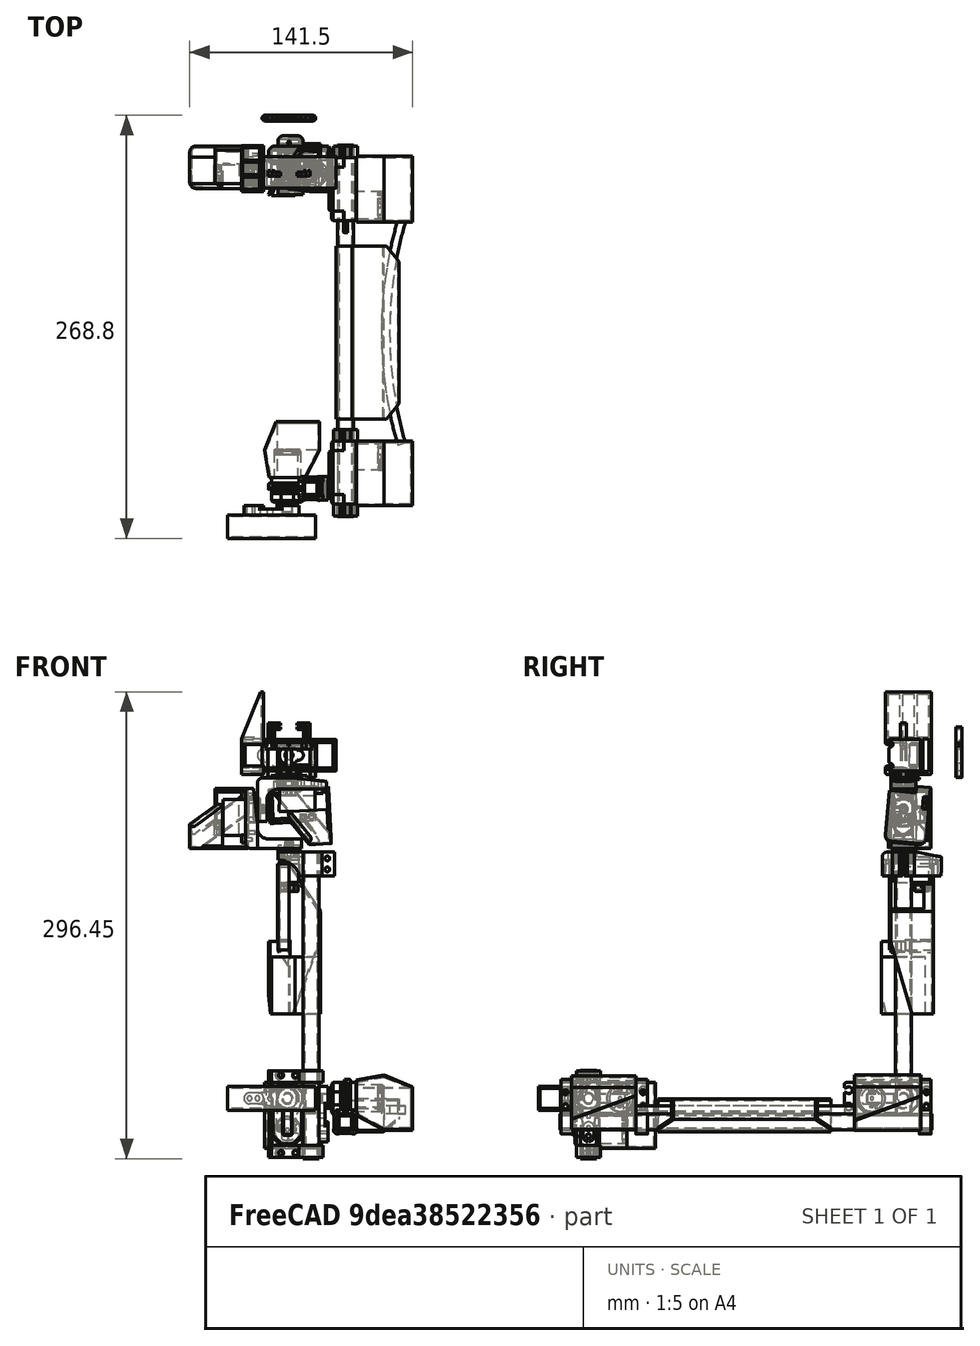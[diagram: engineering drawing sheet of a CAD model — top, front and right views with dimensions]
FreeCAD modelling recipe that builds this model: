
FCSTD DOCUMENT  (FreeCAD 0.19R22366 (Git))
Label: CompleteRobot
License: All rights reserved
LicenseURL: http://en.wikipedia.org/wiki/All_rights_reserved
objects: Sketcher::SketchObject×308, PartDesign::Pad×171, PartDesign::Pocket×133, PartDesign::Body×89, PartDesign::FeatureBase×47, PartDesign::Fillet×35, PartDesign::Mirrored×23, App::Part×12, PartDesign::Chamfer×10, PartDesign::PolarPattern×8, Part::Mirroring×8, PartDesign::Plane×7, PartDesign::MultiTransform×6, App::DocumentObjectGroup×4, PartDesign::Revolution×2, PartDesign::AdditiveLoft×1
note: 1200 computed .brp shape members not serialized (recipe doc carries the construction recipe); baked Part::Feature solids carry a one-line shape summary decoded from their .brp

FEATURE [Sketcher::SketchObject] Sketch
  MapMode = 5
  Support = -> [XY_Plane]
  constraints (7):
    c: Coincident(g0,g-1)
    c: PointOnObject(g1,g-1)
    c: Coincident(g1,g0)
    c: Coincident(g1,g0)
    c: Vertical(g1,g0)
    c: Diameter(g0) = 11.8
    c: Diameter(g1) = 5.5
FEATURE [PartDesign::Pad] Pad
  Length = 5.7
  Length2 = 100
  Profile = -> Sketch
  Refine = true
  Reversed = true
  Type = 0
FEATURE [Sketcher::SketchObject] Sketch001
  ExternalGeometry = -> [Pad]
  MapMode = 5
  Placement = pos=(0,0,-5.7) rot=(1,0,0;3.14159rad)
  Support = -> [Pad]
  constraints (11):
    c: Coincident(g0,g1)
    c: Coincident(g1,g2)
    c: Coincident(g2,g3)
    c: Coincident(g3,g0)
    c: Horizontal(g0)
    c: Horizontal(g2)
    c: Vertical(g3)
    c: Symmetric(g0,g1,g-1)
    c: Distance(g1) = 12
    c: DistanceX(g-1,g0) = 6
    c: Distance(g2) = 22.6
FEATURE [PartDesign::Plane] DatumPlane
  AttachmentOffset = pos=(0,0,16) rot=(0,0,1;0rad)
  Length = 60
  MapMode = 5
  Placement = pos=(0,0,-21.7) rot=(1,0,0;3.14159rad)
  ResizeMode = 0
  Support = -> [Pad]
  Width = 60
FEATURE [Sketcher::SketchObject] Sketch002
  ExternalGeometry = -> [Sketch001]
  MapMode = 5
  Placement = pos=(0,0,-21.7) rot=(1,0,0;3.14159rad)
  Support = -> [DatumPlane]
  constraints (18):
    c: Coincident(g0,g1)
    c: Coincident(g1,g2)
    c: Coincident(g2,g3)
    c: Coincident(g3,g0)
    c: Horizontal(g0)
    c: Horizontal(g2)
    c: Vertical(g3)
    c: Distance(g1) = 12.3
    c: Distance(g2) = 22.9
    c: PointOnObject(g4,g-1)
    c: PointOnObject(g5,g-3)
    c: Coincident(g5,g4)
    c: Horizontal(g5)
    c: PointOnObject(g4,g-4)
    c: Equal(g5,g4)
    c: Symmetric(g0,g1,g4)
    c: Horizontal(g4)
    c: Vertical(g1)
FEATURE [PartDesign::AdditiveLoft] AdditiveLoft
  BaseFeature = -> Pad
  Closed = false
  Profile = -> Sketch001
  Refine = true
  Ruled = false
  Sections = -> [Sketch002]
FEATURE [PartDesign::Plane] DatumPlane001
  AttachmentOffset = pos=(0,0,-1.7) rot=(0,0,1;0rad)
  Length = 60
  MapMode = 5
  Placement = pos=(0,0,-7.4) rot=(0,0,1;0rad)
  ResizeMode = 0
  Support = -> [AdditiveLoft]
  Width = 60
FEATURE [Sketcher::SketchObject] Sketch003
  ExternalGeometry = -> [AdditiveLoft]
  MapMode = 5
  Placement = pos=(0,0,-7.4) rot=(0,0,1;0rad)
  Support = -> [DatumPlane001]
  constraints (46):
    c: Coincident(g1,g2)
    c: Coincident(g2,g0)
    c: Horizontal(g0)
    c: Horizontal(g1)
    c: Coincident(g0,g-3)
    c: Coincident(g1,g-3)
    c: Distance(g0) = 5
    c: Coincident(g3,g4)
    c: Coincident(g4,g5)
    c: Horizontal(g3)
    c: Horizontal(g5)
    c: Coincident(g4,g-4)
    c: Coincident(g3,g-4)
    c: Equal(g3,g0)
    c: PointOnObject(g6,g-1)
    c: PointOnObject(g7,g-1)
    c: Vertical(g7,g7)
    c: Vertical(g6,g6)
    c: Coincident(g8,g7)
    c: Horizontal(g8)
    c: Coincident(g9,g8)
    c: Coincident(g9,g3)
    c: Coincident(g10,g7)
    c: Horizontal(g10)
    c: Coincident(g11,g10)
    c: Coincident(g11,g5)
    c: Vertical(g11)
    c: Vertical(g9)
    c: Vertical(g5,g3)
    c: Vertical(g0,g1)
    c: Coincident(g12,g6)
    c: Horizontal(g12)
    c: Coincident(g13,g0)
    c: Coincident(g13,g12)
    c: Coincident(g14,g1)
    c: Vertical(g14)
    c: Coincident(g15,g6)
    c: Horizontal(g15)
    c: Coincident(g14,g15)
    c: Vertical(g13)
    c: Equal(g6,g7)
    c: Equal(g12,g8)
    c: Diameter(g6) = 2
    c: Distance(g12) = 1.3
    c: DistanceY(g14,g12) = 1.2
    c: Horizontal(g7,g6)
FEATURE [PartDesign::Pad] Pad001
  BaseFeature = -> AdditiveLoft
  Length = 2.6
  Length2 = 100
  Profile = -> Sketch003
  Refine = true
  Reversed = true
  Type = 0
FEATURE [Sketcher::SketchObject] Sketch004
  MapMode = 5
  Support = -> [Pad001]
FEATURE [Sketcher::SketchObject] Sketch005
  MapMode = 5
  Support = -> [XY_Plane]
  constraints (2):
    c: Coincident(g0,g-1)
    c: Diameter(g0) = 4.95
FEATURE [PartDesign::Pad] Pad002
  BaseFeature = -> Pad001
  Length = 4.45
  Length2 = 100
  Profile = -> Sketch005
  Refine = true
  Type = 0
FEATURE [PartDesign::Chamfer] Chamfer
  Angle = 45
  Base = -> Pad002 [Edge69]
  BaseFeature = -> Pad002
  ChamferType = 1
  FlipDirection = false
  Refine = true
  Size = 0.45
  Size2 = 0.4
  SupportTransform = false
  expr: Size2 = (4.95 - 4.15) / 2
FEATURE [Sketcher::SketchObject] Sketch006
  ExternalGeometry = -> [Chamfer]
  MapMode = 5
  Support = -> [XY_Plane]
  expr: Constraints[4] = (4.95 - 4) / 2
  expr: Constraints[16] = 360 / 20
  constraints (25):
    c: PointOnObject(g0,g-3)
    c: Symmetric(g0,g1,g-1)
    c: PointOnObject(g2,g-1)
    c: PointOnObject(g2,g-3)
    c: DistanceX(g0,g2) = 0.475
    c: Coincident(g3,g0)
    c: Coincident(g3,g1)
    c: Symmetric(g0,g1,g-1)
    c: Distance(g3) = 0.12
    c: Coincident(g4,g0)
    c: PointOnObject(g4,g-3)
    c: Equal(g4,g3)
    c: Coincident(g5,g1)
    c: Coincident(g5,g-1)
    c: Coincident(g6,g-1)
    c: Coincident(g6,g4)
    c: Angle(g5,g6) = 0.314159
    c: Coincident(g7,g4)
    c: Coincident(g8,g1)
    c: Parallel(g7,g6)
    c: Parallel(g8,g5)
    c: Coincident(g9,g-1)
    c: Coincident(g9,g7)
    c: Coincident(g9,g8)
    c: Distance(g7) = 0.1
FEATURE [PartDesign::Pocket] Pocket
  BaseFeature = -> Chamfer
  Length = 5
  Length2 = 100
  Profile = -> Sketch006
  Refine = true
  Reversed = true
  Type = 1
FEATURE [PartDesign::PolarPattern] PolarPattern
  Angle = 360
  Axis = -> Sketch006 [N_Axis]
  BaseFeature = -> Pocket
  Occurrences = 20
  Originals = -> [Pocket]
  Refine = true
FEATURE [Sketcher::SketchObject] Sketch007
  MapMode = 5
  Placement = pos=(0,0,4.45) rot=(0,0,1;0rad)
  Support = -> [PolarPattern]
  constraints (2):
    c: Coincident(g0,g-1)
    c: Diameter(g0) = 2
FEATURE [PartDesign::Pocket] Pocket001
  BaseFeature = -> PolarPattern
  Length = 4
  Length2 = 100
  Profile = -> Sketch007
  Refine = true
  Type = 0
FEATURE [PartDesign::Fillet] Fillet
  Base = -> Pocket001 [Edge3,Edge5]
  BaseFeature = -> Pocket001
  Radius = 0.4
  Refine = true
  SupportTransform = false
FEATURE [Sketcher::SketchObject] Sketch008
  ExternalGeometry = -> [Fillet]
  MapMode = 5
  Placement = pos=(0,0,-21.7) rot=(1,0,0;3.14159rad)
  Support = -> [Fillet]
  constraints (18):
    c: Coincident(g0,g1)
    c: Coincident(g1,g2)
    c: Coincident(g2,g3)
    c: Coincident(g3,g0)
    c: Horizontal(g2)
    c: Vertical(g3)
    c: Coincident(g4,g-3)
    c: Coincident(g4,g-4)
    c: Vertical(g1)
    c: PointOnObject(g5,g4)
    c: PointOnObject(g5,g-1)
    c: PointOnObject(g6,g0)
    c: PointOnObject(g6,g2)
    c: PointOnObject(g5,g6)
    c: Symmetric(g6,g6,g-1)
    c: Symmetric(g0,g0,g6)
    c: Distance(g0) = 22
    c: Distance(g1) = 11.4
FEATURE [PartDesign::Pocket] Pocket002
  BaseFeature = -> Fillet
  Length = 10
  Length2 = 100
  Profile = -> Sketch008
  Refine = true
  Type = 0
FEATURE [PartDesign::Body] Body
  Group = -> [Sketch,Pad,Sketch001,DatumPlane,Sketch002,AdditiveLoft,DatumPlane001,Sketch003,Pad001,Sketch004,Sketch005,Pad002,Chamfer,Sketch006,Pocket,PolarPattern,Sketch007,Pocket001,Fillet,Sketch008,Pocket002]
  Origin = -> Origin
  Tip = -> Pocket002
FEATURE [PartDesign::FeatureBase] Clone
  BaseFeature = -> Body
FEATURE [PartDesign::Body] Body001
  BaseFeature = -> Body
  Group = -> [Clone]
  Origin = -> Origin001
  Placement = pos=(0,0,0) rot=(0,0,1;3.14159rad)
  Tip = -> Clone
FEATURE [PartDesign::FeatureBase] Clone001
  BaseFeature = -> Body
FEATURE [PartDesign::Body] Body002
  BaseFeature = -> Body
  Group = -> [Clone001]
  Origin = -> Origin002
  Placement = pos=(-20,0,-20) rot=(0.707107,0,0.707107;3.14159rad)
  Tip = -> Clone001
FEATURE [PartDesign::FeatureBase] Clone002
  BaseFeature = -> Body
FEATURE [PartDesign::Body] Body003
  BaseFeature = -> Body
  Group = -> [Clone002]
  Origin = -> Origin003
  Placement = pos=(0,0,-45) rot=(0,0,-1;1.5708rad)
  Tip = -> Clone002
FEATURE [Sketcher::SketchObject] Sketch009
  MapMode = 5
  Support = -> [XY_Plane004]
  expr: Constraints[2] = 11.8 + 4
  sketch-geometry (2):
    g0: Circle CenterX=0 CenterY=0 CenterZ=0 NormalX=0 NormalY=0 NormalZ=1 AngleXU=0 Radius=7.9
    g1: Circle CenterX=0 CenterY=0 CenterZ=0 NormalX=0 NormalY=0 NormalZ=1 AngleXU=0 Radius=2.55
  constraints (4):
    c: Coincident(g0,g-1)
    c: Coincident(g1,g0)
    c: Diameter(g0) = 15.8
    c: Diameter(g1) = 5.1
FEATURE [PartDesign::Pad] Pad003
  Length = 5
  Length2 = 100
  Profile = -> Sketch009
  Refine = true
  Type = 0
FEATURE [Sketcher::SketchObject] Sketch010
  ExternalGeometry = -> [Pad003]
  MapMode = 5
  Placement = pos=(0,0,5) rot=(0,0,1;0rad)
  Support = -> [Pad003]
  expr: Constraints[10] = 5.1 / 2 - 0.5 / 2
  expr: Constraints[16] = 360 / 20
  sketch-geometry (8):
    g0: ArcOfCircle CenterX=2.3 CenterY=0 CenterZ=0 NormalX=0 NormalY=0 NormalZ=1 AngleXU=0 Radius=0.2 StartAngle=1.57427 EndAngle=4.70891
    g1: LineSegment StartX=2.2993 StartY=0.199999 StartZ=0 EndX=2.3193 EndY=0.200068 EndZ=0
    g2: LineSegment StartX=2.2993 StartY=-0.199999 StartZ=0 EndX=2.3193 EndY=-0.200068 EndZ=0
    g3: ArcOfCircle CenterX=2.31861 CenterY=0.400067 CenterZ=0 NormalX=0 NormalY=0 NormalZ=1 AngleXU=0 Radius=0.2 StartAngle=4.71587 EndAngle=6.27739
    g4: ArcOfCircle CenterX=2.31861 CenterY=-0.400067 CenterZ=0 NormalX=0 NormalY=0 NormalZ=1 AngleXU=0 Radius=0.2 StartAngle=0.00579632 EndAngle=1.56732
    g5: LineSegment [constr] StartX=0 StartY=0 StartZ=0 EndX=2.51861 EndY=0.398908 EndZ=0
    g6: LineSegment [constr] StartX=0 StartY=0 StartZ=0 EndX=2.51861 EndY=-0.398908 EndZ=0
    g7: ArcOfCircle CenterX=0 CenterY=0 CenterZ=0 NormalX=0 NormalY=0 NormalZ=1 AngleXU=0 Radius=2.55 StartAngle=6.12611 EndAngle=6.44026
  constraints (21):
    c: PointOnObject(g0,g-1)
    c: Vertical(g0,g0)
    c: Diameter(g0) = 0.4
    c: Tangent(g2,g0) = -1.5708
    c: Tangent(g1,g0) = 1.5708
    c: PointOnObject(g4,g-3)
    c: Tangent(g4,g2) = 1.5708
    c: Tangent(g3,g1) = -1.5708
    c: Equal(g3,g0)
    c: Equal(g4,g0)
    c: DistanceX(g0) = 2.3
    c: Coincident(g5,g-1)
    c: Coincident(g5,g3)
    c: Coincident(g6,g-1)
    c: Coincident(g6,g4)
    c: Vertical(g4,g3)
    c: Angle(g6,g5) = 0.314159
    c: Coincident(g7,g-1)
    c: Coincident(g7,g3)
    c: Coincident(g7,g4)
    c: Distance(g1) = 0.02
FEATURE [PartDesign::Pad] Pad004
  BaseFeature = -> Pad003
  Length = 10
  Length2 = 100
  Profile = -> Sketch010
  Refine = true
  Reversed = true
  Type = 3
  UpToFace = -> Pad003 [Face3]
FEATURE [PartDesign::PolarPattern] PolarPattern001
  Angle = 360
  Axis = -> Sketch010 [N_Axis]
  BaseFeature = -> Pad004
  Occurrences = 20
  Originals = -> [Pad004]
  Refine = true
FEATURE [Sketcher::SketchObject] Sketch011
  ExternalGeometry = -> [PolarPattern001]
  MapMode = 5
  Placement = pos=(0,0,5) rot=(0,0,1;0rad)
  Support = -> [PolarPattern001]
  sketch-geometry (2):
    g0: Circle CenterX=0 CenterY=0 CenterZ=0 NormalX=0 NormalY=0 NormalZ=1 AngleXU=0 Radius=1.3
    g1: Circle CenterX=0 CenterY=0 CenterZ=0 NormalX=0 NormalY=0 NormalZ=1 AngleXU=0 Radius=7.9
  constraints (4):
    c: Coincident(g0,g-1)
    c: Diameter(g0) = 2.6
    c: Coincident(g1,g0)
    c: Equal(g-3,g1)
FEATURE [PartDesign::Pad] Pad005
  BaseFeature = -> PolarPattern001
  Length = 1
  Length2 = 100
  Profile = -> Sketch011
  Refine = true
  Type = 0
FEATURE [PartDesign::Plane] DatumPlane002
  AttachmentOffset = pos=(0,0,-20) rot=(0,0,1;0rad)
  Length = 61.225
  MapMode = 5
  Placement = pos=(-20,4.4e-15,-4.4e-15) rot=(0.57735,0.57735,0.57735;2.0944rad)
  ResizeMode = 0
  Support = -> [YZ_Plane004]
  Width = 74.225
FEATURE [Sketcher::SketchObject] Sketch012
  ExternalGeometry = -> [Pad005]
  MapMode = 5
  Placement = pos=(-20,4.4e-15,-4.4e-15) rot=(0.57735,0.57735,0.57735;2.0944rad)
  Support = -> [DatumPlane002]
  sketch-geometry (4):
    g0: LineSegment StartX=-7.9 StartY=6 StartZ=0 EndX=7.9 EndY=6 EndZ=0
    g1: LineSegment StartX=7.9 StartY=6 StartZ=0 EndX=7.9 EndY=0 EndZ=0
    g2: LineSegment StartX=7.9 StartY=0 StartZ=0 EndX=-7.9 EndY=0 EndZ=0
    g3: LineSegment StartX=-7.9 StartY=0 StartZ=0 EndX=-7.9 EndY=6 EndZ=0
  constraints (10):
    c: Coincident(g0,g1)
    c: Coincident(g1,g2)
    c: Coincident(g2,g3)
    c: Coincident(g3,g0)
    c: Horizontal(g0)
    c: Horizontal(g2)
    c: Vertical(g1)
    c: Vertical(g3)
    c: Symmetric(g2,g1,g-1)
    c: Coincident(g0,g-3)
FEATURE [PartDesign::Pad] Pad006
  BaseFeature = -> Pad005
  Length = 10
  Length2 = 100
  Profile = -> Sketch012
  Refine = true
  Type = 2
FEATURE [Sketcher::SketchObject] Sketch013
  MapMode = 5
  Placement = pos=(-20,0,0) rot=(0.57735,-0.57735,-0.57735;2.0944rad)
  Support = -> [Pad006]
  sketch-geometry (4):
    g0: LineSegment StartX=-8 StartY=0 StartZ=0 EndX=8 EndY=0 EndZ=0
    g1: LineSegment StartX=8 StartY=0 StartZ=0 EndX=8 EndY=38 EndZ=0
    g2: LineSegment StartX=8 StartY=38 StartZ=0 EndX=-8 EndY=38 EndZ=0
    g3: LineSegment StartX=-8 StartY=38 StartZ=0 EndX=-8 EndY=0 EndZ=0
  constraints (11):
    c: Coincident(g0,g1)
    c: Coincident(g1,g2)
    c: Coincident(g2,g3)
    c: Coincident(g3,g0)
    c: Horizontal(g0)
    c: Horizontal(g2)
    c: Vertical(g1)
    c: Vertical(g3)
    c: Symmetric(g0,g0,g-1)
    c: Distance(g2) = 16
    c: Distance(g1) = 38
FEATURE [PartDesign::Pad] Pad007
  BaseFeature = -> Pad006
  Length = 7.4
  Length2 = 100
  Profile = -> Sketch013
  Refine = true
  Type = 0
FEATURE [Sketcher::SketchObject] Sketch014
  MapMode = 5
  Placement = pos=(-20,0,0) rot=(0.57735,0.57735,0.57735;2.0944rad)
  Support = -> [Pad007]
  sketch-geometry (2):
    g0: ArcOfCircle CenterX=0 CenterY=25 CenterZ=0 NormalX=0 NormalY=0 NormalZ=1 AngleXU=0 Radius=6.3 StartAngle=5.23599 EndAngle=10.472
    g1: ArcOfCircle CenterX=0 CenterY=19.544 CenterZ=0 NormalX=0 NormalY=0 NormalZ=1 AngleXU=0 Radius=3.15 StartAngle=3.14159 EndAngle=6.28319
  constraints (8):
    c: PointOnObject(g0,g-2)
    c: PointOnObject(g1,g-2)
    c: Coincident(g1,g0)
    c: Coincident(g1,g0)
    c: Horizontal(g0,g1)
    c: Diameter(g0) = 12.6
    c: DistanceY(g0) = 25
    c: Diameter(g1) = 6.3
FEATURE [PartDesign::Pocket] Pocket003
  BaseFeature = -> Pad007
  Length = 5
  Length2 = 100
  Profile = -> Sketch014
  Refine = true
  Type = 1
FEATURE [Sketcher::SketchObject] Sketch015
  MapMode = 5
  Placement = pos=(-27.4,0,0) rot=(0.57735,-0.57735,-0.57735;2.0944rad)
  Support = -> [Pocket003]
  sketch-geometry (4):
    g0: LineSegment StartX=-6.405 StartY=31.9 StartZ=0 EndX=6.405 EndY=31.9 EndZ=0
    g1: LineSegment StartX=6.405 StartY=31.9 StartZ=0 EndX=6.405 EndY=7.9 EndZ=0
    g2: LineSegment StartX=6.405 StartY=7.9 StartZ=0 EndX=-6.405 EndY=7.9 EndZ=0
    g3: LineSegment StartX=-6.405 StartY=7.9 StartZ=0 EndX=-6.405 EndY=31.9 EndZ=0
  constraints (11):
    c: Coincident(g0,g1)
    c: Coincident(g1,g2)
    c: Coincident(g2,g3)
    c: Coincident(g3,g0)
    c: Horizontal(g2)
    c: Vertical(g1)
    c: Vertical(g3)
    c: Symmetric(g0,g0,g-2)
    c: Distance(g0) = 12.81
    c: Distance(g1) = 24
    c: DistanceY(g2) = 7.9
FEATURE [PartDesign::Pocket] Pocket004
  BaseFeature = -> Pocket003
  Length = 1.9
  Length2 = 100
  Profile = -> Sketch015
  Refine = true
  Type = 0
FEATURE [Sketcher::SketchObject] Sketch016
  MapMode = 5
  Placement = pos=(-27.4,0,0) rot=(0.57735,-0.57735,-0.57735;2.0944rad)
  Support = -> [Pocket004]
  sketch-geometry (2):
    g0: Circle CenterX=0 CenterY=33.9 CenterZ=0 NormalX=0 NormalY=0 NormalZ=1 AngleXU=0 Radius=1
    g1: Circle CenterX=0 CenterY=5.5 CenterZ=0 NormalX=0 NormalY=0 NormalZ=1 AngleXU=0 Radius=1
  constraints (6):
    c: PointOnObject(g0,g-2)
    c: PointOnObject(g1,g-2)
    c: Diameter(g0) = 2
    c: Equal(g1,g0)
    c: DistanceY(g1) = 5.5
    c: DistanceY(g1,g0) = 28.4
FEATURE [PartDesign::Pocket] Pocket005
  BaseFeature = -> Pocket004
  Length = 4
  Length2 = 100
  Profile = -> Sketch016
  Refine = true
  Type = 0
FEATURE [Sketcher::SketchObject] Sketch017
  ExternalGeometry = -> [Pocket005]
  MapMode = 5
  Placement = pos=(0,8,0) rot=(0,0.707107,0.707107;3.14159rad)
  Support = -> [Pocket005]
  sketch-geometry (3):
    g0: LineSegment StartX=20 StartY=15 StartZ=0 EndX=22.5 EndY=38 EndZ=0
    g1: LineSegment StartX=20 StartY=38 StartZ=0 EndX=22.5 EndY=38 EndZ=0
    g2: LineSegment StartX=20 StartY=38 StartZ=0 EndX=20 EndY=15 EndZ=0
  constraints (8):
    c: PointOnObject(g0,g-3)
    c: Coincident(g1,g-3)
    c: Coincident(g1,g0)
    c: Horizontal(g1)
    c: Coincident(g2,g1)
    c: Coincident(g2,g0)
    c: Distance(g1) = 2.5
    c: Distance(g2) = 23
FEATURE [PartDesign::Pocket] Pocket006
  BaseFeature = -> Pocket005
  Length = 5
  Length2 = 100
  Profile = -> Sketch017
  Refine = true
  Type = 1
FEATURE [PartDesign::Fillet] Fillet001
  Base = -> Pocket006 [Edge317]
  BaseFeature = -> Pocket006
  Radius = 10
  Refine = true
  SupportTransform = false
FEATURE [PartDesign::Chamfer] Chamfer001
  Angle = 45
  Base = -> Fillet001 [Edge21,Edge18]
  BaseFeature = -> Fillet001
  ChamferType = 0
  FlipDirection = false
  Refine = true
  Size = 0.05
  Size2 = 10
  SupportTransform = false
FEATURE [PartDesign::Fillet] Fillet002
  Base = -> Chamfer001 [Edge6]
  BaseFeature = -> Chamfer001
  Radius = 7
  Refine = true
  SupportTransform = false
FEATURE [PartDesign::Fillet] Fillet003
  Base = -> Fillet002 [Edge18]
  BaseFeature = -> Fillet002
  Radius = 3
  Refine = true
  SupportTransform = false
FEATURE [PartDesign::Fillet] Fillet004
  Base = -> Fillet003 [Edge114,Edge129]
  BaseFeature = -> Fillet003
  Radius = 6
  Refine = true
  SupportTransform = false
FEATURE [Sketcher::SketchObject] Sketch018
  ExternalGeometry = -> [Sketch015]
  MapMode = 5
  Placement = pos=(-25.5,0,0) rot=(0.57735,-0.57735,-0.57735;2.0944rad)
  Support = -> [Fillet004]
  sketch-geometry (10):
    g0: Circle CenterX=4.5 CenterY=29.9 CenterZ=0 NormalX=0 NormalY=0 NormalZ=1 AngleXU=0 Radius=1
    g1: Circle CenterX=-4.5 CenterY=29.9 CenterZ=0 NormalX=0 NormalY=0 NormalZ=1 AngleXU=0 Radius=1
    g2: Circle CenterX=4.5 CenterY=9.9 CenterZ=0 NormalX=0 NormalY=0 NormalZ=1 AngleXU=0 Radius=1
    g3: Circle CenterX=-4.5 CenterY=9.9 CenterZ=0 NormalX=0 NormalY=0 NormalZ=1 AngleXU=0 Radius=1
    g4: LineSegment [constr] StartX=-4.5 StartY=29.9 StartZ=0 EndX=4.5 EndY=29.9 EndZ=0
    g5: LineSegment [constr] StartX=-4.5 StartY=29.9 StartZ=0 EndX=-4.5 EndY=9.9 EndZ=0
    g6: LineSegment [constr] StartX=-4.5 StartY=9.9 StartZ=0 EndX=4.5 EndY=9.9 EndZ=0
    g7: LineSegment [constr] StartX=4.5 StartY=29.9 StartZ=0 EndX=4.5 EndY=9.9 EndZ=0
    g8: LineSegment [constr] StartX=-6.405 StartY=31.9 StartZ=0 EndX=0 EndY=19.9 EndZ=0
    g9: LineSegment [constr] StartX=0 StartY=19.9 StartZ=0 EndX=6.405 EndY=7.9 EndZ=0
  constraints (24):
    c: Diameter(g0) = 2
    c: Coincident(g4,g1)
    c: Coincident(g4,g0)
    c: Horizontal(g4)
    c: Coincident(g5,g1)
    c: Coincident(g5,g3)
    c: Vertical(g5)
    c: Coincident(g6,g3)
    c: Coincident(g6,g2)
    c: Horizontal(g6)
    c: Coincident(g7,g0)
    c: Coincident(g7,g2)
    c: Vertical(g7)
    c: Coincident(g8,g-3)
    c: Coincident(g9,g8)
    c: Coincident(g9,g-4)
    c: Equal(g8,g9)
    c: Parallel(g8,g9)
    c: Symmetric(g0,g3,g8)
    c: Distance(g5) = 20
    c: Distance(g4) = 9
    c: Equal(g1,g3)
    c: Equal(g3,g2)
    c: Equal(g2,g0)
FEATURE [PartDesign::Pocket] Pocket007
  BaseFeature = -> Fillet004
  Length = 4
  Length2 = 100
  Profile = -> Sketch018
  Refine = true
  Type = 0
FEATURE [Sketcher::SketchObject] Sketch020
  ExternalGeometry = -> [Pocket007]
  MapMode = 5
  Placement = pos=(0,0,-1.2e-15) rot=(1,0,0;3.14159rad)
  Support = -> [Pocket007]
  sketch-geometry (1):
    g0: Circle CenterX=0 CenterY=0 CenterZ=0 NormalX=0 NormalY=0 NormalZ=1 AngleXU=0 Radius=2.55
  constraints (2):
    c: Coincident(g0,g-1)
    c: PointOnObject(g-3,g0)
FEATURE [PartDesign::Pocket] Pocket008
  BaseFeature = -> Pocket007
  Length = 2
  Length2 = 100
  Profile = -> Sketch020
  Refine = true
  Type = 0
FEATURE [Sketcher::SketchObject] Sketch021
  ExternalGeometry = -> [Pocket008]
  MapMode = 5
  Placement = pos=(-25.5,0,0) rot=(0.57735,-0.57735,-0.57735;2.0944rad)
  Support = -> [Pocket008]
  sketch-geometry (6):
    g0: ArcOfCircle CenterX=0 CenterY=25 CenterZ=0 NormalX=0 NormalY=0 NormalZ=1 AngleXU=0 Radius=6.3 StartAngle=0.972582 EndAngle=2.16901
    g1: ArcOfCircle CenterX=0 CenterY=25 CenterZ=0 NormalX=0 NormalY=0 NormalZ=1 AngleXU=0 Radius=6.7 StartAngle=0.961287 EndAngle=2.18031
    g2: LineSegment StartX=-3.83552 StartY=30.4935 StartZ=0 EndX=-3.54796 EndY=30.206 EndZ=0
    g3: LineSegment StartX=3.83552 StartY=30.4935 StartZ=0 EndX=3.54796 EndY=30.206 EndZ=0
    g4: GeomPoint X=0 Y=31.3 Z=0
    g5: GeomPoint X=0 Y=31.7 Z=0
  constraints (15):
    c: Coincident(g0,g-3)
    c: Coincident(g0,g-3)
    c: Coincident(g0,g-3)
    c: Coincident(g1,g0)
    c: Coincident(g2,g1)
    c: Coincident(g2,g0)
    c: Coincident(g3,g1)
    c: Coincident(g3,g0)
    c: Horizontal(g1,g1)
    c: Perpendicular(g3,g2)
    c: PointOnObject(g4,g-2)
    c: PointOnObject(g5,g-2)
    c: PointOnObject(g5,g1)
    c: PointOnObject(g4,g0)
    c: DistanceY(g4,g5) = 0.4
FEATURE [PartDesign::Pocket] Pocket009
  BaseFeature = -> Pocket008
  Length = 5
  Length2 = 100
  Profile = -> Sketch021
  Refine = true
  Type = 1
FEATURE [Sketcher::SketchObject] Sketch022
  ExternalGeometry = -> [Pocket009]
  MapMode = 5
  Placement = pos=(0,0,0) rot=(1,0,0;1.5708rad)
  Support = -> [XZ_Plane004]
  sketch-geometry (4):
    g0: LineSegment StartX=1.90556 StartY=5 StartZ=0 EndX=2.55 EndY=4.275 EndZ=0
    g1: GeomPoint X=2.15 Y=4.725 Z=0
    g2: LineSegment StartX=2.55 StartY=4.275 StartZ=0 EndX=2.55 EndY=5 EndZ=0
    g3: LineSegment StartX=1.90556 StartY=5 StartZ=0 EndX=2.55 EndY=5 EndZ=0
  constraints (11):
    c: PointOnObject(g0,g-3)
    c: Vertical(g-4,g0)
    c: PointOnObject(g1,g0)
    c: DistanceY(g0,g1) = 0.45
    c: DistanceY(g1,g0) = 0.275
    c: DistanceX(g1,g0) = 0.4
    c: Coincident(g2,g0)
    c: Vertical(g2)
    c: Coincident(g3,g0)
    c: Coincident(g3,g2)
    c: Horizontal(g3)
FEATURE [PartDesign::Revolution] Revolution
  Angle = 360
  Axis = (0,-2e-16,1)
  Base = (0,0,0)
  BaseFeature = -> Pocket009
  Profile = -> Sketch022
  ReferenceAxis = -> Sketch022 [V_Axis]
  Refine = true
FEATURE [Sketcher::SketchObject] Sketch043
  MapMode = 5
  Placement = pos=(0,0,-1.2e-15) rot=(1,0,0;3.14159rad)
  Support = -> [Revolution]
  expr: Constraints[1] = 11.8 + 2
  sketch-geometry (1):
    g0: Circle CenterX=0 CenterY=0 CenterZ=0 NormalX=0 NormalY=0 NormalZ=1 AngleXU=0 Radius=6.9
  constraints (2):
    c: Coincident(g0,g-1)
    c: Diameter(g0) = 13.8
FEATURE [PartDesign::Pocket] Pocket019
  BaseFeature = -> Revolution
  Length = 1.8
  Length2 = 100
  Profile = -> Sketch043
  Refine = true
  Type = 0
FEATURE [Sketcher::SketchObject] Sketch044
  MapMode = 5
  Support = -> [XY_Plane006]
  expr: Constraints[1] = 11.8 + 2 - 0.1
  sketch-geometry (2):
    g0: Circle CenterX=0 CenterY=0 CenterZ=0 NormalX=0 NormalY=0 NormalZ=1 AngleXU=0 Radius=6.85
    g1: Circle CenterX=0 CenterY=0 CenterZ=0 NormalX=0 NormalY=0 NormalZ=1 AngleXU=0 Radius=3
  constraints (4):
    c: Coincident(g0,g-1)
    c: Diameter(g0) = 13.7
    c: Coincident(g1,g0)
    c: Diameter(g1) = 6
FEATURE [PartDesign::Pad] Pad014
  Length = 1.8
  Length2 = 100
  Profile = -> Sketch044
  Refine = true
  Type = 0
FEATURE [Sketcher::SketchObject] Sketch045
  ExternalGeometry = -> [Pad014]
  MapMode = 5
  Placement = pos=(0,0,0) rot=(1,0,0;3.14159rad)
  Support = -> [Pad014]
  sketch-geometry (4):
    g0: ArcOfCircle CenterX=0 CenterY=0 CenterZ=0 NormalX=0 NormalY=0 NormalZ=1 AngleXU=0 Radius=6.85 StartAngle=5.23599 EndAngle=10.472
    g1: ArcOfCircle CenterX=0 CenterY=0 CenterZ=0 NormalX=0 NormalY=0 NormalZ=1 AngleXU=0 Radius=5.85 StartAngle=5.23599 EndAngle=10.472
    g2: LineSegment StartX=-2.925 StartY=-5.06625 StartZ=0 EndX=-3.425 EndY=-5.93227 EndZ=0
    g3: LineSegment StartX=2.925 StartY=-5.06625 StartZ=0 EndX=3.425 EndY=-5.93227 EndZ=0
  constraints (12):
    c: Coincident(g0,g-1)
    c: Coincident(g1,g0)
    c: Coincident(g2,g1)
    c: Coincident(g2,g0)
    c: Coincident(g3,g1)
    c: Coincident(g3,g0)
    c: Perpendicular(g0,g3)
    c: Perpendicular(g0,g2)
    c: Horizontal(g0,g0)
    c: Diameter(g1) = 11.7
    c: Angle(g2,g3) = 1.0472
    c: Equal(g-3,g0)
FEATURE [PartDesign::Pad] Pad015
  BaseFeature = -> Pad014
  Length = 2
  Length2 = 100
  Profile = -> Sketch045
  Refine = true
  Type = 0
FEATURE [Sketcher::SketchObject] Sketch046
  MapMode = 5
  Support = -> [XY_Plane006]
  sketch-geometry (2):
    g0: Circle CenterX=4.5 CenterY=-5 CenterZ=0 NormalX=0 NormalY=0 NormalZ=1 AngleXU=0 Radius=1
    g1: Circle CenterX=-4.5 CenterY=-5 CenterZ=0 NormalX=0 NormalY=0 NormalZ=1 AngleXU=0 Radius=1
  constraints (5):
    c: Equal(g1,g0)
    c: Symmetric(g1,g0,g-2)
    c: Diameter(g0) = 2
    c: DistanceX(g0) = 4.5
    c: DistanceY(g0) = -5
FEATURE [PartDesign::Pocket] Pocket020
  BaseFeature = -> Pad015
  Length = 5
  Length2 = 100
  Profile = -> Sketch046
  Refine = true
  Type = 1
FEATURE [PartDesign::Body] Body006  label="s4Bushing"
  Group = -> [Sketch044,Pad014,Sketch045,Pad015,Sketch046,Pocket020]
  Origin = -> Origin006
  Placement = pos=(0,0,-45) rot=(0,0,1;0rad)
  Tip = -> Pocket020
FEATURE [Sketcher::SketchObject] Sketch047
  MapMode = 5
  Support = -> [XY_Plane007]
  sketch-geometry (2):
    g0: Circle CenterX=4.5 CenterY=-4.9 CenterZ=0 NormalX=0 NormalY=0 NormalZ=1 AngleXU=0 Radius=1
    g1: Circle CenterX=-4.5 CenterY=-4.9 CenterZ=0 NormalX=0 NormalY=0 NormalZ=1 AngleXU=0 Radius=1
  constraints (5):
    c: Equal(g1,g0)
    c: Symmetric(g1,g0,g-2)
    c: Diameter(g0) = 2
    c: DistanceX(g0) = 4.5
    c: DistanceY(g0) = -4.9
FEATURE [Sketcher::SketchObject] Sketch049
  MapMode = 5
  Support = -> [XY_Plane007]
  expr: Constraints[1] = 11.8 + 2 - 0.1
  sketch-geometry (2):
    g0: Circle CenterX=0 CenterY=0 CenterZ=0 NormalX=0 NormalY=0 NormalZ=1 AngleXU=0 Radius=6.85
    g1: Circle CenterX=0 CenterY=0 CenterZ=0 NormalX=0 NormalY=0 NormalZ=1 AngleXU=0 Radius=3
  constraints (4):
    c: Coincident(g0,g-1)
    c: Diameter(g0) = 13.7
    c: Coincident(g1,g0)
    c: Diameter(g1) = 6
FEATURE [PartDesign::Pad] Pad016
  Length = 1.8
  Length2 = 100
  Profile = -> Sketch049
  Refine = true
  Type = 0
FEATURE [Sketcher::SketchObject] Sketch048
  ExternalGeometry = -> [Pad016]
  MapMode = 5
  Placement = pos=(0,0,0) rot=(1,0,0;3.14159rad)
  Support = -> [Pad016]
  sketch-geometry (4):
    g0: ArcOfCircle CenterX=0 CenterY=0 CenterZ=0 NormalX=0 NormalY=0 NormalZ=1 AngleXU=0 Radius=6.85 StartAngle=5.23599 EndAngle=10.472
    g1: ArcOfCircle CenterX=0 CenterY=0 CenterZ=0 NormalX=0 NormalY=0 NormalZ=1 AngleXU=0 Radius=5.85 StartAngle=5.23599 EndAngle=10.472
    g2: LineSegment StartX=-2.925 StartY=-5.06625 StartZ=0 EndX=-3.425 EndY=-5.93227 EndZ=0
    g3: LineSegment StartX=2.925 StartY=-5.06625 StartZ=0 EndX=3.425 EndY=-5.93227 EndZ=0
  constraints (12):
    c: Coincident(g0,g-1)
    c: Coincident(g1,g0)
    c: Coincident(g2,g1)
    c: Coincident(g2,g0)
    c: Coincident(g3,g1)
    c: Coincident(g3,g0)
    c: Perpendicular(g0,g3)
    c: Perpendicular(g0,g2)
    c: Horizontal(g0,g0)
    c: Diameter(g1) = 11.7
    c: Angle(g2,g3) = 1.0472
    c: Equal(g-3,g0)
FEATURE [PartDesign::Pad] Pad017
  BaseFeature = -> Pad016
  Length = 2
  Length2 = 100
  Profile = -> Sketch048
  Refine = true
  Type = 0
FEATURE [PartDesign::Pocket] Pocket021
  BaseFeature = -> Pad017
  Length = 5
  Length2 = 100
  Profile = -> Sketch047
  Refine = true
  Type = 1
FEATURE [PartDesign::Body] Body007  label="s5Bushing"
  Group = -> [Sketch049,Pad016,Sketch048,Pad017,Sketch047,Pocket021]
  Origin = -> Origin007
  Placement = pos=(-20,0,-20) rot=(0.57735,-0.57735,0.57735;4.18879rad)
  Tip = -> Pocket021
FEATURE [Sketcher::SketchObject] Sketch050
  MapMode = 5
  Placement = pos=(0,0,0) rot=(0.57735,0.57735,0.57735;2.0944rad)
  Support = -> [YZ_Plane004]
  sketch-geometry (1):
    g0: Circle CenterX=0 CenterY=25 CenterZ=0 NormalX=0 NormalY=0 NormalZ=1 AngleXU=0 Radius=7.5
  constraints (3):
    c: PointOnObject(g0,g-2)
    c: DistanceY(g0) = 25
    c: Diameter(g0) = 15
FEATURE [PartDesign::Pocket] Pocket022
  BaseFeature = -> Pocket019
  Length = 22.5
  Length2 = 100
  Profile = -> Sketch050
  Refine = true
  Type = 0
FEATURE [PartDesign::Body] Body004  label="s5Mount"
  Group = -> [Sketch009,Pad003,Sketch010,Pad004,PolarPattern001,Sketch011,Pad005,DatumPlane002,Sketch012,Pad006,Sketch013,Pad007,Sketch014,Pocket003,Sketch015,Pocket004,Sketch016,Pocket005,Sketch017,Pocket006,Fillet001,Chamfer001,Fillet002,Fillet003,Fillet004,Sketch018,Pocket007,Sketch020,Pocket008,Sketch021,Pocket009,Sketch022,Revolution,Sketch043,Pocket019,Sketch050,Pocket022]
  Origin = -> Origin004
  Placement = pos=(0,0,-45) rot=(0,0,1;0rad)
  Tip = -> Pocket022
FEATURE [Sketcher::SketchObject] Sketch052
  MapMode = 5
  Support = -> [XY_Plane008]
  sketch-geometry (2):
    g0: Circle CenterX=0 CenterY=0 CenterZ=0 NormalX=0 NormalY=0 NormalZ=1 AngleXU=0 Radius=2.6
    g1: Circle CenterX=0 CenterY=0 CenterZ=0 NormalX=0 NormalY=0 NormalZ=1 AngleXU=0 Radius=6.15
  constraints (4):
    c: Coincident(g0,g-1)
    c: Coincident(g1,g0)
    c: Diameter(g0) = 5.2
    c: Diameter(g1) = 12.3
FEATURE [PartDesign::Pad] Pad018
  Length = 5.15
  Length2 = 100
  Profile = -> Sketch052
  Type = 0
  expr: Length = 4.45 + 0.2 + 0.5
FEATURE [Sketcher::SketchObject] Sketch053
  MapMode = 5
  Placement = pos=(0,0,0) rot=(1,0,0;3.14159rad)
  Support = -> [Pad018]
  sketch-geometry (4):
    g0: LineSegment StartX=-6.1 StartY=6.1 StartZ=0 EndX=6.1 EndY=6.1 EndZ=0
    g1: LineSegment StartX=6.1 StartY=6.1 StartZ=0 EndX=6.1 EndY=-6.1 EndZ=0
    g2: LineSegment StartX=6.1 StartY=-6.1 StartZ=0 EndX=-6.1 EndY=-6.1 EndZ=0
    g3: LineSegment StartX=-6.1 StartY=-6.1 StartZ=0 EndX=-6.1 EndY=6.1 EndZ=0
  constraints (11):
    c: Coincident(g0,g1)
    c: Coincident(g1,g2)
    c: Coincident(g2,g3)
    c: Coincident(g3,g0)
    c: Horizontal(g0)
    c: Horizontal(g2)
    c: Vertical(g1)
    c: Vertical(g3)
    c: Symmetric(g0,g1,g-1)
    c: Distance(g0) = 12.2
    c: Equal(g0,g3)
FEATURE [PartDesign::Pad] Pad019
  BaseFeature = -> Pad018
  Length = 1
  Length2 = 100
  Profile = -> Sketch053
  Refine = true
  Type = 0
FEATURE [Sketcher::SketchObject] Sketch054
  MapMode = 5
  Support = -> [Pad019]
  sketch-geometry (8):
    g0: LineSegment StartX=-6.2 StartY=6.8 StartZ=0 EndX=6.2 EndY=6.8 EndZ=0
    g1: LineSegment StartX=6.2 StartY=6.8 StartZ=0 EndX=6.2 EndY=-6.8 EndZ=0
    g2: LineSegment StartX=5 StartY=4.8 StartZ=0 EndX=-6.2 EndY=4.8 EndZ=0
    g3: LineSegment StartX=-6.2 StartY=4.8 StartZ=0 EndX=-6.2 EndY=6.8 EndZ=0
    g4: LineSegment StartX=-6.2 StartY=-4.8 StartZ=0 EndX=5 EndY=-4.8 EndZ=0
    g5: LineSegment StartX=6.2 StartY=-6.8 StartZ=0 EndX=-6.2 EndY=-6.8 EndZ=0
    g6: LineSegment StartX=-6.2 StartY=-6.8 StartZ=0 EndX=-6.2 EndY=-4.8 EndZ=0
    g7: LineSegment StartX=5 StartY=4.8 StartZ=0 EndX=5 EndY=-4.8 EndZ=0
  constraints (21):
    c: Coincident(g0,g1)
    c: Coincident(g2,g3)
    c: Coincident(g3,g0)
    c: Horizontal(g2)
    c: Vertical(g1)
    c: Vertical(g3)
    c: Symmetric(g0,g0,g-2)
    c: Coincident(g5,g6)
    c: Coincident(g6,g4)
    c: Horizontal(g4)
    c: Symmetric(g5,g5,g-2)
    c: Symmetric(g2,g4,g-1)
    c: Distance(g0) = 12.4
    c: Distance(g3) = 2
    c: DistanceY(g4,g2) = 9.6
    c: Coincident(g7,g2)
    c: Coincident(g7,g4)
    c: Vertical(g7)
    c: Coincident(g1,g5)
    c: Equal(g6,g3)
    c: DistanceX(g4,g1) = 1.2
FEATURE [PartDesign::Pocket] Pocket024
  BaseFeature = -> Pad019
  Length = 1
  Length2 = 100
  Profile = -> Sketch054
  Refine = true
  Reversed = true
  Type = 0
FEATURE [Sketcher::SketchObject] Sketch055
  ExternalGeometry = -> [Pocket024]
  MapMode = 5
  Placement = pos=(0,0,1) rot=(1,0,0;3.14159rad)
  Support = -> [Pocket024]
  sketch-geometry (4):
    g0: ArcOfCircle CenterX=0 CenterY=0 CenterZ=0 NormalX=0 NormalY=0 NormalZ=1 AngleXU=0 Radius=6.15 StartAngle=4.03704 EndAngle=8.52933
    g1: ArcOfCircle CenterX=0 CenterY=0 CenterZ=0 NormalX=0 NormalY=0 NormalZ=1 AngleXU=0 Radius=4.8 StartAngle=4.03704 EndAngle=8.52933
    g2: LineSegment StartX=-3.8448 StartY=4.8 StartZ=0 EndX=-3.00082 EndY=3.74634 EndZ=0
    g3: LineSegment StartX=-3.00082 StartY=-3.74634 StartZ=0 EndX=-3.8448 EndY=-4.8 EndZ=0
  constraints (11):
    c: Coincident(g0,g-1)
    c: Coincident(g1,g0)
    c: Coincident(g2,g0)
    c: Coincident(g2,g1)
    c: Coincident(g3,g1)
    c: Coincident(g3,g0)
    c: Perpendicular(g0,g3)
    c: Perpendicular(g0,g2)
    c: Vertical(g0,g0)
    c: Tangent(g1,g-4)
    c: Coincident(g0,g-4)
FEATURE [PartDesign::Pocket] Pocket025
  BaseFeature = -> Pocket024
  Length = 2.2
  Length2 = 100
  Profile = -> Sketch055
  Refine = true
  Type = 0
FEATURE [Sketcher::SketchObject] Sketch056
  MapMode = 5
  Support = -> [Pocket025]
  expr: Constraints[9] = 5.1 / 2 - 0.5 / 2
  expr: Constraints[15] = 360 / 20
  sketch-geometry (8):
    g0: ArcOfCircle CenterX=2.3 CenterY=0 CenterZ=0 NormalX=0 NormalY=0 NormalZ=1 AngleXU=0 Radius=0.2 StartAngle=1.44924 EndAngle=4.83395
    g1: LineSegment StartX=2.32425 StartY=0.198524 StartZ=0 EndX=2.3441 EndY=0.196099 EndZ=0
    g2: LineSegment StartX=2.32425 StartY=-0.198524 StartZ=0 EndX=2.3441 EndY=-0.196099 EndZ=0
    g3: ArcOfCircle CenterX=2.36836 CenterY=0.394623 CenterZ=0 NormalX=0 NormalY=0 NormalZ=1 AngleXU=0 Radius=0.2 StartAngle=4.59083 EndAngle=6.34375
    g4: ArcOfCircle CenterX=2.36836 CenterY=-0.394623 CenterZ=0 NormalX=0 NormalY=0 NormalZ=1 AngleXU=0 Radius=0.2 StartAngle=6.22262 EndAngle=7.97554
    g5: LineSegment [constr] StartX=0 StartY=0 StartZ=0 EndX=2.56799 EndY=0.40673 EndZ=0
    g6: LineSegment [constr] StartX=0 StartY=0 StartZ=0 EndX=2.56799 EndY=-0.40673 EndZ=0
    g7: ArcOfCircle CenterX=0 CenterY=0 CenterZ=0 NormalX=0 NormalY=0 NormalZ=1 AngleXU=0 Radius=2.6 StartAngle=6.12611 EndAngle=6.44026
  constraints (21):
    c: PointOnObject(g0,g-1)
    c: Vertical(g0,g0)
    c: Diameter(g0) = 0.4
    c: Tangent(g2,g0) = -1.5708
    c: Tangent(g1,g0) = 1.5708
    c: Tangent(g4,g2) = 1.5708
    c: Tangent(g3,g1) = -1.5708
    c: Equal(g3,g0)
    c: Equal(g4,g0)
    c: DistanceX(g0) = 2.3
    c: Coincident(g5,g-1)
    c: Coincident(g5,g3)
    c: Coincident(g6,g-1)
    c: Coincident(g6,g4)
    c: Vertical(g4,g3)
    c: Angle(g6,g5) = 0.314159
    c: Coincident(g7,g-1)
    c: Coincident(g7,g3)
    c: Coincident(g7,g4)
    c: Distance(g1) = 0.02
    c: Diameter(g7) = 5.2
FEATURE [PartDesign::Pad] Pad020
  BaseFeature = -> Pocket025
  Length = 5
  Length2 = 100
  Profile = -> Sketch056
  Refine = true
  Type = 0
FEATURE [PartDesign::PolarPattern] PolarPattern003
  Angle = 360
  Axis = -> Sketch056 [N_Axis]
  BaseFeature = -> Pad020
  Occurrences = 20
  Originals = -> [Pad020]
  Refine = true
FEATURE [Sketcher::SketchObject] Sketch057
  MapMode = 5
  Support = -> [PolarPattern003]
  sketch-geometry (1):
    g0: Circle CenterX=0 CenterY=0 CenterZ=0 NormalX=0 NormalY=0 NormalZ=1 AngleXU=0 Radius=1.35
  constraints (2):
    c: Coincident(g0,g-1)
    c: Diameter(g0) = 2.7
FEATURE [PartDesign::Pocket] Pocket026
  BaseFeature = -> PolarPattern003
  Length = 5
  Length2 = 100
  Profile = -> Sketch057
  Refine = true
  Type = 1
FEATURE [Sketcher::SketchObject] Sketch058
  ExternalGeometry = -> [Pocket026]
  MapMode = 5
  Placement = pos=(0,0,5.15) rot=(0,0,1;0rad)
  Support = -> [Pocket026]
  sketch-geometry (2):
    g0: Circle CenterX=0 CenterY=0 CenterZ=0 NormalX=0 NormalY=0 NormalZ=1 AngleXU=0 Radius=2.7
    g1: LineSegment [constr] StartX=2.6 StartY=0 StartZ=0 EndX=2.7 EndY=0 EndZ=0
  constraints (6):
    c: Coincident(g0,g-1)
    c: PointOnObject(g1,g-3)
    c: PointOnObject(g1,g0)
    c: PointOnObject(g1,g-1)
    c: Horizontal(g1)
    c: Distance(g1) = 0.1
FEATURE [PartDesign::Pocket] Pocket029
  BaseFeature = -> Pocket026
  Length = 1
  Length2 = 100
  Profile = -> Sketch058
  Refine = true
  Type = 0
FEATURE [Sketcher::SketchObject] Sketch059
  ExternalGeometry = -> [Pocket025]
  MapMode = 5
  Placement = pos=(0,0,5.15) rot=(0,0,1;0rad)
  Support = -> [Pocket025]
  expr: Constraints[1] = 11.8 + 4
  sketch-geometry (2):
    g0: Circle CenterX=0 CenterY=0 CenterZ=0 NormalX=0 NormalY=0 NormalZ=1 AngleXU=0 Radius=7.9
    g1: Circle CenterX=0 CenterY=0 CenterZ=0 NormalX=0 NormalY=0 NormalZ=1 AngleXU=0 Radius=2.6
  constraints (4):
    c: Coincident(g0,g-1)
    c: Diameter(g0) = 15.8
    c: Coincident(g1,g0)
    c: Equal(g-3,g1)
FEATURE [PartDesign::Pad] Pad021
  BaseFeature = -> Pocket029
  Length = 1.94
  Length2 = 100
  Profile = -> Sketch059
  Refine = true
  Reversed = true
  Type = 3
  UpToFace = -> Pocket029 [Face17]
FEATURE [Sketcher::SketchObject] Sketch060
  MapMode = 5
  Placement = pos=(0,0,5.15) rot=(0,0,1;0rad)
  Support = -> [Pad021]
  expr: Constraints[1] = 11.8 + 2
  sketch-geometry (1):
    g0: Circle CenterX=0 CenterY=0 CenterZ=0 NormalX=0 NormalY=0 NormalZ=1 AngleXU=0 Radius=6.9
  constraints (2):
    c: Coincident(g0,g-1)
    c: Diameter(g0) = 13.8
FEATURE [Sketcher::SketchObject] Sketch061
  MapMode = 5
  Support = -> [XY_Plane009]
  expr: Constraints[1] = 11.8 + 2 - 0.1
  sketch-geometry (2):
    g0: Circle CenterX=0 CenterY=0 CenterZ=0 NormalX=0 NormalY=0 NormalZ=1 AngleXU=0 Radius=6.85
    g1: Circle CenterX=0 CenterY=0 CenterZ=0 NormalX=0 NormalY=0 NormalZ=1 AngleXU=0 Radius=3.5
  constraints (4):
    c: Coincident(g0,g-1)
    c: Diameter(g0) = 13.7
    c: Coincident(g1,g0)
    c: Diameter(g1) = 7
FEATURE [PartDesign::Pad] Pad022
  Length = 1
  Length2 = 100
  Profile = -> Sketch061
  Refine = true
  Type = 0
FEATURE [Sketcher::SketchObject] Sketch062
  ExternalGeometry = -> [Pad022]
  MapMode = 5
  Placement = pos=(0,0,0) rot=(1,0,0;3.14159rad)
  Support = -> [Pad022]
  sketch-geometry (4):
    g0: ArcOfCircle CenterX=0 CenterY=0 CenterZ=0 NormalX=0 NormalY=0 NormalZ=1 AngleXU=0 Radius=6.85 StartAngle=0.523599 EndAngle=5.75959
    g1: ArcOfCircle CenterX=0 CenterY=0 CenterZ=0 NormalX=0 NormalY=0 NormalZ=1 AngleXU=0 Radius=5.9 StartAngle=0.523599 EndAngle=5.75959
    g2: LineSegment StartX=5.10955 StartY=2.95 StartZ=0 EndX=5.93227 EndY=3.425 EndZ=0
    g3: LineSegment StartX=5.10955 StartY=-2.95 StartZ=0 EndX=5.93227 EndY=-3.425 EndZ=0
  constraints (12):
    c: Coincident(g0,g-1)
    c: Coincident(g1,g0)
    c: Coincident(g2,g1)
    c: Coincident(g2,g0)
    c: Coincident(g3,g1)
    c: Coincident(g3,g0)
    c: Perpendicular(g0,g3)
    c: Perpendicular(g0,g2)
    c: Angle(g3,g2) = 1.0472
    c: Vertical(g0,g0)
    c: Equal(g0,g-3)
    c: Diameter(g1) = 11.8
FEATURE [PartDesign::Pad] Pad023
  BaseFeature = -> Pad022
  Length = 1.2
  Length2 = 100
  Profile = -> Sketch062
  Refine = true
  Type = 0
FEATURE [Sketcher::SketchObject] Sketch064
  MapMode = 5
  Placement = pos=(0,0,-1.2) rot=(1,0,0;3.14159rad)
  Support = -> [Pad023]
  sketch-geometry (2):
    g0: Circle CenterX=-5 CenterY=4.5 CenterZ=0 NormalX=0 NormalY=0 NormalZ=1 AngleXU=0 Radius=1
    g1: Circle CenterX=-5 CenterY=-4.5 CenterZ=0 NormalX=0 NormalY=0 NormalZ=1 AngleXU=0 Radius=1
  constraints (5):
    c: Diameter(g0) = 2
    c: Equal(g1,g0)
    c: DistanceY(g0) = 4.5
    c: DistanceX(g0) = -5
    c: Symmetric(g0,g1,g-1)
FEATURE [PartDesign::Pocket] Pocket032
  BaseFeature = -> Pad023
  Length = 1.2
  Length2 = 100
  Profile = -> Sketch064
  Refine = true
  Type = 0
FEATURE [PartDesign::Body] Body009  label="s6Bushing"
  Group = -> [Sketch061,Pad022,Sketch062,Pad023,Sketch064,Pocket032]
  Origin = -> Origin009
  Tip = -> Pocket032
FEATURE [Sketcher::SketchObject] Sketch065
  MapMode = 5
  Support = -> [XY_Plane010]
  sketch-geometry (4):
    g0: LineSegment StartX=-7 StartY=24 StartZ=0 EndX=9 EndY=24 EndZ=0
    g1: LineSegment StartX=-7 StartY=24 StartZ=0 EndX=-7 EndY=-13.5 EndZ=0
    g2: LineSegment StartX=-7 StartY=-13.5 StartZ=0 EndX=9 EndY=-13.5 EndZ=0
    g3: LineSegment StartX=9 StartY=-13.5 StartZ=0 EndX=9 EndY=24 EndZ=0
  constraints (12):
    c: Coincident(g1,g0)
    c: Vertical(g1)
    c: Coincident(g2,g1)
    c: Horizontal(g2)
    c: Coincident(g3,g0)
    c: Vertical(g3)
    c: Distance(g1) = 37.5
    c: Distance(g0) = 16
    c: DistanceY(g1,g-1) = 13.5
    c: Coincident(g3,g2)
    c: DistanceX(g0) = -7
    c: Horizontal(g0)
FEATURE [PartDesign::Pad] Pad024
  Length = 5
  Length2 = 100
  Profile = -> Sketch065
  Refine = true
  Type = 0
FEATURE [Sketcher::SketchObject] Sketch066
  AttachmentOffset = pos=(0,0,0) rot=(0,0,1;3.14159rad)
  ExternalGeometry = -> [Pad024]
  MapMode = 5
  Placement = pos=(0,0,0) rot=(0,-1,0;3.14159rad)
  Support = -> [Pad024]
  sketch-geometry (4):
    g0: LineSegment StartX=-9 StartY=24 StartZ=0 EndX=-7 EndY=24 EndZ=0
    g1: LineSegment StartX=-7 StartY=24 StartZ=0 EndX=-7 EndY=-13.5 EndZ=0
    g2: LineSegment StartX=-7 StartY=-13.5 StartZ=0 EndX=-9 EndY=-13.5 EndZ=0
    g3: LineSegment StartX=-9 StartY=-13.5 StartZ=0 EndX=-9 EndY=24 EndZ=0
  constraints (10):
    c: Coincident(g0,g1)
    c: Coincident(g1,g2)
    c: Coincident(g2,g3)
    c: Coincident(g3,g0)
    c: Horizontal(g0)
    c: Horizontal(g2)
    c: Vertical(g1)
    c: Coincident(g0,g-3)
    c: Coincident(g2,g-3)
    c: Distance(g0) = 2
FEATURE [PartDesign::Pad] Pad025
  BaseFeature = -> Pad024
  Length = 10
  Length2 = 100
  Profile = -> Sketch066
  Refine = true
  Type = 0
FEATURE [Sketcher::SketchObject] Sketch067
  ExternalGeometry = -> [Pad025]
  MapMode = 5
  Placement = pos=(0,24,0) rot=(0,0.707107,0.707107;3.14159rad)
  Support = -> [Pad025]
  sketch-geometry (3):
    g0: LineSegment StartX=-7 StartY=0 StartZ=0 EndX=7 EndY=0 EndZ=0
    g1: LineSegment StartX=-7 StartY=-10 StartZ=0 EndX=-7 EndY=0 EndZ=0
    g2: ArcOfCircle CenterX=7 CenterY=-14.8 CenterZ=0 NormalX=0 NormalY=0 NormalZ=1 AngleXU=0 Radius=14.8 StartAngle=1.5708 EndAngle=2.8113
  constraints (6):
    c: Coincident(g-4,g0)
    c: Coincident(g0,g-3)
    c: Coincident(g1,g0)
    c: Coincident(g2,g1)
    c: Coincident(g1,g-4)
    c: Tangent(g2,g0) = 1.5708
FEATURE [PartDesign::Pad] Pad026
  BaseFeature = -> Pad025
  Length = 2
  Length2 = 100
  Profile = -> Sketch067
  Refine = true
  Reversed = true
  Type = 0
FEATURE [Sketcher::SketchObject] Sketch068
  ExternalGeometry = -> [Pad026]
  MapMode = 5
  Placement = pos=(3e-16,-13.5,-7e-16) rot=(1,0,0;1.5708rad)
  Support = -> [Pad026]
  sketch-geometry (3):
    g0: LineSegment StartX=-7 StartY=7e-16 StartZ=0 EndX=7 EndY=7e-16 EndZ=0
    g1: LineSegment StartX=7 StartY=7e-16 StartZ=0 EndX=7 EndY=-10 EndZ=0
    g2: ArcOfCircle CenterX=-7 CenterY=-14.8 CenterZ=0 NormalX=0 NormalY=0 NormalZ=1 AngleXU=0 Radius=14.8 StartAngle=0.330297 EndAngle=1.5708
  constraints (6):
    c: Coincident(g-3,g0)
    c: Coincident(g0,g-4)
    c: Coincident(g0,g1)
    c: Coincident(g1,g-4)
    c: Coincident(g2,g1)
    c: Tangent(g2,g0) = 1.5708
FEATURE [PartDesign::Pad] Pad027
  BaseFeature = -> Pad026
  Length = 2
  Length2 = 100
  Profile = -> Sketch068
  Refine = true
  Reversed = true
  Type = 0
FEATURE [Sketcher::SketchObject] Sketch069
  ExternalGeometry = -> [Pad027]
  MapMode = 5
  Placement = pos=(9,0,0) rot=(0.57735,0.57735,0.57735;2.0944rad)
  Support = -> [Pad027]
  sketch-geometry (3):
    g0: LineSegment StartX=24 StartY=5 StartZ=0 EndX=9 EndY=5 EndZ=0
    g1: LineSegment StartX=9 StartY=5 StartZ=0 EndX=24 EndY=2 EndZ=0
    g2: LineSegment StartX=24 StartY=2 StartZ=0 EndX=24 EndY=5 EndZ=0
  constraints (8):
    c: Coincident(g-4,g0)
    c: PointOnObject(g0,g-3)
    c: Coincident(g0,g1)
    c: PointOnObject(g1,g-4)
    c: Coincident(g1,g2)
    c: Coincident(g2,g0)
    c: Distance(g2) = 3
    c: DistanceX(g-1,g0) = 9
FEATURE [PartDesign::Pocket] Pocket033
  BaseFeature = -> Pad027
  Length = 5
  Length2 = 100
  Profile = -> Sketch069
  Refine = true
  Type = 1
FEATURE [PartDesign::Fillet] Fillet009
  Base = -> Pocket033 [Edge19]
  BaseFeature = -> Pocket033
  Radius = 3
  Refine = true
  SupportTransform = false
FEATURE [PartDesign::Fillet] Fillet010
  Base = -> Fillet009 [Edge23]
  BaseFeature = -> Fillet009
  Radius = 0.1
  Refine = true
  SupportTransform = false
FEATURE [PartDesign::Fillet] Fillet011
  Base = -> Fillet010 [Edge12]
  BaseFeature = -> Fillet010
  Radius = 10
  Refine = true
  SupportTransform = false
FEATURE [Sketcher::SketchObject] Sketch070
  AttachmentOffset = pos=(0,0,0) rot=(0,0,1;3.14159rad)
  ExternalGeometry = -> [Fillet011]
  MapMode = 5
  Placement = pos=(0,0,0) rot=(0,-1,0;3.14159rad)
  Support = -> [Fillet011]
  sketch-geometry (3):
    g0: ArcOfCircle CenterX=3.5 CenterY=20.5 CenterZ=0 NormalX=0 NormalY=0 NormalZ=1 AngleXU=0 Radius=3.5 StartAngle=0 EndAngle=1.57079
    g1: LineSegment StartX=7 StartY=24 StartZ=0 EndX=7 EndY=20.5 EndZ=0
    g2: LineSegment StartX=7 StartY=24 StartZ=0 EndX=3.50003 EndY=24 EndZ=0
  constraints (8):
    c: PointOnObject(g0,g-3)
    c: Tangent(g0,g-3)
    c: Coincident(g1,g-3)
    c: Tangent(g1,g0) = 1.5708
    c: Coincident(g2,g1)
    c: Coincident(g2,g0)
    c: Radius(g0) = 3.5
    c: Vertical(g1)
FEATURE [PartDesign::Pocket] Pocket034
  BaseFeature = -> Fillet011
  Length = 5
  Length2 = 100
  Midplane = true
  Profile = -> Sketch070
  Refine = true
  Type = 1
FEATURE [Sketcher::SketchObject] Sketch071
  AttachmentOffset = pos=(0,0,0) rot=(0,0,1;3.14159rad)
  ExternalGeometry = -> [Pocket034]
  MapMode = 5
  Placement = pos=(0,0,-10) rot=(0,-1,0;3.14159rad)
  Support = -> [Pocket034]
  sketch-geometry (3):
    g0: ArcOfCircle CenterX=-5.5 CenterY=20.5 CenterZ=0 NormalX=0 NormalY=0 NormalZ=1 AngleXU=0 Radius=3.5 StartAngle=1.5708 EndAngle=3.14159
    g1: LineSegment StartX=-5.50001 StartY=24 StartZ=0 EndX=-9 EndY=24 EndZ=0
    g2: LineSegment StartX=-9 StartY=20.5 StartZ=0 EndX=-9 EndY=24 EndZ=0
  constraints (8):
    c: Coincident(g1,g0)
    c: Horizontal(g1)
    c: Tangent(g1,g0)
    c: Coincident(g2,g1)
    c: Tangent(g2,g0) = 1.5708
    c: Radius(g0) = 3.5
    c: Coincident(g1,g-3)
    c: Vertical(g2)
FEATURE [PartDesign::Pocket] Pocket035
  BaseFeature = -> Pocket034
  Length = 5
  Length2 = 100
  Profile = -> Sketch071
  Refine = true
  Type = 1
FEATURE [Sketcher::SketchObject] Sketch072
  MapMode = 5
  Placement = pos=(0,0,5) rot=(0,0,1;0rad)
  sketch-geometry (17):
    g0: LineSegment StartX=9 StartY=5 StartZ=0 EndX=19 EndY=5 EndZ=0
    g1: LineSegment StartX=9 StartY=7 StartZ=0 EndX=21 EndY=7 EndZ=0
    g2: LineSegment StartX=21 StartY=7 StartZ=0 EndX=21 EndY=2.5 EndZ=0
    g3: LineSegment StartX=21 StartY=2.5 StartZ=0 EndX=29 EndY=2.5 EndZ=0
    g4: LineSegment StartX=29 StartY=2.5 StartZ=0 EndX=29 EndY=0.5 EndZ=0
    g5: LineSegment StartX=29 StartY=0.5 StartZ=0 EndX=19 EndY=0.5 EndZ=0
    g6: LineSegment StartX=19 StartY=5 StartZ=0 EndX=19 EndY=0.5 EndZ=0
    g7: LineSegment StartX=7 StartY=-7 StartZ=0 EndX=21 EndY=-7 EndZ=0
    g8: LineSegment StartX=9 StartY=-5 StartZ=0 EndX=19 EndY=-5 EndZ=0
    g9: LineSegment StartX=19 StartY=-5 StartZ=0 EndX=19 EndY=-0.5 EndZ=0
    g10: LineSegment StartX=19 StartY=-0.5 StartZ=0 EndX=29 EndY=-0.5 EndZ=0
    g11: LineSegment StartX=29 StartY=-0.5 StartZ=0 EndX=29 EndY=-2.5 EndZ=0
    g12: LineSegment StartX=29 StartY=-2.5 StartZ=0 EndX=21 EndY=-2.5 EndZ=0
    g13: LineSegment StartX=21 StartY=-7 StartZ=0 EndX=21 EndY=-2.5 EndZ=0
    g14: LineSegment StartX=9 StartY=7 StartZ=0 EndX=7 EndY=7 EndZ=0
    g15: LineSegment StartX=7 StartY=7 StartZ=0 EndX=7 EndY=-7 EndZ=0
    g16: LineSegment StartX=9 StartY=5 StartZ=0 EndX=9 EndY=-5 EndZ=0
  constraints (50):
    c: Horizontal(g0)
    c: Horizontal(g1)
    c: Coincident(g1,g2)
    c: Coincident(g2,g3)
    c: Horizontal(g3)
    c: Coincident(g3,g4)
    c: Coincident(g4,g5)
    c: Horizontal(g5)
    c: Coincident(g6,g0)
    c: Coincident(g6,g5)
    c: Vertical(g6)
    c: Vertical(g4)
    c: Vertical(g2)
    c: DistanceY(g0,g1) = 2
    c: DistanceX(g0,g1) = 2
    c: Horizontal(g7)
    c: Horizontal(g8)
    c: Coincident(g8,g9)
    c: Coincident(g9,g10)
    c: Horizontal(g10)
    c: Coincident(g10,g11)
    c: Coincident(g11,g12)
    c: Horizontal(g12)
    c: Coincident(g13,g7)
    c: Coincident(g13,g12)
    c: Vertical(g13)
    c: Vertical(g11)
    c: Vertical(g9)
    c: DistanceY(g7,g8) = 2
    c: DistanceX(g8,g7) = 2
    c: Equal(g0,g8)
    c: Equal(g6,g9)
    c: DistanceY(g8,g0) = 10
    c: Distance(g0) = 10
    c: Equal(g5,g10)
    c: Symmetric(g0,g8,g-1)
    c: Distance(g3) = 8
    c: Distance(g4,g10) = 1
    c: Coincident(g14,g1)
    c: Horizontal(g14)
    c: Coincident(g15,g14)
    c: Vertical(g15)
    c: Coincident(g16,g0)
    c: Coincident(g16,g8)
    c: Equal(g4,g11)
    c: Distance(g4) = 2
    c: Equal(g14,g4)
    c: Coincident(g7,g15)
    c: DistanceX(g0) = 9
    c: Vertical(g1,g0)
FEATURE [PartDesign::Pad] Pad028
  BaseFeature = -> Pocket035
  Length = 15
  Length2 = 100
  Profile = -> Sketch072
  Refine = true
  Reversed = true
  Type = 0
FEATURE [PartDesign::Fillet] Fillet012
  Base = -> Pad028 [Edge17,Edge74,Edge8,Edge88]
  BaseFeature = -> Pad028
  Radius = 1
  Refine = true
  SupportTransform = false
FEATURE [PartDesign::Fillet] Fillet013
  Base = -> Fillet012 [Edge76,Edge56,Edge75,Edge58]
  BaseFeature = -> Fillet012
  Radius = 1
  Refine = true
  SupportTransform = false
FEATURE [Sketcher::SketchObject] Sketch073
  ExternalGeometry = -> [Fillet013]
  MapMode = 5
  Placement = pos=(0,2.5,0) rot=(0,0.707107,0.707107;3.14159rad)
  Support = -> [Fillet013]
  sketch-geometry (4):
    g0: Circle CenterX=-24.3786 CenterY=1 CenterZ=0 NormalX=0 NormalY=0 NormalZ=1 AngleXU=0 Radius=1.5
    g1: Circle CenterX=-24.3786 CenterY=-6 CenterZ=0 NormalX=0 NormalY=0 NormalZ=1 AngleXU=0 Radius=1.5
    g2: LineSegment [constr] StartX=-28.3786 StartY=-10 StartZ=0 EndX=-28.3786 EndY=-6 EndZ=0
    g3: LineSegment [constr] StartX=-28.3786 StartY=5 StartZ=0 EndX=-28.3786 EndY=1 EndZ=0
  constraints (8):
    c: Vertical(g1,g0)
    c: Diameter(g0) = 3
    c: Diameter(g1) = 3
    c: Horizontal(g3,g0)
    c: Horizontal(g2,g1)
    c: Equal(g2,g3)
    c: Distance(g3) = 4
    c: Distance(g0,g3) = 4
FEATURE [PartDesign::Pocket] Pocket036
  BaseFeature = -> Fillet013
  Length = 5
  Length2 = 100
  Profile = -> Sketch073
  Refine = true
  Type = 1
FEATURE [Sketcher::SketchObject] Sketch074
  MapMode = 5
  Placement = pos=(0,0,0) rot=(1,0,0;3.14159rad)
  Support = -> [Pocket036]
  sketch-geometry (4):
    g0: LineSegment StartX=-6.25 StartY=6.5 StartZ=0 EndX=6.25 EndY=6.5 EndZ=0
    g1: LineSegment StartX=6.25 StartY=6.5 StartZ=0 EndX=6.25 EndY=-17 EndZ=0
    g2: LineSegment StartX=6.25 StartY=-17 StartZ=0 EndX=-6.25 EndY=-17 EndZ=0
    g3: LineSegment StartX=-6.25 StartY=-17 StartZ=0 EndX=-6.25 EndY=6.5 EndZ=0
  constraints (11):
    c: Coincident(g0,g1)
    c: Coincident(g1,g2)
    c: Coincident(g2,g3)
    c: Coincident(g3,g0)
    c: Horizontal(g2)
    c: Vertical(g1)
    c: Vertical(g3)
    c: Symmetric(g0,g0,g-2)
    c: Distance(g0) = 12.5
    c: Distance(g3) = 23.5
    c: DistanceY(g-1,g0) = 6.5
FEATURE [PartDesign::Pocket] Pocket037
  BaseFeature = -> Pocket036
  Length = 2
  Length2 = 100
  Profile = -> Sketch074
  Refine = true
  Type = 0
FEATURE [Sketcher::SketchObject] Sketch075
  ExternalGeometry = -> [Pocket037]
  MapMode = 5
  Placement = pos=(0,0,2) rot=(1,0,0;3.14159rad)
  Support = -> [Pocket037]
  sketch-geometry (3):
    g0: ArcOfCircle CenterX=0 CenterY=0 CenterZ=0 NormalX=0 NormalY=0 NormalZ=1 AngleXU=0 Radius=6.25 StartAngle=5.24905 EndAngle=10.4589
    g1: ArcOfCircle CenterX=0 CenterY=-5.2 CenterZ=0 NormalX=0 NormalY=0 NormalZ=1 AngleXU=0 Radius=3.2 StartAngle=3.19518 EndAngle=6.2296
    g2: LineSegment [constr] StartX=0 StartY=0 StartZ=0 EndX=0 EndY=-8.4 EndZ=0
  constraints (10):
    c: Coincident(g0,g-1)
    c: PointOnObject(g1,g-2)
    c: Coincident(g1,g0)
    c: Coincident(g1,g0)
    c: Tangent(g-3,g0)
    c: Coincident(g2,g0)
    c: PointOnObject(g2,g1)
    c: Vertical(g2)
    c: Distance(g2) = 8.4
    c: Distance(g0,g1) = 3.2
FEATURE [PartDesign::Pocket] Pocket038
  BaseFeature = -> Pocket037
  Length = 5
  Length2 = 100
  Profile = -> Sketch075
  Refine = true
  Type = 1
FEATURE [Sketcher::SketchObject] Sketch076
  MapMode = 5
  Placement = pos=(0,0,2) rot=(1,0,0;3.14159rad)
  Support = -> [Pocket038]
  sketch-geometry (4):
    g0: Circle CenterX=-4.5 CenterY=5 CenterZ=0 NormalX=0 NormalY=0 NormalZ=1 AngleXU=0 Radius=1
    g1: Circle CenterX=4.5 CenterY=5 CenterZ=0 NormalX=0 NormalY=0 NormalZ=1 AngleXU=0 Radius=1
    g2: Circle CenterX=4.5 CenterY=-15 CenterZ=0 NormalX=0 NormalY=0 NormalZ=1 AngleXU=0 Radius=1
    g3: Circle CenterX=-4.5 CenterY=-15 CenterZ=0 NormalX=0 NormalY=0 NormalZ=1 AngleXU=0 Radius=1
  constraints (11):
    c: Equal(g2,g3)
    c: Equal(g3,g1)
    c: Equal(g1,g0)
    c: Diameter(g1) = 2
    c: Symmetric(g0,g1,g-2)
    c: Vertical(g3,g0)
    c: Vertical(g2,g1)
    c: Horizontal(g3,g2)
    c: DistanceX(g1) = 4.5
    c: DistanceY(g1) = 5
    c: DistanceY(g2,g1) = 20
FEATURE [PartDesign::Pocket] Pocket039
  BaseFeature = -> Pocket038
  Length = 5
  Length2 = 100
  Profile = -> Sketch076
  Refine = true
  Type = 1
FEATURE [Sketcher::SketchObject] Sketch077
  AttachmentOffset = pos=(0,0,0) rot=(0,0,1;3.14159rad)
  MapMode = 5
  Placement = pos=(0,0,0) rot=(0,-1,0;3.14159rad)
  Support = -> [Pocket039]
  sketch-geometry (2):
    g0: Circle CenterX=0 CenterY=19.5 CenterZ=0 NormalX=0 NormalY=0 NormalZ=1 AngleXU=0 Radius=1
    g1: Circle CenterX=0 CenterY=-8.9 CenterZ=0 NormalX=0 NormalY=0 NormalZ=1 AngleXU=0 Radius=1
  constraints (6):
    c: PointOnObject(g0,g-2)
    c: PointOnObject(g1,g-2)
    c: Equal(g1,g0)
    c: Distance(g-1,g1) = 8.9
    c: Distance(g-1,g0) = 19.5
    c: Diameter(g0) = 2
FEATURE [PartDesign::Pocket] Pocket040
  BaseFeature = -> Pocket039
  Length = 5
  Length2 = 100
  Profile = -> Sketch077
  Refine = true
  Type = 1
FEATURE [PartDesign::Body] Body010  label="s4Mount"
  Group = -> [Sketch065,Pad024,Sketch066,Pad025,Sketch067,Pad026,Sketch068,Pad027,Sketch069,Pocket033,Fillet009,Fillet010,Fillet011,Sketch070,Pocket034,Sketch071,Pocket035,Sketch072,Pad028,Fillet012,Fillet013,Sketch073,Pocket036,Sketch074,Pocket037,Sketch075,Pocket038,Sketch076,Pocket039,Sketch077,Pocket040]
  Origin = -> Origin010
  Placement = pos=(0,0,-52.4) rot=(0,0,1;0rad)
  Tip = -> Pocket040
FEATURE [Sketcher::SketchObject] Sketch078
  MapMode = 5
  Support = -> [XY_Plane011]
  sketch-geometry (8):
    g0: LineSegment StartX=-5 StartY=5 StartZ=0 EndX=5 EndY=5 EndZ=0
    g1: LineSegment StartX=5 StartY=5 StartZ=0 EndX=5 EndY=-5 EndZ=0
    g2: LineSegment StartX=5 StartY=-5 StartZ=0 EndX=-5 EndY=-5 EndZ=0
    g3: LineSegment StartX=-5 StartY=-5 StartZ=0 EndX=-5 EndY=5 EndZ=0
    g4: LineSegment StartX=-4 StartY=4 StartZ=0 EndX=4 EndY=4 EndZ=0
    g5: LineSegment StartX=4 StartY=4 StartZ=0 EndX=4 EndY=-4 EndZ=0
    g6: LineSegment StartX=4 StartY=-4 StartZ=0 EndX=-4 EndY=-4 EndZ=0
    g7: LineSegment StartX=-4 StartY=-4 StartZ=0 EndX=-4 EndY=4 EndZ=0
  constraints (22):
    c: Coincident(g0,g1)
    c: Coincident(g1,g2)
    c: Coincident(g2,g3)
    c: Coincident(g3,g0)
    c: Horizontal(g0)
    c: Horizontal(g2)
    c: Vertical(g1)
    c: Vertical(g3)
    c: Symmetric(g0,g1,g-1)
    c: Equal(g0,g1)
    c: Distance(g0) = 10
    c: Coincident(g4,g5)
    c: Coincident(g5,g6)
    c: Coincident(g6,g7)
    c: Coincident(g7,g4)
    c: Horizontal(g4)
    c: Horizontal(g6)
    c: Vertical(g5)
    c: Vertical(g7)
    c: Symmetric(g4,g5,g-1)
    c: Equal(g4,g5)
    c: Distance(g4) = 8
FEATURE [PartDesign::Pad] Pad029
  Length = 166
  Length2 = 100
  Profile = -> Sketch078
  Refine = true
  Reversed = true
  Type = 0
FEATURE [PartDesign::Body] Body011
  Group = -> [Sketch078,Pad029]
  Origin = -> Origin011
  Placement = pos=(14,0,-47.4) rot=(0,0,1;0rad)
  Tip = -> Pad029
FEATURE [Sketcher::SketchObject] Sketch090
  MapMode = 5
  Support = -> [XY_Plane013]
  sketch-geometry (8):
    g0: LineSegment StartX=-5 StartY=5 StartZ=0 EndX=5 EndY=5 EndZ=0
    g1: LineSegment StartX=5 StartY=5 StartZ=0 EndX=5 EndY=-5 EndZ=0
    g2: LineSegment StartX=5 StartY=-5 StartZ=0 EndX=-5 EndY=-5 EndZ=0
    g3: LineSegment StartX=-5 StartY=-5 StartZ=0 EndX=-5 EndY=5 EndZ=0
    g4: LineSegment StartX=-4 StartY=4 StartZ=0 EndX=4 EndY=4 EndZ=0
    g5: LineSegment StartX=4 StartY=4 StartZ=0 EndX=4 EndY=-4 EndZ=0
    g6: LineSegment StartX=4 StartY=-4 StartZ=0 EndX=-4 EndY=-4 EndZ=0
    g7: LineSegment StartX=-4 StartY=-4 StartZ=0 EndX=-4 EndY=4 EndZ=0
  constraints (22):
    c: Coincident(g0,g1)
    c: Coincident(g1,g2)
    c: Coincident(g2,g3)
    c: Coincident(g3,g0)
    c: Horizontal(g0)
    c: Horizontal(g2)
    c: Vertical(g1)
    c: Vertical(g3)
    c: Symmetric(g0,g1,g-1)
    c: Equal(g0,g1)
    c: Distance(g0) = 10
    c: Coincident(g4,g5)
    c: Coincident(g5,g6)
    c: Coincident(g6,g7)
    c: Coincident(g7,g4)
    c: Horizontal(g4)
    c: Horizontal(g6)
    c: Vertical(g5)
    c: Vertical(g7)
    c: Symmetric(g4,g5,g-1)
    c: Equal(g4,g5)
    c: Distance(g4) = 8
FEATURE [PartDesign::Pad] Pad037
  Length = 236
  Length2 = 100
  Profile = -> Sketch090
  Refine = true
  Reversed = true
  Type = 0
FEATURE [PartDesign::Body] Body013
  Group = -> [Sketch090,Pad037]
  Origin = -> Origin013
  Placement = pos=(35.9,18,-218.8) rot=(-1,0,0;1.5708rad)
  Tip = -> Pad037
FEATURE [Sketcher::SketchObject] Sketch094
  MapMode = 5
  Support = -> [XY_Plane014]
  expr: Constraints[31] = 15 / 2
  expr: Constraints[32] = 7 / 2
  sketch-geometry (15):
    g0: Circle [constr] CenterX=0 CenterY=0 CenterZ=0 NormalX=0 NormalY=0 NormalZ=1 AngleXU=0 Radius=7.5
    g1: Circle [constr] CenterX=18.5 CenterY=0 CenterZ=0 NormalX=0 NormalY=0 NormalZ=1 AngleXU=0 Radius=3.5
    g2: LineSegment StartX=-7.5 StartY=0 StartZ=0 EndX=27.5 EndY=0 EndZ=0
    g3: ArcOfCircle CenterX=0 CenterY=0 CenterZ=0 NormalX=0 NormalY=0 NormalZ=1 AngleXU=0 Radius=7.5 StartAngle=1.25298 EndAngle=3.14159
    g4: LineSegment [constr] StartX=13.3609 StartY=3.5 StartZ=0 EndX=2.34371 EndY=7.1244 EndZ=0
    g5: LineSegment [constr] StartX=18.5 StartY=3.5 StartZ=0 EndX=13.3609 EndY=3.5 EndZ=0
    g6: Circle [constr] CenterX=2.34371 CenterY=7.1244 CenterZ=0 NormalX=0 NormalY=0 NormalZ=1 AngleXU=0 Radius=1
    g7: Circle [constr] CenterX=13.3609 CenterY=3.5 CenterZ=0 NormalX=0 NormalY=0 NormalZ=1 AngleXU=0 Radius=1
    g8: Circle [constr] CenterX=18.5 CenterY=3.5 CenterZ=0 NormalX=0 NormalY=0 NormalZ=1 AngleXU=0 Radius=1
    g9: BSplineCurve PolesCount=3 KnotsCount=2 Degree=2 IsPeriodic=0
    g10: GeomPoint [constr] X=2.34371 Y=7.1244 Z=0
    g11: GeomPoint [constr] X=18.5 Y=3.5 Z=0
    g12: LineSegment StartX=18.5 StartY=3.5 StartZ=0 EndX=24 EndY=3.5 EndZ=0
    g13: ArcOfCircle CenterX=24 CenterY=0 CenterZ=0 NormalX=0 NormalY=0 NormalZ=1 AngleXU=0 Radius=3.5 StartAngle=0 EndAngle=1.5708
    g14: LineSegment [constr] StartX=24 StartY=0 StartZ=0 EndX=13.3609 EndY=3.5 EndZ=0
  constraints (37):
    c: Coincident(g0,g-1)
    c: PointOnObject(g1,g-1)
    c: PointOnObject(g2,g0)
    c: Horizontal(g2)
    c: PointOnObject(g-1,g2)
    c: Coincident(g3,g-1)
    c: Coincident(g3,g2)
    c: Tangent(g4,g0)
    c: Coincident(g3,g4)
    c: Coincident(g5,g4)
    c: Horizontal(g5)
    c: Tangent(g5,g1)
    c: Coincident(g6,g3)
    c: Radius(g6) = 1
    c: Equal(g6,g7)
    c: Coincident(g7,g4)
    c: Equal(g6,g8)
    c: InternalAlignment(g6,g9)
    c: InternalAlignment(g7,g9)
    c: InternalAlignment(g8,g9)
    c: InternalAlignment(g10,g9)
    c: InternalAlignment(g11,g9)
    c: Coincident(g12,g5)
    c: Horizontal(g12)
    c: PointOnObject(g13,g-1)
    c: Coincident(g13,g12)
    c: Coincident(g2,g13)
    c: Tangent(g13,g12)
    c: DistanceX(g1,g2) = 9
    c: PointOnObject(g5,g1)
    c: Coincident(g8,g5)
    c: Radius(g3) = 7.5
    c: Radius(g13) = 3.5
    c: Distance(g2) = 35
    c: Coincident(g14,g13)
    c: Coincident(g14,g4)
    c: Parallel(g14,g4)
FEATURE [PartDesign::Pad] Pad038
  AllowMultiFace = false
  Length = 5.8
  Length2 = 100
  Profile = -> Sketch094
  Refine = true
  Type = 0
FEATURE [PartDesign::Mirrored] Mirrored009
  MirrorPlane = -> Sketch094 [H_Axis]
  Originals = -> [Pad038]
  Refine = true
FEATURE [Sketcher::SketchObject] Sketch093
  ExternalGeometry = -> [Mirrored009]
  MapMode = 5
  Placement = pos=(0,0,5.8) rot=(0,0,1;0rad)
  Support = -> [Mirrored009]
  expr: Constraints[6] = 3 / 2
  expr: Constraints[8] = 3 + 2
  expr: Constraints[9] = 3 + 5
  sketch-geometry (4):
    g0: Circle CenterX=0 CenterY=0 CenterZ=0 NormalX=0 NormalY=0 NormalZ=1 AngleXU=0 Radius=3
    g1: Circle CenterX=24 CenterY=0 CenterZ=0 NormalX=0 NormalY=0 NormalZ=1 AngleXU=0 Radius=1.5
    g2: Circle CenterX=19 CenterY=0 CenterZ=0 NormalX=0 NormalY=0 NormalZ=1 AngleXU=0 Radius=1.5
    g3: Circle CenterX=11 CenterY=0 CenterZ=0 NormalX=0 NormalY=0 NormalZ=1 AngleXU=0 Radius=1.5
  constraints (11):
    c: Coincident(g0,g-1)
    c: PointOnObject(g1,g-1)
    c: PointOnObject(g2,g-1)
    c: PointOnObject(g3,g-1)
    c: Equal(g3,g2)
    c: Equal(g2,g1)
    c: Radius(g1) = 1.5
    c: DistanceX(g1,g-3) = 3.5
    c: DistanceX(g2,g1) = 5
    c: DistanceX(g3,g2) = 8
    c: Radius(g0) = 3
FEATURE [PartDesign::Pocket] Pocket047
  AllowMultiFace = false
  BaseFeature = -> Mirrored009
  Length = 5
  Length2 = 100
  Profile = -> Sketch093
  Refine = true
  Type = 1
FEATURE [Sketcher::SketchObject] Sketch091
  ExternalGeometry = -> [Pocket047]
  MapMode = 5
  Placement = pos=(0,0,0) rot=(1,0,0;3.14159rad)
  Support = -> [Pocket047]
  sketch-geometry (8):
    g0: LineSegment StartX=2.34371 StartY=7.1244 StartZ=0 EndX=2.34371 EndY=8.1244 EndZ=0
    g1: LineSegment StartX=2.34371 StartY=8.1244 StartZ=0 EndX=18.5 EndY=8.1244 EndZ=0
    g2: LineSegment StartX=18.5 StartY=8.1244 StartZ=0 EndX=18.5 EndY=3.5 EndZ=0
    g3: LineSegment StartX=2.34371 StartY=-7.1244 StartZ=0 EndX=2.34371 EndY=-8.1244 EndZ=0
    g4: LineSegment StartX=2.34371 StartY=-8.1244 StartZ=0 EndX=18.5 EndY=-8.1244 EndZ=0
    g5: LineSegment StartX=18.5 StartY=-8.1244 StartZ=0 EndX=18.5 EndY=-3.5 EndZ=0
    g6: ArcOfCircle CenterX=0 CenterY=0 CenterZ=0 NormalX=0 NormalY=0 NormalZ=1 AngleXU=0 Radius=7.5 StartAngle=5.03021 EndAngle=7.53616
    g7: ArcOfCircle CenterX=18.5 CenterY=0 CenterZ=0 NormalX=0 NormalY=0 NormalZ=1 AngleXU=0 Radius=3.5 StartAngle=1.57079 EndAngle=4.71239
  constraints (22):
    c: Vertical(g0)
    c: Coincident(g1,g0)
    c: Horizontal(g1)
    c: Coincident(g2,g1)
    c: Vertical(g2)
    c: Coincident(g2,g-5)
    c: Coincident(g0,g-3)
    c: Coincident(g3,g-4)
    c: Vertical(g3)
    c: Coincident(g4,g3)
    c: Horizontal(g4)
    c: Coincident(g5,g4)
    c: Coincident(g5,g-6)
    c: Vertical(g5)
    c: Equal(g5,g2)
    c: Distance(g0) = 1
    c: Coincident(g6,g0)
    c: Coincident(g6,g3)
    c: Coincident(g7,g2)
    c: Coincident(g7,g5)
    c: Tangent(g6,g-3)
    c: Tangent(g-5,g7)
FEATURE [PartDesign::Pocket] Pocket046
  AllowMultiFace = false
  BaseFeature = -> Pocket047
  Length = 2
  Length2 = 100
  Profile = -> Sketch091
  Refine = true
  Type = 0
FEATURE [Sketcher::SketchObject] Sketch092
  ExternalGeometry = -> [Pocket046]
  MapMode = 5
  Placement = pos=(0,0,0) rot=(1,0,0;3.14159rad)
  Support = -> [Pocket046]
  sketch-geometry (8):
    g0: LineSegment StartX=6.5 StartY=7.1244 StartZ=0 EndX=8.5 EndY=7.1244 EndZ=0
    g1: LineSegment StartX=8.5 StartY=7.1244 StartZ=0 EndX=8.5 EndY=-7.1244 EndZ=0
    g2: LineSegment StartX=8.5 StartY=-7.1244 StartZ=0 EndX=6.5 EndY=-7.1244 EndZ=0
    g3: LineSegment StartX=6.5 StartY=-7.1244 StartZ=0 EndX=6.5 EndY=7.1244 EndZ=0
    g4: LineSegment [constr] StartX=7.5 StartY=0 StartZ=0 EndX=6.5 EndY=0 EndZ=0
    g5: LineSegment [constr] StartX=2.34371 StartY=7.1244 StartZ=0 EndX=6.5 EndY=7.1244 EndZ=0
    g6: LineSegment [constr] StartX=6.5 StartY=7.1244 StartZ=0 EndX=6.5 EndY=0 EndZ=0
    g7: LineSegment [constr] StartX=6.5 StartY=0 StartZ=0 EndX=6.5 EndY=-7.1244 EndZ=0
  constraints (21):
    c: Coincident(g0,g1)
    c: Coincident(g1,g2)
    c: Coincident(g2,g3)
    c: Coincident(g3,g0)
    c: Horizontal(g0)
    c: Horizontal(g2)
    c: Vertical(g1)
    c: Vertical(g3)
    c: Coincident(g4,g-3)
    c: PointOnObject(g4,g3)
    c: Horizontal(g4)
    c: Distance(g4) = 1
    c: Coincident(g5,g-3)
    c: Coincident(g5,g0)
    c: Horizontal(g5)
    c: Coincident(g6,g0)
    c: Coincident(g6,g4)
    c: Coincident(g7,g4)
    c: Coincident(g7,g2)
    c: Equal(g6,g7)
    c: DistanceX(g4,g1) = 1
FEATURE [PartDesign::Pocket] Pocket045
  AllowMultiFace = false
  BaseFeature = -> Pocket046
  Length = 0
  Length2 = 100
  Profile = -> Sketch092
  Refine = true
  Type = 2
FEATURE [PartDesign::Body] Body014
  Group = -> [Sketch094,Pad038,Mirrored009,Sketch093,Pocket047,Sketch091,Pocket046,Sketch092,Pocket045]
  Origin = -> Origin014
  Placement = pos=(24.9,0,-203.8) rot=(0,-1,0;1.5708rad)
  Tip = -> Pocket045
FEATURE [Sketcher::SketchObject] Sketch099
  MapMode = 5
  Support = -> [XY_Plane015]
  expr: Constraints[67] = 2.5 / 2
  sketch-geometry (26):
    g0: LineSegment [constr] StartX=-5.1 StartY=0 StartZ=0 EndX=-5.1 EndY=-5.1 EndZ=0
    g1: LineSegment [constr] StartX=-5.1 StartY=-5.1 StartZ=0 EndX=0 EndY=-5.1 EndZ=0
    g2: LineSegment [constr] StartX=-5.1 StartY=0 StartZ=0 EndX=-5.1 EndY=5.1 EndZ=0
    g3: LineSegment [constr] StartX=0 StartY=-5.1 StartZ=0 EndX=5.1 EndY=-5.1 EndZ=0
    g4: ArcOfCircle CenterX=-5.1 CenterY=-5.1 CenterZ=0 NormalX=0 NormalY=0 NormalZ=1 AngleXU=0 Radius=0.5 StartAngle=1.5708 EndAngle=6.28319
    g5: ArcOfCircle CenterX=-5.1 CenterY=-5.1 CenterZ=0 NormalX=0 NormalY=0 NormalZ=1 AngleXU=0 Radius=2.5 StartAngle=2.49809 EndAngle=5.35589
    g6: LineSegment [constr] StartX=-5.1 StartY=5.1 StartZ=0 EndX=-1.25 EndY=5.1 EndZ=0
    g7: ArcOfCircle CenterX=-5.1 CenterY=5.1 CenterZ=0 NormalX=0 NormalY=0 NormalZ=1 AngleXU=0 Radius=0.5 StartAngle=-9e-16 EndAngle=4.71239
    g8: ArcOfCircle CenterX=-5.1 CenterY=5.1 CenterZ=0 NormalX=0 NormalY=0 NormalZ=1 AngleXU=0 Radius=2.5 StartAngle=0.927295 EndAngle=3.78509
    g9: LineSegment StartX=-7.1 StartY=3.6 StartZ=0 EndX=-7.1 EndY=-3.6 EndZ=0
    g10: LineSegment [constr] StartX=-5.1 StartY=5.1 StartZ=0 EndX=-5.6 EndY=5.1 EndZ=0
    g11: LineSegment [constr] StartX=-5.6 StartY=5.1 StartZ=0 EndX=-7.6 EndY=5.1 EndZ=0
    g12: LineSegment [constr] StartX=-5.1 StartY=-5.1 StartZ=0 EndX=-5.6 EndY=-5.1 EndZ=0
    g13: LineSegment [constr] StartX=-5.6 StartY=-5.1 StartZ=0 EndX=-7.6 EndY=-5.1 EndZ=0
    g14: LineSegment [constr] StartX=-5.1 StartY=0 StartZ=0 EndX=-7.1 EndY=0 EndZ=0
    g15: LineSegment [constr] StartX=-3.6 StartY=7.1 StartZ=0 EndX=-3.6 EndY=5.1 EndZ=0
    g16: LineSegment StartX=-3.6 StartY=-7.1 StartZ=0 EndX=0 EndY=-7.1 EndZ=0
    g17: LineSegment [constr] StartX=-3.6 StartY=-7.1 StartZ=0 EndX=-3.6 EndY=-5.1 EndZ=0
    g18: LineSegment StartX=-5.1 StartY=4.6 StartZ=0 EndX=-5.1 EndY=-4.6 EndZ=0
    g19: LineSegment StartX=-4.6 StartY=-5.1 StartZ=0 EndX=0 EndY=-5.1 EndZ=0
    g20: LineSegment StartX=-4.6 StartY=5.1 StartZ=0 EndX=-1.25 EndY=5.1 EndZ=0
    g21: LineSegment StartX=0 StartY=-5.1 StartZ=0 EndX=0 EndY=-7.1 EndZ=0
    g22: LineSegment StartX=-1.25 StartY=25.1 StartZ=0 EndX=-1.25 EndY=5.1 EndZ=0
    g23: LineSegment StartX=-3.6 StartY=7.1 StartZ=0 EndX=-3.25 EndY=7.1 EndZ=0
    g24: LineSegment StartX=-3.25 StartY=7.1 StartZ=0 EndX=-3.25 EndY=25.1 EndZ=0
    g25: LineSegment StartX=-3.25 StartY=25.1 StartZ=0 EndX=-1.25 EndY=25.1 EndZ=0
  constraints (77):
    c: PointOnObject(g0,g-1)
    c: Vertical(g0)
    c: Coincident(g1,g0)
    c: PointOnObject(g1,g-2)
    c: Horizontal(g1)
    c: Coincident(g2,g0)
    c: Vertical(g2)
    c: Equal(g2,g0)
    c: Coincident(g3,g1)
    c: Horizontal(g3)
    c: Equal(g3,g1)
    c: Equal(g0,g1)
    c: DistanceX(g0,g3) = 10.2
    c: Coincident(g4,g0)
    c: PointOnObject(g4,g1)
    c: PointOnObject(g4,g0)
    c: Coincident(g5,g4)
    c: Coincident(g6,g2)
    c: Horizontal(g6)
    c: Coincident(g7,g2)
    c: PointOnObject(g7,g2)
    c: PointOnObject(g7,g6)
    c: Coincident(g8,g7)
    c: Coincident(g9,g8)
    c: Coincident(g9,g5)
    c: Vertical(g9)
    c: Coincident(g10,g7)
    c: PointOnObject(g10,g7)
    c: Horizontal(g10)
    c: Coincident(g11,g10)
    c: PointOnObject(g11,g8)
    c: Horizontal(g11)
    c: Distance(g11) = 2
    c: Coincident(g12,g4)
    c: PointOnObject(g12,g4)
    c: Coincident(g13,g12)
    c: PointOnObject(g13,g5)
    c: Horizontal(g13)
    c: Horizontal(g12)
    c: Equal(g13,g11)
    c: Equal(g4,g7)
    c: Coincident(g14,g0)
    c: Horizontal(g14)
    c: PointOnObject(g14,g9)
    c: Equal(g14,g11)
    c: Radius(g4) = 0.5
    c: Coincident(g15,g8)
    c: PointOnObject(g15,g6)
    c: Vertical(g15)
    c: Equal(g15,g11)
    c: Coincident(g16,g5)
    c: PointOnObject(g16,g-2)
    c: Horizontal(g16)
    c: Coincident(g17,g5)
    c: PointOnObject(g17,g1)
    c: Vertical(g17)
    c: Equal(g17,g11)
    c: Coincident(g18,g7)
    c: Coincident(g18,g4)
    c: Coincident(g19,g4)
    c: Coincident(g19,g1)
    c: Coincident(g20,g7)
    c: Coincident(g20,g6)
    c: Coincident(g21,g19)
    c: Coincident(g21,g16)
    c: Coincident(g22,g20)
    c: Vertical(g22)
    c: DistanceX(g20,g-1) = 1.25
    c: Coincident(g23,g8)
    c: Horizontal(g23)
    c: Coincident(g24,g23)
    c: Vertical(g24)
    c: Coincident(g25,g24)
    c: Coincident(g25,g22)
    c: Horizontal(g25)
    c: Equal(g25,g15)
    c: Distance(g22) = 20
FEATURE [PartDesign::Pad] Pad041
  AllowMultiFace = false
  Length = 7.5
  Length2 = 100
  Profile = -> Sketch099
  Type = 0
FEATURE [Sketcher::SketchObject] Sketch096
  ExternalGeometry = -> [Pad041]
  MapMode = 5
  Placement = pos=(-1.25,0,0) rot=(0.57735,0.57735,0.57735;2.0944rad)
  Support = -> [Pad041]
  expr: Constraints[7] = 4.8 + 0.4 + 1
  sketch-geometry (8):
    g0: Circle CenterX=18.9 CenterY=2.85 CenterZ=0 NormalX=0 NormalY=0 NormalZ=1 AngleXU=0 Radius=1
    g1: Circle CenterX=9.9 CenterY=2.85 CenterZ=0 NormalX=0 NormalY=0 NormalZ=1 AngleXU=0 Radius=1
    g2: LineSegment [constr] StartX=18.9 StartY=2.85 StartZ=0 EndX=25.1 EndY=2.85 EndZ=0
    g3: LineSegment [constr] StartX=18.9 StartY=2.85 StartZ=0 EndX=18.9 EndY=0 EndZ=0
    g4: LineSegment [constr] StartX=9.9 StartY=2.85 StartZ=0 EndX=9.9 EndY=0 EndZ=0
    g5: LineSegment [constr] StartX=9.9 StartY=2.85 StartZ=0 EndX=5.1 EndY=2.85 EndZ=0
    g6: LineSegment [constr] StartX=19.9 StartY=2.85 StartZ=0 EndX=25.1 EndY=2.85 EndZ=0
    g7: LineSegment [constr] StartX=17.9 StartY=2.85 StartZ=0 EndX=10.9 EndY=2.85 EndZ=0
  constraints (25):
    c: Horizontal(g2)
    c: PointOnObject(g2,g-3)
    c: Coincident(g2,g0)
    c: Coincident(g3,g0)
    c: PointOnObject(g3,g-1)
    c: Vertical(g3)
    c: Distance(g3) = 2.85
    c: Distance(g2) = 6.2
    c: Radius(g0) = 1
    c: PointOnObject(g4,g-1)
    c: Coincident(g5,g1)
    c: Horizontal(g5)
    c: Coincident(g4,g1)
    c: Vertical(g4)
    c: Equal(g4,g3)
    c: Equal(g1,g0)
    c: PointOnObject(g6,g0)
    c: Coincident(g6,g2)
    c: Horizontal(g6)
    c: PointOnObject(g7,g2)
    c: PointOnObject(g7,g1)
    c: Horizontal(g7)
    c: PointOnObject(g7,g0)
    c: DistanceX(g5,g2) = 20
    c: Distance(g5) = 4.8
FEATURE [PartDesign::Pad] Pad039
  AllowMultiFace = false
  BaseFeature = -> Pad041
  Length = 1
  Length2 = 100
  Profile = -> Sketch096
  Type = 0
FEATURE [Sketcher::SketchObject] Sketch097
  ExternalGeometry = -> [Pad039]
  MapMode = 5
  Placement = pos=(-0.25,0,0) rot=(0.57735,0.57735,0.57735;2.0944rad)
  Support = -> [Pad039]
  sketch-geometry (2):
    g0: Circle CenterX=18.9 CenterY=2.85 CenterZ=0 NormalX=0 NormalY=0 NormalZ=1 AngleXU=0 Radius=1.6
    g1: Circle CenterX=9.9 CenterY=2.85 CenterZ=0 NormalX=0 NormalY=0 NormalZ=1 AngleXU=0 Radius=1.6
  constraints (4):
    c: Coincident(g0,g-4)
    c: Coincident(g1,g-3)
    c: Equal(g1,g0)
    c: Radius(g1) = 1.6
FEATURE [PartDesign::Pocket] Pocket049
  AllowMultiFace = false
  BaseFeature = -> Pad039
  Length = 5
  Length2 = 100
  Profile = -> Sketch097
  Type = 0
FEATURE [PartDesign::Mirrored] Mirrored010
  BaseFeature = -> Pocket049
  MirrorPlane = -> Sketch099 [V_Axis]
  Originals = -> [Pad041]
FEATURE [PartDesign::Mirrored] Mirrored011
  BaseFeature = -> Mirrored010
  MirrorPlane = -> YZ_Plane015
  Originals = -> [Pad039]
FEATURE [PartDesign::Mirrored] Mirrored012
  BaseFeature = -> Mirrored011
  MirrorPlane = -> YZ_Plane015
  Originals = -> [Pocket049]
FEATURE [PartDesign::Fillet] Fillet021
  Base = -> Mirrored012 [Edge1,Edge2,Edge76,Edge77,Edge8,Edge36,Edge78,Edge75]
  BaseFeature = -> Mirrored012
  Radius = 1
  SupportTransform = false
FEATURE [PartDesign::Fillet] Fillet022
  Base = -> Fillet021 [Edge73,Edge55,Edge74,Edge114,Edge113,Edge112]
  BaseFeature = -> Fillet021
  Radius = 2
  SupportTransform = false
FEATURE [Sketcher::SketchObject] Sketch098
  ExternalGeometry = -> [Fillet022]
  MapMode = 5
  Placement = pos=(0,25.1,0) rot=(0,0.707107,0.707107;3.14159rad)
  Support = -> [Fillet022]
  sketch-geometry (4):
    g0: LineSegment StartX=3.25 StartY=7.5 StartZ=0 EndX=-0.5 EndY=7.5 EndZ=0
    g1: LineSegment StartX=-0.5 StartY=7.5 StartZ=0 EndX=-0.5 EndY=0 EndZ=0
    g2: LineSegment StartX=-0.5 StartY=0 StartZ=0 EndX=3.25 EndY=0 EndZ=0
    g3: LineSegment StartX=3.25 StartY=0 StartZ=0 EndX=3.25 EndY=7.5 EndZ=0
  constraints (11):
    c: Coincident(g0,g1)
    c: Coincident(g1,g2)
    c: Coincident(g2,g3)
    c: Coincident(g3,g0)
    c: Horizontal(g0)
    c: Horizontal(g2)
    c: Vertical(g1)
    c: Vertical(g3)
    c: Coincident(g0,g-3)
    c: PointOnObject(g1,g-1)
    c: Distance(g0) = 3.75
FEATURE [PartDesign::Pad] Pad040
  AllowMultiFace = false
  BaseFeature = -> Fillet022
  Length = 2
  Length2 = 100
  Profile = -> Sketch098
  Type = 0
FEATURE [PartDesign::Fillet] Fillet020
  Base = -> Pad040 [Edge62,Edge119,Edge37,Edge96,Edge93]
  BaseFeature = -> Pad040
  Radius = 1
  SupportTransform = false
FEATURE [PartDesign::Body] Body015
  Group = -> [Sketch099,Pad041,Sketch096,Pad039,Sketch097,Pocket049,Mirrored010,Mirrored011,Mirrored012,Fillet021,Fillet022,Sketch098,Pad040,Fillet020]
  Origin = -> Origin015
  Placement = pos=(35.9,-37.5,-218.8) rot=(0,0.707107,0.707107;3.14159rad)
  Tip = -> Fillet020
FEATURE [PartDesign::FeatureBase] Clone006
  BaseFeature = -> Body015
  Placement = pos=(0,0,0) rot=(1,0,0;1.5708rad)
FEATURE [PartDesign::Body] Body019
  BaseFeature = -> Body015
  Group = -> [Clone006]
  Origin = -> Origin019
  Placement = pos=(35.9,-217.5,-218.8) rot=(0,0,1;3.14159rad)
  Tip = -> Clone006
FEATURE [PartDesign::FeatureBase] Clone007
  BaseFeature = -> Body014
  Placement = pos=(0,0,0) rot=(0,-1,0;1.5708rad)
FEATURE [PartDesign::Body] Body020
  BaseFeature = -> Body014
  Group = -> [Clone007]
  Origin = -> Origin020
  Placement = pos=(24.9,-200,-203.8) rot=(1,0,0;3.14159rad)
  Tip = -> Clone007
FEATURE [PartDesign::FeatureBase] Clone008
  BaseFeature = -> Body015
  Placement = pos=(0,0,0) rot=(0,0.707107,0.707107;3.14159rad)
FEATURE [PartDesign::Body] Body021
  BaseFeature = -> Body015
  Group = -> [Clone008]
  Origin = -> Origin021
  Tip = -> Clone008
FEATURE [Part::Mirroring] Part__Mirroring  label="Body021 (Mirror #1)"
  Base = (0,0,0)
  Normal = (0,1,0)
  Placement = pos=(35.9,17.5,-218.8) rot=(0,0,1;0rad)
  Source = -> Body021
FEATURE [PartDesign::FeatureBase] Clone009
  BaseFeature = -> Body015
  Placement = pos=(0,0,0) rot=(0,0.707107,0.707107;3.14159rad)
FEATURE [PartDesign::Body] Body022
  BaseFeature = -> Body015
  Group = -> [Clone009]
  Origin = -> Origin022
  Tip = -> Clone009
FEATURE [Part::Mirroring] Part__Mirroring001  label="Body022 (Mirror #2)"
  Base = (0,0,0)
  Normal = (0,1,0)
  Placement = pos=(35.9,-162.5,-218.8) rot=(0,0,1;0rad)
  Source = -> Body022
FEATURE [Sketcher::SketchObject] Sketch108
  MapMode = 5
  Support = -> [XY_Plane023]
  sketch-geometry (8):
    g0: LineSegment StartX=-20 StartY=10 StartZ=0 EndX=20 EndY=10 EndZ=0
    g1: LineSegment StartX=20 StartY=10 StartZ=0 EndX=20 EndY=-10 EndZ=0
    g2: LineSegment StartX=20 StartY=-10 StartZ=0 EndX=-20 EndY=-10 EndZ=0
    g3: LineSegment StartX=-20 StartY=-10 StartZ=0 EndX=-20 EndY=10 EndZ=0
    g4: LineSegment [constr] StartX=0 StartY=10 StartZ=0 EndX=0 EndY=0 EndZ=0
    g5: LineSegment [constr] StartX=0 StartY=0 StartZ=0 EndX=0 EndY=-10 EndZ=0
    g6: LineSegment [constr] StartX=0 StartY=0 StartZ=0 EndX=-20 EndY=0 EndZ=0
    g7: LineSegment [constr] StartX=0 StartY=0 StartZ=0 EndX=20 EndY=0 EndZ=0
  constraints (24):
    c: Coincident(g0,g1)
    c: Coincident(g1,g2)
    c: Coincident(g2,g3)
    c: Coincident(g3,g0)
    c: Horizontal(g0)
    c: Horizontal(g2)
    c: Vertical(g1)
    c: Vertical(g3)
    c: PointOnObject(g4,g0)
    c: Coincident(g4,g-1)
    c: Vertical(g4)
    c: Coincident(g5,g-1)
    c: PointOnObject(g5,g2)
    c: Vertical(g5)
    c: Equal(g4,g5)
    c: Distance(g2) = 40
    c: Distance(g3) = 20
    c: Coincident(g6,g-1)
    c: PointOnObject(g6,g3)
    c: Horizontal(g6)
    c: Coincident(g7,g-1)
    c: PointOnObject(g7,g1)
    c: Horizontal(g7)
    c: Equal(g7,g6)
FEATURE [PartDesign::Pad] Pad046
  AllowMultiFace = false
  Length = 27.4
  Length2 = 100
  Profile = -> Sketch108
  Refine = true
  Reversed = true
  Type = 0
FEATURE [Sketcher::SketchObject] Sketch109
  ExternalGeometry = -> [Pad046]
  MapMode = 5
  Support = -> [Pad046]
  sketch-geometry (7):
    g0: LineSegment StartX=-27.5 StartY=10 StartZ=0 EndX=27.5 EndY=10 EndZ=0
    g1: LineSegment StartX=27.5 StartY=10 StartZ=0 EndX=27.5 EndY=-10 EndZ=0
    g2: LineSegment StartX=27.5 StartY=-10 StartZ=0 EndX=-27.5 EndY=-10 EndZ=0
    g3: LineSegment StartX=-27.5 StartY=-10 StartZ=0 EndX=-27.5 EndY=10 EndZ=0
    g4: LineSegment [constr] StartX=-27.5 StartY=10 StartZ=0 EndX=-20 EndY=10 EndZ=0
    g5: LineSegment [constr] StartX=20 StartY=10 StartZ=0 EndX=27.5 EndY=10 EndZ=0
    g6: LineSegment [constr] StartX=27.5 StartY=-10 StartZ=0 EndX=20 EndY=-10 EndZ=0
  constraints (19):
    c: Coincident(g0,g1)
    c: Coincident(g1,g2)
    c: Coincident(g3,g0)
    c: Horizontal(g0)
    c: Horizontal(g2)
    c: Vertical(g1)
    c: Vertical(g3)
    c: Coincident(g4,g0)
    c: Coincident(g4,g-4)
    c: Coincident(g5,g-3)
    c: Coincident(g5,g0)
    c: Coincident(g6,g1)
    c: Coincident(g6,g-5)
    c: Horizontal(g6)
    c: Horizontal(g5)
    c: Coincident(g3,g2)
    c: Equal(g4,g5)
    c: Equal(g5,g6)
    c: Distance(g4) = 7.5
FEATURE [PartDesign::Pad] Pad048
  AllowMultiFace = false
  BaseFeature = -> Pad046
  Length = 2.5
  Length2 = 100
  Profile = -> Sketch109
  Refine = true
  Type = 0
FEATURE [Sketcher::SketchObject] Sketch110
  ExternalGeometry = -> [Pad048]
  MapMode = 5
  Placement = pos=(0,0,2.5) rot=(0,0,1;0rad)
  Support = -> [Pad048]
  sketch-geometry (4):
    g0: LineSegment StartX=-20 StartY=-10 StartZ=0 EndX=-20 EndY=10 EndZ=0
    g1: LineSegment StartX=-20 StartY=10 StartZ=0 EndX=20 EndY=10 EndZ=0
    g2: LineSegment StartX=20 StartY=10 StartZ=0 EndX=20 EndY=-10 EndZ=0
    g3: LineSegment StartX=20 StartY=-10 StartZ=0 EndX=-20 EndY=-10 EndZ=0
  constraints (8):
    c: Coincident(g1,g0)
    c: Coincident(g3,g0)
    c: Coincident(g1,g-3)
    c: Coincident(g2,g1)
    c: Coincident(g2,g-6)
    c: Coincident(g3,g2)
    c: Coincident(g0,g-5)
    c: Coincident(g0,g-4)
FEATURE [PartDesign::Pad] Pad047
  AllowMultiFace = false
  BaseFeature = -> Pad048
  Length = 7.5
  Length2 = 100
  Profile = -> Sketch110
  Refine = true
  Type = 0
FEATURE [PartDesign::Chamfer] Chamfer006
  Angle = 45
  Base = -> Pad047 [Edge38,Edge36,Edge33,Edge31]
  BaseFeature = -> Pad047
  ChamferType = 0
  FlipDirection = false
  Refine = true
  Size = 6
  Size2 = 1
  SupportTransform = false
FEATURE [Sketcher::SketchObject] Sketch107
  ExternalGeometry = -> [Chamfer006]
  MapMode = 5
  Placement = pos=(0,0,10) rot=(0,0,1;0rad)
  Support = -> [Chamfer006]
  expr: Constraints[1] = 13 / 2
  sketch-geometry (2):
    g0: Circle CenterX=-10 CenterY=0 CenterZ=0 NormalX=0 NormalY=0 NormalZ=1 AngleXU=0 Radius=6.5
    g1: GeomPoint X=-16.5 Y=0 Z=0
  constraints (5):
    c: PointOnObject(g0,g-1)
    c: Radius(g0) = 6.5
    c: PointOnObject(g1,g-1)
    c: PointOnObject(g1,g0)
    c: DistanceX(g-3,g1) = 3.5
FEATURE [PartDesign::Pad] Pad045
  AllowMultiFace = false
  BaseFeature = -> Chamfer006
  Length = 2.2
  Length2 = 100
  Profile = -> Sketch107
  Refine = true
  Type = 0
FEATURE [Sketcher::SketchObject] Sketch101
  ExternalGeometry = -> [Pad045]
  MapMode = 5
  Placement = pos=(0,0,10) rot=(0,0,1;0rad)
  Support = -> [Pad045]
  sketch-geometry (5):
    g0: LineSegment StartX=-10 StartY=3 StartZ=0 EndX=13.5 EndY=3 EndZ=0
    g1: LineSegment StartX=13.5 StartY=3 StartZ=0 EndX=13.5 EndY=-3 EndZ=0
    g2: LineSegment StartX=13.5 StartY=-3 StartZ=0 EndX=-10 EndY=-3 EndZ=0
    g3: LineSegment StartX=-10 StartY=3 StartZ=0 EndX=-10 EndY=0 EndZ=0
    g4: LineSegment StartX=-10 StartY=-3 StartZ=0 EndX=-10 EndY=0 EndZ=0
  constraints (14):
    c: Coincident(g0,g1)
    c: Coincident(g1,g2)
    c: Horizontal(g0)
    c: Horizontal(g2)
    c: Vertical(g1)
    c: Coincident(g3,g0)
    c: Coincident(g3,g-3)
    c: Coincident(g4,g2)
    c: Coincident(g4,g3)
    c: Vertical(g4)
    c: Vertical(g3)
    c: Equal(g3,g4)
    c: DistanceY(g1,g1) = 6
    c: DistanceX(g0,g-4) = 6.5
FEATURE [PartDesign::Pad] Pad044
  AllowMultiFace = false
  BaseFeature = -> Pad045
  Length = 1.5
  Length2 = 100
  Profile = -> Sketch101
  Refine = true
  Type = 0
FEATURE [Sketcher::SketchObject] Sketch103
  ExternalGeometry = -> [Pad044]
  MapMode = 5
  Placement = pos=(0,0,12.2) rot=(0,0,1;0rad)
  Support = -> [Pad044]
  expr: Constraints[1] = 6 / 2
  sketch-geometry (1):
    g0: Circle CenterX=-10 CenterY=0 CenterZ=0 NormalX=0 NormalY=0 NormalZ=1 AngleXU=0 Radius=3
  constraints (2):
    c: Coincident(g0,g-3)
    c: Radius(g0) = 3
FEATURE [PartDesign::Pad] Pad042
  AllowMultiFace = false
  BaseFeature = -> Pad044
  Length = 4
  Length2 = 100
  Profile = -> Sketch103
  Refine = true
  Type = 0
FEATURE [Sketcher::SketchObject] Sketch106
  ExternalGeometry = -> [Pad042]
  MapMode = 5
  Placement = pos=(0,0,2.5) rot=(0,0,1;0rad)
  Support = -> [Pad042]
  expr: Constraints[8] = 4.3 / 2
  sketch-geometry (7):
    g0: LineSegment StartX=28.5 StartY=-3.7 StartZ=0 EndX=28.5 EndY=-6.7 EndZ=0
    g1: ArcOfCircle CenterX=24.65 CenterY=-5.2 CenterZ=0 NormalX=0 NormalY=0 NormalZ=1 AngleXU=0 Radius=2.15 StartAngle=0.772146 EndAngle=5.51104
    g2: LineSegment [constr] StartX=24.65 StartY=-5.2 StartZ=0 EndX=22.5 EndY=-5.2 EndZ=0
    g3: LineSegment StartX=28.5 StartY=-3.7 StartZ=0 EndX=26.1903 EndY=-3.7 EndZ=0
    g4: LineSegment StartX=28.5 StartY=-6.7 StartZ=0 EndX=26.1903 EndY=-6.7 EndZ=0
    g5: LineSegment [constr] StartX=24.65 StartY=-5.2 StartZ=0 EndX=26.1903 EndY=-3.7 EndZ=0
    g6: LineSegment [constr] StartX=24.65 StartY=-5.2 StartZ=0 EndX=26.1903 EndY=-6.7 EndZ=0
  constraints (20):
    c: Vertical(g0)
    c: Distance(g0) = 3
    c: DistanceX(g-3,g0) = 1
    c: DistanceY(g-3,g0) = 3.3
    c: Coincident(g2,g1)
    c: Horizontal(g2)
    c: PointOnObject(g2,g1)
    c: DistanceX(g2,g-3) = 5
    c: Radius(g1) = 2.15
    c: Coincident(g3,g0)
    c: Horizontal(g3)
    c: Coincident(g4,g0)
    c: Horizontal(g4)
    c: Equal(g4,g3)
    c: Coincident(g5,g1)
    c: Coincident(g5,g3)
    c: Coincident(g6,g1)
    c: Coincident(g6,g4)
    c: Coincident(g3,g1)
    c: Coincident(g4,g1)
FEATURE [PartDesign::Mirrored] Mirrored001
  MirrorPlane = -> Sketch106 [V_Axis]
  Refine = true
FEATURE [PartDesign::Pocket] Pocket053
  AllowMultiFace = false
  BaseFeature = -> Pad042
  Length = 5
  Length2 = 100
  Profile = -> Sketch106
  Refine = true
  Type = 1
FEATURE [Sketcher::SketchObject] Sketch100
  ExternalGeometry = -> [Pocket053]
  MapMode = 5
  Placement = pos=(0,0,-27.4) rot=(1,0,0;3.14159rad)
  Support = -> [Pocket053]
  sketch-geometry (9):
    g0: LineSegment StartX=20 StartY=10 StartZ=0 EndX=16 EndY=10 EndZ=0
    g1: LineSegment [constr] StartX=16 StartY=10 StartZ=0 EndX=16 EndY=6 EndZ=0
    g2: LineSegment [constr] StartX=16 StartY=6 StartZ=0 EndX=20 EndY=6 EndZ=0
    g3: LineSegment StartX=20 StartY=6 StartZ=0 EndX=20 EndY=10 EndZ=0
    g4: ArcOfCircle CenterX=18 CenterY=8 CenterZ=0 NormalX=0 NormalY=0 NormalZ=1 AngleXU=0 Radius=2 StartAngle=3.14159 EndAngle=4.71239
    g5: LineSegment [constr] StartX=16 StartY=8 StartZ=0 EndX=18 EndY=8 EndZ=0
    g6: LineSegment [constr] StartX=18 StartY=6 StartZ=0 EndX=18 EndY=8 EndZ=0
    g7: LineSegment StartX=16 StartY=8 StartZ=0 EndX=16 EndY=10 EndZ=0
    g8: LineSegment StartX=18 StartY=6 StartZ=0 EndX=20 EndY=6 EndZ=0
  constraints (24):
    c: Coincident(g0,g1)
    c: Coincident(g1,g2)
    c: Coincident(g2,g3)
    c: Coincident(g3,g0)
    c: Horizontal(g0)
    c: Horizontal(g2)
    c: Vertical(g1)
    c: Vertical(g3)
    c: Coincident(g0,g-3)
    c: PointOnObject(g4,g1)
    c: PointOnObject(g4,g2)
    c: Coincident(g5,g4)
    c: Coincident(g5,g4)
    c: Coincident(g6,g4)
    c: Coincident(g6,g4)
    c: Vertical(g6)
    c: Horizontal(g5)
    c: Coincident(g7,g4)
    c: Coincident(g7,g0)
    c: Coincident(g8,g4)
    c: Coincident(g8,g2)
    c: Equal(g5,g8)
    c: DistanceX(g0,g0) = 4
    c: DistanceY(g3,g3) = 4
FEATURE [PartDesign::Mirrored] Mirrored003
  MirrorPlane = -> Sketch100 [V_Axis]
  Refine = true
FEATURE [PartDesign::Mirrored] Mirrored002
  MirrorPlane = -> Sketch100 [H_Axis]
  Refine = true
FEATURE [PartDesign::Mirrored] Mirrored013
  MirrorPlane = -> Sketch106 [H_Axis]
  Refine = true
FEATURE [PartDesign::MultiTransform] MultiTransform
  Originals = -> [Pocket053]
  Refine = true
  Transformations = -> [Mirrored013,Mirrored001]
FEATURE [PartDesign::Pocket] Pocket052
  AllowMultiFace = false
  BaseFeature = -> MultiTransform
  Length = 1
  Length2 = 100
  Profile = -> Sketch100
  Refine = true
  Type = 0
FEATURE [PartDesign::MultiTransform] MultiTransform001
  Originals = -> [Pocket052]
  Refine = true
  Transformations = -> [Mirrored002,Mirrored003]
FEATURE [PartDesign::Fillet] Fillet028
  Base = -> MultiTransform001 [Edge113,Edge109]
  BaseFeature = -> MultiTransform001
  Radius = 1
  Refine = true
  SupportTransform = false
FEATURE [PartDesign::Chamfer] Chamfer007
  Angle = 45
  Base = -> Fillet028 [Edge28,Edge29,Edge26,Edge19,Edge17]
  BaseFeature = -> Fillet028
  ChamferType = 0
  FlipDirection = false
  Refine = true
  Size = 0.5
  Size2 = 1
  SupportTransform = false
FEATURE [PartDesign::Fillet] Fillet024
  Base = -> Chamfer007 [Edge23,Edge4]
  BaseFeature = -> Chamfer007
  Radius = 1
  Refine = true
  SupportTransform = false
FEATURE [PartDesign::Chamfer] Chamfer002
  Angle = 45
  Base = -> Fillet024 [Edge36]
  BaseFeature = -> Fillet024
  ChamferType = 0
  FlipDirection = false
  Refine = true
  Size = 0.5
  Size2 = 1
  SupportTransform = false
FEATURE [PartDesign::Chamfer] Chamfer003
  Angle = 45
  Base = -> Chamfer002 [Edge36,Edge38,Edge40,Edge39,Edge37,Edge35,Edge33,Edge34]
  BaseFeature = -> Chamfer002
  ChamferType = 0
  FlipDirection = false
  Refine = true
  Size = 1
  Size2 = 1
  SupportTransform = false
FEATURE [PartDesign::Fillet] Fillet025
  Base = -> Chamfer003 [Edge83,Edge115,Edge114,Edge88]
  BaseFeature = -> Chamfer003
  Radius = 1
  Refine = true
  SupportTransform = false
FEATURE [PartDesign::Chamfer] Chamfer004
  Angle = 45
  Base = -> Fillet025 [Edge3,Edge14,Edge16,Edge18,Edge20,Edge22,Edge24,Edge26,Edge19,Edge53,Edge58,Edge56,Edge60,Edge61,Edge64,Edge62,Edge66,Edge7]
  BaseFeature = -> Fillet025
  ChamferType = 0
  FlipDirection = false
  Refine = true
  Size = 0.4
  Size2 = 1
  SupportTransform = false
FEATURE [PartDesign::Fillet] Fillet023
  Base = -> Chamfer004 [Edge39,Edge33,Edge92,Edge120]
  BaseFeature = -> Chamfer004
  Radius = 1
  Refine = true
  SupportTransform = false
FEATURE [PartDesign::Chamfer] Chamfer005
  Angle = 45
  Base = -> Fillet023 [Edge103,Edge42,Edge22,Edge35]
  BaseFeature = -> Fillet023
  ChamferType = 0
  FlipDirection = false
  Refine = true
  Size = 1
  Size2 = 1
  SupportTransform = false
FEATURE [Sketcher::SketchObject] Sketch102
  ExternalGeometry = -> [Chamfer005]
  MapMode = 5
  Placement = pos=(0,0,12.2) rot=(0,0,1;0rad)
  Support = -> [Chamfer005]
  sketch-geometry (3):
    g0: Circle CenterX=-10 CenterY=0 CenterZ=0 NormalX=0 NormalY=0 NormalZ=1 AngleXU=0 Radius=3.5
    g1: Circle CenterX=-10 CenterY=0 CenterZ=0 NormalX=0 NormalY=0 NormalZ=1 AngleXU=0 Radius=3
    g2: LineSegment [constr] StartX=-7 StartY=0 StartZ=0 EndX=-6.5 EndY=0 EndZ=0
  constraints (8):
    c: Coincident(g0,g-3)
    c: Coincident(g1,g0)
    c: Equal(g1,g-3)
    c: PointOnObject(g2,g1)
    c: PointOnObject(g2,g0)
    c: Horizontal(g2)
    c: PointOnObject(g2,g-1)
    c: DistanceX(g2,g2) = 0.5
FEATURE [PartDesign::Pocket] Pocket050
  AllowMultiFace = false
  BaseFeature = -> Chamfer005
  Length = 1
  Length2 = 100
  Profile = -> Sketch102
  Refine = true
  Type = 0
FEATURE [Sketcher::SketchObject] Sketch105
  ExternalGeometry = -> [Pocket050]
  MapMode = 5
  Placement = pos=(0,0,-26.4) rot=(1,0,0;3.14159rad)
  Support = -> [Pocket050]
  sketch-geometry (1):
    g0: Circle CenterX=18 CenterY=8 CenterZ=0 NormalX=0 NormalY=0 NormalZ=1 AngleXU=0 Radius=1.9
  constraints (2):
    c: Coincident(g0,g-3)
    c: Radius(g0) = 1.9
FEATURE [PartDesign::Pad] Pad043
  AllowMultiFace = false
  BaseFeature = -> Pocket050
  Length = 1
  Length2 = 100
  Profile = -> Sketch105
  Refine = true
  Type = 0
FEATURE [PartDesign::Mirrored] Mirrored005
  MirrorPlane = -> Sketch105 [V_Axis]
  Refine = true
FEATURE [Sketcher::SketchObject] Sketch104
  ExternalGeometry = -> [Pad043]
  MapMode = 5
  Placement = pos=(0,0,-27.4) rot=(1,0,0;3.14159rad)
  Support = -> [Pad043]
  sketch-geometry (14):
    g0: LineSegment StartX=17.75 StartY=9.25 StartZ=0 EndX=17.75 EndY=8.25 EndZ=0
    g1: LineSegment StartX=17.75 StartY=9.25 StartZ=0 EndX=18.25 EndY=9.25 EndZ=0
    g2: LineSegment StartX=18.25 StartY=9.25 StartZ=0 EndX=18.25 EndY=8.25 EndZ=0
    g3: LineSegment StartX=18.25 StartY=8.25 StartZ=0 EndX=19.25 EndY=8.25 EndZ=0
    g4: LineSegment StartX=19.25 StartY=8.25 StartZ=0 EndX=19.25 EndY=7.75 EndZ=0
    g5: LineSegment StartX=19.25 StartY=7.75 StartZ=0 EndX=18.25 EndY=7.75 EndZ=0
    g6: LineSegment StartX=18.25 StartY=7.75 StartZ=0 EndX=18.25 EndY=6.75 EndZ=0
    g7: LineSegment StartX=18.25 StartY=6.75 StartZ=0 EndX=17.75 EndY=6.75 EndZ=0
    g8: LineSegment StartX=17.75 StartY=6.75 StartZ=0 EndX=17.75 EndY=7.75 EndZ=0
    g9: LineSegment StartX=17.75 StartY=7.75 StartZ=0 EndX=16.75 EndY=7.75 EndZ=0
    g10: LineSegment StartX=16.75 StartY=7.75 StartZ=0 EndX=16.75 EndY=8.25 EndZ=0
    g11: LineSegment StartX=16.75 StartY=8.25 StartZ=0 EndX=17.75 EndY=8.25 EndZ=0
    g12: LineSegment [constr] StartX=17.75 StartY=8.25 StartZ=0 EndX=18 EndY=8 EndZ=0
    g13: LineSegment [constr] StartX=18 StartY=8 StartZ=0 EndX=18.25 EndY=7.75 EndZ=0
  constraints (40):
    c: Vertical(g0)
    c: Coincident(g1,g0)
    c: Horizontal(g1)
    c: Coincident(g2,g1)
    c: Vertical(g2)
    c: Coincident(g3,g2)
    c: Horizontal(g3)
    c: Coincident(g4,g3)
    c: Vertical(g4)
    c: Coincident(g5,g4)
    c: Horizontal(g5)
    c: Coincident(g6,g5)
    c: Vertical(g6)
    c: Coincident(g7,g6)
    c: Horizontal(g7)
    c: Coincident(g8,g7)
    c: Vertical(g8)
    c: Coincident(g9,g8)
    c: Horizontal(g9)
    c: Coincident(g10,g9)
    c: Vertical(g10)
    c: Coincident(g11,g10)
    c: Coincident(g11,g0)
    c: Horizontal(g11)
    c: Equal(g2,g0)
    c: Equal(g3,g5)
    c: Equal(g4,g7)
    c: Equal(g7,g10)
    c: Equal(g10,g1)
    c: Equal(g11,g3)
    c: Equal(g0,g8)
    c: Equal(g0,g11)
    c: Coincident(g12,g0)
    c: Coincident(g12,g-3)
    c: Coincident(g13,g12)
    c: Coincident(g13,g5)
    c: Parallel(g13,g12)
    c: Equal(g12,g13)
    c: Distance(g4) = 0.5
    c: Distance(g2) = 1
FEATURE [PartDesign::Mirrored] Mirrored007
  MirrorPlane = -> Sketch104 [V_Axis]
  Refine = true
FEATURE [PartDesign::Mirrored] Mirrored006
  MirrorPlane = -> Sketch104 [H_Axis]
  Refine = true
FEATURE [PartDesign::Mirrored] Mirrored004
  MirrorPlane = -> Sketch105 [H_Axis]
  Refine = true
FEATURE [PartDesign::MultiTransform] MultiTransform002
  Originals = -> [Pad043]
  Refine = true
  Transformations = -> [Mirrored004,Mirrored005]
FEATURE [PartDesign::Pocket] Pocket051
  AllowMultiFace = false
  BaseFeature = -> MultiTransform002
  Length = 0.5
  Length2 = 100
  Profile = -> Sketch104
  Refine = true
  Type = 0
FEATURE [PartDesign::MultiTransform] MultiTransform003
  Originals = -> [Pocket051]
  Refine = true
  Transformations = -> [Mirrored006,Mirrored007]
FEATURE [PartDesign::Fillet] Fillet027
  Base = -> MultiTransform003 [Edge73,Edge65,Edge242,Edge268]
  BaseFeature = -> MultiTransform003
  Radius = 0.5
  Refine = true
  SupportTransform = false
FEATURE [PartDesign::Fillet] Fillet026
  Base = -> Fillet027 [Edge480]
  BaseFeature = -> Fillet027
  Radius = 0.5
  Refine = true
  SupportTransform = false
FEATURE [Sketcher::SketchObject] Sketch111
  MapMode = 5
  Placement = pos=(0,0,-27.4) rot=(1,0,0;3.14159rad)
  Support = -> [Fillet026]
  sketch-geometry (4):
    g0: LineSegment StartX=-20.1 StartY=10.1 StartZ=0 EndX=20.1 EndY=10.1 EndZ=0
    g1: LineSegment StartX=20.1 StartY=10.1 StartZ=0 EndX=20.1 EndY=-10.1 EndZ=0
    g2: LineSegment StartX=20.1 StartY=-10.1 StartZ=0 EndX=-20.1 EndY=-10.1 EndZ=0
    g3: LineSegment StartX=-20.1 StartY=-10.1 StartZ=0 EndX=-20.1 EndY=10.1 EndZ=0
  constraints (11):
    c: Coincident(g0,g1)
    c: Coincident(g1,g2)
    c: Coincident(g2,g3)
    c: Coincident(g3,g0)
    c: Horizontal(g0)
    c: Horizontal(g2)
    c: Vertical(g1)
    c: Vertical(g3)
    c: Symmetric(g0,g1,g-1)
    c: Distance(g0) = 40.2
    c: Distance(g1) = 20.2
FEATURE [PartDesign::Pocket] Pocket054
  BaseFeature = -> Fillet026
  Length = 0
  Length2 = 100
  Offset = -5.5
  Profile = -> Sketch111
  Refine = true
  Type = 3
  UpToFace = -> Fillet026 [Face50]
FEATURE [Sketcher::SketchObject] Sketch114
  MapMode = 5
  Support = -> [XY_Plane027]
  expr: Constraints[2] = 5 / 2 - 0.1
  sketch-geometry (2):
    g0: Circle CenterX=0 CenterY=0 CenterZ=0 NormalX=0 NormalY=0 NormalZ=1 AngleXU=0 Radius=1.95
    g1: Circle CenterX=0 CenterY=0 CenterZ=0 NormalX=0 NormalY=0 NormalZ=1 AngleXU=0 Radius=2.4
  constraints (4):
    c: Radius(g0) = 1.95
    c: Coincident(g0,g-1)
    c: Radius(g1) = 2.4
    c: Coincident(g1,g0)
FEATURE [Sketcher::SketchObject] Sketch122
  MapMode = 5
  Support = -> [XY_Plane028]
  expr: Constraints[0] = 3.5 / 2
  sketch-geometry (1):
    g0: Circle CenterX=0 CenterY=0 CenterZ=0 NormalX=0 NormalY=0 NormalZ=1 AngleXU=0 Radius=1.75
  constraints (2):
    c: Radius(g0) = 1.75
    c: Coincident(g0,g-1)
FEATURE [PartDesign::Pad] Pad056
  AllowMultiFace = false
  Length = 11
  Length2 = 100
  Profile = -> Sketch122
  Reversed = true
  Type = 0
FEATURE [Sketcher::SketchObject] Sketch121
  MapMode = 5
  Placement = pos=(0,0,-11) rot=(1,0,0;3.14159rad)
  Support = -> [Pad056]
  sketch-geometry (6):
    g0: LineSegment StartX=1 StartY=2 StartZ=0 EndX=4 EndY=2 EndZ=0
    g1: LineSegment StartX=4 StartY=2 StartZ=0 EndX=4 EndY=-2 EndZ=0
    g2: LineSegment StartX=4 StartY=-2 StartZ=0 EndX=1 EndY=-2 EndZ=0
    g3: LineSegment StartX=1 StartY=2 StartZ=0 EndX=1 EndY=0 EndZ=0
    g4: LineSegment StartX=1 StartY=-2 StartZ=0 EndX=1 EndY=0 EndZ=0
    g5: LineSegment [constr] StartX=0 StartY=0 StartZ=0 EndX=1 EndY=0 EndZ=0
  constraints (17):
    c: Coincident(g0,g1)
    c: Coincident(g1,g2)
    c: Horizontal(g0)
    c: Horizontal(g2)
    c: Vertical(g1)
    c: Coincident(g3,g4)
    c: Vertical(g4)
    c: Vertical(g3)
    c: Equal(g3,g4)
    c: Coincident(g5,g3)
    c: Coincident(g-1,g5)
    c: Horizontal(g5)
    c: Coincident(g3,g0)
    c: Coincident(g4,g2)
    c: Distance(g5) = 1
    c: Distance(g0) = 3
    c: Distance(g1) = 4
FEATURE [PartDesign::Pocket] Pocket059
  AllowMultiFace = false
  BaseFeature = -> Pad056
  Length = 5
  Length2 = 100
  Profile = -> Sketch121
  Type = 0
FEATURE [PartDesign::Pad] Pad062
  AllowMultiFace = false
  Length = 4
  Length2 = 100
  Profile = -> Sketch114
  Reversed = true
  Type = 0
  expr: Length = 3 + 1
FEATURE [PartDesign::Mirrored] Mirrored014
  BaseFeature = -> Pocket059
  MirrorPlane = -> YZ_Plane027
  Originals = -> [Pocket059]
FEATURE [Sketcher::SketchObject] Sketch126
  MapMode = 5
  Support = -> [Mirrored014]
  expr: Constraints[1] = 6.2 / 2 + 0.8
  sketch-geometry (1):
    g0: Circle CenterX=0 CenterY=0 CenterZ=0 NormalX=0 NormalY=0 NormalZ=1 AngleXU=0 Radius=3.9
  constraints (2):
    c: Coincident(g0,g-1)
    c: Radius(g0) = 3.9
FEATURE [PartDesign::Pad] Pad055
  AllowMultiFace = false
  BaseFeature = -> Mirrored014
  Length = 3
  Length2 = 100
  Profile = -> Sketch126
  Type = 0
  expr: Length = 0.15 * 20
FEATURE [Sketcher::SketchObject] Sketch120
  MapMode = 5
  Placement = pos=(0,0,3) rot=(0,0,1;0rad)
  Support = -> [Pad055]
  expr: Constraints[1] = 6.2 / 2
  sketch-geometry (1):
    g0: Circle CenterX=0 CenterY=0 CenterZ=0 NormalX=0 NormalY=0 NormalZ=1 AngleXU=0 Radius=3.1
  constraints (2):
    c: Coincident(g0,g-1)
    c: Radius(g0) = 3.1
FEATURE [PartDesign::Pocket] Pocket060
  AllowMultiFace = false
  BaseFeature = -> Pad055
  Length = 2.25
  Length2 = 100
  Profile = -> Sketch120
  Type = 0
  expr: Length = 0.15 * 15
FEATURE [Sketcher::SketchObject] Sketch127
  MapMode = 5
  Placement = pos=(0,0,0) rot=(1,0,0;3.14159rad)
  Support = -> [Pocket060]
  sketch-geometry (2):
    g0: Circle CenterX=0 CenterY=0 CenterZ=0 NormalX=0 NormalY=0 NormalZ=1 AngleXU=0 Radius=1.6
    g1: Circle CenterX=0 CenterY=0 CenterZ=0 NormalX=0 NormalY=0 NormalZ=1 AngleXU=0 Radius=3
  constraints (4):
    c: Coincident(g0,g-1)
    c: Radius(g0) = 1.6
    c: Coincident(g1,g0)
    c: Radius(g1) = 3
FEATURE [PartDesign::Pocket] Pocket055
  AllowMultiFace = false
  BaseFeature = -> Pocket060
  Length = 0
  Length2 = 100
  Profile = -> Sketch127
  Reversed = true
  Type = 3
  UpToFace = -> Pocket060 [Face10]
FEATURE [PartDesign::Body] Body027
  Group = -> [Sketch122,Pad056,Sketch121,Pocket059,Mirrored014,Sketch126,Pad055,Sketch120,Pocket060,Sketch127,Pocket055]
  Origin = -> Origin027
  Tip = -> Pocket060
FEATURE [Sketcher::SketchObject] Sketch128
  ExternalGeometry = -> [Pad062]
  MapMode = 5
  Support = -> [Pad062]
  sketch-geometry (5):
    g0: LineSegment StartX=-5 StartY=5 StartZ=0 EndX=5 EndY=5 EndZ=0
    g1: LineSegment StartX=5 StartY=5 StartZ=0 EndX=5 EndY=-6.1 EndZ=0
    g2: LineSegment StartX=5 StartY=-6.1 StartZ=0 EndX=-5 EndY=-6.1 EndZ=0
    g3: LineSegment StartX=-5 StartY=-6.1 StartZ=0 EndX=-5 EndY=5 EndZ=0
    g4: Circle CenterX=0 CenterY=0 CenterZ=0 NormalX=0 NormalY=0 NormalZ=1 AngleXU=0 Radius=1.95
  constraints (14):
    c: Coincident(g0,g1)
    c: Coincident(g1,g2)
    c: Coincident(g2,g3)
    c: Coincident(g3,g0)
    c: Horizontal(g0)
    c: Horizontal(g2)
    c: Vertical(g1)
    c: Vertical(g3)
    c: DistanceX(g-1,g1) = 5
    c: Distance(g1) = 11.1
    c: Distance(g0) = 10
    c: Coincident(g4,g-1)
    c: Equal(g4,g-3)
    c: DistanceY(g4,g0) = 5
FEATURE [PartDesign::Pad] Pad057
  AllowMultiFace = false
  BaseFeature = -> Pad062
  Length = 1
  Length2 = 100
  Profile = -> Sketch128
  Reversed = true
  Type = 0
FEATURE [Sketcher::SketchObject] Sketch129
  MapMode = 5
  Placement = pos=(0,0,-1) rot=(1,0,0;3.14159rad)
  Support = -> [Pad057]
  sketch-geometry (5):
    g0: LineSegment StartX=-1.15 StartY=5.3 StartZ=0 EndX=-1.15 EndY=6.1 EndZ=0
    g1: LineSegment StartX=-1.15 StartY=6.1 StartZ=0 EndX=1.15 EndY=6.1 EndZ=0
    g2: LineSegment StartX=1.15 StartY=6.1 StartZ=0 EndX=1.15 EndY=5.3 EndZ=0
    g3: LineSegment StartX=1.15 StartY=5.3 StartZ=0 EndX=0 EndY=5.3 EndZ=0
    g4: LineSegment StartX=0 StartY=5.3 StartZ=0 EndX=-1.15 EndY=5.3 EndZ=0
  constraints (14):
    c: Coincident(g0,g1)
    c: Coincident(g1,g2)
    c: Horizontal(g1)
    c: Vertical(g0)
    c: Vertical(g2)
    c: Coincident(g4,g3)
    c: Coincident(g4,g0)
    c: Coincident(g3,g2)
    c: PointOnObject(g3,g-2)
    c: Horizontal(g3)
    c: Horizontal(g4)
    c: Equal(g4,g3)
    c: Distance(g1) = 2.3
    c: Distance(g2) = 0.8
FEATURE [PartDesign::Pad] Pad061
  AllowMultiFace = false
  BaseFeature = -> Pad057
  Length = 1.2
  Length2 = 100
  Profile = -> Sketch129
  Type = 0
  expr: Length = 2.7 - 1.5
FEATURE [PartDesign::Fillet] Fillet030
  Base = -> Pad061 [Edge2]
  BaseFeature = -> Pad061
  Radius = 0.2
  Refine = true
  SupportTransform = false
FEATURE [PartDesign::Chamfer] Chamfer008
  Angle = 45
  Base = -> Fillet030 [Edge31]
  BaseFeature = -> Fillet030
  ChamferType = 0
  FlipDirection = false
  Refine = true
  Size = 0.3
  Size2 = 1
  SupportTransform = false
FEATURE [Sketcher::SketchObject] Sketch124
  ExternalGeometry = -> [Chamfer008]
  MapMode = 5
  Support = -> [Chamfer008]
  expr: Constraints[9] = 6.2 / 2 + 0.8 + 0.2
  sketch-geometry (8):
    g0: LineSegment StartX=-5 StartY=5 StartZ=0 EndX=-5 EndY=-6.1 EndZ=0
    g1: LineSegment StartX=-5 StartY=-6.1 StartZ=0 EndX=5 EndY=-6.1 EndZ=0
    g2: LineSegment StartX=5 StartY=-6.1 StartZ=0 EndX=5 EndY=5 EndZ=0
    g3: ArcOfCircle CenterX=0 CenterY=0 CenterZ=0 NormalX=0 NormalY=0 NormalZ=1 AngleXU=0 Radius=4.1 StartAngle=3.14159 EndAngle=6.28319
    g4: LineSegment StartX=-5 StartY=5 StartZ=0 EndX=-4.1 EndY=5 EndZ=0
    g5: LineSegment StartX=-4.1 StartY=5 StartZ=0 EndX=-4.1 EndY=9e-16 EndZ=0
    g6: LineSegment StartX=5 StartY=5 StartZ=0 EndX=4.1 EndY=5 EndZ=0
    g7: LineSegment StartX=4.1 StartY=0 StartZ=0 EndX=4.1 EndY=5 EndZ=0
  constraints (20):
    c: Coincident(g1,g0)
    c: Coincident(g2,g1)
    c: Coincident(g2,g-3)
    c: Coincident(g1,g-3)
    c: Coincident(g0,g-4)
    c: Coincident(g-4,g0)
    c: Coincident(g3,g-1)
    c: PointOnObject(g3,g-1)
    c: PointOnObject(g3,g-1)
    c: Radius(g3) = 4.1
    c: Coincident(g4,g0)
    c: Coincident(g5,g4)
    c: Coincident(g5,g3)
    c: Coincident(g6,g2)
    c: Coincident(g7,g3)
    c: Coincident(g7,g6)
    c: Horizontal(g6)
    c: Horizontal(g4)
    c: Vertical(g5)
    c: Vertical(g7)
FEATURE [PartDesign::Pad] Pad059
  AllowMultiFace = false
  BaseFeature = -> Chamfer008
  Length = 4
  Length2 = 100
  Profile = -> Sketch124
  Type = 0
FEATURE [Sketcher::SketchObject] Sketch125
  ExternalGeometry = -> [Pad059]
  MapMode = 5
  Placement = pos=(0,0,4) rot=(0,0,1;0rad)
  Support = -> [Pad059]
  sketch-geometry (17):
    g0: LineSegment StartX=-5 StartY=5 StartZ=0 EndX=5 EndY=5 EndZ=0
    g1: LineSegment [constr] StartX=5 StartY=5 StartZ=0 EndX=5 EndY=-6.1 EndZ=0
    g2: LineSegment [constr] StartX=5 StartY=-6.1 StartZ=0 EndX=-5 EndY=-6.1 EndZ=0
    g3: LineSegment [constr] StartX=-5 StartY=-6.1 StartZ=0 EndX=-5 EndY=5 EndZ=0
    g4: LineSegment StartX=-5 StartY=5 StartZ=0 EndX=-5 EndY=0.75 EndZ=0
    g5: LineSegment StartX=5 StartY=5 StartZ=0 EndX=5 EndY=0.75 EndZ=0
    g6: ArcOfCircle CenterX=-5.75 CenterY=0.75 CenterZ=0 NormalX=0 NormalY=0 NormalZ=1 AngleXU=0 Radius=0.75 StartAngle=4.71239 EndAngle=6.28319
    g7: ArcOfCircle CenterX=5.75 CenterY=0.75 CenterZ=0 NormalX=0 NormalY=0 NormalZ=1 AngleXU=0 Radius=0.75 StartAngle=3.14159 EndAngle=4.71239
    g8: ArcOfCircle CenterX=-5.75 CenterY=-0.75 CenterZ=0 NormalX=0 NormalY=0 NormalZ=1 AngleXU=0 Radius=0.75 StartAngle=1.5708 EndAngle=3.14159
    g9: ArcOfCircle CenterX=5.75 CenterY=-0.75 CenterZ=0 NormalX=0 NormalY=0 NormalZ=1 AngleXU=0 Radius=0.75 StartAngle=1e-16 EndAngle=1.5708
    g10: LineSegment [constr] StartX=-5.75 StartY=0.75 StartZ=0 EndX=-5.75 EndY=0 EndZ=0
    g11: LineSegment [constr] StartX=-5.75 StartY=0 StartZ=0 EndX=-5.75 EndY=-0.75 EndZ=0
    g12: LineSegment [constr] StartX=5.75 StartY=0.75 StartZ=0 EndX=5.75 EndY=3e-16 EndZ=0
    g13: LineSegment [constr] StartX=5.75 StartY=-0.75 StartZ=0 EndX=5.75 EndY=3e-16 EndZ=0
    g14: LineSegment StartX=-6.5 StartY=-0.75 StartZ=0 EndX=-6.5 EndY=-6.1 EndZ=0
    g15: LineSegment StartX=6.5 StartY=-0.75 StartZ=0 EndX=6.5 EndY=-6.1 EndZ=0
    g16: LineSegment StartX=-6.5 StartY=-6.1 StartZ=0 EndX=6.5 EndY=-6.1 EndZ=0
  constraints (44):
    c: Coincident(g0,g1)
    c: Coincident(g1,g2)
    c: Coincident(g2,g3)
    c: Coincident(g3,g0)
    c: Horizontal(g0)
    c: Horizontal(g2)
    c: Vertical(g1)
    c: Vertical(g3)
    c: Coincident(g2,g-3)
    c: Coincident(g0,g-4)
    c: Coincident(g4,g0)
    c: Vertical(g4)
    c: Coincident(g5,g0)
    c: Vertical(g5)
    c: Tangent(g6,g4) = 1.5708
    c: Tangent(g7,g5) = -1.5708
    c: Coincident(g8,g6)
    c: Coincident(g10,g6)
    c: Coincident(g11,g8)
    c: Coincident(g11,g6)
    c: Vertical(g11)
    c: Vertical(g10)
    c: Equal(g10,g11)
    c: Coincident(g10,g6)
    c: Coincident(g12,g7)
    c: Coincident(g12,g7)
    c: Vertical(g12)
    c: Coincident(g13,g9)
    c: Coincident(g13,g7)
    c: Vertical(g13)
    c: Coincident(g9,g7)
    c: Equal(g12,g13)
    c: Equal(g5,g4)
    c: Equal(g12,g10)
    c: Vertical(g14)
    c: Vertical(g15)
    c: Horizontal(g16)
    c: Coincident(g16,g14)
    c: Coincident(g15,g16)
    c: PointOnObject(g1,g16)
    c: Tangent(g14,g8) = -1.5708
    c: Tangent(g9,g15) = 1.5708
    c: DistanceX(g1,g15) = 1.5
    c: PointOnObject(g6,g-1)
FEATURE [PartDesign::Pad] Pad058
  AllowMultiFace = false
  BaseFeature = -> Pad059
  Length = 2.55
  Length2 = 100
  Profile = -> Sketch125
  Type = 0
FEATURE [Sketcher::SketchObject] Sketch123
  ExternalGeometry = -> [Pad058]
  MapMode = 5
  Support = -> [Pad058]
  expr: Constraints[3] = 3.5 / 2 + 0.1
  sketch-geometry (4):
    g0: ArcOfCircle CenterX=0 CenterY=0 CenterZ=0 NormalX=0 NormalY=0 NormalZ=1 AngleXU=0 Radius=1.85 StartAngle=3.14159 EndAngle=6.28319
    g1: LineSegment StartX=1.85 StartY=-5e-16 StartZ=0 EndX=1.85 EndY=5 EndZ=0
    g2: LineSegment StartX=-1.85 StartY=2e-16 StartZ=0 EndX=-1.85 EndY=5 EndZ=0
    g3: LineSegment StartX=1.85 StartY=5 StartZ=0 EndX=-1.85 EndY=5 EndZ=0
  constraints (12):
    c: Coincident(g0,g-1)
    c: PointOnObject(g0,g-1)
    c: PointOnObject(g0,g-1)
    c: Radius(g0) = 1.85
    c: Coincident(g1,g0)
    c: PointOnObject(g1,g-3)
    c: Vertical(g1)
    c: Coincident(g2,g0)
    c: PointOnObject(g2,g-3)
    c: Vertical(g2)
    c: Coincident(g3,g1)
    c: Coincident(g2,g3)
FEATURE [PartDesign::Pocket] Pocket061
  AllowMultiFace = false
  BaseFeature = -> Pad058
  Length = 5
  Length2 = 100
  Profile = -> Sketch123
  Type = 1
FEATURE [Sketcher::SketchObject] Sketch118
  MapMode = 5
  Placement = pos=(0,0,6.55) rot=(0,0,1;0rad)
  Support = -> [Pocket061]
  expr: Constraints[17] = 11.1 + 0.2
  expr: Constraints[16] = 8.199999999999999 + 0.2
  sketch-geometry (6):
    g0: LineSegment StartX=5.65 StartY=-4.2 StartZ=0 EndX=-5.65 EndY=-4.2 EndZ=0
    g1: LineSegment StartX=-5.65 StartY=-4.2 StartZ=0 EndX=-5.65 EndY=4.2 EndZ=0
    g2: LineSegment StartX=5.65 StartY=4.2 StartZ=0 EndX=5.65 EndY=0 EndZ=0
    g3: LineSegment StartX=5.65 StartY=0 StartZ=0 EndX=5.65 EndY=-4.2 EndZ=0
    g4: LineSegment StartX=-5.65 StartY=4.2 StartZ=0 EndX=0 EndY=4.2 EndZ=0
    g5: LineSegment StartX=0 StartY=4.2 StartZ=0 EndX=5.65 EndY=4.2 EndZ=0
  constraints (18):
    c: Coincident(g0,g1)
    c: Horizontal(g0)
    c: Vertical(g1)
    c: PointOnObject(g2,g-1)
    c: Vertical(g2)
    c: Coincident(g3,g2)
    c: Coincident(g3,g0)
    c: Vertical(g3)
    c: Equal(g3,g2)
    c: PointOnObject(g4,g-2)
    c: Horizontal(g4)
    c: Coincident(g5,g4)
    c: Coincident(g5,g2)
    c: Horizontal(g5)
    c: Equal(g4,g5)
    c: Coincident(g1,g4)
    c: Distance(g1) = 8.4
    c: Distance(g0) = 11.3
FEATURE [PartDesign::Pocket] Pocket058
  AllowMultiFace = false
  BaseFeature = -> Pocket061
  Length = 2
  Length2 = 100
  Profile = -> Sketch118
  Type = 0
  expr: Length = 1.2 + 0.8
FEATURE [Sketcher::SketchObject] Sketch113
  ExternalGeometry = -> [Pocket058]
  MapMode = 5
  Support = -> [Pocket058]
  sketch-geometry (1):
    g0: Circle CenterX=0 CenterY=0 CenterZ=0 NormalX=0 NormalY=0 NormalZ=1 AngleXU=0 Radius=4.1
  constraints (2):
    c: Coincident(g0,g-1)
    c: Equal(g0,g-3)
FEATURE [PartDesign::Pocket] Pocket056
  AllowMultiFace = false
  BaseFeature = -> Pocket058
  Length = 5
  Length2 = 100
  Profile = -> Sketch113
  Type = 1
FEATURE [Sketcher::SketchObject] Sketch112
  ExternalGeometry = -> [Pocket056]
  MapMode = 5
  Placement = pos=(0,0,-1) rot=(1,0,0;3.14159rad)
  Support = -> [Pocket056]
  sketch-geometry (4):
    g0: ArcOfCircle CenterX=0 CenterY=0 CenterZ=0 NormalX=0 NormalY=0 NormalZ=1 AngleXU=0 Radius=4.1 StartAngle=3.14159 EndAngle=6.28319
    g1: LineSegment StartX=4.1 StartY=2.6e-15 StartZ=0 EndX=4.1 EndY=-5 EndZ=0
    g2: LineSegment StartX=4.1 StartY=-5 StartZ=0 EndX=-4.1 EndY=-5 EndZ=0
    g3: LineSegment StartX=-4.1 StartY=-5 StartZ=0 EndX=-4.1 EndY=9e-16 EndZ=0
  constraints (11):
    c: Coincident(g0,g-1)
    c: Coincident(g0,g-3)
    c: PointOnObject(g0,g-1)
    c: Coincident(g1,g2)
    c: Coincident(g2,g3)
    c: Horizontal(g2)
    c: Vertical(g1)
    c: Vertical(g3)
    c: PointOnObject(g-4,g2)
    c: Coincident(g1,g0)
    c: Coincident(g3,g0)
FEATURE [PartDesign::Pad] Pad054
  AllowMultiFace = false
  BaseFeature = -> Pocket056
  Length = 10
  Length2 = 100
  Profile = -> Sketch112
  Reversed = true
  Type = 3
  UpToFace = -> Pocket056 [Face19]
FEATURE [Sketcher::SketchObject] Sketch116
  MapMode = 5
  Placement = pos=(0,0,-1) rot=(1,0,0;3.14159rad)
  Support = -> [Pad054]
  expr: Constraints[1] = 2.2 / 2
  expr: Constraints[2] = 5 + 2.2 / 2 - 0.1
  sketch-geometry (1):
    g0: Circle CenterX=0 CenterY=6 CenterZ=0 NormalX=0 NormalY=0 NormalZ=1 AngleXU=0 Radius=1.1
  constraints (3):
    c: PointOnObject(g0,g-2)
    c: Radius(g0) = 1.1
    c: Distance(g-1,g0) = 6
FEATURE [PartDesign::Pad] Pad060
  AllowMultiFace = false
  BaseFeature = -> Pad054
  Length = 1.2
  Length2 = 100
  Profile = -> Sketch116
  Type = 0
FEATURE [Sketcher::SketchObject] Sketch119
  ExternalGeometry = -> [Pad060]
  MapMode = 5
  Placement = pos=(0,0,-1) rot=(1,0,0;3.14159rad)
  Support = -> [Pad060]
  sketch-geometry (2):
    g0: Circle CenterX=0 CenterY=6 CenterZ=0 NormalX=0 NormalY=0 NormalZ=1 AngleXU=0 Radius=1.1
    g1: Circle CenterX=0 CenterY=6 CenterZ=0 NormalX=0 NormalY=0 NormalZ=1 AngleXU=0 Radius=2
  constraints (4):
    c: Coincident(g0,g-3)
    c: Equal(g-3,g0)
    c: Coincident(g1,g0)
    c: Radius(g1) = 2
FEATURE [PartDesign::Pocket] Pocket057
  AllowMultiFace = false
  BaseFeature = -> Pad060
  Length = 5
  Length2 = 100
  Profile = -> Sketch119
  Reversed = true
  Type = 1
FEATURE [Sketcher::SketchObject] Sketch117
  ExternalGeometry = -> [Pocket057]
  MapMode = 5
  Placement = pos=(0,0,-1) rot=(1,0,0;3.14159rad)
  Support = -> [Pocket057]
  expr: Constraints[14] = 11 / 2 + 2
  sketch-geometry (5):
    g0: LineSegment StartX=5 StartY=2 StartZ=0 EndX=7.5 EndY=2 EndZ=0
    g1: LineSegment StartX=7.5 StartY=2 StartZ=0 EndX=7.5 EndY=-2 EndZ=0
    g2: LineSegment StartX=7.5 StartY=-2 StartZ=0 EndX=5 EndY=-2 EndZ=0
    g3: LineSegment StartX=5 StartY=2 StartZ=0 EndX=5 EndY=0 EndZ=0
    g4: LineSegment StartX=5 StartY=0 StartZ=0 EndX=5 EndY=-2 EndZ=0
  constraints (15):
    c: Coincident(g2,g4)
    c: Coincident(g3,g4)
    c: Coincident(g0,g3)
    c: Coincident(g1,g2)
    c: Coincident(g0,g1)
    c: Horizontal(g0)
    c: Horizontal(g2)
    c: Vertical(g1)
    c: Vertical(g3)
    c: Vertical(g4)
    c: Equal(g3,g4)
    c: PointOnObject(g3,g-1)
    c: PointOnObject(g3,g-3)
    c: Distance(g1) = 4
    c: DistanceX(g-1,g0) = 7.5
FEATURE [PartDesign::Pad] Pad050
  AllowMultiFace = false
  BaseFeature = -> Pocket057
  Length = 2
  Length2 = 100
  Profile = -> Sketch117
  Reversed = true
  Type = 0
FEATURE [Sketcher::SketchObject] Sketch115
  MapMode = 5
  Placement = pos=(0,0,-1) rot=(1,0,0;3.14159rad)
  Support = -> [Pad050]
  expr: Constraints[1] = 10.95 / 2 + 2 / 2
  expr: Constraints[2] = 2 / 2
  sketch-geometry (1):
    g0: Circle CenterX=6.475 CenterY=0 CenterZ=0 NormalX=0 NormalY=0 NormalZ=1 AngleXU=0 Radius=1
  constraints (3):
    c: PointOnObject(g0,g-1)
    c: Distance(g-1,g0) = 6.475
    c: Radius(g0) = 1
FEATURE [PartDesign::Pad] Pad051
  AllowMultiFace = false
  BaseFeature = -> Pad050
  Length = 1.2
  Length2 = 100
  Profile = -> Sketch115
  Type = 0
FEATURE [PartDesign::Mirrored] Mirrored015
  BaseFeature = -> Pad051
  MirrorPlane = -> YZ_Plane026
  Originals = -> [Pad050]
FEATURE [Sketcher::SketchObject] Sketch130
  MapMode = 5
  Support = -> [XY_Plane026]
  sketch-geometry (1):
    g0: Circle CenterX=0 CenterY=0 CenterZ=0 NormalX=0 NormalY=0 NormalZ=1 AngleXU=0 Radius=3
  constraints (2):
    c: Radius(g0) = 3
    c: Coincident(g0,g-1)
FEATURE [PartDesign::Pad] Pad053
  AllowMultiFace = false
  Length = 2.5
  Length2 = 100
  Profile = -> Sketch130
  Type = 0
FEATURE [PartDesign::Mirrored] Mirrored016
  BaseFeature = -> Mirrored015
  MirrorPlane = -> YZ_Plane026
  Originals = -> [Pad051]
FEATURE [Sketcher::SketchObject] Sketch019
  ExternalGeometry = -> [Mirrored016]
  MapMode = 5
  Placement = pos=(0,5,0) rot=(0,0.707107,0.707107;3.14159rad)
  Support = -> [Mirrored016]
  sketch-geometry (5):
    g0: LineSegment StartX=3 StartY=0 StartZ=0 EndX=3 EndY=-1 EndZ=0
    g1: LineSegment StartX=3 StartY=-1 StartZ=0 EndX=-3 EndY=-1 EndZ=0
    g2: LineSegment StartX=-3 StartY=-1 StartZ=0 EndX=-3 EndY=0 EndZ=0
    g3: LineSegment StartX=0 StartY=0 StartZ=0 EndX=-3 EndY=0 EndZ=0
    g4: LineSegment StartX=0 StartY=0 StartZ=0 EndX=3 EndY=0 EndZ=0
  constraints (14):
    c: Coincident(g0,g1)
    c: Coincident(g1,g2)
    c: Horizontal(g1)
    c: Vertical(g0)
    c: Vertical(g2)
    c: PointOnObject(g2,g-1)
    c: Coincident(g3,g-1)
    c: Coincident(g3,g2)
    c: Coincident(g4,g3)
    c: Coincident(g4,g0)
    c: Equal(g4,g3)
    c: Horizontal(g4)
    c: PointOnObject(g0,g-3)
    c: Distance(g1) = 6
FEATURE [PartDesign::Pad] Pad052
  AllowMultiFace = false
  BaseFeature = -> Mirrored016
  Length = 5
  Length2 = 100
  Profile = -> Sketch019
  Type = 0
FEATURE [PartDesign::Pad] Pad049
  AllowMultiFace = false
  BaseFeature = -> Pad052
  Length = 2
  Length2 = 100
  Profile = -> Sketch116
  Reversed = true
  Type = 3
  UpToFace = -> Pad052 [Face64]
FEATURE [PartDesign::Body] Body028
  Group = -> [Sketch130,Pad053]
  Origin = -> Origin028
  Placement = pos=(0,0,0.8) rot=(0,0,1;0rad)
  Tip = -> Pad053
FEATURE [PartDesign::FeatureBase] Clone012
  BaseFeature = -> Body027
FEATURE [PartDesign::Body] Body029
  BaseFeature = -> Body027
  Group = -> [Clone012]
  Origin = -> Origin030
  Tip = -> Clone012
FEATURE [PartDesign::FeatureBase] Clone014
  BaseFeature = -> Body028
  Placement = pos=(0,0,0.8) rot=(0,0,1;0rad)
FEATURE [PartDesign::Body] Body031
  BaseFeature = -> Body028
  Group = -> [Clone014]
  Origin = -> Origin032
  Tip = -> Clone014
FEATURE [PartDesign::FeatureBase] Clone016
  BaseFeature = -> Body028
  Placement = pos=(0,0,0.8) rot=(0,0,1;0rad)
FEATURE [PartDesign::Body] Body032
  Group = -> [Clone016]
  Origin = -> Origin034
  Tip = -> Clone016
FEATURE [PartDesign::FeatureBase] Clone017
  BaseFeature = -> Body027
FEATURE [PartDesign::Body] Body034
  BaseFeature = -> Body027
  Group = -> [Clone017]
  Origin = -> Origin037
  Tip = -> Clone017
FEATURE [PartDesign::FeatureBase] Clone019
  BaseFeature = -> Body028
  Placement = pos=(0,0,0.8) rot=(0,0,1;0rad)
FEATURE [PartDesign::Body] Body035
  Group = -> [Clone019]
  Origin = -> Origin038
  Tip = -> Clone019
FEATURE [PartDesign::FeatureBase] Clone020
  BaseFeature = -> Body027
FEATURE [PartDesign::Body] Body037
  BaseFeature = -> Body027
  Group = -> [Clone020]
  Origin = -> Origin041
  Tip = -> Clone020
FEATURE [Sketcher::SketchObject] Sketch131
  MapMode = 5
  Support = -> [XY_Plane042]
  expr: Constraints[3] = 1 + 0.4 * 2
  expr: Constraints[2] = 2 / 2
  sketch-geometry (2):
    g0: Circle CenterX=0 CenterY=0 CenterZ=0 NormalX=0 NormalY=0 NormalZ=1 AngleXU=0 Radius=1
    g1: Circle CenterX=0 CenterY=0 CenterZ=0 NormalX=0 NormalY=0 NormalZ=1 AngleXU=0 Radius=1.8
  constraints (4):
    c: Coincident(g0,g-1)
    c: Coincident(g1,g0)
    c: Radius(g0) = 1
    c: Radius(g1) = 1.8
FEATURE [PartDesign::Pad] Pad063
  AllowMultiFace = false
  Length = 18
  Length2 = 100
  Profile = -> Sketch131
  Type = 0
FEATURE [Sketcher::SketchObject] Sketch132
  ExternalGeometry = -> [Pad063]
  MapMode = 5
  Placement = pos=(0,0,18) rot=(0,0,1;0rad)
  Support = -> [Pad063]
  expr: Constraints[15] = 20 - 2.4 * 2 - 2 - 0.2
  expr: Constraints[12] = 21 + 1.6 - (2 - 1.6) - 0.2
  sketch-geometry (6):
    g0: LineSegment StartX=-10.8 StartY=1.8 StartZ=0 EndX=11.2 EndY=1.8 EndZ=0
    g1: LineSegment StartX=11.2 StartY=1.8 StartZ=0 EndX=11.2 EndY=-1.8 EndZ=0
    g2: LineSegment StartX=11.2 StartY=-1.8 StartZ=0 EndX=-10.8 EndY=-1.8 EndZ=0
    g3: LineSegment StartX=-10.8 StartY=-1.8 StartZ=0 EndX=-10.8 EndY=1.8 EndZ=0
    g4: Circle CenterX=0 CenterY=0 CenterZ=0 NormalX=0 NormalY=0 NormalZ=1 AngleXU=0 Radius=1
    g5: GeomPoint X=-1.8 Y=0 Z=0
  constraints (16):
    c: Coincident(g0,g1)
    c: Coincident(g1,g2)
    c: Coincident(g2,g3)
    c: Coincident(g3,g0)
    c: Horizontal(g0)
    c: Horizontal(g2)
    c: Vertical(g1)
    c: Vertical(g3)
    c: Tangent(g0,g-3)
    c: Tangent(g-3,g2)
    c: Coincident(g4,g-1)
    c: Equal(g-4,g4)
    c: Distance(g0) = 22
    c: PointOnObject(g5,g-3)
    c: PointOnObject(g5,g-1)
    c: DistanceX(g5,g0) = 13
FEATURE [PartDesign::Pad] Pad064
  AllowMultiFace = false
  BaseFeature = -> Pad063
  Length = 2
  Length2 = 100
  Profile = -> Sketch132
  Type = 0
FEATURE [Sketcher::SketchObject] Sketch133
  MapMode = 5
  Support = -> [XY_Plane043]
  expr: Constraints[3] = 1 + 0.4 * 2
  expr: Constraints[2] = 2 / 2
  sketch-geometry (2):
    g0: Circle CenterX=0 CenterY=0 CenterZ=0 NormalX=0 NormalY=0 NormalZ=1 AngleXU=0 Radius=1
    g1: Circle CenterX=0 CenterY=0 CenterZ=0 NormalX=0 NormalY=0 NormalZ=1 AngleXU=0 Radius=1.8
  constraints (4):
    c: Coincident(g0,g-1)
    c: Coincident(g1,g0)
    c: Radius(g0) = 1
    c: Radius(g1) = 1.8
FEATURE [PartDesign::Pad] Pad065
  AllowMultiFace = false
  Length = 18
  Length2 = 100
  Profile = -> Sketch133
  Type = 0
FEATURE [Sketcher::SketchObject] Sketch134
  ExternalGeometry = -> [Pad065]
  MapMode = 5
  Placement = pos=(0,0,18) rot=(0,0,1;0rad)
  Support = -> [Pad065]
  sketch-geometry (6):
    g0: LineSegment StartX=-3.8 StartY=1.8 StartZ=0 EndX=4e-16 EndY=1.8 EndZ=0
    g1: LineSegment StartX=-3e-16 StartY=-1.8 StartZ=0 EndX=-3.8 EndY=-1.8 EndZ=0
    g2: LineSegment StartX=-3.8 StartY=-1.8 StartZ=0 EndX=-3.8 EndY=1.8 EndZ=0
    g3: ArcOfCircle CenterX=0 CenterY=0 CenterZ=0 NormalX=0 NormalY=0 NormalZ=1 AngleXU=0 Radius=1.8 StartAngle=4.71239 EndAngle=7.85398
    g4: Circle CenterX=0 CenterY=0 CenterZ=0 NormalX=0 NormalY=0 NormalZ=1 AngleXU=0 Radius=1
    g5: GeomPoint X=-1.8 Y=0 Z=0
  constraints (16):
    c: Coincident(g1,g2)
    c: Coincident(g2,g0)
    c: Horizontal(g0)
    c: Horizontal(g1)
    c: Vertical(g2)
    c: Coincident(g3,g-1)
    c: PointOnObject(g3,g-4)
    c: PointOnObject(g3,g-2)
    c: PointOnObject(g3,g-2)
    c: Coincident(g0,g3)
    c: Coincident(g1,g3)
    c: Coincident(g4,g3)
    c: Equal(g-3,g4)
    c: PointOnObject(g5,g-4)
    c: PointOnObject(g5,g-1)
    c: DistanceX(g0,g5) = 2
FEATURE [PartDesign::Pad] Pad066
  AllowMultiFace = false
  BaseFeature = -> Pad065
  Length = 4
  Length2 = 100
  Profile = -> Sketch134
  Type = 0
FEATURE [Sketcher::SketchObject] Sketch135
  ExternalGeometry = -> [Pad064]
  MapMode = 5
  Placement = pos=(0,-3,0) rot=(1,0,0;1.5708rad)
  sketch-geometry (3):
    g0: LineSegment StartX=11.2 StartY=20 StartZ=0 EndX=11.2 EndY=18 EndZ=0
    g1: LineSegment StartX=11.2 StartY=20 StartZ=0 EndX=8.2 EndY=18 EndZ=0
    g2: LineSegment StartX=11.2 StartY=18 StartZ=0 EndX=8.2 EndY=18 EndZ=0
  constraints (7):
    c: Coincident(g1,g0)
    c: Coincident(g2,g0)
    c: Coincident(g2,g1)
    c: Horizontal(g2)
    c: Distance(g2) = 3
    c: Coincident(g0,g-3)
    c: Coincident(g0,g-3)
FEATURE [Sketcher::SketchObject] Sketch137
  ExternalGeometry = -> [Pad066]
  MapMode = 5
  Placement = pos=(0,-1.8,0) rot=(1,0,0;1.5708rad)
  Support = -> [Pad066]
  sketch-geometry (3):
    g0: LineSegment StartX=-3.8 StartY=20 StartZ=0 EndX=-3.8 EndY=18 EndZ=0
    g1: LineSegment StartX=-3.8 StartY=20 StartZ=0 EndX=-6.8 EndY=18 EndZ=0
    g2: LineSegment StartX=-3.8 StartY=18 StartZ=0 EndX=-6.8 EndY=18 EndZ=0
  constraints (8):
    c: Coincident(g2,g1)
    c: Coincident(g2,g0)
    c: Horizontal(g2)
    c: Distance(g2) = 3
    c: Coincident(g-3,g0)
    c: Coincident(g1,g0)
    c: PointOnObject(g0,g-3)
    c: Distance(g0) = 2
FEATURE [PartDesign::Pocket] Pocket062
  AllowMultiFace = false
  BaseFeature = -> Pad064
  Length = 5
  Length2 = 100
  Profile = -> Sketch135
  Type = 1
FEATURE [Sketcher::SketchObject] Sketch136
  ExternalGeometry = -> [Pocket062]
  MapMode = 5
  Placement = pos=(0,0,20) rot=(0,0,1;0rad)
  Support = -> [Pocket062]
  sketch-geometry (5):
    g0: LineSegment StartX=11.19 StartY=-2e-16 StartZ=0 EndX=8.2 EndY=-1.8 EndZ=0
    g1: LineSegment StartX=8.2 StartY=1.8 StartZ=0 EndX=11.19 EndY=-2e-16 EndZ=0
    g2: LineSegment StartX=8.2 StartY=-1.8 StartZ=0 EndX=11.2 EndY=-1.8 EndZ=0
    g3: LineSegment StartX=8.2 StartY=1.8 StartZ=0 EndX=11.2 EndY=1.8 EndZ=0
    g4: LineSegment StartX=11.2 StartY=-1.8 StartZ=0 EndX=11.2 EndY=1.8 EndZ=0
  constraints (13):
    c: Coincident(g1,g0)
    c: Coincident(g2,g0)
    c: Horizontal(g2)
    c: Horizontal(g3)
    c: Distance(g2) = 3
    c: Equal(g2,g3)
    c: Coincident(g1,g3)
    c: Coincident(g2,g4)
    c: Coincident(g4,g3)
    c: PointOnObject(g0,g-1)
    c: DistanceX(g0,g3) = 0.01
    c: Coincident(g3,g-3)
    c: Coincident(g2,g-3)
FEATURE [PartDesign::Pocket] Pocket063
  AllowMultiFace = false
  BaseFeature = -> Pocket062
  Length = 5
  Length2 = 100
  Profile = -> Sketch136
  Type = 1
FEATURE [PartDesign::Pad] Pad067
  AllowMultiFace = false
  BaseFeature = -> Pad066
  Length = 10
  Length2 = 100
  Profile = -> Sketch137
  Reversed = true
  Type = 3
  UpToFace = -> Pad066 [Face7]
FEATURE [Sketcher::SketchObject] Sketch138
  ExternalGeometry = -> [Pad066]
  MapMode = 5
  Placement = pos=(0,0,22) rot=(0,0,1;0rad)
  Support = -> [Pad067]
  sketch-geometry (5):
    g0: LineSegment StartX=-3.8 StartY=1.8 StartZ=0 EndX=-6.8 EndY=1.8 EndZ=0
    g1: LineSegment StartX=-3.8 StartY=-1.8 StartZ=0 EndX=-3.8 EndY=1.8 EndZ=0
    g2: LineSegment StartX=-6.8 StartY=1.8 StartZ=0 EndX=-3.81 EndY=0 EndZ=0
    g3: LineSegment StartX=-3.81 StartY=0 StartZ=0 EndX=-6.8 EndY=-1.8 EndZ=0
    g4: LineSegment StartX=-6.8 StartY=-1.8 StartZ=0 EndX=-3.8 EndY=-1.8 EndZ=0
  constraints (13):
    c: Horizontal(g4)
    c: Horizontal(g0)
    c: Equal(g0,g4)
    c: Distance(g0) = 3
    c: Coincident(g1,g-3)
    c: Coincident(g1,g-3)
    c: Coincident(g2,g3)
    c: PointOnObject(g2,g-1)
    c: Coincident(g2,g0)
    c: Coincident(g0,g1)
    c: Coincident(g3,g4)
    c: Coincident(g1,g4)
    c: DistanceX(g2,g1) = 0.01
FEATURE [PartDesign::Pad] Pad068
  AllowMultiFace = false
  BaseFeature = -> Pad067
  Length = 10
  Length2 = 100
  Profile = -> Sketch138
  Reversed = true
  Type = 3
  UpToFace = -> Pad067 [Face4]
FEATURE [Sketcher::SketchObject] Sketch032
  ExternalGeometry = -> [Pocket063]
  MapMode = 5
  Placement = pos=(0,0,20) rot=(0,0,1;0rad)
  sketch-geometry (9):
    g0: LineSegment StartX=-10.8 StartY=1.8 StartZ=0 EndX=-10.8 EndY=-1.8 EndZ=0
    g1: LineSegment StartX=8.2 StartY=1.8 StartZ=0 EndX=11.19 EndY=-7e-16 EndZ=0
    g2: LineSegment StartX=11.19 StartY=-7e-16 StartZ=0 EndX=8.2 EndY=-1.8 EndZ=0
    g3: ArcOfCircle CenterX=0 CenterY=0 CenterZ=0 NormalX=0 NormalY=0 NormalZ=1 AngleXU=0 Radius=1.86815 StartAngle=1.84174 EndAngle=4.44144
    g4: ArcOfCircle CenterX=0 CenterY=0 CenterZ=0 NormalX=0 NormalY=0 NormalZ=1 AngleXU=0 Radius=1.86815 StartAngle=4.98334 EndAngle=7.58303
    g5: LineSegment StartX=-10.8 StartY=-1.8 StartZ=0 EndX=-0.5 EndY=-1.8 EndZ=0
    g6: LineSegment StartX=0.5 StartY=-1.8 StartZ=0 EndX=8.2 EndY=-1.8 EndZ=0
    g7: LineSegment StartX=8.2 StartY=1.8 StartZ=0 EndX=0.5 EndY=1.8 EndZ=0
    g8: LineSegment StartX=-0.5 StartY=1.8 StartZ=0 EndX=-10.8 EndY=1.8 EndZ=0
  constraints (22):
    c: Coincident(g2,g1)
    c: Coincident(g0,g-3)
    c: Coincident(g0,g-5)
    c: Coincident(g2,g-5)
    c: Coincident(g-4,g1)
    c: Coincident(g1,g-4)
    c: Coincident(g3,g-1)
    c: Coincident(g4,g3)
    c: Equal(g4,g3)
    c: Coincident(g5,g0)
    c: Coincident(g5,g3)
    c: Coincident(g6,g4)
    c: Coincident(g6,g2)
    c: Coincident(g7,g1)
    c: Coincident(g7,g4)
    c: Coincident(g8,g3)
    c: Coincident(g8,g0)
    c: Horizontal(g7)
    c: Horizontal(g8)
    c: Horizontal(g5)
    c: Horizontal(g6)
    c: DistanceX(g3,g4) = 1
FEATURE [PartDesign::Pad] Pad069
  AllowMultiFace = false
  BaseFeature = -> Pocket063
  Length = 2
  Length2 = 100
  Profile = -> Sketch032
  Type = 0
FEATURE [Sketcher::SketchObject] Sketch139
  ExternalGeometry = -> [Pad069]
  MapMode = 5
  Placement = pos=(0,0,22) rot=(0,0,1;0rad)
  Support = -> [Pad069]
  sketch-geometry (4):
    g0: LineSegment StartX=-10.8 StartY=1.8 StartZ=0 EndX=-9.2 EndY=1.8 EndZ=0
    g1: LineSegment StartX=-9.2 StartY=1.8 StartZ=0 EndX=-9.2 EndY=-1.8 EndZ=0
    g2: LineSegment StartX=-9.2 StartY=-1.8 StartZ=0 EndX=-10.8 EndY=-1.8 EndZ=0
    g3: LineSegment StartX=-10.8 StartY=-1.8 StartZ=0 EndX=-10.8 EndY=1.8 EndZ=0
  constraints (10):
    c: Coincident(g0,g1)
    c: Coincident(g1,g2)
    c: Coincident(g2,g3)
    c: Coincident(g3,g0)
    c: Horizontal(g0)
    c: Horizontal(g2)
    c: Vertical(g1)
    c: Coincident(g0,g-3)
    c: Coincident(g2,g-3)
    c: Distance(g0) = 1.6
FEATURE [PartDesign::Pad] Pad070
  AllowMultiFace = false
  BaseFeature = -> Pad069
  Length = 11
  Length2 = 100
  Profile = -> Sketch139
  Type = 0
  expr: Length = 9 + 2
FEATURE [Sketcher::SketchObject] Sketch140
  ExternalGeometry = -> [Pad070]
  MapMode = 5
  Placement = pos=(0,0,22) rot=(0,0,1;0rad)
  Support = -> [Pad070]
  sketch-geometry (9):
    g0: LineSegment StartX=-9.2 StartY=-1.8 StartZ=0 EndX=-0.5 EndY=-1.8 EndZ=0
    g1: LineSegment StartX=-1.85742 StartY=-0.2 StartZ=0 EndX=-9.2 EndY=-0.2 EndZ=0
    g2: LineSegment StartX=-9.2 StartY=-0.2 StartZ=0 EndX=-9.2 EndY=-1.8 EndZ=0
    g3: ArcOfCircle CenterX=0 CenterY=0 CenterZ=0 NormalX=0 NormalY=0 NormalZ=1 AngleXU=0 Radius=1.86815 StartAngle=3.24886 EndAngle=4.44144
    g4: ArcOfCircle CenterX=0 CenterY=0 CenterZ=0 NormalX=0 NormalY=0 NormalZ=1 AngleXU=0 Radius=1.86815 StartAngle=4.98334 EndAngle=6.17592
    g5: LineSegment StartX=1.85742 StartY=-0.2 StartZ=0 EndX=10.8578 EndY=-0.2 EndZ=0
    g6: LineSegment StartX=0.5 StartY=-1.8 StartZ=0 EndX=8.2 EndY=-1.8 EndZ=0
    g7: LineSegment StartX=8.2 StartY=-1.8 StartZ=0 EndX=10.8578 EndY=-0.2 EndZ=0
    g8: LineSegment [constr] StartX=1.85742 StartY=-0.2 StartZ=0 EndX=-1.85742 EndY=-0.2 EndZ=0
  constraints (22):
    c: Coincident(g1,g2)
    c: Coincident(g2,g0)
    c: Horizontal(g1)
    c: Vertical(g2)
    c: Coincident(g0,g-3)
    c: Coincident(g0,g-4)
    c: Coincident(g3,g-1)
    c: Coincident(g3,g1)
    c: Coincident(g3,g0)
    c: Distance(g2) = 1.6
    c: Coincident(g4,g3)
    c: Coincident(g4,g-5)
    c: Coincident(g5,g4)
    c: PointOnObject(g5,g-6)
    c: Horizontal(g5)
    c: Coincident(g6,g4)
    c: Coincident(g6,g-6)
    c: Coincident(g7,g6)
    c: Coincident(g7,g5)
    c: Coincident(g8,g4)
    c: Coincident(g8,g1)
    c: Horizontal(g8)
FEATURE [PartDesign::Pad] Pad071
  AllowMultiFace = false
  BaseFeature = -> Pad070
  Length = 2
  Length2 = 100
  Profile = -> Sketch140
  Type = 0
FEATURE [Sketcher::SketchObject] Sketch141
  ExternalGeometry = -> [Pad071]
  MapMode = 5
  Placement = pos=(0,0,33) rot=(0,0,1;0rad)
  Support = -> [Pad071]
  sketch-geometry (4):
    g0: LineSegment StartX=-10.8 StartY=1.8 StartZ=0 EndX=-5.2 EndY=1.8 EndZ=0
    g1: LineSegment StartX=-5.2 StartY=1.8 StartZ=0 EndX=-5.2 EndY=-1.8 EndZ=0
    g2: LineSegment StartX=-5.2 StartY=-1.8 StartZ=0 EndX=-10.8 EndY=-1.8 EndZ=0
    g3: LineSegment StartX=-10.8 StartY=-1.8 StartZ=0 EndX=-10.8 EndY=1.8 EndZ=0
  constraints (10):
    c: Coincident(g0,g1)
    c: Coincident(g1,g2)
    c: Coincident(g2,g3)
    c: Coincident(g3,g0)
    c: Horizontal(g0)
    c: Horizontal(g2)
    c: Vertical(g1)
    c: Coincident(g-3,g2)
    c: Coincident(g0,g-3)
    c: DistanceX(g-4,g0) = 4
FEATURE [PartDesign::Pad] Pad072
  AllowMultiFace = false
  BaseFeature = -> Pad071
  Length = 1.6
  Length2 = 100
  Profile = -> Sketch141
  Type = 0
FEATURE [Sketcher::SketchObject] Sketch142
  ExternalGeometry = -> [Pad068]
  MapMode = 5
  Placement = pos=(0,0,22) rot=(0,0,1;0rad)
  Support = -> [Pad068]
  sketch-geometry (6):
    g0: ArcOfCircle CenterX=0 CenterY=0 CenterZ=0 NormalX=0 NormalY=0 NormalZ=1 AngleXU=0 Radius=1.8 StartAngle=4.71239 EndAngle=7.85398
    g1: LineSegment StartX=6e-16 StartY=1.8 StartZ=0 EndX=-1.69706 EndY=1.8 EndZ=0
    g2: LineSegment StartX=-3e-16 StartY=-1.8 StartZ=0 EndX=-1.69706 EndY=-1.8 EndZ=0
    g3: ArcOfCircle CenterX=0 CenterY=0 CenterZ=0 NormalX=0 NormalY=0 NormalZ=1 AngleXU=0 Radius=1.8 StartAngle=2.45182 EndAngle=3.83137
    g4: ArcOfCircle CenterX=-1.69706 CenterY=1.4 CenterZ=0 NormalX=0 NormalY=0 NormalZ=1 AngleXU=0 Radius=0.4 StartAngle=5.59341 EndAngle=7.85398
    g5: ArcOfCircle CenterX=-1.69706 CenterY=-1.4 CenterZ=0 NormalX=0 NormalY=0 NormalZ=1 AngleXU=0 Radius=0.4 StartAngle=4.71239 EndAngle=6.97296
  constraints (16):
    c: Coincident(g0,g-1)
    c: Coincident(g0,g-3)
    c: Coincident(g0,g-3)
    c: Coincident(g1,g0)
    c: Horizontal(g1)
    c: Coincident(g2,g0)
    c: Horizontal(g2)
    c: Equal(g1,g2)
    c: Coincident(g3,g0)
    c: Equal(g4,g5)
    c: Tangent(g4,g3) = 1.5708
    c: Tangent(g5,g3) = 1.5708
    c: Tangent(g5,g2) = 1.5708
    c: Tangent(g4,g1) = -1.5708
    c: Radius(g4) = 0.4
    c: Equal(g3,g0)
FEATURE [PartDesign::Pocket] Pocket064
  AllowMultiFace = false
  BaseFeature = -> Pad068
  Length = 2
  Length2 = 100
  Profile = -> Sketch142
  Type = 0
FEATURE [Sketcher::SketchObject] Sketch143
  ExternalGeometry = -> [Pocket064]
  MapMode = 5
  Placement = pos=(0,0,22) rot=(0,0,1;0rad)
  Support = -> [Pocket064]
  sketch-geometry (4):
    g0: LineSegment StartX=-1.8 StartY=1.8 StartZ=0 EndX=-3.4 EndY=1.8 EndZ=0
    g1: LineSegment StartX=-3.4 StartY=1.8 StartZ=0 EndX=-3.4 EndY=-1.8 EndZ=0
    g2: LineSegment StartX=-3.4 StartY=-1.8 StartZ=0 EndX=-1.8 EndY=-1.8 EndZ=0
    g3: LineSegment StartX=-1.8 StartY=-1.8 StartZ=0 EndX=-1.8 EndY=1.8 EndZ=0
  constraints (12):
    c: Coincident(g0,g1)
    c: Coincident(g1,g2)
    c: Coincident(g2,g3)
    c: Coincident(g3,g0)
    c: Horizontal(g0)
    c: Horizontal(g2)
    c: Vertical(g1)
    c: Vertical(g3)
    c: Distance(g0) = 1.6
    c: Tangent(g3,g-3)
    c: PointOnObject(g0,g-4)
    c: PointOnObject(g1,g-5)
FEATURE [PartDesign::Pad] Pad073
  AllowMultiFace = false
  BaseFeature = -> Pocket064
  Length = 11
  Length2 = 100
  Profile = -> Sketch143
  Type = 0
  expr: Length = 9 + 2
FEATURE [Sketcher::SketchObject] Sketch144
  ExternalGeometry = -> [Pad073]
  MapMode = 5
  Placement = pos=(0,0,22) rot=(0,0,1;0rad)
  Support = -> [Pad073]
  sketch-geometry (4):
    g0: LineSegment StartX=-4.14222 StartY=-0.2 StartZ=0 EndX=-3.4 EndY=-0.2 EndZ=0
    g1: LineSegment StartX=-6.8 StartY=-1.8 StartZ=0 EndX=-4.14222 EndY=-0.2 EndZ=0
    g2: LineSegment StartX=-6.8 StartY=-1.8 StartZ=0 EndX=-3.4 EndY=-1.8 EndZ=0
    g3: LineSegment StartX=-3.4 StartY=-1.8 StartZ=0 EndX=-3.4 EndY=-0.2 EndZ=0
  constraints (10):
    c: Coincident(g1,g0)
    c: Coincident(g2,g1)
    c: Coincident(g3,g2)
    c: Coincident(g3,g0)
    c: Distance(g3) = 1.6
    c: Coincident(g1,g-3)
    c: PointOnObject(g0,g-3)
    c: Horizontal(g0)
    c: PointOnObject(g0,g-4)
    c: Coincident(g2,g-4)
FEATURE [PartDesign::Pad] Pad074
  AllowMultiFace = false
  BaseFeature = -> Pad073
  Length = 2
  Length2 = 100
  Profile = -> Sketch144
  Type = 0
FEATURE [Sketcher::SketchObject] Sketch145
  ExternalGeometry = -> [Pad074]
  MapMode = 5
  Placement = pos=(0,0,33) rot=(0,0,1;0rad)
  Support = -> [Pad074]
  sketch-geometry (4):
    g0: LineSegment StartX=-1.8 StartY=1.8 StartZ=0 EndX=-7.4 EndY=1.8 EndZ=0
    g1: LineSegment StartX=-7.4 StartY=1.8 StartZ=0 EndX=-7.4 EndY=-1.8 EndZ=0
    g2: LineSegment StartX=-7.4 StartY=-1.8 StartZ=0 EndX=-1.8 EndY=-1.8 EndZ=0
    g3: LineSegment StartX=-1.8 StartY=-1.8 StartZ=0 EndX=-1.8 EndY=1.8 EndZ=0
  constraints (10):
    c: Coincident(g0,g1)
    c: Coincident(g1,g2)
    c: Coincident(g2,g3)
    c: Coincident(g3,g0)
    c: Horizontal(g0)
    c: Horizontal(g2)
    c: Vertical(g1)
    c: Coincident(g0,g-3)
    c: Coincident(g2,g-3)
    c: DistanceX(g0,g-4) = 4
FEATURE [PartDesign::Pad] Pad075
  AllowMultiFace = false
  BaseFeature = -> Pad074
  Length = 1.6
  Length2 = 100
  Profile = -> Sketch145
  Type = 0
FEATURE [Sketcher::SketchObject] Sketch149
  MapMode = 5
  Support = -> [XY_Plane044]
  expr: Constraints[3] = 1 + 0.4 * 2
  expr: Constraints[2] = 2 / 2
  sketch-geometry (2):
    g0: Circle CenterX=0 CenterY=0 CenterZ=0 NormalX=0 NormalY=0 NormalZ=1 AngleXU=0 Radius=1
    g1: Circle CenterX=0 CenterY=0 CenterZ=0 NormalX=0 NormalY=0 NormalZ=1 AngleXU=0 Radius=1.8
  constraints (4):
    c: Coincident(g0,g-1)
    c: Coincident(g1,g0)
    c: Radius(g0) = 1
    c: Radius(g1) = 1.8
FEATURE [PartDesign::Pad] Pad078
  AllowMultiFace = false
  Length = 18
  Length2 = 100
  Profile = -> Sketch149
  Type = 0
FEATURE [Sketcher::SketchObject] Sketch147
  ExternalGeometry = -> [Pad078]
  MapMode = 5
  Placement = pos=(0,0,18) rot=(0,0,1;0rad)
  Support = -> [Pad078]
  expr: Constraints[15] = 20 - 2.4 * 2 - 2 - 0.2
  expr: Constraints[12] = 21 + 1.6 - (2 - 1.6) - 0.2
  sketch-geometry (6):
    g0: LineSegment StartX=-10.8 StartY=1.8 StartZ=0 EndX=11.2 EndY=1.8 EndZ=0
    g1: LineSegment StartX=11.2 StartY=1.8 StartZ=0 EndX=11.2 EndY=-1.8 EndZ=0
    g2: LineSegment StartX=11.2 StartY=-1.8 StartZ=0 EndX=-10.8 EndY=-1.8 EndZ=0
    g3: LineSegment StartX=-10.8 StartY=-1.8 StartZ=0 EndX=-10.8 EndY=1.8 EndZ=0
    g4: Circle CenterX=0 CenterY=0 CenterZ=0 NormalX=0 NormalY=0 NormalZ=1 AngleXU=0 Radius=1
    g5: GeomPoint X=-1.8 Y=0 Z=0
  constraints (16):
    c: Coincident(g0,g1)
    c: Coincident(g1,g2)
    c: Coincident(g2,g3)
    c: Coincident(g3,g0)
    c: Horizontal(g0)
    c: Horizontal(g2)
    c: Vertical(g1)
    c: Vertical(g3)
    c: Tangent(g0,g-3)
    c: Tangent(g-3,g2)
    c: Coincident(g4,g-1)
    c: Equal(g-4,g4)
    c: Distance(g0) = 22
    c: PointOnObject(g5,g-3)
    c: PointOnObject(g5,g-1)
    c: DistanceX(g5,g0) = 13
FEATURE [PartDesign::Pad] Pad077
  AllowMultiFace = false
  BaseFeature = -> Pad078
  Length = 2
  Length2 = 100
  Profile = -> Sketch147
  Type = 0
FEATURE [Sketcher::SketchObject] Sketch146
  ExternalGeometry = -> [Pad077]
  MapMode = 5
  Placement = pos=(0,-3,0) rot=(1,0,0;1.5708rad)
  sketch-geometry (3):
    g0: LineSegment StartX=11.2 StartY=20 StartZ=0 EndX=11.2 EndY=18 EndZ=0
    g1: LineSegment StartX=11.2 StartY=20 StartZ=0 EndX=8.2 EndY=18 EndZ=0
    g2: LineSegment StartX=11.2 StartY=18 StartZ=0 EndX=8.2 EndY=18 EndZ=0
  constraints (7):
    c: Coincident(g1,g0)
    c: Coincident(g2,g0)
    c: Coincident(g2,g1)
    c: Horizontal(g2)
    c: Distance(g2) = 3
    c: Coincident(g0,g-3)
    c: Coincident(g0,g-3)
FEATURE [Sketcher::SketchObject] Sketch150
  MapMode = 5
  Support = -> [XY_Plane045]
  expr: Constraints[3] = 1 + 0.4 * 2
  expr: Constraints[2] = 2 / 2
  sketch-geometry (2):
    g0: Circle CenterX=0 CenterY=0 CenterZ=0 NormalX=0 NormalY=0 NormalZ=1 AngleXU=0 Radius=1
    g1: Circle CenterX=0 CenterY=0 CenterZ=0 NormalX=0 NormalY=0 NormalZ=1 AngleXU=0 Radius=1.8
  constraints (4):
    c: Coincident(g0,g-1)
    c: Coincident(g1,g0)
    c: Radius(g0) = 1
    c: Radius(g1) = 1.8
FEATURE [PartDesign::Pad] Pad079
  AllowMultiFace = false
  Length = 18
  Length2 = 100
  Profile = -> Sketch150
  Type = 0
FEATURE [Sketcher::SketchObject] Sketch148
  ExternalGeometry = -> [Pad079]
  MapMode = 5
  Placement = pos=(0,0,18) rot=(0,0,1;0rad)
  Support = -> [Pad079]
  sketch-geometry (6):
    g0: LineSegment StartX=-3.8 StartY=1.8 StartZ=0 EndX=4e-16 EndY=1.8 EndZ=0
    g1: LineSegment StartX=-3e-16 StartY=-1.8 StartZ=0 EndX=-3.8 EndY=-1.8 EndZ=0
    g2: LineSegment StartX=-3.8 StartY=-1.8 StartZ=0 EndX=-3.8 EndY=1.8 EndZ=0
    g3: ArcOfCircle CenterX=0 CenterY=0 CenterZ=0 NormalX=0 NormalY=0 NormalZ=1 AngleXU=0 Radius=1.8 StartAngle=4.71239 EndAngle=7.85398
    g4: Circle CenterX=0 CenterY=0 CenterZ=0 NormalX=0 NormalY=0 NormalZ=1 AngleXU=0 Radius=1
    g5: GeomPoint X=-1.8 Y=0 Z=0
  constraints (16):
    c: Coincident(g1,g2)
    c: Coincident(g2,g0)
    c: Horizontal(g0)
    c: Horizontal(g1)
    c: Vertical(g2)
    c: Coincident(g3,g-1)
    c: PointOnObject(g3,g-4)
    c: PointOnObject(g3,g-2)
    c: PointOnObject(g3,g-2)
    c: Coincident(g0,g3)
    c: Coincident(g1,g3)
    c: Coincident(g4,g3)
    c: Equal(g-3,g4)
    c: PointOnObject(g5,g-4)
    c: PointOnObject(g5,g-1)
    c: DistanceX(g0,g5) = 2
FEATURE [PartDesign::Pad] Pad080
  AllowMultiFace = false
  BaseFeature = -> Pad079
  Length = 4
  Length2 = 100
  Profile = -> Sketch148
  Type = 0
FEATURE [PartDesign::Pocket] Pocket066
  AllowMultiFace = false
  BaseFeature = -> Pad077
  Length = 5
  Length2 = 100
  Profile = -> Sketch146
  Type = 1
FEATURE [Sketcher::SketchObject] Sketch151
  ExternalGeometry = -> [Pocket066]
  MapMode = 5
  Placement = pos=(0,0,20) rot=(0,0,1;0rad)
  Support = -> [Pocket066]
  sketch-geometry (5):
    g0: LineSegment StartX=11.19 StartY=-2e-16 StartZ=0 EndX=8.2 EndY=-1.8 EndZ=0
    g1: LineSegment StartX=8.2 StartY=1.8 StartZ=0 EndX=11.19 EndY=-2e-16 EndZ=0
    g2: LineSegment StartX=8.2 StartY=-1.8 StartZ=0 EndX=11.2 EndY=-1.8 EndZ=0
    g3: LineSegment StartX=8.2 StartY=1.8 StartZ=0 EndX=11.2 EndY=1.8 EndZ=0
    g4: LineSegment StartX=11.2 StartY=-1.8 StartZ=0 EndX=11.2 EndY=1.8 EndZ=0
  constraints (13):
    c: Coincident(g1,g0)
    c: Coincident(g2,g0)
    c: Horizontal(g2)
    c: Horizontal(g3)
    c: Distance(g2) = 3
    c: Equal(g2,g3)
    c: Coincident(g1,g3)
    c: Coincident(g2,g4)
    c: Coincident(g4,g3)
    c: PointOnObject(g0,g-1)
    c: DistanceX(g0,g3) = 0.01
    c: Coincident(g3,g-3)
    c: Coincident(g2,g-3)
FEATURE [PartDesign::Pocket] Pocket065
  AllowMultiFace = false
  BaseFeature = -> Pocket066
  Length = 5
  Length2 = 100
  Profile = -> Sketch151
  Type = 1
FEATURE [Sketcher::SketchObject] Sketch152
  ExternalGeometry = -> [Pad080]
  MapMode = 5
  Placement = pos=(0,-1.8,0) rot=(1,0,0;1.5708rad)
  Support = -> [Pad080]
  sketch-geometry (3):
    g0: LineSegment StartX=-3.8 StartY=20 StartZ=0 EndX=-3.8 EndY=18 EndZ=0
    g1: LineSegment StartX=-3.8 StartY=20 StartZ=0 EndX=-6.8 EndY=18 EndZ=0
    g2: LineSegment StartX=-3.8 StartY=18 StartZ=0 EndX=-6.8 EndY=18 EndZ=0
  constraints (8):
    c: Coincident(g2,g1)
    c: Coincident(g2,g0)
    c: Horizontal(g2)
    c: Distance(g2) = 3
    c: Coincident(g-3,g0)
    c: Coincident(g1,g0)
    c: PointOnObject(g0,g-3)
    c: Distance(g0) = 2
FEATURE [PartDesign::Pad] Pad082
  AllowMultiFace = false
  BaseFeature = -> Pad080
  Length = 10
  Length2 = 100
  Profile = -> Sketch152
  Reversed = true
  Type = 3
  UpToFace = -> Pad080 [Face7]
FEATURE [Sketcher::SketchObject] Sketch153
  ExternalGeometry = -> [Pad080]
  MapMode = 5
  Placement = pos=(0,0,22) rot=(0,0,1;0rad)
  Support = -> [Pad082]
  sketch-geometry (5):
    g0: LineSegment StartX=-3.8 StartY=1.8 StartZ=0 EndX=-6.8 EndY=1.8 EndZ=0
    g1: LineSegment StartX=-3.8 StartY=-1.8 StartZ=0 EndX=-3.8 EndY=1.8 EndZ=0
    g2: LineSegment StartX=-6.8 StartY=1.8 StartZ=0 EndX=-3.81 EndY=0 EndZ=0
    g3: LineSegment StartX=-3.81 StartY=0 StartZ=0 EndX=-6.8 EndY=-1.8 EndZ=0
    g4: LineSegment StartX=-6.8 StartY=-1.8 StartZ=0 EndX=-3.8 EndY=-1.8 EndZ=0
  constraints (13):
    c: Horizontal(g4)
    c: Horizontal(g0)
    c: Equal(g0,g4)
    c: Distance(g0) = 3
    c: Coincident(g1,g-3)
    c: Coincident(g1,g-3)
    c: Coincident(g2,g3)
    c: PointOnObject(g2,g-1)
    c: Coincident(g2,g0)
    c: Coincident(g0,g1)
    c: Coincident(g3,g4)
    c: Coincident(g1,g4)
    c: DistanceX(g2,g1) = 0.01
FEATURE [PartDesign::Pad] Pad081
  AllowMultiFace = false
  BaseFeature = -> Pad082
  Length = 10
  Length2 = 100
  Profile = -> Sketch153
  Reversed = true
  Type = 3
  UpToFace = -> Pad082 [Face4]
FEATURE [Sketcher::SketchObject] Sketch158
  ExternalGeometry = -> [Pad081]
  MapMode = 5
  Placement = pos=(0,0,22) rot=(0,0,1;0rad)
  Support = -> [Pad081]
  sketch-geometry (6):
    g0: ArcOfCircle CenterX=0 CenterY=0 CenterZ=0 NormalX=0 NormalY=0 NormalZ=1 AngleXU=0 Radius=1.8 StartAngle=4.71239 EndAngle=7.85398
    g1: LineSegment StartX=6e-16 StartY=1.8 StartZ=0 EndX=-1.69706 EndY=1.8 EndZ=0
    g2: LineSegment StartX=-3e-16 StartY=-1.8 StartZ=0 EndX=-1.69706 EndY=-1.8 EndZ=0
    g3: ArcOfCircle CenterX=0 CenterY=0 CenterZ=0 NormalX=0 NormalY=0 NormalZ=1 AngleXU=0 Radius=1.8 StartAngle=2.45182 EndAngle=3.83137
    g4: ArcOfCircle CenterX=-1.69706 CenterY=1.4 CenterZ=0 NormalX=0 NormalY=0 NormalZ=1 AngleXU=0 Radius=0.4 StartAngle=5.59341 EndAngle=7.85398
    g5: ArcOfCircle CenterX=-1.69706 CenterY=-1.4 CenterZ=0 NormalX=0 NormalY=0 NormalZ=1 AngleXU=0 Radius=0.4 StartAngle=4.71239 EndAngle=6.97296
  constraints (16):
    c: Coincident(g0,g-1)
    c: Coincident(g0,g-3)
    c: Coincident(g0,g-3)
    c: Coincident(g1,g0)
    c: Horizontal(g1)
    c: Coincident(g2,g0)
    c: Horizontal(g2)
    c: Equal(g1,g2)
    c: Coincident(g3,g0)
    c: Equal(g4,g5)
    c: Tangent(g4,g3) = 1.5708
    c: Tangent(g5,g3) = 1.5708
    c: Tangent(g5,g2) = 1.5708
    c: Tangent(g4,g1) = -1.5708
    c: Radius(g4) = 0.4
    c: Equal(g3,g0)
FEATURE [PartDesign::Pocket] Pocket067
  AllowMultiFace = false
  BaseFeature = -> Pad081
  Length = 2
  Length2 = 100
  Profile = -> Sketch158
  Type = 0
FEATURE [Sketcher::SketchObject] Sketch154
  ExternalGeometry = -> [Pocket067]
  MapMode = 5
  Placement = pos=(0,0,22) rot=(0,0,1;0rad)
  Support = -> [Pocket067]
  sketch-geometry (4):
    g0: LineSegment StartX=-1.8 StartY=1.8 StartZ=0 EndX=-3.4 EndY=1.8 EndZ=0
    g1: LineSegment StartX=-3.4 StartY=1.8 StartZ=0 EndX=-3.4 EndY=-1.8 EndZ=0
    g2: LineSegment StartX=-3.4 StartY=-1.8 StartZ=0 EndX=-1.8 EndY=-1.8 EndZ=0
    g3: LineSegment StartX=-1.8 StartY=-1.8 StartZ=0 EndX=-1.8 EndY=1.8 EndZ=0
  constraints (12):
    c: Coincident(g0,g1)
    c: Coincident(g1,g2)
    c: Coincident(g2,g3)
    c: Coincident(g3,g0)
    c: Horizontal(g0)
    c: Horizontal(g2)
    c: Vertical(g1)
    c: Vertical(g3)
    c: Distance(g0) = 1.6
    c: Tangent(g3,g-3)
    c: PointOnObject(g0,g-4)
    c: PointOnObject(g1,g-5)
FEATURE [PartDesign::Pad] Pad076
  AllowMultiFace = false
  BaseFeature = -> Pocket067
  Length = 8.5
  Length2 = 100
  Profile = -> Sketch154
  Type = 0
  expr: Length = 6.5 + 2
FEATURE [Sketcher::SketchObject] Sketch156
  ExternalGeometry = -> [Pad076]
  MapMode = 5
  Placement = pos=(0,0,22) rot=(0,0,1;0rad)
  Support = -> [Pad076]
  sketch-geometry (4):
    g0: LineSegment StartX=-6.8 StartY=1.8 StartZ=0 EndX=-3.4 EndY=1.8 EndZ=0
    g1: LineSegment StartX=-4.14222 StartY=0.2 StartZ=0 EndX=-6.8 EndY=1.8 EndZ=0
    g2: LineSegment StartX=-4.14222 StartY=0.2 StartZ=0 EndX=-3.4 EndY=0.2 EndZ=0
    g3: LineSegment StartX=-3.4 StartY=0.2 StartZ=0 EndX=-3.4 EndY=1.8 EndZ=0
  constraints (11):
    c: Coincident(g1,g0)
    c: Coincident(g2,g1)
    c: Coincident(g3,g2)
    c: Coincident(g3,g0)
    c: Distance(g3) = 1.6
    c: Horizontal(g0)
    c: Horizontal(g2)
    c: Coincident(g0,g-4)
    c: PointOnObject(g0,g-3)
    c: PointOnObject(g1,g-3)
    c: Vertical(g3)
FEATURE [PartDesign::Pad] Pad031
  AllowMultiFace = false
  BaseFeature = -> Pad076
  Length = 2
  Length2 = 100
  Profile = -> Sketch156
  Type = 0
FEATURE [Sketcher::SketchObject] Sketch160
  ExternalGeometry = -> [Pad031]
  MapMode = 5
  Placement = pos=(0,0,30.5) rot=(0,0,1;0rad)
  Support = -> [Pad031]
  sketch-geometry (4):
    g0: LineSegment StartX=-1.8 StartY=-1.8 StartZ=0 EndX=-7.4 EndY=-1.8 EndZ=0
    g1: LineSegment StartX=-7.4 StartY=-1.8 StartZ=0 EndX=-7.4 EndY=1.8 EndZ=0
    g2: LineSegment StartX=-7.4 StartY=1.8 StartZ=0 EndX=-1.8 EndY=1.8 EndZ=0
    g3: LineSegment StartX=-1.8 StartY=1.8 StartZ=0 EndX=-1.8 EndY=-1.8 EndZ=0
  constraints (10):
    c: Coincident(g0,g1)
    c: Coincident(g1,g2)
    c: Coincident(g2,g3)
    c: Coincident(g3,g0)
    c: Horizontal(g0)
    c: Horizontal(g2)
    c: Vertical(g1)
    c: Coincident(g2,g-3)
    c: Coincident(g0,g-3)
    c: DistanceX(g1,g-4) = 4
FEATURE [PartDesign::Pad] Pad084
  AllowMultiFace = false
  BaseFeature = -> Pad031
  Length = 1.6
  Length2 = 100
  Profile = -> Sketch160
  Type = 0
FEATURE [Sketcher::SketchObject] Sketch161
  ExternalGeometry = -> [Pocket065]
  MapMode = 5
  Placement = pos=(0,0,20) rot=(0,0,1;0rad)
  sketch-geometry (9):
    g0: LineSegment StartX=-10.8 StartY=1.8 StartZ=0 EndX=-10.8 EndY=-1.8 EndZ=0
    g1: LineSegment StartX=8.2 StartY=1.8 StartZ=0 EndX=11.19 EndY=-7e-16 EndZ=0
    g2: LineSegment StartX=11.19 StartY=-7e-16 StartZ=0 EndX=8.2 EndY=-1.8 EndZ=0
    g3: ArcOfCircle CenterX=0 CenterY=0 CenterZ=0 NormalX=0 NormalY=0 NormalZ=1 AngleXU=0 Radius=1.86815 StartAngle=1.84174 EndAngle=4.44144
    g4: ArcOfCircle CenterX=0 CenterY=0 CenterZ=0 NormalX=0 NormalY=0 NormalZ=1 AngleXU=0 Radius=1.86815 StartAngle=4.98334 EndAngle=7.58303
    g5: LineSegment StartX=-10.8 StartY=-1.8 StartZ=0 EndX=-0.5 EndY=-1.8 EndZ=0
    g6: LineSegment StartX=0.5 StartY=-1.8 StartZ=0 EndX=8.2 EndY=-1.8 EndZ=0
    g7: LineSegment StartX=8.2 StartY=1.8 StartZ=0 EndX=0.5 EndY=1.8 EndZ=0
    g8: LineSegment StartX=-0.5 StartY=1.8 StartZ=0 EndX=-10.8 EndY=1.8 EndZ=0
  constraints (22):
    c: Coincident(g2,g1)
    c: Coincident(g0,g-3)
    c: Coincident(g0,g-5)
    c: Coincident(g2,g-5)
    c: Coincident(g-4,g1)
    c: Coincident(g1,g-4)
    c: Coincident(g3,g-1)
    c: Coincident(g4,g3)
    c: Equal(g4,g3)
    c: Coincident(g5,g0)
    c: Coincident(g5,g3)
    c: Coincident(g6,g4)
    c: Coincident(g6,g2)
    c: Coincident(g7,g1)
    c: Coincident(g7,g4)
    c: Coincident(g8,g3)
    c: Coincident(g8,g0)
    c: Horizontal(g7)
    c: Horizontal(g8)
    c: Horizontal(g5)
    c: Horizontal(g6)
    c: DistanceX(g3,g4) = 1
FEATURE [PartDesign::Pad] Pad083
  AllowMultiFace = false
  BaseFeature = -> Pocket065
  Length = 2
  Length2 = 100
  Profile = -> Sketch161
  Type = 0
FEATURE [Sketcher::SketchObject] Sketch155
  ExternalGeometry = -> [Pad083]
  MapMode = 5
  Placement = pos=(0,0,22) rot=(0,0,1;0rad)
  Support = -> [Pad083]
  sketch-geometry (4):
    g0: LineSegment StartX=-10.8 StartY=1.8 StartZ=0 EndX=-9.2 EndY=1.8 EndZ=0
    g1: LineSegment StartX=-9.2 StartY=1.8 StartZ=0 EndX=-9.2 EndY=-1.8 EndZ=0
    g2: LineSegment StartX=-9.2 StartY=-1.8 StartZ=0 EndX=-10.8 EndY=-1.8 EndZ=0
    g3: LineSegment StartX=-10.8 StartY=-1.8 StartZ=0 EndX=-10.8 EndY=1.8 EndZ=0
  constraints (10):
    c: Coincident(g0,g1)
    c: Coincident(g1,g2)
    c: Coincident(g2,g3)
    c: Coincident(g3,g0)
    c: Horizontal(g0)
    c: Horizontal(g2)
    c: Vertical(g1)
    c: Coincident(g0,g-3)
    c: Coincident(g2,g-3)
    c: Distance(g0) = 1.6
FEATURE [PartDesign::Pad] Pad032
  AllowMultiFace = false
  BaseFeature = -> Pad083
  Length = 8.5
  Length2 = 100
  Profile = -> Sketch155
  Type = 0
  expr: Length = 6.5 + 2
FEATURE [Sketcher::SketchObject] Sketch159
  ExternalGeometry = -> [Pad032]
  MapMode = 5
  Placement = pos=(0,0,22) rot=(0,0,1;0rad)
  Support = -> [Pad032]
  sketch-geometry (9):
    g0: LineSegment StartX=-9.2 StartY=0.2 StartZ=0 EndX=-1.85742 EndY=0.2 EndZ=0
    g1: LineSegment StartX=-0.5 StartY=1.8 StartZ=0 EndX=-9.2 EndY=1.8 EndZ=0
    g2: LineSegment StartX=-9.2 StartY=1.8 StartZ=0 EndX=-9.2 EndY=0.2 EndZ=0
    g3: ArcOfCircle CenterX=0 CenterY=0 CenterZ=0 NormalX=0 NormalY=0 NormalZ=1 AngleXU=0 Radius=1.86815 StartAngle=1.84174 EndAngle=3.03433
    g4: ArcOfCircle CenterX=0 CenterY=0 CenterZ=0 NormalX=0 NormalY=0 NormalZ=1 AngleXU=0 Radius=1.86815 StartAngle=0.107263 EndAngle=1.29985
    g5: LineSegment StartX=0.5 StartY=1.8 StartZ=0 EndX=8.2 EndY=1.8 EndZ=0
    g6: LineSegment StartX=1.85742 StartY=0.2 StartZ=0 EndX=10.8578 EndY=0.2 EndZ=0
    g7: LineSegment StartX=10.8578 StartY=0.2 StartZ=0 EndX=8.2 EndY=1.8 EndZ=0
    g8: LineSegment [constr] StartX=-1.85742 StartY=0.2 StartZ=0 EndX=1.85742 EndY=0.2 EndZ=0
  constraints (24):
    c: Coincident(g1,g2)
    c: Coincident(g2,g0)
    c: Vertical(g2)
    c: Coincident(g3,g-1)
    c: Coincident(g3,g1)
    c: Coincident(g3,g0)
    c: Distance(g2) = 1.6
    c: Coincident(g4,g3)
    c: Coincident(g5,g4)
    c: Coincident(g6,g4)
    c: Coincident(g5,g7)
    c: Coincident(g6,g7)
    c: Horizontal(g6)
    c: Horizontal(g0)
    c: Coincident(g1,g-3)
    c: Coincident(g5,g-4)
    c: PointOnObject(g6,g-4)
    c: Horizontal(g1)
    c: Horizontal(g5)
    c: PointOnObject(g1,g-5)
    c: PointOnObject(g4,g-6)
    c: Coincident(g8,g0)
    c: Coincident(g8,g4)
    c: Horizontal(g8)
FEATURE [PartDesign::Pad] Pad033
  AllowMultiFace = false
  BaseFeature = -> Pad032
  Length = 2
  Length2 = 100
  Profile = -> Sketch159
  Type = 0
FEATURE [Sketcher::SketchObject] Sketch157
  ExternalGeometry = -> [Pad033]
  MapMode = 5
  Placement = pos=(0,0,30.5) rot=(0,0,1;0rad)
  Support = -> [Pad033]
  sketch-geometry (4):
    g0: LineSegment StartX=-10.8 StartY=1.8 StartZ=0 EndX=-5.2 EndY=1.8 EndZ=0
    g1: LineSegment StartX=-5.2 StartY=1.8 StartZ=0 EndX=-5.2 EndY=-1.8 EndZ=0
    g2: LineSegment StartX=-5.2 StartY=-1.8 StartZ=0 EndX=-10.8 EndY=-1.8 EndZ=0
    g3: LineSegment StartX=-10.8 StartY=-1.8 StartZ=0 EndX=-10.8 EndY=1.8 EndZ=0
  constraints (10):
    c: Coincident(g0,g1)
    c: Coincident(g1,g2)
    c: Coincident(g2,g3)
    c: Coincident(g3,g0)
    c: Horizontal(g0)
    c: Horizontal(g2)
    c: Vertical(g1)
    c: Coincident(g0,g-3)
    c: Coincident(g2,g-3)
    c: DistanceX(g-4,g0) = 4
FEATURE [PartDesign::Pad] Pad030
  AllowMultiFace = false
  BaseFeature = -> Pad033
  Length = 1.6
  Length2 = 100
  Profile = -> Sketch157
  Type = 0
FEATURE [Sketcher::SketchObject] Sketch162
  ExternalGeometry = -> [Pad084]
  MapMode = 5
  Placement = pos=(0,0,32.1) rot=(0,0,1;0rad)
  Support = -> [Pad084]
  sketch-geometry (4):
    g0: LineSegment StartX=-3.4 StartY=-1.8 StartZ=0 EndX=-7.4 EndY=-1.8 EndZ=0
    g1: LineSegment StartX=-7.4 StartY=-1.8 StartZ=0 EndX=-7.4 EndY=-0.8 EndZ=0
    g2: LineSegment StartX=-7.4 StartY=-0.8 StartZ=0 EndX=-3.4 EndY=-0.8 EndZ=0
    g3: LineSegment StartX=-3.4 StartY=-0.8 StartZ=0 EndX=-3.4 EndY=-1.8 EndZ=0
  constraints (11):
    c: Coincident(g0,g1)
    c: Coincident(g1,g2)
    c: Coincident(g2,g3)
    c: Coincident(g3,g0)
    c: Horizontal(g0)
    c: Horizontal(g2)
    c: Vertical(g1)
    c: Vertical(g3)
    c: Coincident(g0,g-4)
    c: PointOnObject(g1,g-3)
    c: Distance(g3) = 1
FEATURE [PartDesign::Pocket] Pocket068
  AllowMultiFace = false
  BaseFeature = -> Pad084
  Length = 5
  Length2 = 100
  Profile = -> Sketch162
  Type = 2
FEATURE [Sketcher::SketchObject] Sketch163
  ExternalGeometry = -> [Pad030]
  MapMode = 5
  Placement = pos=(0,0,32.1) rot=(0,0,1;0rad)
  Support = -> [Pad030]
  sketch-geometry (4):
    g0: LineSegment StartX=-9.2 StartY=-1.8 StartZ=0 EndX=-5.2 EndY=-1.8 EndZ=0
    g1: LineSegment StartX=-5.2 StartY=-1.8 StartZ=0 EndX=-5.2 EndY=-0.8 EndZ=0
    g2: LineSegment StartX=-5.2 StartY=-0.8 StartZ=0 EndX=-9.2 EndY=-0.8 EndZ=0
    g3: LineSegment StartX=-9.2 StartY=-0.8 StartZ=0 EndX=-9.2 EndY=-1.8 EndZ=0
  constraints (11):
    c: Coincident(g0,g1)
    c: Coincident(g1,g2)
    c: Coincident(g2,g3)
    c: Coincident(g3,g0)
    c: Horizontal(g0)
    c: Horizontal(g2)
    c: Vertical(g1)
    c: Vertical(g3)
    c: Coincident(g0,g-4)
    c: PointOnObject(g1,g-3)
    c: Distance(g3) = 1
FEATURE [PartDesign::Pocket] Pocket069
  AllowMultiFace = false
  BaseFeature = -> Pad030
  Length = 5
  Length2 = 100
  Profile = -> Sketch163
  Type = 2
FEATURE [PartDesign::Body] Body041
  Group = -> [Sketch149,Pad078,Sketch147,Pad077,Sketch146,Sketch151,Pocket066,Pocket065,Sketch161,Pad083,Sketch155,Pad032,Sketch159,Pad033,Sketch157,Pad030,Sketch163,Pocket069]
  Origin = -> Origin046
  Placement = pos=(0,35.2,0) rot=(0,0,1;0rad)
  Tip = -> Pocket069
  expr: .Placement.Base.y = 40 - 2.4 * 2
FEATURE [Sketcher::SketchObject] Sketch164
  ExternalGeometry = -> [Pad072]
  MapMode = 5
  Placement = pos=(0,0,34.6) rot=(0,0,1;0rad)
  Support = -> [Pad072]
  sketch-geometry (4):
    g0: LineSegment StartX=-9.2 StartY=1.8 StartZ=0 EndX=-5.2 EndY=1.8 EndZ=0
    g1: LineSegment StartX=-5.2 StartY=1.8 StartZ=0 EndX=-5.2 EndY=0.8 EndZ=0
    g2: LineSegment StartX=-5.2 StartY=0.8 StartZ=0 EndX=-9.2 EndY=0.8 EndZ=0
    g3: LineSegment StartX=-9.2 StartY=0.8 StartZ=0 EndX=-9.2 EndY=1.8 EndZ=0
  constraints (11):
    c: Coincident(g0,g1)
    c: Coincident(g1,g2)
    c: Coincident(g2,g3)
    c: Coincident(g3,g0)
    c: Horizontal(g0)
    c: Horizontal(g2)
    c: Vertical(g1)
    c: Vertical(g3)
    c: Coincident(g0,g-4)
    c: PointOnObject(g1,g-3)
    c: Distance(g1) = 1
FEATURE [PartDesign::Pocket] Pocket070
  AllowMultiFace = false
  BaseFeature = -> Pad072
  Length = 5
  Length2 = 100
  Profile = -> Sketch164
  Type = 2
FEATURE [PartDesign::Body] Body038
  Group = -> [Sketch131,Pad063,Sketch132,Pad064,Sketch135,Sketch136,Pocket062,Pocket063,Sketch032,Pad069,Sketch139,Pad070,Sketch140,Pad071,Sketch141,Pad072,Sketch164,Pocket070]
  Origin = -> Origin043
  Tip = -> Pocket070
FEATURE [Sketcher::SketchObject] Sketch165
  ExternalGeometry = -> [Pad075]
  MapMode = 5
  Placement = pos=(0,0,34.6) rot=(0,0,1;0rad)
  Support = -> [Pad075]
  sketch-geometry (4):
    g0: LineSegment StartX=-3.4 StartY=1.8 StartZ=0 EndX=-7.4 EndY=1.8 EndZ=0
    g1: LineSegment StartX=-7.4 StartY=1.8 StartZ=0 EndX=-7.4 EndY=0.8 EndZ=0
    g2: LineSegment StartX=-7.4 StartY=0.8 StartZ=0 EndX=-3.4 EndY=0.8 EndZ=0
    g3: LineSegment StartX=-3.4 StartY=0.8 StartZ=0 EndX=-3.4 EndY=1.8 EndZ=0
  constraints (11):
    c: Coincident(g0,g1)
    c: Coincident(g1,g2)
    c: Coincident(g2,g3)
    c: Coincident(g3,g0)
    c: Horizontal(g0)
    c: Horizontal(g2)
    c: Vertical(g1)
    c: Vertical(g3)
    c: Coincident(g0,g-4)
    c: PointOnObject(g1,g-3)
    c: Distance(g3) = 1
FEATURE [PartDesign::Pocket] Pocket071
  AllowMultiFace = false
  BaseFeature = -> Pad075
  Length = 5
  Length2 = 100
  Profile = -> Sketch165
  Type = 2
FEATURE [PartDesign::Body] Body039
  Group = -> [Sketch133,Pad065,Sketch134,Pad066,Sketch137,Sketch138,Pad067,Pad068,Sketch142,Pocket064,Sketch143,Pad073,Sketch144,Pad074,Sketch145,Pad075,Sketch165,Pocket071]
  Origin = -> Origin044
  Placement = pos=(15.2,0,0) rot=(0,0,1;0rad)
  Tip = -> Pocket071
  expr: .Placement.Base.x = 20 - 2.4 * 2
FEATURE [Sketcher::SketchObject] Sketch166
  ExternalGeometry = -> [Pocket068]
  MapMode = 5
  Support = -> [XY_Plane045]
  expr: Constraints[11] = (20 - 2.4 * 2) / 2 + 7.5 / 2
  sketch-geometry (4):
    g0: ArcOfCircle CenterX=0 CenterY=0 CenterZ=0 NormalX=0 NormalY=0 NormalZ=1 AngleXU=0 Radius=1.8 StartAngle=1.5708 EndAngle=4.71239
    g1: LineSegment StartX=0 StartY=1.8 StartZ=0 EndX=-11.35 EndY=1.8 EndZ=0
    g2: LineSegment StartX=0 StartY=-1.8 StartZ=0 EndX=-11.35 EndY=-1.8 EndZ=0
    g3: LineSegment StartX=-11.35 StartY=1.8 StartZ=0 EndX=-11.35 EndY=-1.8 EndZ=0
  constraints (12):
    c: Coincident(g0,g-1)
    c: PointOnObject(g0,g-2)
    c: PointOnObject(g0,g-2)
    c: Equal(g-3,g0)
    c: Coincident(g1,g0)
    c: Horizontal(g1)
    c: Coincident(g2,g0)
    c: Horizontal(g2)
    c: Coincident(g3,g1)
    c: Coincident(g3,g2)
    c: Vertical(g3)
    c: Distance(g1) = 11.35
FEATURE [PartDesign::Pad] Pad034
  AllowMultiFace = false
  BaseFeature = -> Pocket068
  Length = 4
  Length2 = 100
  Profile = -> Sketch166
  Type = 0
FEATURE [Sketcher::SketchObject] Sketch167
  ExternalGeometry = -> [Pad034]
  MapMode = 5
  Placement = pos=(0,0,0) rot=(1,0,0;3.14159rad)
  Support = -> [Pad034]
  sketch-geometry (4):
    g0: LineSegment StartX=-11.35 StartY=1.8 StartZ=0 EndX=-3.85 EndY=1.8 EndZ=0
    g1: LineSegment StartX=-3.85 StartY=1.8 StartZ=0 EndX=-3.85 EndY=-1.8 EndZ=0
    g2: LineSegment StartX=-3.85 StartY=-1.8 StartZ=0 EndX=-11.35 EndY=-1.8 EndZ=0
    g3: LineSegment StartX=-11.35 StartY=-1.8 StartZ=0 EndX=-11.35 EndY=1.8 EndZ=0
  constraints (10):
    c: Coincident(g0,g1)
    c: Coincident(g1,g2)
    c: Coincident(g2,g3)
    c: Coincident(g3,g0)
    c: Horizontal(g0)
    c: Horizontal(g2)
    c: Vertical(g1)
    c: Coincident(g0,g-3)
    c: Coincident(g2,g-3)
    c: Distance(g0) = 7.5
FEATURE [PartDesign::Pocket] Pocket072
  AllowMultiFace = false
  BaseFeature = -> Pad034
  Length = 1.2
  Length2 = 100
  Profile = -> Sketch167
  Type = 0
FEATURE [Sketcher::SketchObject] Sketch168
  ExternalGeometry = -> [Pocket072]
  MapMode = 5
  Placement = pos=(0,1.8,0) rot=(0,0.707107,0.707107;3.14159rad)
  Support = -> [Pocket072]
  sketch-geometry (3):
    g0: LineSegment StartX=11.35 StartY=4 StartZ=0 EndX=0 EndY=4 EndZ=0
    g1: LineSegment StartX=11.35 StartY=4 StartZ=0 EndX=0 EndY=10 EndZ=0
    g2: LineSegment StartX=0 StartY=10 StartZ=0 EndX=0 EndY=4 EndZ=0
  constraints (7):
    c: Coincident(g0,g-3)
    c: Coincident(g0,g-3)
    c: Coincident(g1,g0)
    c: Coincident(g2,g1)
    c: Coincident(g2,g0)
    c: Vertical(g2)
    c: Distance(g2) = 6
FEATURE [PartDesign::Pad] Pad035
  AllowMultiFace = false
  BaseFeature = -> Pocket072
  Length = 10
  Length2 = 100
  Profile = -> Sketch168
  Reversed = true
  Type = 3
  UpToFace = -> Pocket072 [Face7]
FEATURE [Sketcher::SketchObject] Sketch169
  ExternalGeometry = -> [Pad035]
  MapMode = 5
  Support = -> [XY_Plane045]
  sketch-geometry (1):
    g0: Circle CenterX=0 CenterY=0 CenterZ=0 NormalX=0 NormalY=0 NormalZ=1 AngleXU=0 Radius=1
  constraints (2):
    c: Coincident(g0,g-1)
    c: Equal(g-3,g0)
FEATURE [PartDesign::Pocket] Pocket073
  AllowMultiFace = false
  BaseFeature = -> Pad035
  Length = 5
  Length2 = 100
  Profile = -> Sketch169
  Reversed = true
  Type = 1
FEATURE [PartDesign::Body] Body040
  Group = -> [Sketch150,Pad079,Sketch148,Pad080,Sketch152,Sketch153,Pad082,Pad081,Sketch158,Pocket067,Sketch154,Pad076,Sketch156,Pad031,Sketch160,Pad084,Sketch162,Pocket068,Sketch166,Pad034,Sketch167,Pocket072,Sketch168,Pad035,Sketch169,Pocket073]
  Origin = -> Origin045
  Placement = pos=(15.2,35.2,0) rot=(0,0,1;0rad)
  Tip = -> Pocket073
  expr: .Placement.Base.y = 40 - 2.4 * 2
  expr: .Placement.Base.x = 20 - 2.4 * 2
FEATURE [App::Part] Part004
  Group = -> [Body041]
  Origin = -> Origin042
FEATURE [PartDesign::FeatureBase] Clone025
  BaseFeature = -> Body038
FEATURE [PartDesign::Body] Body046
  BaseFeature = -> Body038
  Group = -> [Clone025]
  Origin = -> Origin053
  Tip = -> Clone025
FEATURE [PartDesign::FeatureBase] Clone026
  BaseFeature = -> Body039
  Placement = pos=(15.2,0,0) rot=(0,0,1;0rad)
FEATURE [PartDesign::Body] Body047
  BaseFeature = -> Body039
  Group = -> [Clone026]
  Origin = -> Origin052
  Tip = -> Clone026
FEATURE [PartDesign::FeatureBase] Clone027
  BaseFeature = -> Body040
  Placement = pos=(15.2,35.2,0) rot=(0,0,1;0rad)
FEATURE [PartDesign::Body] Body048
  BaseFeature = -> Body040
  Group = -> [Clone027]
  Origin = -> Origin054
  Tip = -> Clone027
FEATURE [PartDesign::FeatureBase] Clone028
  BaseFeature = -> Body041
  Placement = pos=(0,35.2,0) rot=(0,0,1;0rad)
FEATURE [PartDesign::Body] Body049
  Group = -> [Clone028]
  Origin = -> Origin055
  Tip = -> Clone028
FEATURE [Part::Mirroring] Part__Mirroring002  label="Body046 (Mirror #3)"
  Base = (0,0,0)
  Normal = (1,0,0)
  Source = -> Body046
FEATURE [Part::Mirroring] Part__Mirroring003  label="Body047 (Mirror #4)"
  Base = (0,0,0)
  Normal = (1,0,0)
  Source = -> Body047
FEATURE [Part::Mirroring] Part__Mirroring004  label="Body048 (Mirror #5)"
  Base = (0,0,0)
  Normal = (1,0,0)
  Source = -> Body048
FEATURE [Part::Mirroring] Part__Mirroring005  label="Body049 (Mirror #6)"
  Base = (0,0,0)
  Normal = (1,0,0)
  Source = -> Body049
FEATURE [App::Part] Part006
  Group = -> [Body046,Body047,Body048,Body038,Part__Mirroring002,Body039,Part__Mirroring003,Body040,Body049,Part__Mirroring005,Part__Mirroring004]
  Origin = -> Origin056
  Placement = pos=(42.6,-27.5,-211.4) rot=(0,1,0;1.5708rad)
FEATURE [PartDesign::FeatureBase] Clone021
  BaseFeature = -> Body038
FEATURE [PartDesign::Body] Body042
  Group = -> [Clone021]
  Origin = -> Origin047
  Tip = -> Clone021
FEATURE [PartDesign::FeatureBase] Clone022
  BaseFeature = -> Body039
  Placement = pos=(15.2,0,0) rot=(0,0,1;0rad)
FEATURE [PartDesign::Body] Body043
  Group = -> [Clone022]
  Origin = -> Origin048
  Tip = -> Clone022
FEATURE [PartDesign::FeatureBase] Clone023
  BaseFeature = -> Body040
  Placement = pos=(15.2,35.2,0) rot=(0,0,1;0rad)
FEATURE [PartDesign::Body] Body044
  Group = -> [Clone023]
  Origin = -> Origin049
  Tip = -> Clone023
FEATURE [PartDesign::FeatureBase] Clone024
  BaseFeature = -> Body041
  Placement = pos=(0,35.2,0) rot=(0,0,1;0rad)
FEATURE [PartDesign::Body] Body045
  Group = -> [Clone024]
  Origin = -> Origin050
  Tip = -> Clone024
FEATURE [App::Part] Part005
  Group = -> [Body042,Body043,Body044,Body045]
  Origin = -> Origin051
  Placement = pos=(42.6,-172.4,-211.4) rot=(0.707107,0,0.707107;3.14159rad)
FEATURE [Sketcher::SketchObject] Sketch170
  MapMode = 5
  Support = -> [XY_Plane057]
  sketch-geometry (8):
    g0: LineSegment StartX=-5 StartY=5 StartZ=0 EndX=5 EndY=5 EndZ=0
    g1: LineSegment StartX=5 StartY=5 StartZ=0 EndX=5 EndY=-5 EndZ=0
    g2: LineSegment StartX=5 StartY=-5 StartZ=0 EndX=-5 EndY=-5 EndZ=0
    g3: LineSegment StartX=-5 StartY=-5 StartZ=0 EndX=-5 EndY=5 EndZ=0
    g4: LineSegment StartX=-4 StartY=4 StartZ=0 EndX=4 EndY=4 EndZ=0
    g5: LineSegment StartX=4 StartY=4 StartZ=0 EndX=4 EndY=-4 EndZ=0
    g6: LineSegment StartX=4 StartY=-4 StartZ=0 EndX=-4 EndY=-4 EndZ=0
    g7: LineSegment StartX=-4 StartY=-4 StartZ=0 EndX=-4 EndY=4 EndZ=0
  constraints (22):
    c: Coincident(g0,g1)
    c: Coincident(g1,g2)
    c: Coincident(g2,g3)
    c: Coincident(g3,g0)
    c: Horizontal(g0)
    c: Horizontal(g2)
    c: Vertical(g1)
    c: Vertical(g3)
    c: Symmetric(g0,g1,g-1)
    c: Equal(g0,g1)
    c: Distance(g0) = 10
    c: Coincident(g4,g5)
    c: Coincident(g5,g6)
    c: Coincident(g6,g7)
    c: Coincident(g7,g4)
    c: Horizontal(g4)
    c: Horizontal(g6)
    c: Vertical(g5)
    c: Vertical(g7)
    c: Symmetric(g4,g5,g-1)
    c: Equal(g4,g5)
    c: Distance(g4) = 8
FEATURE [PartDesign::Pad] Pad085
  Length = 56
  Length2 = 100
  Profile = -> Sketch170
  Refine = true
  Reversed = true
  Type = 0
FEATURE [PartDesign::Body] Body050
  Group = -> [Sketch170,Pad085]
  Origin = -> Origin057
  Placement = pos=(14,-200,-186.1) rot=(0,0,1;0rad)
  Tip = -> Pad085
FEATURE [PartDesign::FeatureBase] Clone030
  BaseFeature = -> Body015
  Placement = pos=(0,0,0) rot=(0,0.707107,0.707107;3.14159rad)
FEATURE [PartDesign::Body] Body052
  BaseFeature = -> Body015
  Group = -> [Clone030]
  Origin = -> Origin059
  Tip = -> Clone030
FEATURE [Part::Mirroring] Part__Mirroring006  label="Body022 (Mirror #2)001"
  Base = (0,0,0)
  Normal = (0,1,0)
  Placement = pos=(14,-200,-241.3) rot=(0.57735,0.57735,-0.57735;4.18879rad)
  Source = -> Body052
FEATURE [PartDesign::FeatureBase] Clone031
  BaseFeature = -> Body015
  Placement = pos=(0,0,0) rot=(1,0,0;1.5708rad)
FEATURE [PartDesign::Body] Body053
  BaseFeature = -> Body015
  Group = -> [Clone031]
  Origin = -> Origin060
  Placement = pos=(14,-200,-186.3) rot=(0.57735,-0.57735,-0.57735;2.0944rad)
  Tip = -> Clone031
FEATURE [Sketcher::SketchObject] Sketch172
  MapMode = 5
  Support = -> [XY_Plane061]
  expr: Constraints[2] = 2 / 2
  expr: Constraints[3] = 1 + 0.4 * 2
  sketch-geometry (2):
    g0: Circle CenterX=0 CenterY=0 CenterZ=0 NormalX=0 NormalY=0 NormalZ=1 AngleXU=0 Radius=1
    g1: Circle CenterX=0 CenterY=0 CenterZ=0 NormalX=0 NormalY=0 NormalZ=1 AngleXU=0 Radius=1.8
  constraints (4):
    c: Coincident(g0,g-1)
    c: Coincident(g1,g0)
    c: Radius(g0) = 1
    c: Radius(g1) = 1.8
FEATURE [PartDesign::Pad] Pad086
  AllowMultiFace = false
  Length = 18
  Length2 = 100
  Profile = -> Sketch172
  Type = 0
FEATURE [Sketcher::SketchObject] Sketch173
  ExternalGeometry = -> [Pad086]
  MapMode = 5
  Placement = pos=(0,0,18) rot=(0,0,1;0rad)
  Support = -> [Pad086]
  expr: Constraints[12] = 21 + 1.6 - (2 - 1.6) - 0.2
  expr: Constraints[15] = 20 - 2.4 * 2 - 2 - 0.2
  sketch-geometry (6):
    g0: LineSegment StartX=-10.8 StartY=1.8 StartZ=0 EndX=11.2 EndY=1.8 EndZ=0
    g1: LineSegment StartX=11.2 StartY=1.8 StartZ=0 EndX=11.2 EndY=-1.8 EndZ=0
    g2: LineSegment StartX=11.2 StartY=-1.8 StartZ=0 EndX=-10.8 EndY=-1.8 EndZ=0
    g3: LineSegment StartX=-10.8 StartY=-1.8 StartZ=0 EndX=-10.8 EndY=1.8 EndZ=0
    g4: Circle CenterX=0 CenterY=0 CenterZ=0 NormalX=0 NormalY=0 NormalZ=1 AngleXU=0 Radius=1
    g5: GeomPoint X=-1.8 Y=0 Z=0
  constraints (16):
    c: Coincident(g0,g1)
    c: Coincident(g1,g2)
    c: Coincident(g2,g3)
    c: Coincident(g3,g0)
    c: Horizontal(g0)
    c: Horizontal(g2)
    c: Vertical(g1)
    c: Vertical(g3)
    c: Tangent(g0,g-3)
    c: Tangent(g-3,g2)
    c: Coincident(g4,g-1)
    c: Equal(g-4,g4)
    c: Distance(g0) = 22
    c: PointOnObject(g5,g-3)
    c: PointOnObject(g5,g-1)
    c: DistanceX(g5,g0) = 13
FEATURE [PartDesign::Pad] Pad087
  AllowMultiFace = false
  BaseFeature = -> Pad086
  Length = 2
  Length2 = 100
  Profile = -> Sketch173
  Type = 0
FEATURE [Sketcher::SketchObject] Sketch174
  MapMode = 5
  Support = -> [XY_Plane062]
  expr: Constraints[2] = 2 / 2
  expr: Constraints[3] = 1 + 0.4 * 2
  sketch-geometry (2):
    g0: Circle CenterX=0 CenterY=0 CenterZ=0 NormalX=0 NormalY=0 NormalZ=1 AngleXU=0 Radius=1
    g1: Circle CenterX=0 CenterY=0 CenterZ=0 NormalX=0 NormalY=0 NormalZ=1 AngleXU=0 Radius=1.8
  constraints (4):
    c: Coincident(g0,g-1)
    c: Coincident(g1,g0)
    c: Radius(g0) = 1
    c: Radius(g1) = 1.8
FEATURE [PartDesign::Pad] Pad088
  AllowMultiFace = false
  Length = 18
  Length2 = 100
  Profile = -> Sketch174
  Type = 0
FEATURE [Sketcher::SketchObject] Sketch175
  ExternalGeometry = -> [Pad088]
  MapMode = 5
  Placement = pos=(0,0,18) rot=(0,0,1;0rad)
  Support = -> [Pad088]
  sketch-geometry (6):
    g0: LineSegment StartX=-3.8 StartY=1.8 StartZ=0 EndX=4e-16 EndY=1.8 EndZ=0
    g1: LineSegment StartX=-3e-16 StartY=-1.8 StartZ=0 EndX=-3.8 EndY=-1.8 EndZ=0
    g2: LineSegment StartX=-3.8 StartY=-1.8 StartZ=0 EndX=-3.8 EndY=1.8 EndZ=0
    g3: ArcOfCircle CenterX=0 CenterY=0 CenterZ=0 NormalX=0 NormalY=0 NormalZ=1 AngleXU=0 Radius=1.8 StartAngle=4.71239 EndAngle=7.85398
    g4: Circle CenterX=0 CenterY=0 CenterZ=0 NormalX=0 NormalY=0 NormalZ=1 AngleXU=0 Radius=1
    g5: GeomPoint X=-1.8 Y=0 Z=0
  constraints (16):
    c: Coincident(g1,g2)
    c: Coincident(g2,g0)
    c: Horizontal(g0)
    c: Horizontal(g1)
    c: Vertical(g2)
    c: Coincident(g3,g-1)
    c: PointOnObject(g3,g-4)
    c: PointOnObject(g3,g-2)
    c: PointOnObject(g3,g-2)
    c: Coincident(g0,g3)
    c: Coincident(g1,g3)
    c: Coincident(g4,g3)
    c: Equal(g-3,g4)
    c: PointOnObject(g5,g-4)
    c: PointOnObject(g5,g-1)
    c: DistanceX(g0,g5) = 2
FEATURE [PartDesign::Pad] Pad089
  AllowMultiFace = false
  BaseFeature = -> Pad088
  Length = 4
  Length2 = 100
  Profile = -> Sketch175
  Type = 0
FEATURE [Sketcher::SketchObject] Sketch176
  ExternalGeometry = -> [Pad087]
  MapMode = 5
  Placement = pos=(0,-3,0) rot=(1,0,0;1.5708rad)
  sketch-geometry (3):
    g0: LineSegment StartX=11.2 StartY=20 StartZ=0 EndX=11.2 EndY=18 EndZ=0
    g1: LineSegment StartX=11.2 StartY=20 StartZ=0 EndX=8.2 EndY=18 EndZ=0
    g2: LineSegment StartX=11.2 StartY=18 StartZ=0 EndX=8.2 EndY=18 EndZ=0
  constraints (7):
    c: Coincident(g1,g0)
    c: Coincident(g2,g0)
    c: Coincident(g2,g1)
    c: Horizontal(g2)
    c: Distance(g2) = 3
    c: Coincident(g0,g-3)
    c: Coincident(g0,g-3)
FEATURE [Sketcher::SketchObject] Sketch178
  ExternalGeometry = -> [Pad089]
  MapMode = 5
  Placement = pos=(0,-1.8,0) rot=(1,0,0;1.5708rad)
  Support = -> [Pad089]
  sketch-geometry (3):
    g0: LineSegment StartX=-3.8 StartY=20 StartZ=0 EndX=-3.8 EndY=18 EndZ=0
    g1: LineSegment StartX=-3.8 StartY=20 StartZ=0 EndX=-6.8 EndY=18 EndZ=0
    g2: LineSegment StartX=-3.8 StartY=18 StartZ=0 EndX=-6.8 EndY=18 EndZ=0
  constraints (8):
    c: Coincident(g2,g1)
    c: Coincident(g2,g0)
    c: Horizontal(g2)
    c: Distance(g2) = 3
    c: Coincident(g-3,g0)
    c: Coincident(g1,g0)
    c: PointOnObject(g0,g-3)
    c: Distance(g0) = 2
FEATURE [PartDesign::Pocket] Pocket074
  AllowMultiFace = false
  BaseFeature = -> Pad087
  Length = 5
  Length2 = 100
  Profile = -> Sketch176
  Type = 1
FEATURE [Sketcher::SketchObject] Sketch177
  ExternalGeometry = -> [Pocket074]
  MapMode = 5
  Placement = pos=(0,0,20) rot=(0,0,1;0rad)
  Support = -> [Pocket074]
  sketch-geometry (5):
    g0: LineSegment StartX=11.19 StartY=-2e-16 StartZ=0 EndX=8.2 EndY=-1.8 EndZ=0
    g1: LineSegment StartX=8.2 StartY=1.8 StartZ=0 EndX=11.19 EndY=-2e-16 EndZ=0
    g2: LineSegment StartX=8.2 StartY=-1.8 StartZ=0 EndX=11.2 EndY=-1.8 EndZ=0
    g3: LineSegment StartX=8.2 StartY=1.8 StartZ=0 EndX=11.2 EndY=1.8 EndZ=0
    g4: LineSegment StartX=11.2 StartY=-1.8 StartZ=0 EndX=11.2 EndY=1.8 EndZ=0
  constraints (13):
    c: Coincident(g1,g0)
    c: Coincident(g2,g0)
    c: Horizontal(g2)
    c: Horizontal(g3)
    c: Distance(g2) = 3
    c: Equal(g2,g3)
    c: Coincident(g1,g3)
    c: Coincident(g2,g4)
    c: Coincident(g4,g3)
    c: PointOnObject(g0,g-1)
    c: DistanceX(g0,g3) = 0.01
    c: Coincident(g3,g-3)
    c: Coincident(g2,g-3)
FEATURE [PartDesign::Pocket] Pocket075
  AllowMultiFace = false
  BaseFeature = -> Pocket074
  Length = 5
  Length2 = 100
  Profile = -> Sketch177
  Type = 1
FEATURE [PartDesign::Pad] Pad090
  AllowMultiFace = false
  BaseFeature = -> Pad089
  Length = 10
  Length2 = 100
  Profile = -> Sketch178
  Reversed = true
  Type = 3
  UpToFace = -> Pad089 [Face7]
FEATURE [Sketcher::SketchObject] Sketch179
  ExternalGeometry = -> [Pad089]
  MapMode = 5
  Placement = pos=(0,0,22) rot=(0,0,1;0rad)
  Support = -> [Pad090]
  sketch-geometry (5):
    g0: LineSegment StartX=-3.8 StartY=1.8 StartZ=0 EndX=-6.8 EndY=1.8 EndZ=0
    g1: LineSegment StartX=-3.8 StartY=-1.8 StartZ=0 EndX=-3.8 EndY=1.8 EndZ=0
    g2: LineSegment StartX=-6.8 StartY=1.8 StartZ=0 EndX=-3.81 EndY=0 EndZ=0
    g3: LineSegment StartX=-3.81 StartY=0 StartZ=0 EndX=-6.8 EndY=-1.8 EndZ=0
    g4: LineSegment StartX=-6.8 StartY=-1.8 StartZ=0 EndX=-3.8 EndY=-1.8 EndZ=0
  constraints (13):
    c: Horizontal(g4)
    c: Horizontal(g0)
    c: Equal(g0,g4)
    c: Distance(g0) = 3
    c: Coincident(g1,g-3)
    c: Coincident(g1,g-3)
    c: Coincident(g2,g3)
    c: PointOnObject(g2,g-1)
    c: Coincident(g2,g0)
    c: Coincident(g0,g1)
    c: Coincident(g3,g4)
    c: Coincident(g1,g4)
    c: DistanceX(g2,g1) = 0.01
FEATURE [PartDesign::Pad] Pad091
  AllowMultiFace = false
  BaseFeature = -> Pad090
  Length = 10
  Length2 = 100
  Profile = -> Sketch179
  Reversed = true
  Type = 3
  UpToFace = -> Pad090 [Face4]
FEATURE [Sketcher::SketchObject] Sketch180
  ExternalGeometry = -> [Pocket075]
  MapMode = 5
  Placement = pos=(0,0,20) rot=(0,0,1;0rad)
  sketch-geometry (9):
    g0: LineSegment StartX=-10.8 StartY=1.8 StartZ=0 EndX=-10.8 EndY=-1.8 EndZ=0
    g1: LineSegment StartX=8.2 StartY=1.8 StartZ=0 EndX=11.19 EndY=-7e-16 EndZ=0
    g2: LineSegment StartX=11.19 StartY=-7e-16 StartZ=0 EndX=8.2 EndY=-1.8 EndZ=0
    g3: ArcOfCircle CenterX=0 CenterY=0 CenterZ=0 NormalX=0 NormalY=0 NormalZ=1 AngleXU=0 Radius=1.86815 StartAngle=1.84174 EndAngle=4.44144
    g4: ArcOfCircle CenterX=0 CenterY=0 CenterZ=0 NormalX=0 NormalY=0 NormalZ=1 AngleXU=0 Radius=1.86815 StartAngle=4.98334 EndAngle=7.58303
    g5: LineSegment StartX=-10.8 StartY=-1.8 StartZ=0 EndX=-0.5 EndY=-1.8 EndZ=0
    g6: LineSegment StartX=0.5 StartY=-1.8 StartZ=0 EndX=8.2 EndY=-1.8 EndZ=0
    g7: LineSegment StartX=8.2 StartY=1.8 StartZ=0 EndX=0.5 EndY=1.8 EndZ=0
    g8: LineSegment StartX=-0.5 StartY=1.8 StartZ=0 EndX=-10.8 EndY=1.8 EndZ=0
  constraints (22):
    c: Coincident(g2,g1)
    c: Coincident(g0,g-3)
    c: Coincident(g0,g-5)
    c: Coincident(g2,g-5)
    c: Coincident(g-4,g1)
    c: Coincident(g1,g-4)
    c: Coincident(g3,g-1)
    c: Coincident(g4,g3)
    c: Equal(g4,g3)
    c: Coincident(g5,g0)
    c: Coincident(g5,g3)
    c: Coincident(g6,g4)
    c: Coincident(g6,g2)
    c: Coincident(g7,g1)
    c: Coincident(g7,g4)
    c: Coincident(g8,g3)
    c: Coincident(g8,g0)
    c: Horizontal(g7)
    c: Horizontal(g8)
    c: Horizontal(g5)
    c: Horizontal(g6)
    c: DistanceX(g3,g4) = 1
FEATURE [PartDesign::Pad] Pad092
  AllowMultiFace = false
  BaseFeature = -> Pocket075
  Length = 2
  Length2 = 100
  Profile = -> Sketch180
  Type = 0
FEATURE [Sketcher::SketchObject] Sketch181
  ExternalGeometry = -> [Pad092]
  MapMode = 5
  Placement = pos=(0,0,22) rot=(0,0,1;0rad)
  Support = -> [Pad092]
  sketch-geometry (4):
    g0: LineSegment StartX=-10.8 StartY=1.8 StartZ=0 EndX=-9.2 EndY=1.8 EndZ=0
    g1: LineSegment StartX=-9.2 StartY=1.8 StartZ=0 EndX=-9.2 EndY=-1.8 EndZ=0
    g2: LineSegment StartX=-9.2 StartY=-1.8 StartZ=0 EndX=-10.8 EndY=-1.8 EndZ=0
    g3: LineSegment StartX=-10.8 StartY=-1.8 StartZ=0 EndX=-10.8 EndY=1.8 EndZ=0
  constraints (10):
    c: Coincident(g0,g1)
    c: Coincident(g1,g2)
    c: Coincident(g2,g3)
    c: Coincident(g3,g0)
    c: Horizontal(g0)
    c: Horizontal(g2)
    c: Vertical(g1)
    c: Coincident(g0,g-3)
    c: Coincident(g2,g-3)
    c: Distance(g0) = 1.6
FEATURE [PartDesign::Pad] Pad093
  AllowMultiFace = false
  BaseFeature = -> Pad092
  Length = 11
  Length2 = 100
  Profile = -> Sketch181
  Type = 0
  expr: Length = 9 + 2
FEATURE [Sketcher::SketchObject] Sketch182
  ExternalGeometry = -> [Pad093]
  MapMode = 5
  Placement = pos=(0,0,22) rot=(0,0,1;0rad)
  Support = -> [Pad093]
  sketch-geometry (9):
    g0: LineSegment StartX=-9.2 StartY=-1.8 StartZ=0 EndX=-0.5 EndY=-1.8 EndZ=0
    g1: LineSegment StartX=-1.85742 StartY=-0.2 StartZ=0 EndX=-9.2 EndY=-0.2 EndZ=0
    g2: LineSegment StartX=-9.2 StartY=-0.2 StartZ=0 EndX=-9.2 EndY=-1.8 EndZ=0
    g3: ArcOfCircle CenterX=0 CenterY=0 CenterZ=0 NormalX=0 NormalY=0 NormalZ=1 AngleXU=0 Radius=1.86815 StartAngle=3.24886 EndAngle=4.44144
    g4: ArcOfCircle CenterX=0 CenterY=0 CenterZ=0 NormalX=0 NormalY=0 NormalZ=1 AngleXU=0 Radius=1.86815 StartAngle=4.98334 EndAngle=6.17592
    g5: LineSegment StartX=1.85742 StartY=-0.2 StartZ=0 EndX=10.8578 EndY=-0.2 EndZ=0
    g6: LineSegment StartX=0.5 StartY=-1.8 StartZ=0 EndX=8.2 EndY=-1.8 EndZ=0
    g7: LineSegment StartX=8.2 StartY=-1.8 StartZ=0 EndX=10.8578 EndY=-0.2 EndZ=0
    g8: LineSegment [constr] StartX=1.85742 StartY=-0.2 StartZ=0 EndX=-1.85742 EndY=-0.2 EndZ=0
  constraints (22):
    c: Coincident(g1,g2)
    c: Coincident(g2,g0)
    c: Horizontal(g1)
    c: Vertical(g2)
    c: Coincident(g0,g-3)
    c: Coincident(g0,g-4)
    c: Coincident(g3,g-1)
    c: Coincident(g3,g1)
    c: Coincident(g3,g0)
    c: Distance(g2) = 1.6
    c: Coincident(g4,g3)
    c: Coincident(g4,g-5)
    c: Coincident(g5,g4)
    c: PointOnObject(g5,g-6)
    c: Horizontal(g5)
    c: Coincident(g6,g4)
    c: Coincident(g6,g-6)
    c: Coincident(g7,g6)
    c: Coincident(g7,g5)
    c: Coincident(g8,g4)
    c: Coincident(g8,g1)
    c: Horizontal(g8)
FEATURE [PartDesign::Pad] Pad094
  AllowMultiFace = false
  BaseFeature = -> Pad093
  Length = 2
  Length2 = 100
  Profile = -> Sketch182
  Type = 0
FEATURE [Sketcher::SketchObject] Sketch183
  ExternalGeometry = -> [Pad094]
  MapMode = 5
  Placement = pos=(0,0,33) rot=(0,0,1;0rad)
  Support = -> [Pad094]
  sketch-geometry (4):
    g0: LineSegment StartX=-10.8 StartY=1.8 StartZ=0 EndX=-5.2 EndY=1.8 EndZ=0
    g1: LineSegment StartX=-5.2 StartY=1.8 StartZ=0 EndX=-5.2 EndY=-1.8 EndZ=0
    g2: LineSegment StartX=-5.2 StartY=-1.8 StartZ=0 EndX=-10.8 EndY=-1.8 EndZ=0
    g3: LineSegment StartX=-10.8 StartY=-1.8 StartZ=0 EndX=-10.8 EndY=1.8 EndZ=0
  constraints (10):
    c: Coincident(g0,g1)
    c: Coincident(g1,g2)
    c: Coincident(g2,g3)
    c: Coincident(g3,g0)
    c: Horizontal(g0)
    c: Horizontal(g2)
    c: Vertical(g1)
    c: Coincident(g-3,g2)
    c: Coincident(g0,g-3)
    c: DistanceX(g-4,g0) = 4
FEATURE [PartDesign::Pad] Pad095
  AllowMultiFace = false
  BaseFeature = -> Pad094
  Length = 1.6
  Length2 = 100
  Profile = -> Sketch183
  Type = 0
FEATURE [Sketcher::SketchObject] Sketch184
  ExternalGeometry = -> [Pad091]
  MapMode = 5
  Placement = pos=(0,0,22) rot=(0,0,1;0rad)
  Support = -> [Pad091]
  sketch-geometry (6):
    g0: ArcOfCircle CenterX=0 CenterY=0 CenterZ=0 NormalX=0 NormalY=0 NormalZ=1 AngleXU=0 Radius=1.8 StartAngle=4.71239 EndAngle=7.85398
    g1: LineSegment StartX=6e-16 StartY=1.8 StartZ=0 EndX=-1.69706 EndY=1.8 EndZ=0
    g2: LineSegment StartX=-3e-16 StartY=-1.8 StartZ=0 EndX=-1.69706 EndY=-1.8 EndZ=0
    g3: ArcOfCircle CenterX=0 CenterY=0 CenterZ=0 NormalX=0 NormalY=0 NormalZ=1 AngleXU=0 Radius=1.8 StartAngle=2.45182 EndAngle=3.83137
    g4: ArcOfCircle CenterX=-1.69706 CenterY=1.4 CenterZ=0 NormalX=0 NormalY=0 NormalZ=1 AngleXU=0 Radius=0.4 StartAngle=5.59341 EndAngle=7.85398
    g5: ArcOfCircle CenterX=-1.69706 CenterY=-1.4 CenterZ=0 NormalX=0 NormalY=0 NormalZ=1 AngleXU=0 Radius=0.4 StartAngle=4.71239 EndAngle=6.97296
  constraints (16):
    c: Coincident(g0,g-1)
    c: Coincident(g0,g-3)
    c: Coincident(g0,g-3)
    c: Coincident(g1,g0)
    c: Horizontal(g1)
    c: Coincident(g2,g0)
    c: Horizontal(g2)
    c: Equal(g1,g2)
    c: Coincident(g3,g0)
    c: Equal(g4,g5)
    c: Tangent(g4,g3) = 1.5708
    c: Tangent(g5,g3) = 1.5708
    c: Tangent(g5,g2) = 1.5708
    c: Tangent(g4,g1) = -1.5708
    c: Radius(g4) = 0.4
    c: Equal(g3,g0)
FEATURE [PartDesign::Pocket] Pocket076
  AllowMultiFace = false
  BaseFeature = -> Pad091
  Length = 2
  Length2 = 100
  Profile = -> Sketch184
  Type = 0
FEATURE [Sketcher::SketchObject] Sketch185
  ExternalGeometry = -> [Pocket076]
  MapMode = 5
  Placement = pos=(0,0,22) rot=(0,0,1;0rad)
  Support = -> [Pocket076]
  sketch-geometry (4):
    g0: LineSegment StartX=-1.8 StartY=1.8 StartZ=0 EndX=-3.4 EndY=1.8 EndZ=0
    g1: LineSegment StartX=-3.4 StartY=1.8 StartZ=0 EndX=-3.4 EndY=-1.8 EndZ=0
    g2: LineSegment StartX=-3.4 StartY=-1.8 StartZ=0 EndX=-1.8 EndY=-1.8 EndZ=0
    g3: LineSegment StartX=-1.8 StartY=-1.8 StartZ=0 EndX=-1.8 EndY=1.8 EndZ=0
  constraints (12):
    c: Coincident(g0,g1)
    c: Coincident(g1,g2)
    c: Coincident(g2,g3)
    c: Coincident(g3,g0)
    c: Horizontal(g0)
    c: Horizontal(g2)
    c: Vertical(g1)
    c: Vertical(g3)
    c: Distance(g0) = 1.6
    c: Tangent(g3,g-3)
    c: PointOnObject(g0,g-4)
    c: PointOnObject(g1,g-5)
FEATURE [PartDesign::Pad] Pad096
  AllowMultiFace = false
  BaseFeature = -> Pocket076
  Length = 11
  Length2 = 100
  Profile = -> Sketch185
  Type = 0
  expr: Length = 9 + 2
FEATURE [Sketcher::SketchObject] Sketch186
  ExternalGeometry = -> [Pad096]
  MapMode = 5
  Placement = pos=(0,0,22) rot=(0,0,1;0rad)
  Support = -> [Pad096]
  sketch-geometry (4):
    g0: LineSegment StartX=-4.14222 StartY=-0.2 StartZ=0 EndX=-3.4 EndY=-0.2 EndZ=0
    g1: LineSegment StartX=-6.8 StartY=-1.8 StartZ=0 EndX=-4.14222 EndY=-0.2 EndZ=0
    g2: LineSegment StartX=-6.8 StartY=-1.8 StartZ=0 EndX=-3.4 EndY=-1.8 EndZ=0
    g3: LineSegment StartX=-3.4 StartY=-1.8 StartZ=0 EndX=-3.4 EndY=-0.2 EndZ=0
  constraints (10):
    c: Coincident(g1,g0)
    c: Coincident(g2,g1)
    c: Coincident(g3,g2)
    c: Coincident(g3,g0)
    c: Distance(g3) = 1.6
    c: Coincident(g1,g-3)
    c: PointOnObject(g0,g-3)
    c: Horizontal(g0)
    c: PointOnObject(g0,g-4)
    c: Coincident(g2,g-4)
FEATURE [PartDesign::Pad] Pad097
  AllowMultiFace = false
  BaseFeature = -> Pad096
  Length = 2
  Length2 = 100
  Profile = -> Sketch186
  Type = 0
FEATURE [Sketcher::SketchObject] Sketch187
  ExternalGeometry = -> [Pad097]
  MapMode = 5
  Placement = pos=(0,0,33) rot=(0,0,1;0rad)
  Support = -> [Pad097]
  sketch-geometry (4):
    g0: LineSegment StartX=-1.8 StartY=1.8 StartZ=0 EndX=-7.4 EndY=1.8 EndZ=0
    g1: LineSegment StartX=-7.4 StartY=1.8 StartZ=0 EndX=-7.4 EndY=-1.8 EndZ=0
    g2: LineSegment StartX=-7.4 StartY=-1.8 StartZ=0 EndX=-1.8 EndY=-1.8 EndZ=0
    g3: LineSegment StartX=-1.8 StartY=-1.8 StartZ=0 EndX=-1.8 EndY=1.8 EndZ=0
  constraints (10):
    c: Coincident(g0,g1)
    c: Coincident(g1,g2)
    c: Coincident(g2,g3)
    c: Coincident(g3,g0)
    c: Horizontal(g0)
    c: Horizontal(g2)
    c: Vertical(g1)
    c: Coincident(g0,g-3)
    c: Coincident(g2,g-3)
    c: DistanceX(g0,g-4) = 4
FEATURE [PartDesign::Pad] Pad098
  AllowMultiFace = false
  BaseFeature = -> Pad097
  Length = 1.6
  Length2 = 100
  Profile = -> Sketch187
  Type = 0
FEATURE [Sketcher::SketchObject] Sketch191
  MapMode = 5
  Support = -> [XY_Plane063]
  expr: Constraints[2] = 2 / 2
  expr: Constraints[3] = 1 + 0.4 * 2
  sketch-geometry (2):
    g0: Circle CenterX=0 CenterY=0 CenterZ=0 NormalX=0 NormalY=0 NormalZ=1 AngleXU=0 Radius=1
    g1: Circle CenterX=0 CenterY=0 CenterZ=0 NormalX=0 NormalY=0 NormalZ=1 AngleXU=0 Radius=1.8
  constraints (4):
    c: Coincident(g0,g-1)
    c: Coincident(g1,g0)
    c: Radius(g0) = 1
    c: Radius(g1) = 1.8
FEATURE [PartDesign::Pad] Pad101
  AllowMultiFace = false
  Length = 18
  Length2 = 100
  Profile = -> Sketch191
  Type = 0
FEATURE [Sketcher::SketchObject] Sketch189
  ExternalGeometry = -> [Pad101]
  MapMode = 5
  Placement = pos=(0,0,18) rot=(0,0,1;0rad)
  Support = -> [Pad101]
  expr: Constraints[12] = 21 + 1.6 - (2 - 1.6) - 0.2
  expr: Constraints[15] = 20 - 2.4 * 2 - 2 - 0.2
  sketch-geometry (6):
    g0: LineSegment StartX=-10.8 StartY=1.8 StartZ=0 EndX=11.2 EndY=1.8 EndZ=0
    g1: LineSegment StartX=11.2 StartY=1.8 StartZ=0 EndX=11.2 EndY=-1.8 EndZ=0
    g2: LineSegment StartX=11.2 StartY=-1.8 StartZ=0 EndX=-10.8 EndY=-1.8 EndZ=0
    g3: LineSegment StartX=-10.8 StartY=-1.8 StartZ=0 EndX=-10.8 EndY=1.8 EndZ=0
    g4: Circle CenterX=0 CenterY=0 CenterZ=0 NormalX=0 NormalY=0 NormalZ=1 AngleXU=0 Radius=1
    g5: GeomPoint X=-1.8 Y=0 Z=0
  constraints (16):
    c: Coincident(g0,g1)
    c: Coincident(g1,g2)
    c: Coincident(g2,g3)
    c: Coincident(g3,g0)
    c: Horizontal(g0)
    c: Horizontal(g2)
    c: Vertical(g1)
    c: Vertical(g3)
    c: Tangent(g0,g-3)
    c: Tangent(g-3,g2)
    c: Coincident(g4,g-1)
    c: Equal(g-4,g4)
    c: Distance(g0) = 22
    c: PointOnObject(g5,g-3)
    c: PointOnObject(g5,g-1)
    c: DistanceX(g5,g0) = 13
FEATURE [PartDesign::Pad] Pad100
  AllowMultiFace = false
  BaseFeature = -> Pad101
  Length = 2
  Length2 = 100
  Profile = -> Sketch189
  Type = 0
FEATURE [Sketcher::SketchObject] Sketch188
  ExternalGeometry = -> [Pad100]
  MapMode = 5
  Placement = pos=(0,-3,0) rot=(1,0,0;1.5708rad)
  sketch-geometry (3):
    g0: LineSegment StartX=11.2 StartY=20 StartZ=0 EndX=11.2 EndY=18 EndZ=0
    g1: LineSegment StartX=11.2 StartY=20 StartZ=0 EndX=8.2 EndY=18 EndZ=0
    g2: LineSegment StartX=11.2 StartY=18 StartZ=0 EndX=8.2 EndY=18 EndZ=0
  constraints (7):
    c: Coincident(g1,g0)
    c: Coincident(g2,g0)
    c: Coincident(g2,g1)
    c: Horizontal(g2)
    c: Distance(g2) = 3
    c: Coincident(g0,g-3)
    c: Coincident(g0,g-3)
FEATURE [Sketcher::SketchObject] Sketch192
  MapMode = 5
  Support = -> [XY_Plane064]
  expr: Constraints[2] = 2 / 2
  expr: Constraints[3] = 1 + 0.4 * 2
  sketch-geometry (2):
    g0: Circle CenterX=0 CenterY=0 CenterZ=0 NormalX=0 NormalY=0 NormalZ=1 AngleXU=0 Radius=1
    g1: Circle CenterX=0 CenterY=0 CenterZ=0 NormalX=0 NormalY=0 NormalZ=1 AngleXU=0 Radius=1.8
  constraints (4):
    c: Coincident(g0,g-1)
    c: Coincident(g1,g0)
    c: Radius(g0) = 1
    c: Radius(g1) = 1.8
FEATURE [PartDesign::Pad] Pad102
  AllowMultiFace = false
  Length = 18
  Length2 = 100
  Profile = -> Sketch192
  Type = 0
FEATURE [Sketcher::SketchObject] Sketch190
  ExternalGeometry = -> [Pad102]
  MapMode = 5
  Placement = pos=(0,0,18) rot=(0,0,1;0rad)
  Support = -> [Pad102]
  sketch-geometry (6):
    g0: LineSegment StartX=-3.8 StartY=1.8 StartZ=0 EndX=4e-16 EndY=1.8 EndZ=0
    g1: LineSegment StartX=-3e-16 StartY=-1.8 StartZ=0 EndX=-3.8 EndY=-1.8 EndZ=0
    g2: LineSegment StartX=-3.8 StartY=-1.8 StartZ=0 EndX=-3.8 EndY=1.8 EndZ=0
    g3: ArcOfCircle CenterX=0 CenterY=0 CenterZ=0 NormalX=0 NormalY=0 NormalZ=1 AngleXU=0 Radius=1.8 StartAngle=4.71239 EndAngle=7.85398
    g4: Circle CenterX=0 CenterY=0 CenterZ=0 NormalX=0 NormalY=0 NormalZ=1 AngleXU=0 Radius=1
    g5: GeomPoint X=-1.8 Y=0 Z=0
  constraints (16):
    c: Coincident(g1,g2)
    c: Coincident(g2,g0)
    c: Horizontal(g0)
    c: Horizontal(g1)
    c: Vertical(g2)
    c: Coincident(g3,g-1)
    c: PointOnObject(g3,g-4)
    c: PointOnObject(g3,g-2)
    c: PointOnObject(g3,g-2)
    c: Coincident(g0,g3)
    c: Coincident(g1,g3)
    c: Coincident(g4,g3)
    c: Equal(g-3,g4)
    c: PointOnObject(g5,g-4)
    c: PointOnObject(g5,g-1)
    c: DistanceX(g0,g5) = 2
FEATURE [PartDesign::Pad] Pad103
  AllowMultiFace = false
  BaseFeature = -> Pad102
  Length = 4
  Length2 = 100
  Profile = -> Sketch190
  Type = 0
FEATURE [PartDesign::Pocket] Pocket078
  AllowMultiFace = false
  BaseFeature = -> Pad100
  Length = 5
  Length2 = 100
  Profile = -> Sketch188
  Type = 1
FEATURE [Sketcher::SketchObject] Sketch193
  ExternalGeometry = -> [Pocket078]
  MapMode = 5
  Placement = pos=(0,0,20) rot=(0,0,1;0rad)
  Support = -> [Pocket078]
  sketch-geometry (5):
    g0: LineSegment StartX=11.19 StartY=-2e-16 StartZ=0 EndX=8.2 EndY=-1.8 EndZ=0
    g1: LineSegment StartX=8.2 StartY=1.8 StartZ=0 EndX=11.19 EndY=-2e-16 EndZ=0
    g2: LineSegment StartX=8.2 StartY=-1.8 StartZ=0 EndX=11.2 EndY=-1.8 EndZ=0
    g3: LineSegment StartX=8.2 StartY=1.8 StartZ=0 EndX=11.2 EndY=1.8 EndZ=0
    g4: LineSegment StartX=11.2 StartY=-1.8 StartZ=0 EndX=11.2 EndY=1.8 EndZ=0
  constraints (13):
    c: Coincident(g1,g0)
    c: Coincident(g2,g0)
    c: Horizontal(g2)
    c: Horizontal(g3)
    c: Distance(g2) = 3
    c: Equal(g2,g3)
    c: Coincident(g1,g3)
    c: Coincident(g2,g4)
    c: Coincident(g4,g3)
    c: PointOnObject(g0,g-1)
    c: DistanceX(g0,g3) = 0.01
    c: Coincident(g3,g-3)
    c: Coincident(g2,g-3)
FEATURE [PartDesign::Pocket] Pocket077
  AllowMultiFace = false
  BaseFeature = -> Pocket078
  Length = 5
  Length2 = 100
  Profile = -> Sketch193
  Type = 1
FEATURE [Sketcher::SketchObject] Sketch194
  ExternalGeometry = -> [Pad103]
  MapMode = 5
  Placement = pos=(0,-1.8,0) rot=(1,0,0;1.5708rad)
  Support = -> [Pad103]
  sketch-geometry (3):
    g0: LineSegment StartX=-3.8 StartY=20 StartZ=0 EndX=-3.8 EndY=18 EndZ=0
    g1: LineSegment StartX=-3.8 StartY=20 StartZ=0 EndX=-6.8 EndY=18 EndZ=0
    g2: LineSegment StartX=-3.8 StartY=18 StartZ=0 EndX=-6.8 EndY=18 EndZ=0
  constraints (8):
    c: Coincident(g2,g1)
    c: Coincident(g2,g0)
    c: Horizontal(g2)
    c: Distance(g2) = 3
    c: Coincident(g-3,g0)
    c: Coincident(g1,g0)
    c: PointOnObject(g0,g-3)
    c: Distance(g0) = 2
FEATURE [PartDesign::Pad] Pad105
  AllowMultiFace = false
  BaseFeature = -> Pad103
  Length = 10
  Length2 = 100
  Profile = -> Sketch194
  Reversed = true
  Type = 3
  UpToFace = -> Pad103 [Face7]
FEATURE [Sketcher::SketchObject] Sketch195
  ExternalGeometry = -> [Pad103]
  MapMode = 5
  Placement = pos=(0,0,22) rot=(0,0,1;0rad)
  Support = -> [Pad105]
  sketch-geometry (5):
    g0: LineSegment StartX=-3.8 StartY=1.8 StartZ=0 EndX=-6.8 EndY=1.8 EndZ=0
    g1: LineSegment StartX=-3.8 StartY=-1.8 StartZ=0 EndX=-3.8 EndY=1.8 EndZ=0
    g2: LineSegment StartX=-6.8 StartY=1.8 StartZ=0 EndX=-3.81 EndY=0 EndZ=0
    g3: LineSegment StartX=-3.81 StartY=0 StartZ=0 EndX=-6.8 EndY=-1.8 EndZ=0
    g4: LineSegment StartX=-6.8 StartY=-1.8 StartZ=0 EndX=-3.8 EndY=-1.8 EndZ=0
  constraints (13):
    c: Horizontal(g4)
    c: Horizontal(g0)
    c: Equal(g0,g4)
    c: Distance(g0) = 3
    c: Coincident(g1,g-3)
    c: Coincident(g1,g-3)
    c: Coincident(g2,g3)
    c: PointOnObject(g2,g-1)
    c: Coincident(g2,g0)
    c: Coincident(g0,g1)
    c: Coincident(g3,g4)
    c: Coincident(g1,g4)
    c: DistanceX(g2,g1) = 0.01
FEATURE [PartDesign::Pad] Pad104
  AllowMultiFace = false
  BaseFeature = -> Pad105
  Length = 10
  Length2 = 100
  Profile = -> Sketch195
  Reversed = true
  Type = 3
  UpToFace = -> Pad105 [Face4]
FEATURE [Sketcher::SketchObject] Sketch200
  ExternalGeometry = -> [Pad104]
  MapMode = 5
  Placement = pos=(0,0,22) rot=(0,0,1;0rad)
  Support = -> [Pad104]
  sketch-geometry (6):
    g0: ArcOfCircle CenterX=0 CenterY=0 CenterZ=0 NormalX=0 NormalY=0 NormalZ=1 AngleXU=0 Radius=1.8 StartAngle=4.71239 EndAngle=7.85398
    g1: LineSegment StartX=6e-16 StartY=1.8 StartZ=0 EndX=-1.69706 EndY=1.8 EndZ=0
    g2: LineSegment StartX=-3e-16 StartY=-1.8 StartZ=0 EndX=-1.69706 EndY=-1.8 EndZ=0
    g3: ArcOfCircle CenterX=0 CenterY=0 CenterZ=0 NormalX=0 NormalY=0 NormalZ=1 AngleXU=0 Radius=1.8 StartAngle=2.45182 EndAngle=3.83137
    g4: ArcOfCircle CenterX=-1.69706 CenterY=1.4 CenterZ=0 NormalX=0 NormalY=0 NormalZ=1 AngleXU=0 Radius=0.4 StartAngle=5.59341 EndAngle=7.85398
    g5: ArcOfCircle CenterX=-1.69706 CenterY=-1.4 CenterZ=0 NormalX=0 NormalY=0 NormalZ=1 AngleXU=0 Radius=0.4 StartAngle=4.71239 EndAngle=6.97296
  constraints (16):
    c: Coincident(g0,g-1)
    c: Coincident(g0,g-3)
    c: Coincident(g0,g-3)
    c: Coincident(g1,g0)
    c: Horizontal(g1)
    c: Coincident(g2,g0)
    c: Horizontal(g2)
    c: Equal(g1,g2)
    c: Coincident(g3,g0)
    c: Equal(g4,g5)
    c: Tangent(g4,g3) = 1.5708
    c: Tangent(g5,g3) = 1.5708
    c: Tangent(g5,g2) = 1.5708
    c: Tangent(g4,g1) = -1.5708
    c: Radius(g4) = 0.4
    c: Equal(g3,g0)
FEATURE [PartDesign::Pocket] Pocket079
  AllowMultiFace = false
  BaseFeature = -> Pad104
  Length = 2
  Length2 = 100
  Profile = -> Sketch200
  Type = 0
FEATURE [Sketcher::SketchObject] Sketch196
  ExternalGeometry = -> [Pocket079]
  MapMode = 5
  Placement = pos=(0,0,22) rot=(0,0,1;0rad)
  Support = -> [Pocket079]
  sketch-geometry (4):
    g0: LineSegment StartX=-1.8 StartY=1.8 StartZ=0 EndX=-3.4 EndY=1.8 EndZ=0
    g1: LineSegment StartX=-3.4 StartY=1.8 StartZ=0 EndX=-3.4 EndY=-1.8 EndZ=0
    g2: LineSegment StartX=-3.4 StartY=-1.8 StartZ=0 EndX=-1.8 EndY=-1.8 EndZ=0
    g3: LineSegment StartX=-1.8 StartY=-1.8 StartZ=0 EndX=-1.8 EndY=1.8 EndZ=0
  constraints (12):
    c: Coincident(g0,g1)
    c: Coincident(g1,g2)
    c: Coincident(g2,g3)
    c: Coincident(g3,g0)
    c: Horizontal(g0)
    c: Horizontal(g2)
    c: Vertical(g1)
    c: Vertical(g3)
    c: Distance(g0) = 1.6
    c: Tangent(g3,g-3)
    c: PointOnObject(g0,g-4)
    c: PointOnObject(g1,g-5)
FEATURE [PartDesign::Pad] Pad099
  AllowMultiFace = false
  BaseFeature = -> Pocket079
  Length = 8.5
  Length2 = 100
  Profile = -> Sketch196
  Type = 0
  expr: Length = 6.5 + 2
FEATURE [Sketcher::SketchObject] Sketch198
  ExternalGeometry = -> [Pad099]
  MapMode = 5
  Placement = pos=(0,0,22) rot=(0,0,1;0rad)
  Support = -> [Pad099]
  sketch-geometry (4):
    g0: LineSegment StartX=-6.8 StartY=1.8 StartZ=0 EndX=-3.4 EndY=1.8 EndZ=0
    g1: LineSegment StartX=-4.14222 StartY=0.2 StartZ=0 EndX=-6.8 EndY=1.8 EndZ=0
    g2: LineSegment StartX=-4.14222 StartY=0.2 StartZ=0 EndX=-3.4 EndY=0.2 EndZ=0
    g3: LineSegment StartX=-3.4 StartY=0.2 StartZ=0 EndX=-3.4 EndY=1.8 EndZ=0
  constraints (11):
    c: Coincident(g1,g0)
    c: Coincident(g2,g1)
    c: Coincident(g3,g2)
    c: Coincident(g3,g0)
    c: Distance(g3) = 1.6
    c: Horizontal(g0)
    c: Horizontal(g2)
    c: Coincident(g0,g-4)
    c: PointOnObject(g0,g-3)
    c: PointOnObject(g1,g-3)
    c: Vertical(g3)
FEATURE [PartDesign::Pad] Pad109
  AllowMultiFace = false
  BaseFeature = -> Pad099
  Length = 2
  Length2 = 100
  Profile = -> Sketch198
  Type = 0
FEATURE [Sketcher::SketchObject] Sketch202
  ExternalGeometry = -> [Pad109]
  MapMode = 5
  Placement = pos=(0,0,30.5) rot=(0,0,1;0rad)
  Support = -> [Pad109]
  sketch-geometry (4):
    g0: LineSegment StartX=-1.8 StartY=-1.8 StartZ=0 EndX=-7.4 EndY=-1.8 EndZ=0
    g1: LineSegment StartX=-7.4 StartY=-1.8 StartZ=0 EndX=-7.4 EndY=1.8 EndZ=0
    g2: LineSegment StartX=-7.4 StartY=1.8 StartZ=0 EndX=-1.8 EndY=1.8 EndZ=0
    g3: LineSegment StartX=-1.8 StartY=1.8 StartZ=0 EndX=-1.8 EndY=-1.8 EndZ=0
  constraints (10):
    c: Coincident(g0,g1)
    c: Coincident(g1,g2)
    c: Coincident(g2,g3)
    c: Coincident(g3,g0)
    c: Horizontal(g0)
    c: Horizontal(g2)
    c: Vertical(g1)
    c: Coincident(g2,g-3)
    c: Coincident(g0,g-3)
    c: DistanceX(g1,g-4) = 4
FEATURE [PartDesign::Pad] Pad107
  AllowMultiFace = false
  BaseFeature = -> Pad109
  Length = 1.6
  Length2 = 100
  Profile = -> Sketch202
  Type = 0
FEATURE [Sketcher::SketchObject] Sketch203
  ExternalGeometry = -> [Pocket077]
  MapMode = 5
  Placement = pos=(0,0,20) rot=(0,0,1;0rad)
  sketch-geometry (9):
    g0: LineSegment StartX=-10.8 StartY=1.8 StartZ=0 EndX=-10.8 EndY=-1.8 EndZ=0
    g1: LineSegment StartX=8.2 StartY=1.8 StartZ=0 EndX=11.19 EndY=-7e-16 EndZ=0
    g2: LineSegment StartX=11.19 StartY=-7e-16 StartZ=0 EndX=8.2 EndY=-1.8 EndZ=0
    g3: ArcOfCircle CenterX=0 CenterY=0 CenterZ=0 NormalX=0 NormalY=0 NormalZ=1 AngleXU=0 Radius=1.86815 StartAngle=1.84174 EndAngle=4.44144
    g4: ArcOfCircle CenterX=0 CenterY=0 CenterZ=0 NormalX=0 NormalY=0 NormalZ=1 AngleXU=0 Radius=1.86815 StartAngle=4.98334 EndAngle=7.58303
    g5: LineSegment StartX=-10.8 StartY=-1.8 StartZ=0 EndX=-0.5 EndY=-1.8 EndZ=0
    g6: LineSegment StartX=0.5 StartY=-1.8 StartZ=0 EndX=8.2 EndY=-1.8 EndZ=0
    g7: LineSegment StartX=8.2 StartY=1.8 StartZ=0 EndX=0.5 EndY=1.8 EndZ=0
    g8: LineSegment StartX=-0.5 StartY=1.8 StartZ=0 EndX=-10.8 EndY=1.8 EndZ=0
  constraints (22):
    c: Coincident(g2,g1)
    c: Coincident(g0,g-3)
    c: Coincident(g0,g-5)
    c: Coincident(g2,g-5)
    c: Coincident(g-4,g1)
    c: Coincident(g1,g-4)
    c: Coincident(g3,g-1)
    c: Coincident(g4,g3)
    c: Equal(g4,g3)
    c: Coincident(g5,g0)
    c: Coincident(g5,g3)
    c: Coincident(g6,g4)
    c: Coincident(g6,g2)
    c: Coincident(g7,g1)
    c: Coincident(g7,g4)
    c: Coincident(g8,g3)
    c: Coincident(g8,g0)
    c: Horizontal(g7)
    c: Horizontal(g8)
    c: Horizontal(g5)
    c: Horizontal(g6)
    c: DistanceX(g3,g4) = 1
FEATURE [PartDesign::Pad] Pad106
  AllowMultiFace = false
  BaseFeature = -> Pocket077
  Length = 2
  Length2 = 100
  Profile = -> Sketch203
  Type = 0
FEATURE [Sketcher::SketchObject] Sketch197
  ExternalGeometry = -> [Pad106]
  MapMode = 5
  Placement = pos=(0,0,22) rot=(0,0,1;0rad)
  Support = -> [Pad106]
  sketch-geometry (4):
    g0: LineSegment StartX=-10.8 StartY=1.8 StartZ=0 EndX=-9.2 EndY=1.8 EndZ=0
    g1: LineSegment StartX=-9.2 StartY=1.8 StartZ=0 EndX=-9.2 EndY=-1.8 EndZ=0
    g2: LineSegment StartX=-9.2 StartY=-1.8 StartZ=0 EndX=-10.8 EndY=-1.8 EndZ=0
    g3: LineSegment StartX=-10.8 StartY=-1.8 StartZ=0 EndX=-10.8 EndY=1.8 EndZ=0
  constraints (10):
    c: Coincident(g0,g1)
    c: Coincident(g1,g2)
    c: Coincident(g2,g3)
    c: Coincident(g3,g0)
    c: Horizontal(g0)
    c: Horizontal(g2)
    c: Vertical(g1)
    c: Coincident(g0,g-3)
    c: Coincident(g2,g-3)
    c: Distance(g0) = 1.6
FEATURE [PartDesign::Pad] Pad110
  AllowMultiFace = false
  BaseFeature = -> Pad106
  Length = 8.5
  Length2 = 100
  Profile = -> Sketch197
  Type = 0
  expr: Length = 6.5 + 2
FEATURE [Sketcher::SketchObject] Sketch201
  ExternalGeometry = -> [Pad110]
  MapMode = 5
  Placement = pos=(0,0,22) rot=(0,0,1;0rad)
  Support = -> [Pad110]
  sketch-geometry (9):
    g0: LineSegment StartX=-9.2 StartY=0.2 StartZ=0 EndX=-1.85742 EndY=0.2 EndZ=0
    g1: LineSegment StartX=-0.5 StartY=1.8 StartZ=0 EndX=-9.2 EndY=1.8 EndZ=0
    g2: LineSegment StartX=-9.2 StartY=1.8 StartZ=0 EndX=-9.2 EndY=0.2 EndZ=0
    g3: ArcOfCircle CenterX=0 CenterY=0 CenterZ=0 NormalX=0 NormalY=0 NormalZ=1 AngleXU=0 Radius=1.86815 StartAngle=1.84174 EndAngle=3.03433
    g4: ArcOfCircle CenterX=0 CenterY=0 CenterZ=0 NormalX=0 NormalY=0 NormalZ=1 AngleXU=0 Radius=1.86815 StartAngle=0.107263 EndAngle=1.29985
    g5: LineSegment StartX=0.5 StartY=1.8 StartZ=0 EndX=8.2 EndY=1.8 EndZ=0
    g6: LineSegment StartX=1.85742 StartY=0.2 StartZ=0 EndX=10.8578 EndY=0.2 EndZ=0
    g7: LineSegment StartX=10.8578 StartY=0.2 StartZ=0 EndX=8.2 EndY=1.8 EndZ=0
    g8: LineSegment [constr] StartX=-1.85742 StartY=0.2 StartZ=0 EndX=1.85742 EndY=0.2 EndZ=0
  constraints (24):
    c: Coincident(g1,g2)
    c: Coincident(g2,g0)
    c: Vertical(g2)
    c: Coincident(g3,g-1)
    c: Coincident(g3,g1)
    c: Coincident(g3,g0)
    c: Distance(g2) = 1.6
    c: Coincident(g4,g3)
    c: Coincident(g5,g4)
    c: Coincident(g6,g4)
    c: Coincident(g5,g7)
    c: Coincident(g6,g7)
    c: Horizontal(g6)
    c: Horizontal(g0)
    c: Coincident(g1,g-3)
    c: Coincident(g5,g-4)
    c: PointOnObject(g6,g-4)
    c: Horizontal(g1)
    c: Horizontal(g5)
    c: PointOnObject(g1,g-5)
    c: PointOnObject(g4,g-6)
    c: Coincident(g8,g0)
    c: Coincident(g8,g4)
    c: Horizontal(g8)
FEATURE [PartDesign::Pad] Pad111
  AllowMultiFace = false
  BaseFeature = -> Pad110
  Length = 2
  Length2 = 100
  Profile = -> Sketch201
  Type = 0
FEATURE [Sketcher::SketchObject] Sketch199
  ExternalGeometry = -> [Pad111]
  MapMode = 5
  Placement = pos=(0,0,30.5) rot=(0,0,1;0rad)
  Support = -> [Pad111]
  sketch-geometry (4):
    g0: LineSegment StartX=-10.8 StartY=1.8 StartZ=0 EndX=-5.2 EndY=1.8 EndZ=0
    g1: LineSegment StartX=-5.2 StartY=1.8 StartZ=0 EndX=-5.2 EndY=-1.8 EndZ=0
    g2: LineSegment StartX=-5.2 StartY=-1.8 StartZ=0 EndX=-10.8 EndY=-1.8 EndZ=0
    g3: LineSegment StartX=-10.8 StartY=-1.8 StartZ=0 EndX=-10.8 EndY=1.8 EndZ=0
  constraints (10):
    c: Coincident(g0,g1)
    c: Coincident(g1,g2)
    c: Coincident(g2,g3)
    c: Coincident(g3,g0)
    c: Horizontal(g0)
    c: Horizontal(g2)
    c: Vertical(g1)
    c: Coincident(g0,g-3)
    c: Coincident(g2,g-3)
    c: DistanceX(g-4,g0) = 4
FEATURE [PartDesign::Pad] Pad108
  AllowMultiFace = false
  BaseFeature = -> Pad111
  Length = 1.6
  Length2 = 100
  Profile = -> Sketch199
  Type = 0
FEATURE [Sketcher::SketchObject] Sketch204
  ExternalGeometry = -> [Pad107]
  MapMode = 5
  Placement = pos=(0,0,32.1) rot=(0,0,1;0rad)
  Support = -> [Pad107]
  sketch-geometry (4):
    g0: LineSegment StartX=-3.4 StartY=-1.8 StartZ=0 EndX=-7.4 EndY=-1.8 EndZ=0
    g1: LineSegment StartX=-7.4 StartY=-1.8 StartZ=0 EndX=-7.4 EndY=-0.8 EndZ=0
    g2: LineSegment StartX=-7.4 StartY=-0.8 StartZ=0 EndX=-3.4 EndY=-0.8 EndZ=0
    g3: LineSegment StartX=-3.4 StartY=-0.8 StartZ=0 EndX=-3.4 EndY=-1.8 EndZ=0
  constraints (11):
    c: Coincident(g0,g1)
    c: Coincident(g1,g2)
    c: Coincident(g2,g3)
    c: Coincident(g3,g0)
    c: Horizontal(g0)
    c: Horizontal(g2)
    c: Vertical(g1)
    c: Vertical(g3)
    c: Coincident(g0,g-4)
    c: PointOnObject(g1,g-3)
    c: Distance(g3) = 1
FEATURE [PartDesign::Pocket] Pocket080
  AllowMultiFace = false
  BaseFeature = -> Pad107
  Length = 5
  Length2 = 100
  Profile = -> Sketch204
  Type = 2
FEATURE [Sketcher::SketchObject] Sketch205
  ExternalGeometry = -> [Pad108]
  MapMode = 5
  Placement = pos=(0,0,32.1) rot=(0,0,1;0rad)
  Support = -> [Pad108]
  sketch-geometry (4):
    g0: LineSegment StartX=-9.2 StartY=-1.8 StartZ=0 EndX=-5.2 EndY=-1.8 EndZ=0
    g1: LineSegment StartX=-5.2 StartY=-1.8 StartZ=0 EndX=-5.2 EndY=-0.8 EndZ=0
    g2: LineSegment StartX=-5.2 StartY=-0.8 StartZ=0 EndX=-9.2 EndY=-0.8 EndZ=0
    g3: LineSegment StartX=-9.2 StartY=-0.8 StartZ=0 EndX=-9.2 EndY=-1.8 EndZ=0
  constraints (11):
    c: Coincident(g0,g1)
    c: Coincident(g1,g2)
    c: Coincident(g2,g3)
    c: Coincident(g3,g0)
    c: Horizontal(g0)
    c: Horizontal(g2)
    c: Vertical(g1)
    c: Vertical(g3)
    c: Coincident(g0,g-4)
    c: PointOnObject(g1,g-3)
    c: Distance(g3) = 1
FEATURE [PartDesign::Pocket] Pocket081
  AllowMultiFace = false
  BaseFeature = -> Pad108
  Length = 5
  Length2 = 100
  Profile = -> Sketch205
  Type = 2
FEATURE [PartDesign::Body] Body058
  Group = -> [Sketch191,Pad101,Sketch189,Pad100,Sketch188,Sketch193,Pocket078,Pocket077,Sketch203,Pad106,Sketch197,Pad110,Sketch201,Pad111,Sketch199,Pad108,Sketch205,Pocket081]
  Origin = -> Origin065
  Placement = pos=(0,35.2,0) rot=(0,0,1;0rad)
  Tip = -> Pocket081
  expr: .Placement.Base.y = 40 - 2.4 * 2
FEATURE [Sketcher::SketchObject] Sketch206
  ExternalGeometry = -> [Pad095]
  MapMode = 5
  Placement = pos=(0,0,34.6) rot=(0,0,1;0rad)
  Support = -> [Pad095]
  sketch-geometry (4):
    g0: LineSegment StartX=-9.2 StartY=1.8 StartZ=0 EndX=-5.2 EndY=1.8 EndZ=0
    g1: LineSegment StartX=-5.2 StartY=1.8 StartZ=0 EndX=-5.2 EndY=0.8 EndZ=0
    g2: LineSegment StartX=-5.2 StartY=0.8 StartZ=0 EndX=-9.2 EndY=0.8 EndZ=0
    g3: LineSegment StartX=-9.2 StartY=0.8 StartZ=0 EndX=-9.2 EndY=1.8 EndZ=0
  constraints (11):
    c: Coincident(g0,g1)
    c: Coincident(g1,g2)
    c: Coincident(g2,g3)
    c: Coincident(g3,g0)
    c: Horizontal(g0)
    c: Horizontal(g2)
    c: Vertical(g1)
    c: Vertical(g3)
    c: Coincident(g0,g-4)
    c: PointOnObject(g1,g-3)
    c: Distance(g1) = 1
FEATURE [PartDesign::Pocket] Pocket082
  AllowMultiFace = false
  BaseFeature = -> Pad095
  Length = 5
  Length2 = 100
  Profile = -> Sketch206
  Type = 2
FEATURE [PartDesign::Body] Body055
  Group = -> [Sketch172,Pad086,Sketch173,Pad087,Sketch176,Sketch177,Pocket074,Pocket075,Sketch180,Pad092,Sketch181,Pad093,Sketch182,Pad094,Sketch183,Pad095,Sketch206,Pocket082]
  Origin = -> Origin062
  Tip = -> Pocket082
FEATURE [PartDesign::FeatureBase] Clone032
  BaseFeature = -> Body055
FEATURE [PartDesign::Body] Body054
  BaseFeature = -> Body055
  Group = -> [Clone032]
  Origin = -> Origin066
  Tip = -> Clone032
FEATURE [Sketcher::SketchObject] Sketch207
  ExternalGeometry = -> [Pad098]
  MapMode = 5
  Placement = pos=(0,0,34.6) rot=(0,0,1;0rad)
  Support = -> [Pad098]
  sketch-geometry (4):
    g0: LineSegment StartX=-3.4 StartY=1.8 StartZ=0 EndX=-7.4 EndY=1.8 EndZ=0
    g1: LineSegment StartX=-7.4 StartY=1.8 StartZ=0 EndX=-7.4 EndY=0.8 EndZ=0
    g2: LineSegment StartX=-7.4 StartY=0.8 StartZ=0 EndX=-3.4 EndY=0.8 EndZ=0
    g3: LineSegment StartX=-3.4 StartY=0.8 StartZ=0 EndX=-3.4 EndY=1.8 EndZ=0
  constraints (11):
    c: Coincident(g0,g1)
    c: Coincident(g1,g2)
    c: Coincident(g2,g3)
    c: Coincident(g3,g0)
    c: Horizontal(g0)
    c: Horizontal(g2)
    c: Vertical(g1)
    c: Vertical(g3)
    c: Coincident(g0,g-4)
    c: PointOnObject(g1,g-3)
    c: Distance(g3) = 1
FEATURE [PartDesign::Pocket] Pocket083
  AllowMultiFace = false
  BaseFeature = -> Pad098
  Length = 5
  Length2 = 100
  Profile = -> Sketch207
  Type = 2
FEATURE [PartDesign::Body] Body056
  Group = -> [Sketch174,Pad088,Sketch175,Pad089,Sketch178,Sketch179,Pad090,Pad091,Sketch184,Pocket076,Sketch185,Pad096,Sketch186,Pad097,Sketch187,Pad098,Sketch207,Pocket083]
  Origin = -> Origin063
  Placement = pos=(15.2,0,0) rot=(0,0,1;0rad)
  Tip = -> Pocket083
  expr: .Placement.Base.x = 20 - 2.4 * 2
FEATURE [Sketcher::SketchObject] Sketch208
  ExternalGeometry = -> [Pocket080]
  MapMode = 5
  Support = -> [XY_Plane064]
  expr: Constraints[11] = (20 - 2.4 * 2) / 2 + 7.5 / 2
  sketch-geometry (4):
    g0: ArcOfCircle CenterX=0 CenterY=0 CenterZ=0 NormalX=0 NormalY=0 NormalZ=1 AngleXU=0 Radius=1.8 StartAngle=1.5708 EndAngle=4.71239
    g1: LineSegment StartX=0 StartY=1.8 StartZ=0 EndX=-11.35 EndY=1.8 EndZ=0
    g2: LineSegment StartX=0 StartY=-1.8 StartZ=0 EndX=-11.35 EndY=-1.8 EndZ=0
    g3: LineSegment StartX=-11.35 StartY=1.8 StartZ=0 EndX=-11.35 EndY=-1.8 EndZ=0
  constraints (12):
    c: Coincident(g0,g-1)
    c: PointOnObject(g0,g-2)
    c: PointOnObject(g0,g-2)
    c: Equal(g-3,g0)
    c: Coincident(g1,g0)
    c: Horizontal(g1)
    c: Coincident(g2,g0)
    c: Horizontal(g2)
    c: Coincident(g3,g1)
    c: Coincident(g3,g2)
    c: Vertical(g3)
    c: Distance(g1) = 11.35
FEATURE [PartDesign::Pad] Pad112
  AllowMultiFace = false
  BaseFeature = -> Pocket080
  Length = 4
  Length2 = 100
  Profile = -> Sketch208
  Type = 0
FEATURE [Sketcher::SketchObject] Sketch209
  ExternalGeometry = -> [Pad112]
  MapMode = 5
  Placement = pos=(0,0,0) rot=(1,0,0;3.14159rad)
  Support = -> [Pad112]
  sketch-geometry (4):
    g0: LineSegment StartX=-11.35 StartY=1.8 StartZ=0 EndX=-3.85 EndY=1.8 EndZ=0
    g1: LineSegment StartX=-3.85 StartY=1.8 StartZ=0 EndX=-3.85 EndY=-1.8 EndZ=0
    g2: LineSegment StartX=-3.85 StartY=-1.8 StartZ=0 EndX=-11.35 EndY=-1.8 EndZ=0
    g3: LineSegment StartX=-11.35 StartY=-1.8 StartZ=0 EndX=-11.35 EndY=1.8 EndZ=0
  constraints (10):
    c: Coincident(g0,g1)
    c: Coincident(g1,g2)
    c: Coincident(g2,g3)
    c: Coincident(g3,g0)
    c: Horizontal(g0)
    c: Horizontal(g2)
    c: Vertical(g1)
    c: Coincident(g0,g-3)
    c: Coincident(g2,g-3)
    c: Distance(g0) = 7.5
FEATURE [PartDesign::Pocket] Pocket084
  AllowMultiFace = false
  BaseFeature = -> Pad112
  Length = 1.2
  Length2 = 100
  Profile = -> Sketch209
  Type = 0
FEATURE [Sketcher::SketchObject] Sketch171
  ExternalGeometry = -> [Pocket084]
  MapMode = 5
  Placement = pos=(0,1.8,0) rot=(0,0.707107,0.707107;3.14159rad)
  Support = -> [Pocket084]
  sketch-geometry (3):
    g0: LineSegment StartX=11.35 StartY=4 StartZ=0 EndX=0 EndY=4 EndZ=0
    g1: LineSegment StartX=11.35 StartY=4 StartZ=0 EndX=0 EndY=10 EndZ=0
    g2: LineSegment StartX=0 StartY=10 StartZ=0 EndX=0 EndY=4 EndZ=0
  constraints (7):
    c: Coincident(g0,g-3)
    c: Coincident(g0,g-3)
    c: Coincident(g1,g0)
    c: Coincident(g2,g1)
    c: Coincident(g2,g0)
    c: Vertical(g2)
    c: Distance(g2) = 6
FEATURE [PartDesign::Pad] Pad113
  AllowMultiFace = false
  BaseFeature = -> Pocket084
  Length = 10
  Length2 = 100
  Profile = -> Sketch171
  Reversed = true
  Type = 3
  UpToFace = -> Pocket084 [Face7]
FEATURE [Sketcher::SketchObject] Sketch210
  ExternalGeometry = -> [Pad113]
  MapMode = 5
  Support = -> [XY_Plane064]
  sketch-geometry (1):
    g0: Circle CenterX=0 CenterY=0 CenterZ=0 NormalX=0 NormalY=0 NormalZ=1 AngleXU=0 Radius=1
  constraints (2):
    c: Coincident(g0,g-1)
    c: Equal(g-3,g0)
FEATURE [PartDesign::Pocket] Pocket085
  AllowMultiFace = false
  BaseFeature = -> Pad113
  Length = 5
  Length2 = 100
  Profile = -> Sketch210
  Reversed = true
  Type = 1
FEATURE [PartDesign::Body] Body057
  Group = -> [Sketch192,Pad102,Sketch190,Pad103,Sketch194,Sketch195,Pad105,Pad104,Sketch200,Pocket079,Sketch196,Pad099,Sketch198,Pad109,Sketch202,Pad107,Sketch204,Pocket080,Sketch208,Pad112,Sketch209,Pocket084,Sketch171,Pad113,Sketch210,Pocket085]
  Origin = -> Origin064
  Placement = pos=(15.2,35.2,0) rot=(0,0,1;0rad)
  Tip = -> Pocket085
  expr: .Placement.Base.x = 20 - 2.4 * 2
  expr: .Placement.Base.y = 40 - 2.4 * 2
FEATURE [PartDesign::FeatureBase] Clone033
  BaseFeature = -> Body056
  Placement = pos=(15.2,0,0) rot=(0,0,1;0rad)
FEATURE [PartDesign::Body] Body059
  BaseFeature = -> Body056
  Group = -> [Clone033]
  Origin = -> Origin061
  Tip = -> Clone033
FEATURE [PartDesign::FeatureBase] Clone034
  BaseFeature = -> Body057
  Placement = pos=(15.2,35.2,0) rot=(0,0,1;0rad)
FEATURE [PartDesign::Body] Body060
  BaseFeature = -> Body057
  Group = -> [Clone034]
  Origin = -> Origin067
  Tip = -> Clone034
FEATURE [PartDesign::FeatureBase] Clone035
  BaseFeature = -> Body058
  Placement = pos=(0,35.2,0) rot=(0,0,1;0rad)
FEATURE [PartDesign::Body] Body061
  Group = -> [Clone035]
  Origin = -> Origin068
  Tip = -> Clone035
FEATURE [App::Part] Part007
  Group = -> [Body054,Body059,Body060,Body061]
  Origin = -> Origin069
  Placement = pos=(6.5,-193.2,-231.5) rot=(0,-0.707107,-0.707107;3.14159rad)
FEATURE [PartDesign::FeatureBase] Clone036
  BaseFeature = -> Body014
  Placement = pos=(0,0,0) rot=(0,-1,0;1.5708rad)
FEATURE [PartDesign::Body] Body062
  BaseFeature = -> Body014
  Group = -> [Clone036]
  Origin = -> Origin070
  Placement = pos=(-1,-211,-203.8) rot=(0.57735,0.57735,-0.57735;4.18879rad)
  Tip = -> Clone036
FEATURE [Sketcher::SketchObject] Sketch211
  MapMode = 5
  Support = -> [XY_Plane071]
  sketch-geometry (8):
    g0: LineSegment StartX=-7.5 StartY=7.5 StartZ=0 EndX=7.5 EndY=7.5 EndZ=0
    g1: LineSegment StartX=7.5 StartY=7.5 StartZ=0 EndX=7.5 EndY=-7.5 EndZ=0
    g2: LineSegment StartX=7.5 StartY=-7.5 StartZ=0 EndX=-7.5 EndY=-7.5 EndZ=0
    g3: LineSegment StartX=-7.5 StartY=-7.5 StartZ=0 EndX=-7.5 EndY=7.5 EndZ=0
    g4: LineSegment StartX=-6.5 StartY=6.5 StartZ=0 EndX=6.5 EndY=6.5 EndZ=0
    g5: LineSegment StartX=6.5 StartY=6.5 StartZ=0 EndX=6.5 EndY=-6.5 EndZ=0
    g6: LineSegment StartX=6.5 StartY=-6.5 StartZ=0 EndX=-6.5 EndY=-6.5 EndZ=0
    g7: LineSegment StartX=-6.5 StartY=-6.5 StartZ=0 EndX=-6.5 EndY=6.5 EndZ=0
  constraints (22):
    c: Coincident(g0,g1)
    c: Coincident(g1,g2)
    c: Coincident(g2,g3)
    c: Coincident(g3,g0)
    c: Horizontal(g0)
    c: Horizontal(g2)
    c: Vertical(g1)
    c: Vertical(g3)
    c: Symmetric(g0,g1,g-1)
    c: Equal(g0,g1)
    c: Distance(g0) = 15
    c: Coincident(g4,g5)
    c: Coincident(g5,g6)
    c: Coincident(g6,g7)
    c: Coincident(g7,g4)
    c: Horizontal(g4)
    c: Horizontal(g6)
    c: Vertical(g5)
    c: Vertical(g7)
    c: Symmetric(g4,g5,g-1)
    c: Equal(g4,g5)
    c: Distance(g4) = 13
FEATURE [PartDesign::Pad] Pad114
  Length = 56
  Length2 = 100
  Profile = -> Sketch211
  Refine = true
  Reversed = true
  Type = 0
FEATURE [PartDesign::Body] Body063
  Group = -> [Sketch211,Pad114]
  Origin = -> Origin071
  Placement = pos=(17,-224.3,-203.8) rot=(0,1,0;1.5708rad)
  Tip = -> Pad114
FEATURE [Sketcher::SketchObject] Sketch212
  MapMode = 5
  Support = -> [XY_Plane073]
  expr: Constraints[25] = 10 / 2
  sketch-geometry (9):
    g0: ArcOfCircle CenterX=0 CenterY=0 CenterZ=0 NormalX=0 NormalY=0 NormalZ=1 AngleXU=0 Radius=4.6 StartAngle=5.38434 EndAngle=7.18203
    g1: LineSegment StartX=2.86356 StartY=3.6 StartZ=0 EndX=0 EndY=3.6 EndZ=0
    g2: LineSegment StartX=2.86356 StartY=-3.6 StartZ=0 EndX=0 EndY=-3.6 EndZ=0
    g3: ArcOfCircle CenterX=0 CenterY=0 CenterZ=0 NormalX=0 NormalY=0 NormalZ=1 AngleXU=0 Radius=5 StartAngle=5.35589 EndAngle=7.21048
    g4: LineSegment StartX=3 StartY=4 StartZ=0 EndX=0 EndY=4 EndZ=0
    g5: LineSegment StartX=3 StartY=-4 StartZ=0 EndX=0 EndY=-4 EndZ=0
    g6: LineSegment StartX=0 StartY=-3.6 StartZ=0 EndX=0 EndY=-4 EndZ=0
    g7: LineSegment StartX=0 StartY=4 StartZ=0 EndX=0 EndY=3.6 EndZ=0
    g8: LineSegment [constr] StartX=4.6 StartY=-5.05e-14 StartZ=0 EndX=5 EndY=-5.05e-14 EndZ=0
  constraints (27):
    c: Coincident(g0,g-1)
    c: Coincident(g1,g0)
    c: PointOnObject(g1,g-2)
    c: Horizontal(g1)
    c: Coincident(g2,g0)
    c: PointOnObject(g2,g-2)
    c: Horizontal(g2)
    c: Coincident(g3,g0)
    c: Coincident(g4,g3)
    c: PointOnObject(g4,g-2)
    c: Horizontal(g4)
    c: Coincident(g5,g3)
    c: PointOnObject(g5,g-2)
    c: Horizontal(g5)
    c: Coincident(g6,g2)
    c: Coincident(g6,g5)
    c: Coincident(g7,g4)
    c: Coincident(g7,g1)
    c: Equal(g4,g5)
    c: Equal(g6,g7)
    c: PointOnObject(g8,g0)
    c: PointOnObject(g8,g3)
    c: Horizontal(g8)
    c: Equal(g8,g7)
    c: Distance(g7) = 0.4
    c: Radius(g3) = 5
    c: Distance(g4,g5) = 8
FEATURE [PartDesign::Pad] Pad115
  Length = 10.95
  Length2 = 100
  Profile = -> Sketch212
  Reversed = true
  Type = 0
  expr: Length = 11.35 - 0.4
FEATURE [PartDesign::Mirrored] Mirrored017
  BaseFeature = -> Pad115
  MirrorPlane = -> Sketch212 [V_Axis]
  Originals = -> [Pad115]
FEATURE [Sketcher::SketchObject] Sketch213
  ExternalGeometry = -> [Mirrored017]
  MapMode = 5
  Placement = pos=(0,0,-10.95) rot=(1,0,0;3.14159rad)
  Support = -> [Mirrored017]
  sketch-geometry (4):
    g0: ArcOfCircle CenterX=0 CenterY=0 CenterZ=0 NormalX=0 NormalY=0 NormalZ=1 AngleXU=0 Radius=5 StartAngle=2.2143 EndAngle=4.06889
    g1: ArcOfCircle CenterX=0 CenterY=0 CenterZ=0 NormalX=0 NormalY=0 NormalZ=1 AngleXU=0 Radius=5 StartAngle=5.35589 EndAngle=7.21048
    g2: LineSegment StartX=3 StartY=4 StartZ=0 EndX=-3 EndY=4 EndZ=0
    g3: LineSegment StartX=-3 StartY=-4 StartZ=0 EndX=3 EndY=-4 EndZ=0
  constraints (10):
    c: Coincident(g0,g-1)
    c: Coincident(g1,g0)
    c: Coincident(g0,g-3)
    c: Coincident(g1,g-4)
    c: Coincident(g2,g1)
    c: Coincident(g2,g0)
    c: Horizontal(g2)
    c: Coincident(g3,g0)
    c: Coincident(g3,g1)
    c: Horizontal(g3)
FEATURE [PartDesign::Pad] Pad116
  BaseFeature = -> Mirrored017
  Length = 0.4
  Length2 = 100
  Profile = -> Sketch213
  Type = 0
FEATURE [PartDesign::Fillet] Fillet032
  Base = -> Pad116 [Edge37,Edge35,Edge45,Edge43]
  BaseFeature = -> Pad116
  Radius = 0.5
  SupportTransform = true
FEATURE [PartDesign::Fillet] Fillet033
  Base = -> Fillet032 [Face26]
  BaseFeature = -> Fillet032
  Radius = 0.5
  SupportTransform = true
FEATURE [Sketcher::SketchObject] Sketch214
  MapMode = 5
  Placement = pos=(0,0,-11.35) rot=(1,0,0;3.14159rad)
  Support = -> [Fillet033]
  sketch-geometry (1):
    g0: Circle CenterX=0 CenterY=0 CenterZ=0 NormalX=0 NormalY=0 NormalZ=1 AngleXU=0 Radius=2
  constraints (2):
    c: Coincident(g0,g-1)
    c: Radius(g0) = 2
FEATURE [PartDesign::Pad] Pad117
  BaseFeature = -> Fillet033
  Length = 0.5
  Length2 = 100
  Profile = -> Sketch214
  Type = 0
FEATURE [Sketcher::SketchObject] Sketch215
  MapMode = 5
  Placement = pos=(0,0,-11.85) rot=(1,0,0;3.14159rad)
  Support = -> [Pad117]
  expr: Constraints[4] = 5.5 / 2 + 0.5
  sketch-geometry (2):
    g0: Circle CenterX=0 CenterY=0 CenterZ=0 NormalX=0 NormalY=0 NormalZ=1 AngleXU=0 Radius=0.5
    g1: Circle CenterX=3.25 CenterY=0 CenterZ=0 NormalX=0 NormalY=0 NormalZ=1 AngleXU=0 Radius=0.5
  constraints (5):
    c: Coincident(g0,g-1)
    c: Radius(g0) = 0.5
    c: PointOnObject(g1,g-1)
    c: Radius(g1) = 0.5
    c: DistanceX(g1) = 3.25
FEATURE [PartDesign::Pocket] Pocket086
  BaseFeature = -> Pad117
  Length = 5
  Length2 = 100
  Profile = -> Sketch215
  Type = 1
FEATURE [PartDesign::Mirrored] Mirrored018
  BaseFeature = -> Pocket086
  MirrorPlane = -> Sketch215 [V_Axis]
  Originals = -> [Pocket086]
FEATURE [Sketcher::SketchObject] Sketch216
  ExternalGeometry = -> [Mirrored018]
  MapMode = 5
  Placement = pos=(0,0,-10.95) rot=(0,0,1;0rad)
  Support = -> [Mirrored018]
  sketch-geometry (4):
    g0: ArcOfCircle CenterX=0 CenterY=0 CenterZ=0 NormalX=0 NormalY=0 NormalZ=1 AngleXU=0 Radius=4.6 StartAngle=5.38434 EndAngle=7.18203
    g1: LineSegment StartX=2.86356 StartY=-3.6 StartZ=0 EndX=1.86356 EndY=-3.6 EndZ=0
    g2: LineSegment StartX=2.86356 StartY=3.6 StartZ=0 EndX=1.86356 EndY=3.6 EndZ=0
    g3: ArcOfCircle CenterX=-1 CenterY=-1.08128e-11 CenterZ=0 NormalX=0 NormalY=0 NormalZ=1 AngleXU=0 Radius=4.6 StartAngle=5.38434 EndAngle=7.18203
  constraints (12):
    c: Coincident(g0,g-1)
    c: Coincident(g0,g-3)
    c: Coincident(g1,g0)
    c: PointOnObject(g1,g-4)
    c: Horizontal(g1)
    c: Coincident(g2,g0)
    c: Horizontal(g2)
    c: Coincident(g3,g2)
    c: Coincident(g3,g1)
    c: Equal(g0,g3)
    c: Distance(g1) = 1
    c: Equal(g2,g1)
FEATURE [PartDesign::Pad] Pad118
  BaseFeature = -> Mirrored018
  Length = 10
  Length2 = 100
  Offset = -2.4
  Profile = -> Sketch216
  Type = 3
  UpToFace = -> Mirrored018 [Face4]
FEATURE [PartDesign::Mirrored] Mirrored019
  BaseFeature = -> Pad118
  MirrorPlane = -> Sketch216 [V_Axis]
  Originals = -> [Pad118]
FEATURE [PartDesign::Body] Body064
  Group = -> [Sketch212,Pad115,Mirrored017,Sketch213,Pad116,Fillet032,Fillet033,Sketch214,Pad117,Sketch215,Pocket086,Mirrored018,Sketch216,Pad118,Mirrored019]
  Origin = -> Origin072
  Tip = -> Mirrored019
FEATURE [Sketcher::SketchObject] Sketch217
  MapMode = 5
  Support = -> [XY_Plane074]
  sketch-geometry (4):
    g0: ArcOfCircle CenterX=0 CenterY=0 CenterZ=0 NormalX=0 NormalY=0 NormalZ=1 AngleXU=0 Radius=5 StartAngle=5.35589 EndAngle=7.21048
    g1: LineSegment StartX=3 StartY=4 StartZ=0 EndX=0 EndY=4 EndZ=0
    g2: LineSegment StartX=0 StartY=4 StartZ=0 EndX=0 EndY=-4 EndZ=0
    g3: LineSegment StartX=0 StartY=-4 StartZ=0 EndX=3 EndY=-4 EndZ=0
  constraints (12):
    c: Coincident(g0,g-1)
    c: Radius(g0) = 5
    c: Coincident(g1,g0)
    c: PointOnObject(g1,g-2)
    c: Horizontal(g1)
    c: Coincident(g2,g1)
    c: PointOnObject(g2,g-2)
    c: Coincident(g3,g2)
    c: Coincident(g3,g0)
    c: Horizontal(g3)
    c: Distance(g2) = 8
    c: Equal(g1,g3)
FEATURE [PartDesign::Pad] Pad119
  Length = 1
  Length2 = 100
  Profile = -> Sketch217
  Type = 0
FEATURE [PartDesign::Mirrored] Mirrored020
  BaseFeature = -> Pad119
  MirrorPlane = -> Sketch217 [V_Axis]
  Originals = -> [Pad119]
FEATURE [Sketcher::SketchObject] Sketch218
  MapMode = 5
  Placement = pos=(0,0,1) rot=(0,0,1;0rad)
  Support = -> [Mirrored020]
  sketch-geometry (1):
    g0: Circle CenterX=0 CenterY=0 CenterZ=0 NormalX=0 NormalY=0 NormalZ=1 AngleXU=0 Radius=2
  constraints (2):
    c: Coincident(g0,g-1)
    c: Radius(g0) = 2
FEATURE [PartDesign::Pad] Pad120
  BaseFeature = -> Mirrored020
  Length = 1
  Length2 = 100
  Profile = -> Sketch218
  Type = 0
FEATURE [Sketcher::SketchObject] Sketch219
  MapMode = 5
  Placement = pos=(0,0,0) rot=(1,0,0;3.14159rad)
  Support = -> [Pad120]
  sketch-geometry (1):
    g0: Circle CenterX=0 CenterY=0 CenterZ=0 NormalX=0 NormalY=0 NormalZ=1 AngleXU=0 Radius=0.6
  constraints (2):
    c: Coincident(g0,g-1)
    c: Radius(g0) = 0.6
FEATURE [PartDesign::Pocket] Pocket087
  BaseFeature = -> Pad120
  Length = 5
  Length2 = 100
  Profile = -> Sketch219
  Type = 1
FEATURE [Sketcher::SketchObject] Sketch220
  ExternalGeometry = -> [Pocket087]
  MapMode = 5
  Placement = pos=(0,0,0) rot=(1,0,0;3.14159rad)
  Support = -> [Pocket087]
  expr: Constraints[2] = 5 - 0.4
  sketch-geometry (4):
    g0: ArcOfCircle CenterX=0 CenterY=0 CenterZ=0 NormalX=0 NormalY=0 NormalZ=1 AngleXU=0 Radius=4.6 StartAngle=5.38434 EndAngle=7.18203
    g1: LineSegment StartX=2.86356 StartY=3.6 StartZ=0 EndX=2.46356 EndY=3.6 EndZ=0
    g2: LineSegment StartX=2.46356 StartY=3.6 StartZ=0 EndX=2.46356 EndY=-3.6 EndZ=0
    g3: LineSegment StartX=2.86356 StartY=-3.6 StartZ=0 EndX=2.46356 EndY=-3.6 EndZ=0
  constraints (12):
    c: Coincident(g0,g-1)
    c: Vertical(g0,g0)
    c: Radius(g0) = 4.6
    c: DistanceY(g0,g-3) = 0.4
    c: Coincident(g1,g0)
    c: Coincident(g2,g1)
    c: Vertical(g2)
    c: Coincident(g3,g0)
    c: Coincident(g3,g2)
    c: Horizontal(g3)
    c: Horizontal(g1)
    c: Distance(g1) = 0.4
FEATURE [PartDesign::Pad] Pad121
  BaseFeature = -> Pocket087
  Length = 2
  Length2 = 100
  Profile = -> Sketch220
  Type = 0
FEATURE [Sketcher::SketchObject] Sketch221
  MapMode = 5
  Placement = pos=(0,0,-2) rot=(1,0,0;3.14159rad)
  Support = -> [Pad121]
  expr: Constraints[11] = 5 - 0.4 - 1
  sketch-geometry (8):
    g0: LineSegment StartX=3.1 StartY=2 StartZ=0 EndX=3.6 EndY=2 EndZ=0
    g1: LineSegment StartX=3.6 StartY=2 StartZ=0 EndX=3.6 EndY=-2 EndZ=0
    g2: LineSegment [constr] StartX=3.6 StartY=-2 StartZ=0 EndX=3.1 EndY=-2 EndZ=0
    g3: LineSegment StartX=3.1 StartY=-2 StartZ=0 EndX=3.1 EndY=2 EndZ=0
    g4: LineSegment StartX=3.6 StartY=-2 StartZ=0 EndX=3.6 EndY=-4.12277 EndZ=0
    g5: LineSegment StartX=3.1 StartY=-2 StartZ=0 EndX=2.06757 EndY=-2 EndZ=0
    g6: LineSegment StartX=2.06757 StartY=-2 StartZ=0 EndX=2.06757 EndY=-4.12277 EndZ=0
    g7: LineSegment StartX=2.06757 StartY=-4.12277 StartZ=0 EndX=3.6 EndY=-4.12277 EndZ=0
  constraints (21):
    c: Coincident(g0,g1)
    c: Coincident(g1,g2)
    c: Coincident(g2,g3)
    c: Coincident(g3,g0)
    c: Horizontal(g0)
    c: Horizontal(g2)
    c: Vertical(g1)
    c: Vertical(g3)
    c: Distance(g0) = 0.5
    c: Distance(g1) = 4
    c: DistanceY(g-1,g0) = 2
    c: DistanceX(g0) = 3.6
    c: Coincident(g4,g1)
    c: Vertical(g4)
    c: Coincident(g5,g3)
    c: Horizontal(g5)
    c: Coincident(g6,g5)
    c: Vertical(g6)
    c: Coincident(g7,g6)
    c: Coincident(g7,g4)
    c: Horizontal(g7)
FEATURE [PartDesign::Pocket] Pocket088
  BaseFeature = -> Pad121
  Length = 1.99
  Length2 = 100
  Profile = -> Sketch221
  Type = 0
FEATURE [Sketcher::SketchObject] Sketch222
  ExternalGeometry = -> [Pocket088]
  MapMode = 5
  Placement = pos=(0,0,-0.01) rot=(1,0,0;3.14159rad)
  Support = -> [Pocket088]
  sketch-geometry (5):
    g0: LineSegment StartX=3.1 StartY=0.8 StartZ=0 EndX=3.6 EndY=0.8 EndZ=0
    g1: LineSegment StartX=3.6 StartY=-0.8 StartZ=0 EndX=3.1 EndY=-0.8 EndZ=0
    g2: LineSegment StartX=3.1 StartY=-0.8 StartZ=0 EndX=3.1 EndY=0.8 EndZ=0
    g3: LineSegment StartX=3.6 StartY=0.8 StartZ=0 EndX=3.6 EndY=0 EndZ=0
    g4: LineSegment StartX=3.6 StartY=0 StartZ=0 EndX=3.6 EndY=-0.8 EndZ=0
  constraints (15):
    c: Coincident(g1,g2)
    c: Coincident(g2,g0)
    c: Horizontal(g0)
    c: Horizontal(g1)
    c: Vertical(g2)
    c: PointOnObject(g0,g-4)
    c: PointOnObject(g1,g-3)
    c: Coincident(g3,g0)
    c: PointOnObject(g3,g-1)
    c: Vertical(g3)
    c: Coincident(g4,g3)
    c: Coincident(g4,g1)
    c: Vertical(g4)
    c: Equal(g3,g4)
    c: Distance(g2) = 1.6
FEATURE [PartDesign::Pocket] Pocket089
  BaseFeature = -> Pocket088
  Length = 5
  Length2 = 100
  Profile = -> Sketch222
  Type = 1
FEATURE [PartDesign::PolarPattern] PolarPattern004
  Angle = 360
  Axis = -> Z_Axis073
  Occurrences = 2
FEATURE [PartDesign::MultiTransform] MultiTransform004
  BaseFeature = -> Pocket089
  Originals = -> [Pad121,Pocket088,Pocket089]
  Transformations = -> [PolarPattern004]
FEATURE [Sketcher::SketchObject] Sketch223
  MapMode = 5
  Placement = pos=(0,0,0) rot=(1,0,0;3.14159rad)
  Support = -> [MultiTransform004]
  sketch-geometry (1):
    g0: Circle CenterX=0 CenterY=0 CenterZ=0 NormalX=0 NormalY=0 NormalZ=1 AngleXU=0 Radius=1.5
  constraints (2):
    c: Coincident(g0,g-1)
    c: Radius(g0) = 1.5
FEATURE [PartDesign::Pocket] Pocket090
  BaseFeature = -> MultiTransform004
  Length = 1
  Length2 = 100
  Profile = -> Sketch223
  Type = 0
FEATURE [Sketcher::SketchObject] Sketch224
  ExternalGeometry = -> [Pocket090]
  MapMode = 5
  Placement = pos=(0,0,2) rot=(0,0,1;0rad)
  Support = -> [Pocket090]
  sketch-geometry (1):
    g0: Circle CenterX=0 CenterY=0 CenterZ=0 NormalX=0 NormalY=0 NormalZ=1 AngleXU=0 Radius=2
  constraints (2):
    c: Coincident(g0,g-1)
    c: Equal(g-3,g0)
FEATURE [PartDesign::Pocket] Pocket091
  BaseFeature = -> Pocket090
  Length = 1
  Length2 = 100
  Profile = -> Sketch224
  Type = 0
FEATURE [PartDesign::Body] Body065
  Group = -> [Sketch217,Pad119,Mirrored020,Sketch218,Pad120,Sketch219,Pocket087,Sketch220,Pad121,Sketch221,Pocket088,Sketch222,Pocket089,MultiTransform004,PolarPattern004,Sketch223,Pocket090,Sketch224,Pocket091]
  Origin = -> Origin073
  Tip = -> Pocket091
FEATURE [Sketcher::SketchObject] Sketch225
  MapMode = 5
  Support = -> [XY_Plane012]
  sketch-geometry (8):
    g0: ArcOfCircle CenterX=0 CenterY=0 CenterZ=0 NormalX=0 NormalY=0 NormalZ=1 AngleXU=0 Radius=5 StartAngle=5.35589 EndAngle=7.21048
    g1: ArcOfCircle CenterX=0 CenterY=0 CenterZ=0 NormalX=0 NormalY=0 NormalZ=1 AngleXU=0 Radius=5 StartAngle=2.2143 EndAngle=4.06889
    g2: LineSegment StartX=-3 StartY=-4 StartZ=0 EndX=3 EndY=-4 EndZ=0
    g3: LineSegment StartX=-3 StartY=4 StartZ=0 EndX=3 EndY=4 EndZ=0
    g4: ArcOfCircle CenterX=0 CenterY=0 CenterZ=0 NormalX=0 NormalY=0 NormalZ=1 AngleXU=0 Radius=5.8 StartAngle=2.1668 EndAngle=4.11639
    g5: ArcOfCircle CenterX=0 CenterY=0 CenterZ=0 NormalX=0 NormalY=0 NormalZ=1 AngleXU=0 Radius=5.8 StartAngle=5.30839 EndAngle=7.25798
    g6: LineSegment StartX=-3.25576 StartY=-4.8 StartZ=0 EndX=3.25576 EndY=-4.8 EndZ=0
    g7: LineSegment StartX=-3.25576 StartY=4.8 StartZ=0 EndX=3.25576 EndY=4.8 EndZ=0
  constraints (24):
    c: Coincident(g0,g-1)
    c: Coincident(g1,g0)
    c: Coincident(g2,g1)
    c: Coincident(g2,g0)
    c: Horizontal(g2)
    c: Coincident(g3,g1)
    c: Coincident(g3,g0)
    c: Horizontal(g3)
    c: Equal(g0,g1)
    c: Radius(g0) = 5
    c: Equal(g3,g2)
    c: DistanceY(g0,g0) = 8
    c: Coincident(g4,g0)
    c: Coincident(g5,g0)
    c: Coincident(g6,g4)
    c: Coincident(g6,g5)
    c: Horizontal(g6)
    c: Coincident(g7,g4)
    c: Coincident(g7,g5)
    c: Horizontal(g7)
    c: Equal(g4,g5)
    c: Equal(g6,g7)
    c: Radius(g4) = 5.8
    c: DistanceY(g4,g1) = 0.8
FEATURE [PartDesign::Pad] Pad036
  Length = 3.4
  Length2 = 100
  Profile = -> Sketch225
  Type = 0
FEATURE [Sketcher::SketchObject] Sketch226
  ExternalGeometry = -> [Pad036]
  MapMode = 5
  Placement = pos=(0,0,3.4) rot=(0,0,1;0rad)
  Support = -> [Pad036]
  sketch-geometry (3):
    g0: ArcOfCircle CenterX=0 CenterY=0 CenterZ=0 NormalX=0 NormalY=0 NormalZ=1 AngleXU=0 Radius=5 StartAngle=2.2143 EndAngle=2.94023
    g1: LineSegment StartX=-3 StartY=4 StartZ=0 EndX=-1 EndY=4 EndZ=0
    g2: LineSegment StartX=-4.89898 StartY=1 StartZ=0 EndX=-1 EndY=4 EndZ=0
  constraints (8):
    c: Coincident(g0,g-1)
    c: Coincident(g0,g-6)
    c: Coincident(g1,g0)
    c: PointOnObject(g1,g-3)
    c: Coincident(g2,g0)
    c: Coincident(g2,g1)
    c: Distance(g1) = 2
    c: DistanceY(g0,g0) = 1
FEATURE [PartDesign::Pad] Pad122
  BaseFeature = -> Pad036
  Length = 2.4
  Length2 = 100
  Profile = -> Sketch226
  Reversed = true
  Type = 0
FEATURE [PartDesign::PolarPattern] PolarPattern006
  Angle = 360
  Axis = -> Z_Axis012
  Occurrences = 2
FEATURE [PartDesign::Mirrored] Mirrored021
  MirrorPlane = -> YZ_Plane012
FEATURE [PartDesign::MultiTransform] MultiTransform008
  BaseFeature = -> Pad122
  Originals = -> [Pad122]
  Transformations = -> [PolarPattern006,Mirrored021]
FEATURE [Sketcher::SketchObject] Sketch227
  ExternalGeometry = -> [MultiTransform008]
  MapMode = 5
  Placement = pos=(0,0,3.4) rot=(0,0,1;0rad)
  Support = -> [MultiTransform008]
  sketch-geometry (4):
    g0: LineSegment StartX=3 StartY=-4 StartZ=0 EndX=-3 EndY=-4 EndZ=0
    g1: LineSegment StartX=-3 StartY=4 StartZ=0 EndX=3 EndY=4 EndZ=0
    g2: ArcOfCircle CenterX=0 CenterY=0 CenterZ=0 NormalX=0 NormalY=0 NormalZ=1 AngleXU=0 Radius=5 StartAngle=5.35589 EndAngle=7.21048
    g3: ArcOfCircle CenterX=0 CenterY=0 CenterZ=0 NormalX=0 NormalY=0 NormalZ=1 AngleXU=0 Radius=5 StartAngle=2.2143 EndAngle=4.06889
  constraints (10):
    c: Coincident(g0,g-4)
    c: Horizontal(g0)
    c: Coincident(g1,g-3)
    c: Horizontal(g1)
    c: Coincident(g2,g-1)
    c: Coincident(g2,g1)
    c: Coincident(g2,g0)
    c: Coincident(g3,g2)
    c: Coincident(g3,g1)
    c: Coincident(g3,g0)
FEATURE [PartDesign::Pad] Pad123
  BaseFeature = -> MultiTransform008
  Length = 0.4
  Length2 = 100
  Profile = -> Sketch227
  Reversed = true
  Type = 0
FEATURE [Sketcher::SketchObject] Sketch079
  MapMode = 5
  Placement = pos=(0,0,3.4) rot=(0,0,1;0rad)
  Support = -> [Pad123]
  sketch-geometry (5):
    g0: LineSegment StartX=-3.1 StartY=3.8 StartZ=0 EndX=3.1 EndY=3.8 EndZ=0
    g1: LineSegment StartX=3.1 StartY=3.8 StartZ=0 EndX=3.1 EndY=1.6 EndZ=0
    g2: LineSegment StartX=-3.1 StartY=1.6 StartZ=0 EndX=-3.1 EndY=3.8 EndZ=0
    g3: LineSegment StartX=-3.1 StartY=1.6 StartZ=0 EndX=0 EndY=1.6 EndZ=0
    g4: LineSegment StartX=3.1 StartY=1.6 StartZ=0 EndX=0 EndY=1.6 EndZ=0
  constraints (15):
    c: Coincident(g0,g1)
    c: Coincident(g2,g0)
    c: Horizontal(g0)
    c: Vertical(g1)
    c: Vertical(g2)
    c: Coincident(g3,g2)
    c: PointOnObject(g3,g-2)
    c: Horizontal(g3)
    c: Coincident(g4,g1)
    c: Coincident(g4,g3)
    c: Horizontal(g4)
    c: Equal(g4,g3)
    c: Distance(g0) = 6.2
    c: Distance(g1) = 2.2
    c: DistanceY(g-1,g1) = 1.6
FEATURE [PartDesign::Pocket] Pocket092
  BaseFeature = -> Pad123
  Length = 5
  Length2 = 100
  Profile = -> Sketch079
  Type = 1
FEATURE [Sketcher::SketchObject] Sketch080
  ExternalGeometry = -> [Pocket092]
  MapMode = 5
  Placement = pos=(0,0,3.4) rot=(0,0,1;0rad)
  Support = -> [Pocket092]
  sketch-geometry (4):
    g0: ArcOfCircle CenterX=0 CenterY=0 CenterZ=0 NormalX=0 NormalY=0 NormalZ=1 AngleXU=0 Radius=5.8 StartAngle=5.30839 EndAngle=7.25798
    g1: ArcOfCircle CenterX=0 CenterY=0 CenterZ=0 NormalX=0 NormalY=0 NormalZ=1 AngleXU=0 Radius=5.8 StartAngle=2.1668 EndAngle=4.11639
    g2: LineSegment StartX=-3.25576 StartY=4.8 StartZ=0 EndX=3.25576 EndY=4.8 EndZ=0
    g3: LineSegment StartX=-3.25576 StartY=-4.8 StartZ=0 EndX=3.25576 EndY=-4.8 EndZ=0
  constraints (10):
    c: Coincident(g0,g-1)
    c: Coincident(g0,g-4)
    c: Coincident(g1,g0)
    c: Coincident(g1,g-3)
    c: Coincident(g2,g1)
    c: Coincident(g2,g0)
    c: Horizontal(g2)
    c: Coincident(g3,g1)
    c: Coincident(g3,g0)
    c: Horizontal(g3)
FEATURE [PartDesign::Pad] Pad124
  BaseFeature = -> Pocket092
  Length = 1
  Length2 = 100
  Profile = -> Sketch080
  Type = 0
FEATURE [Sketcher::SketchObject] Sketch081
  MapMode = 5
  Placement = pos=(0,0,4.4) rot=(0,0,1;0rad)
  Support = -> [Pad124]
  sketch-geometry (5):
    g0: LineSegment StartX=3.5 StartY=6 StartZ=0 EndX=3.5 EndY=1 EndZ=0
    g1: LineSegment StartX=3.5 StartY=1 StartZ=0 EndX=-3.5 EndY=1 EndZ=0
    g2: LineSegment StartX=-3.5 StartY=1 StartZ=0 EndX=-3.5 EndY=6 EndZ=0
    g3: LineSegment StartX=-3.5 StartY=6 StartZ=0 EndX=0 EndY=6 EndZ=0
    g4: LineSegment StartX=3.5 StartY=6 StartZ=0 EndX=0 EndY=6 EndZ=0
  constraints (15):
    c: Coincident(g0,g1)
    c: Coincident(g1,g2)
    c: Horizontal(g1)
    c: Vertical(g0)
    c: Vertical(g2)
    c: Coincident(g3,g2)
    c: PointOnObject(g3,g-2)
    c: Horizontal(g3)
    c: Coincident(g4,g0)
    c: Coincident(g4,g3)
    c: Horizontal(g4)
    c: Equal(g3,g4)
    c: DistanceY(g-1,g0) = 1
    c: Distance(g1) = 7
    c: Distance(g2) = 5
FEATURE [PartDesign::Pocket] Pocket093
  BaseFeature = -> Pad124
  Length = 1
  Length2 = 100
  Profile = -> Sketch081
  Type = 0
FEATURE [Sketcher::SketchObject] Sketch082
  MapMode = 5
  Support = -> [XY_Plane012]
  sketch-geometry (5):
    g0: LineSegment StartX=-5.98925 StartY=0.75 StartZ=0 EndX=6.01075 EndY=0.75 EndZ=0
    g1: LineSegment StartX=6.01075 StartY=-0.75 StartZ=0 EndX=-5.98925 EndY=-0.75 EndZ=0
    g2: LineSegment StartX=-5.98925 StartY=-0.75 StartZ=0 EndX=-5.98925 EndY=0.75 EndZ=0
    g3: LineSegment StartX=6.01075 StartY=0.75 StartZ=0 EndX=6.01075 EndY=0 EndZ=0
    g4: LineSegment StartX=6.01075 StartY=-0.75 StartZ=0 EndX=6.01075 EndY=0 EndZ=0
  constraints (14):
    c: Coincident(g1,g2)
    c: Coincident(g2,g0)
    c: Horizontal(g0)
    c: Horizontal(g1)
    c: Vertical(g2)
    c: Coincident(g3,g0)
    c: PointOnObject(g3,g-1)
    c: Vertical(g3)
    c: Coincident(g4,g1)
    c: Coincident(g4,g3)
    c: Vertical(g4)
    c: Equal(g4,g3)
    c: Distance(g0) = 12
    c: Distance(g2) = 1.5
FEATURE [PartDesign::Pocket] Pocket041
  BaseFeature = -> Pocket093
  Length = 1.99
  Length2 = 100
  Profile = -> Sketch082
  Reversed = true
  Type = 0
FEATURE [PartDesign::Fillet] Fillet034
  Base = -> Pocket041 [Edge83,Edge87,Edge32]
  BaseFeature = -> Pocket041
  Radius = 0.5
  SupportTransform = true
FEATURE [PartDesign::Body] Body012
  Group = -> [Sketch225,Pad036,Sketch226,Pad122,MultiTransform008,PolarPattern006,Mirrored021,Sketch227,Pad123,Sketch079,Pocket092,Sketch080,Pad124,Sketch081,Pocket093,Sketch082,Pocket041,Fillet034]
  Origin = -> Origin012
  Tip = -> Fillet034
FEATURE [App::Part] Part008
  Group = -> [Body064,Body065,Body012]
  Origin = -> Origin074
FEATURE [PartDesign::FeatureBase] Clone037
  BaseFeature = -> Body064
FEATURE [PartDesign::Body] Body066
  BaseFeature = -> Body064
  Group = -> [Clone037]
  Origin = -> Origin075
  Tip = -> Clone037
FEATURE [PartDesign::FeatureBase] Clone038
  BaseFeature = -> Body065
FEATURE [PartDesign::Body] Body067
  BaseFeature = -> Body065
  Group = -> [Clone038]
  Origin = -> Origin076
  Tip = -> Clone038
FEATURE [PartDesign::FeatureBase] Clone039
  BaseFeature = -> Body012
FEATURE [PartDesign::Body] Body068
  BaseFeature = -> Body012
  Group = -> [Clone039]
  Origin = -> Origin077
  Placement = pos=(12,0,-23) rot=(0.707107,-0.707107,0;3.14159rad)
  Tip = -> Clone039
FEATURE [App::Part] Part009
  Group = -> [Body066,Body067]
  Origin = -> Origin078
  Placement = pos=(12,4e-16,-23) rot=(0.707107,-0.707107,0;3.14159rad)
FEATURE [PartDesign::FeatureBase] Clone040
  BaseFeature = -> Body012
FEATURE [PartDesign::Body] Body069
  BaseFeature = -> Body012
  Group = -> [Clone040]
  Origin = -> Origin080
  Placement = pos=(-43,0,-32) rot=(0.57735,-0.57735,-0.57735;2.0944rad)
  Tip = -> Clone040
FEATURE [PartDesign::FeatureBase] Clone041
  BaseFeature = -> Body064
FEATURE [PartDesign::Body] Body070
  BaseFeature = -> Body064
  Group = -> [Clone041]
  Origin = -> Origin079
  Tip = -> Clone041
FEATURE [PartDesign::FeatureBase] Clone042
  BaseFeature = -> Body065
FEATURE [PartDesign::Body] Body071
  BaseFeature = -> Body065
  Group = -> [Clone042]
  Origin = -> Origin081
  Tip = -> Clone042
FEATURE [App::Part] Part010
  Group = -> [Body070,Body071]
  Origin = -> Origin082
  Placement = pos=(-43,-9.8e-15,-32) rot=(-0.57735,0.57735,0.57735;4.18879rad)
FEATURE [PartDesign::FeatureBase] Clone043
  BaseFeature = -> Body012
FEATURE [PartDesign::Body] Body072
  BaseFeature = -> Body012
  Group = -> [Clone043]
  Origin = -> Origin084
  Placement = pos=(0,12,-68) rot=(0,1,0;3.14159rad)
  Tip = -> Clone043
FEATURE [PartDesign::FeatureBase] Clone044
  BaseFeature = -> Body064
FEATURE [PartDesign::Body] Body073
  BaseFeature = -> Body064
  Group = -> [Clone044]
  Origin = -> Origin083
  Tip = -> Clone044
FEATURE [PartDesign::FeatureBase] Clone045
  BaseFeature = -> Body065
FEATURE [PartDesign::Body] Body074
  BaseFeature = -> Body065
  Group = -> [Clone045]
  Origin = -> Origin085
  Tip = -> Clone045
FEATURE [App::Part] Part011
  Group = -> [Body073,Body074]
  Origin = -> Origin086
  Placement = pos=(-1.01e-14,12,-68) rot=(0,-1,0;3.14159rad)
FEATURE [Sketcher::SketchObject] Sketch228
  MapMode = 5
  Support = -> [XY_Plane087]
  expr: Constraints[1] = 16.4 / 2
  sketch-geometry (1):
    g0: Circle CenterX=0 CenterY=0 CenterZ=0 NormalX=0 NormalY=0 NormalZ=1 AngleXU=0 Radius=8.2
  constraints (2):
    c: Coincident(g0,g-1)
    c: Radius(g0) = 8.2
FEATURE [PartDesign::Pad] Pad125
  AllowMultiFace = false
  Length = 3.3
  Length2 = 100
  Profile = -> Sketch228
  Type = 0
FEATURE [Sketcher::SketchObject] Sketch229
  MapMode = 5
  Placement = pos=(0,0,3.3) rot=(0,0,1;0rad)
  Support = -> [Pad125]
  expr: Constraints[15] = 16.4 / 2 - 1.5
  sketch-geometry (6):
    g0: ArcOfCircle CenterX=0 CenterY=0 CenterZ=0 NormalX=0 NormalY=0 NormalZ=1 AngleXU=0 Radius=6.7 StartAngle=5.73992 EndAngle=7.58746
    g1: ArcOfCircle CenterX=0 CenterY=0 CenterZ=0 NormalX=0 NormalY=0 NormalZ=1 AngleXU=0 Radius=6.7 StartAngle=2.59833 EndAngle=4.44587
    g2: LineSegment StartX=-5.73538 StartY=3.46344 StartZ=0 EndX=1.76462 EndY=3.46344 EndZ=0
    g3: LineSegment StartX=1.76462 StartY=3.46344 StartZ=0 EndX=1.76462 EndY=6.46344 EndZ=0
    g4: LineSegment StartX=5.73538 StartY=-3.46344 StartZ=0 EndX=-1.76462 EndY=-3.46344 EndZ=0
    g5: LineSegment StartX=-1.76462 StartY=-3.46344 StartZ=0 EndX=-1.76462 EndY=-6.46344 EndZ=0
  constraints (18):
    c: Coincident(g0,g-1)
    c: Coincident(g1,g0)
    c: Equal(g0,g1)
    c: Coincident(g2,g1)
    c: Horizontal(g2)
    c: Coincident(g3,g2)
    c: Coincident(g3,g0)
    c: Coincident(g4,g0)
    c: Horizontal(g4)
    c: Coincident(g5,g4)
    c: Coincident(g5,g1)
    c: Vertical(g3)
    c: Vertical(g5)
    c: Equal(g5,g3)
    c: Equal(g4,g2)
    c: Radius(g0) = 6.7
    c: Distance(g2) = 7.5
    c: Distance(g3) = 3
FEATURE [PartDesign::Pocket] Pocket094
  AllowMultiFace = false
  BaseFeature = -> Pad125
  Length = 2.4
  Length2 = 100
  Profile = -> Sketch229
  Type = 0
FEATURE [Sketcher::SketchObject] Sketch230
  ExternalGeometry = -> [Pocket094]
  MapMode = 5
  Placement = pos=(0,0,3.3) rot=(0,0,1;0rad)
  Support = -> [Pocket094]
  sketch-geometry (4):
    g0: LineSegment StartX=-1.57238 StartY=4.96344 StartZ=0 EndX=1.76462 EndY=3.90778 EndZ=0
    g1: LineSegment StartX=-1.57238 StartY=4.96344 StartZ=0 EndX=-1.34617 EndY=5.67852 EndZ=0
    g2: LineSegment StartX=-1.34617 StartY=5.67852 StartZ=0 EndX=1.76462 EndY=4.69442 EndZ=0
    g3: LineSegment StartX=1.76462 StartY=4.69442 StartZ=0 EndX=1.76462 EndY=3.90778 EndZ=0
  constraints (11):
    c: Coincident(g1,g0)
    c: Coincident(g2,g1)
    c: Coincident(g3,g2)
    c: Coincident(g3,g0)
    c: PointOnObject(g2,g-3)
    c: PointOnObject(g0,g-3)
    c: Perpendicular(g2,g1)
    c: Parallel(g0,g2)
    c: Distance(g0) = 3.5
    c: DistanceY(g-3,g0) = 1.5
    c: Distance(g1) = 0.75
FEATURE [PartDesign::Pocket] Pocket095
  AllowMultiFace = false
  BaseFeature = -> Pocket094
  Length = 2
  Length2 = 100
  Profile = -> Sketch230
  Type = 0
FEATURE [PartDesign::PolarPattern] PolarPattern007
  Angle = 360
  Axis = -> Sketch230 [N_Axis]
  BaseFeature = -> Pocket095
  Occurrences = 2
  Originals = -> [Pocket095]
FEATURE [Sketcher::SketchObject] Sketch231
  ExternalGeometry = -> [PolarPattern007]
  MapMode = 5
  Placement = pos=(0,0,3.3) rot=(0,0,1;0rad)
  Support = -> [PolarPattern007]
  sketch-geometry (14):
    g0: LineSegment StartX=-2.26274 StartY=-4.80833 StartZ=0 EndX=-4.80833 EndY=-2.26274 EndZ=0
    g1: LineSegment StartX=-4.80833 StartY=-2.26274 StartZ=0 EndX=-6.92965 EndY=-4.38406 EndZ=0
    g2: LineSegment [constr] StartX=-6.92965 StartY=-4.38406 StartZ=0 EndX=-4.38406 EndY=-6.92965 EndZ=0
    g3: LineSegment StartX=-4.38406 StartY=-6.92965 StartZ=0 EndX=-2.26274 EndY=-4.80833 EndZ=0
    g4: LineSegment StartX=-4.80833 StartY=2.26274 StartZ=0 EndX=-2.26274 EndY=4.80833 EndZ=0
    g5: LineSegment StartX=-2.26274 StartY=4.80833 StartZ=0 EndX=-4.38406 EndY=6.92965 EndZ=0
    g6: LineSegment [constr] StartX=-4.38406 StartY=6.92965 StartZ=0 EndX=-6.92965 EndY=4.38406 EndZ=0
    g7: LineSegment StartX=-6.92965 StartY=4.38406 StartZ=0 EndX=-4.80833 EndY=2.26274 EndZ=0
    g8: LineSegment StartX=-4.38406 StartY=6.92965 StartZ=0 EndX=-5.09117 EndY=7.63675 EndZ=0
    g9: LineSegment StartX=-6.92965 StartY=4.38406 StartZ=0 EndX=-7.63675 EndY=5.09117 EndZ=0
    g10: LineSegment StartX=-5.09117 StartY=7.63675 StartZ=0 EndX=-7.63675 EndY=5.09117 EndZ=0
    g11: LineSegment StartX=-6.92965 StartY=-4.38406 StartZ=0 EndX=-7.63675 EndY=-5.09117 EndZ=0
    g12: LineSegment StartX=-7.63675 StartY=-5.09117 StartZ=0 EndX=-5.09117 EndY=-7.63675 EndZ=0
    g13: LineSegment StartX=-4.38406 StartY=-6.92965 StartZ=0 EndX=-5.09117 EndY=-7.63675 EndZ=0
  constraints (40):
    c: Coincident(g0,g1)
    c: Coincident(g1,g2)
    c: Coincident(g2,g3)
    c: Coincident(g3,g0)
    c: Distance(g2) = 3.6
    c: Distance(g1) = 3
    c: Perpendicular(g2,g1)
    c: Parallel(g1,g3)
    c: Parallel(g2,g0)
    c: PointOnObject(g2,g-3)
    c: PointOnObject(g1,g-3)
    c: Coincident(g4,g5)
    c: Coincident(g5,g6)
    c: Coincident(g6,g7)
    c: Coincident(g7,g4)
    c: Equal(g2,g6) = 3.6
    c: Equal(g1,g5) = 2.9
    c: Perpendicular(g6,g5)
    c: Parallel(g5,g7)
    c: Parallel(g6,g4)
    c: PointOnObject(g5,g-3)
    c: PointOnObject(g6,g-3)
    c: Parallel(g1,g4)
    c: Coincident(g8,g5)
    c: Coincident(g9,g7)
    c: Coincident(g10,g9)
    c: Coincident(g10,g8)
    c: Parallel(g8,g5)
    c: Parallel(g9,g7)
    c: Parallel(g4,g10)
    c: Coincident(g12,g13)
    c: Coincident(g11,g12)
    c: Coincident(g11,g1)
    c: Coincident(g13,g3)
    c: Parallel(g13,g3)
    c: Parallel(g11,g1)
    c: Parallel(g12,g0)
    c: Equal(g11,g9)
    c: Distance(g9) = 1
    c: Angle(g5,g-1) = 0.785398
FEATURE [PartDesign::Pocket] Pocket096
  AllowMultiFace = false
  BaseFeature = -> PolarPattern007
  Length = 2.4
  Length2 = 100
  Profile = -> Sketch231
  Type = 0
FEATURE [Sketcher::SketchObject] Sketch232
  MapMode = 5
  Placement = pos=(0,0,0) rot=(1,0,0;3.14159rad)
  Support = -> [Pocket096]
  sketch-geometry (1):
    g0: Circle CenterX=0 CenterY=0 CenterZ=0 NormalX=0 NormalY=0 NormalZ=1 AngleXU=0 Radius=1.1
  constraints (2):
    c: Coincident(g0,g-1)
    c: Radius(g0) = 1.1
FEATURE [PartDesign::Pocket] Pocket097
  AllowMultiFace = false
  BaseFeature = -> Pocket096
  Length = 5
  Length2 = 100
  Profile = -> Sketch232
  Type = 1
FEATURE [Sketcher::SketchObject] Sketch233
  ExternalGeometry = -> [Sketch231]
  MapMode = 5
  Support = -> [XY_Plane087]
  expr: Constraints[20] = (3.6 - 2.3) / 2 - 0.3
  expr: Constraints[21] = (3.6 - 2.3) / 2 - 0.3
  sketch-geometry (18):
    g0: LineSegment StartX=-4.56084 StartY=-2.51023 StartZ=0 EndX=-4.9851 EndY=-2.93449 EndZ=0
    g1: LineSegment StartX=-4.9851 StartY=-2.93449 StartZ=0 EndX=-4.20729 EndY=-3.71231 EndZ=0
    g2: LineSegment StartX=-4.20729 StartY=-3.71231 StartZ=0 EndX=-3.78302 EndY=-3.28805 EndZ=0
    g3: LineSegment StartX=-3.78302 StartY=-3.28805 StartZ=0 EndX=-4.56084 EndY=-2.51023 EndZ=0
    g4: LineSegment StartX=-3.71231 StartY=-4.20729 StartZ=0 EndX=-2.93449 EndY=-4.9851 EndZ=0
    g5: LineSegment StartX=-3.28805 StartY=-3.78302 StartZ=0 EndX=-3.71231 EndY=-4.20729 EndZ=0
    g6: LineSegment StartX=-2.93449 StartY=-4.9851 StartZ=0 EndX=-2.51023 EndY=-4.56084 EndZ=0
    g7: LineSegment StartX=-2.51023 StartY=-4.56084 StartZ=0 EndX=-3.28805 EndY=-3.78302 EndZ=0
    g8: LineSegment StartX=-5.33866 StartY=-5.83363 StartZ=0 EndX=-4.56084 EndY=-6.61145 EndZ=0
    g9: LineSegment StartX=-4.91439 StartY=-5.40937 StartZ=0 EndX=-5.33866 EndY=-5.83363 EndZ=0
    g10: LineSegment StartX=-4.56084 StartY=-6.61145 StartZ=0 EndX=-4.13657 EndY=-6.18718 EndZ=0
    g11: LineSegment StartX=-4.13657 StartY=-6.18718 StartZ=0 EndX=-4.91439 EndY=-5.40937 EndZ=0
    g12: LineSegment StartX=-6.61145 StartY=-4.56084 StartZ=0 EndX=-5.83363 EndY=-5.33866 EndZ=0
    g13: LineSegment StartX=-5.83363 StartY=-5.33866 StartZ=0 EndX=-5.40937 EndY=-4.91439 EndZ=0
    g14: LineSegment StartX=-6.18718 StartY=-4.13657 StartZ=0 EndX=-6.61145 EndY=-4.56084 EndZ=0
    g15: LineSegment StartX=-5.40937 StartY=-4.91439 StartZ=0 EndX=-6.18718 EndY=-4.13657 EndZ=0
    g16: LineSegment [constr] StartX=-3.71231 StartY=-4.20729 StartZ=0 EndX=-4.91439 EndY=-5.40937 EndZ=0
    g17: LineSegment [constr] StartX=-4.9851 StartY=-2.93449 StartZ=0 EndX=-6.18718 EndY=-4.13657 EndZ=0
  constraints (52):
    c: Coincident(g0,g1)
    c: Coincident(g1,g2)
    c: Coincident(g2,g3)
    c: Coincident(g3,g0)
    c: Parallel(g3,g1)
    c: Parallel(g0,g2)
    c: Perpendicular(g3,g2)
    c: Parallel(g3,g-3)
    c: Coincident(g5,g4)
    c: Coincident(g4,g6)
    c: Coincident(g6,g7)
    c: Coincident(g7,g5)
    c: Parallel(g7,g4)
    c: Parallel(g5,g6)
    c: Perpendicular(g7,g6)
    c: Equal(g2,g5)
    c: Equal(g7,g3)
    c: PointOnObject(g6,g-3)
    c: Parallel(g7,g-3)
    c: PointOnObject(g2,g-3)
    c: Distance(g-3,g0) = 0.35
    c: Distance(g6,g-4) = 0.35
    c: Distance(g4) = 1.1
    c: Distance(g0) = 0.6
    c: Coincident(g9,g8)
    c: Coincident(g8,g10)
    c: Coincident(g10,g11)
    c: Coincident(g11,g9)
    c: Parallel(g11,g8)
    c: Parallel(g9,g10)
    c: Perpendicular(g11,g10)
    c: Equal(g4,g8) = 0.5
    c: Coincident(g14,g12)
    c: Coincident(g12,g13)
    c: Coincident(g13,g15)
    c: Coincident(g15,g14)
    c: Parallel(g15,g12)
    c: Parallel(g14,g13)
    c: Perpendicular(g15,g13)
    c: Parallel(g15,g1)
    c: Equal(g9,g5)
    c: Equal(g13,g9)
    c: Equal(g15,g11)
    c: Parallel(g11,g4)
    c: Coincident(g16,g4)
    c: Coincident(g16,g9)
    c: Coincident(g17,g0)
    c: Coincident(g17,g14)
    c: Parallel(g0,g17)
    c: Parallel(g16,g5)
    c: Equal(g16,g17)
    c: Distance(g0,g12) = 2.9
FEATURE [PartDesign::Pocket] Pocket098
  AllowMultiFace = false
  BaseFeature = -> Pocket097
  Length = 5
  Length2 = 100
  Profile = -> Sketch233
  Reversed = true
  Type = 1
FEATURE [PartDesign::PolarPattern] PolarPattern008
  Angle = 90
  Axis = -> Sketch233 [N_Axis]
  BaseFeature = -> Pocket098
  Occurrences = 2
  Originals = -> [Pocket098]
  Reversed = true
FEATURE [Sketcher::SketchObject] Sketch234
  MapMode = 5
  Support = -> [XY_Plane087]
  expr: Constraints[2] = 9.6 / 2
  sketch-geometry (1):
    g0: Circle CenterX=0 CenterY=4.8 CenterZ=0 NormalX=0 NormalY=0 NormalZ=1 AngleXU=0 Radius=1
  constraints (3):
    c: PointOnObject(g0,g-2)
    c: Radius(g0) = 1
    c: Distance(g-1,g0) = 4.8
FEATURE [PartDesign::Pocket] Pocket099
  AllowMultiFace = false
  BaseFeature = -> PolarPattern008
  Length = 1
  Length2 = 100
  Profile = -> Sketch234
  Reversed = true
  Type = 2
FEATURE [PartDesign::Mirrored] Mirrored022
  BaseFeature = -> Pocket099
  MirrorPlane = -> XZ_Plane087
  Originals = -> [Pocket099]
FEATURE [Sketcher::SketchObject] Sketch235
  ExternalGeometry = -> [Mirrored022]
  MapMode = 5
  Placement = pos=(0,0,3.3) rot=(0,0,1;0rad)
  Support = -> [Mirrored022]
  sketch-geometry (4):
    g0: LineSegment StartX=-2.26274 StartY=4.80833 StartZ=0 EndX=-3.60762 EndY=4.80833 EndZ=0
    g1: LineSegment StartX=-3.60762 StartY=4.80833 StartZ=0 EndX=-3.60762 EndY=3.46344 EndZ=0
    g2: LineSegment StartX=-3.60762 StartY=3.46344 StartZ=0 EndX=-2.26274 EndY=3.46344 EndZ=0
    g3: LineSegment StartX=-2.26274 StartY=3.46344 StartZ=0 EndX=-2.26274 EndY=4.80833 EndZ=0
  constraints (10):
    c: Coincident(g0,g1)
    c: Coincident(g1,g2)
    c: Coincident(g2,g3)
    c: Coincident(g3,g0)
    c: Horizontal(g0)
    c: Horizontal(g2)
    c: Vertical(g1)
    c: Vertical(g3)
    c: Coincident(g0,g-3)
    c: Coincident(g1,g-4)
FEATURE [PartDesign::Pocket] Pocket100
  AllowMultiFace = false
  BaseFeature = -> Mirrored022
  Length = 0
  Length2 = 100
  Profile = -> Sketch235
  Type = 3
  UpToFace = -> Mirrored022 [Face9]
FEATURE [PartDesign::Body] Body075
  Group = -> [Sketch228,Pad125,Sketch229,Pocket094,Sketch230,Pocket095,PolarPattern007,Sketch231,Pocket096,Sketch232,Pocket097,Sketch233,Pocket098,PolarPattern008,Sketch234,Pocket099,Mirrored022,Sketch235,Pocket100]
  Origin = -> Origin087
  Tip = -> Pocket100
FEATURE [PartDesign::FeatureBase] Clone046
  BaseFeature = -> Body075
FEATURE [PartDesign::Body] Body076
  BaseFeature = -> Body075
  Group = -> [Clone046]
  Origin = -> Origin088
  Placement = pos=(60,-20,-203.8) rot=(0.57735,-0.57735,-0.57735;2.0944rad)
  Tip = -> Clone046
FEATURE [PartDesign::FeatureBase] Clone047
  BaseFeature = -> Body075
FEATURE [PartDesign::Body] Body077
  BaseFeature = -> Body075
  Group = -> [Clone047]
  Origin = -> Origin089
  Placement = pos=(60,-180,-203.8) rot=(0.57735,0.57735,-0.57735;4.18879rad)
  Tip = -> Clone047
FEATURE [PartDesign::FeatureBase] Clone048
  BaseFeature = -> Body075
FEATURE [PartDesign::Body] Body078
  BaseFeature = -> Body075
  Group = -> [Clone048]
  Origin = -> Origin090
  Placement = pos=(-1,-175.3,-223.8) rot=(0.57735,0.57735,-0.57735;2.0944rad)
  Tip = -> Clone048
FEATURE [Sketcher::SketchObject] Sketch237
  MapMode = 5
  Placement = pos=(0,0,0) rot=(1,0,0;1.5708rad)
  Support = -> [XZ_Plane092]
  sketch-geometry (10):
    g0: ArcOfCircle CenterX=0 CenterY=0 CenterZ=0 NormalX=0 NormalY=0 NormalZ=1 AngleXU=0 Radius=7.4 StartAngle=5.61996 EndAngle=7.38231
    g1: ArcOfCircle CenterX=0 CenterY=0 CenterZ=0 NormalX=0 NormalY=0 NormalZ=1 AngleXU=0 Radius=4.9 StartAngle=5.61996 EndAngle=7.38231
    g2: LineSegment StartX=3.86125 StartY=-3.01674 StartZ=0 EndX=5.83128 EndY=-4.55589 EndZ=0
    g3: ArcOfCircle [constr] CenterX=4.08061 CenterY=8 CenterZ=0 NormalX=0 NormalY=0 NormalZ=1 AngleXU=0 Radius=4.08061 StartAngle=3.14159 EndAngle=4.24071
    g4: ArcOfCircle CenterX=4.08061 CenterY=8 CenterZ=0 NormalX=0 NormalY=0 NormalZ=1 AngleXU=0 Radius=1.58061 StartAngle=3.14159 EndAngle=4.24071
    g5: LineSegment StartX=0 StartY=10 StartZ=0 EndX=2.5 EndY=10 EndZ=0
    g6: LineSegment StartX=2.5 StartY=10 StartZ=0 EndX=2.5 EndY=8 EndZ=0
    g7: ArcOfCircle CenterX=0 CenterY=5.91899 CenterZ=0 NormalX=0 NormalY=0 NormalZ=1 AngleXU=0 Radius=0.5 StartAngle=0.471596 EndAngle=1.5708
    g8: ArcOfCircle CenterX=4.08061 CenterY=8 CenterZ=0 NormalX=0 NormalY=0 NormalZ=1 AngleXU=0 Radius=4.08061 StartAngle=3.61319 EndAngle=4.24071
    g9: LineSegment StartX=0 StartY=6.41899 StartZ=0 EndX=0 EndY=10 EndZ=0
  constraints (29):
    c: Coincident(g0,g-1)
    c: Coincident(g1,g0)
    c: Coincident(g2,g1)
    c: Coincident(g2,g0)
    c: Perpendicular(g0,g2)
    c: Diameter(g1) = 9.8
    c: Distance(g2) = 2.5
    c: Angle(g2,g-2) = 2.23402
    c: Tangent(g3,g-2)
    c: PointOnObject(g3,g-2)
    c: Tangent(g3,g1) = 1.5708
    c: Coincident(g4,g3)
    c: Tangent(g4,g0) = 1.5708
    c: Horizontal(g5)
    c: Coincident(g6,g5)
    c: Vertical(g6)
    c: Distance(g6) = 2
    c: Tangent(g6,g4) = -1.5708
    c: DistanceY(g0,g5) = 10
    c: PointOnObject(g7,g-2)
    c: Tangent(g7,g3)
    c: Coincident(g8,g4)
    c: Coincident(g8,g1)
    c: Coincident(g8,g7)
    c: Radius(g7) = 0.5
    c: Coincident(g9,g7)
    c: Coincident(g9,g5)
    c: Vertical(g9)
    c: PointOnObject(g7,g-2)
FEATURE [PartDesign::Pad] Pad128
  Length = 1.8
  Length2 = 100
  Placement = pos=(0,0,0) rot=(1,0,0;1.5708rad)
  Profile = -> Sketch237
  Refine = true
  Reversed = true
  Type = 0
FEATURE [Sketcher::SketchObject] Sketch028
  MapMode = 5
  Placement = pos=(0,0,0) rot=(0.57735,0.57735,0.57735;2.0944rad)
  Support = -> [YZ_Plane092]
  sketch-geometry (8):
    g0: LineSegment StartX=-9 StartY=0 StartZ=0 EndX=9 EndY=0 EndZ=0
    g1: LineSegment StartX=-10 StartY=-1 StartZ=0 EndX=-10 EndY=-19 EndZ=0
    g2: LineSegment StartX=10 StartY=-1 StartZ=0 EndX=10 EndY=-19 EndZ=0
    g3: LineSegment StartX=-9 StartY=-20 StartZ=0 EndX=9 EndY=-20 EndZ=0
    g4: ArcOfCircle CenterX=-9 CenterY=-1 CenterZ=0 NormalX=0 NormalY=0 NormalZ=1 AngleXU=0 Radius=1 StartAngle=1.5708 EndAngle=3.14159
    g5: ArcOfCircle CenterX=9 CenterY=-1 CenterZ=0 NormalX=0 NormalY=0 NormalZ=1 AngleXU=0 Radius=1 StartAngle=0 EndAngle=1.5708
    g6: ArcOfCircle CenterX=-9 CenterY=-19 CenterZ=0 NormalX=0 NormalY=0 NormalZ=1 AngleXU=0 Radius=1 StartAngle=3.14159 EndAngle=4.71239
    g7: ArcOfCircle CenterX=9 CenterY=-19 CenterZ=0 NormalX=0 NormalY=0 NormalZ=1 AngleXU=0 Radius=1 StartAngle=4.71239 EndAngle=6.28319
  constraints (19):
    c: Vertical(g1)
    c: Vertical(g2)
    c: Horizontal(g3)
    c: Tangent(g0,g4) = 1.5708
    c: Tangent(g1,g4) = -1.5708
    c: Tangent(g0,g5) = 1.5708
    c: Tangent(g2,g5) = 1.5708
    c: Tangent(g1,g6) = -1.5708
    c: Tangent(g3,g6) = -1.5708
    c: Tangent(g2,g7) = 1.5708
    c: Tangent(g3,g7) = -1.5708
    c: Equal(g5,g7)
    c: Equal(g7,g6)
    c: Equal(g6,g4)
    c: Horizontal(g0)
    c: Symmetric(g0,g0,g-1)
    c: Radius(g5) = 1
    c: DistanceY(g3,g0) = 20
    c: DistanceX(g1,g2) = 20
FEATURE [Sketcher::SketchObject] Sketch243
  MapMode = 5
  Placement = pos=(0,0,0) rot=(0.57735,0.57735,0.57735;2.0944rad)
  Support = -> [YZ_Plane091]
  expr: Constraints[35] = 1 + 3.8 + 2
  expr: Constraints[34] = 2 + 2 * 0.2
  sketch-geometry (13):
    g0: LineSegment StartX=-40.2 StartY=6.81 StartZ=0 EndX=12.2 EndY=6.81 EndZ=0
    g1: LineSegment StartX=12.2 StartY=6.81 StartZ=0 EndX=12.2 EndY=-22.39 EndZ=0
    g2: LineSegment StartX=-40.2 StartY=-22.39 StartZ=0 EndX=-40.2 EndY=6.81 EndZ=0
    g3: LineSegment StartX=7.8 StartY=-22.39 StartZ=0 EndX=12.2 EndY=-22.39 EndZ=0
    g4: LineSegment StartX=-40.2 StartY=-22.39 StartZ=0 EndX=-7.8 EndY=-22.39 EndZ=0
    g5: LineSegment StartX=-10.2 StartY=0.01 StartZ=0 EndX=0 EndY=0.01 EndZ=0
    g6: LineSegment StartX=0 StartY=0.01 StartZ=0 EndX=10.2 EndY=0.01 EndZ=0
    g7: LineSegment StartX=10.2 StartY=0.01 StartZ=0 EndX=10.2 EndY=-20.39 EndZ=0
    g8: LineSegment StartX=10.2 StartY=-20.39 StartZ=0 EndX=7.8 EndY=-20.39 EndZ=0
    g9: LineSegment StartX=7.8 StartY=-22.39 StartZ=0 EndX=7.8 EndY=-20.39 EndZ=0
    g10: LineSegment StartX=-10.2 StartY=0.01 StartZ=0 EndX=-10.2 EndY=-20.39 EndZ=0
    g11: LineSegment StartX=-10.2 StartY=-20.39 StartZ=0 EndX=-7.8 EndY=-20.39 EndZ=0
    g12: LineSegment StartX=-7.8 StartY=-20.39 StartZ=0 EndX=-7.8 EndY=-22.39 EndZ=0
  constraints (39):
    c: Coincident(g0,g1)
    c: Coincident(g2,g0)
    c: Horizontal(g0)
    c: Vertical(g1)
    c: Vertical(g2)
    c: Coincident(g3,g1)
    c: Horizontal(g3)
    c: Coincident(g4,g2)
    c: Horizontal(g4)
    c: PointOnObject(g5,g-2)
    c: Horizontal(g5)
    c: Coincident(g6,g5)
    c: Horizontal(g6)
    c: Equal(g6,g5)
    c: Coincident(g7,g6)
    c: Vertical(g7)
    c: Coincident(g8,g7)
    c: Horizontal(g8)
    c: Coincident(g9,g3)
    c: Coincident(g9,g8)
    c: Vertical(g9)
    c: Coincident(g10,g5)
    c: Vertical(g10)
    c: Coincident(g11,g10)
    c: Horizontal(g11)
    c: Coincident(g12,g11)
    c: Coincident(g12,g4)
    c: Vertical(g12)
    c: Equal(g8,g11)
    c: Equal(g9,g12)
    c: DistanceX(g5,g6) = 20.4
    c: DistanceX(g6,g0) = 2
    c: Distance(g9) = 2
    c: DistanceY(g5) = 0.01
    c: Distance(g8) = 2.4
    c: DistanceY(g6,g0) = 6.8
    c: DistanceX(g0,g5) = 30
    c: Distance(g10) = 20.4
    c: Distance(g7) = 20.4
FEATURE [PartDesign::Pad] Pad130
  Length = 60
  Length2 = 100
  Midplane = true
  Placement = pos=(0,0,0) rot=(0.57735,0.57735,0.57735;2.0944rad)
  Profile = -> Sketch028
  Refine = true
  Type = 0
FEATURE [Sketcher::SketchObject] Sketch029
  MapMode = 5
  Placement = pos=(5.6e-15,-8.8e-15,-20) rot=(0.707107,0.707107,0;3.14159rad)
  Support = -> [Pad130]
  sketch-geometry (8):
    g0: LineSegment StartX=-7 StartY=28 StartZ=0 EndX=7 EndY=28 EndZ=0
    g1: LineSegment StartX=8 StartY=27 StartZ=0 EndX=8 EndY=-27 EndZ=0
    g2: LineSegment StartX=7 StartY=-28 StartZ=0 EndX=-7 EndY=-28 EndZ=0
    g3: LineSegment StartX=-8 StartY=-27 StartZ=0 EndX=-8 EndY=27 EndZ=0
    g4: ArcOfCircle CenterX=7 CenterY=27 CenterZ=0 NormalX=0 NormalY=0 NormalZ=1 AngleXU=0 Radius=1 StartAngle=-1.33e-14 EndAngle=1.5708
    g5: ArcOfCircle CenterX=-7 CenterY=27 CenterZ=0 NormalX=0 NormalY=0 NormalZ=1 AngleXU=0 Radius=1 StartAngle=1.5708 EndAngle=3.14159
    g6: ArcOfCircle CenterX=-7 CenterY=-27 CenterZ=0 NormalX=0 NormalY=0 NormalZ=1 AngleXU=0 Radius=1 StartAngle=3.14159 EndAngle=4.71239
    g7: ArcOfCircle CenterX=7 CenterY=-27 CenterZ=0 NormalX=0 NormalY=0 NormalZ=1 AngleXU=0 Radius=1 StartAngle=4.71239 EndAngle=6.28319
  constraints (19):
    c: Horizontal(g0)
    c: Horizontal(g2)
    c: Vertical(g1)
    c: Vertical(g3)
    c: Tangent(g0,g4) = 1.5708
    c: Tangent(g1,g4) = 1.5708
    c: Tangent(g0,g5) = 1.5708
    c: Tangent(g3,g5) = 1.5708
    c: Tangent(g3,g6) = 1.5708
    c: Tangent(g2,g6) = 1.5708
    c: Tangent(g1,g7) = 1.5708
    c: Tangent(g2,g7) = 1.5708
    c: Equal(g7,g6)
    c: Equal(g6,g5)
    c: Equal(g5,g4)
    c: Radius(g4) = 1
    c: DistanceX(g3,g1) = 16
    c: Symmetric(g0,g2,g-1)
    c: DistanceY(g2,g0) = 56
FEATURE [PartDesign::Pocket] Pocket109
  BaseFeature = -> Pad130
  Length = 18
  Length2 = 100
  Placement = pos=(0,0,0) rot=(0.57735,0.57735,0.57735;2.0944rad)
  Profile = -> Sketch029
  Refine = true
  Type = 0
FEATURE [Sketcher::SketchObject] Sketch030
  MapMode = 5
  Placement = pos=(0,0,1e-16) rot=(0,0,-1;1.5708rad)
  Support = -> [Pocket109]
  sketch-geometry (1):
    g0: Circle CenterX=0 CenterY=0 CenterZ=0 NormalX=0 NormalY=0 NormalZ=1 AngleXU=0 Radius=2.6
  constraints (2):
    c: Coincident(g0,g-1)
    c: Diameter(g0) = 5.2
FEATURE [PartDesign::Pocket] Pocket105
  BaseFeature = -> Pocket109
  Length = 5
  Length2 = 100
  Placement = pos=(0,0,0) rot=(0.57735,0.57735,0.57735;2.0944rad)
  Profile = -> Sketch030
  Refine = true
  Type = 1
FEATURE [Sketcher::SketchObject] Sketch031
  MapMode = 5
  Placement = pos=(5e-16,-9e-16,-2) rot=(0.707107,0.707107,0;3.14159rad)
  Support = -> [Pocket105]
  expr: Constraints[6] = 11.8 + 0.4
  sketch-geometry (2):
    g0: ArcOfCircle CenterX=0 CenterY=0 CenterZ=0 NormalX=0 NormalY=0 NormalZ=1 AngleXU=0 Radius=6.1 StartAngle=2.10584 EndAngle=7.31894
    g1: ArcOfCircle CenterX=0 CenterY=6 CenterZ=0 NormalX=0 NormalY=0 NormalZ=1 AngleXU=0 Radius=3.2 StartAngle=6.04581 EndAngle=9.66216
  constraints (7):
    c: Coincident(g0,g-1)
    c: PointOnObject(g1,g-2)
    c: Coincident(g1,g0)
    c: Coincident(g1,g0)
    c: Radius(g1) = 3.2
    c: DistanceY(g0,g1) = 6
    c: Diameter(g0) = 12.2
FEATURE [PartDesign::Pocket] Pocket106
  BaseFeature = -> Pocket105
  Length = 1
  Length2 = 100
  Placement = pos=(0,0,0) rot=(0.57735,0.57735,0.57735;2.0944rad)
  Profile = -> Sketch031
  Refine = true
  Type = 0
FEATURE [PartDesign::Pad] Pad131
  Length = 14
  Length2 = 100
  Placement = pos=(0,0,0) rot=(0.57735,0.57735,0.57735;2.0944rad)
  Profile = -> Sketch243
  Type = 0
FEATURE [Sketcher::SketchObject] Sketch248
  ExternalGeometry = -> [Pad131]
  MapMode = 5
  Placement = pos=(0,0,0) rot=(0.57735,0.57735,0.57735;2.0944rad)
  Support = -> [YZ_Plane091]
  expr: Constraints[14] = 2.5 - 0 - 0.2 - 0.8
  expr: Constraints[15] = 0.8 + 1.5 + 1.5
  sketch-geometry (6):
    g0: LineSegment StartX=-10.2 StartY=5.31 StartZ=0 EndX=10.2 EndY=5.31 EndZ=0
    g1: LineSegment StartX=10.2 StartY=5.31 StartZ=0 EndX=10.2 EndY=1.51 EndZ=0
    g2: LineSegment StartX=10.2 StartY=1.51 StartZ=0 EndX=-10.2 EndY=1.51 EndZ=0
    g3: LineSegment StartX=-10.2 StartY=1.51 StartZ=0 EndX=-10.2 EndY=5.31 EndZ=0
    g4: LineSegment [constr] StartX=-10.2 StartY=1.51 StartZ=0 EndX=-10.2 EndY=0.01 EndZ=0
    g5: LineSegment [constr] StartX=10.2 StartY=1.51 StartZ=0 EndX=10.2 EndY=0.01 EndZ=0
  constraints (16):
    c: Coincident(g0,g1)
    c: Coincident(g1,g2)
    c: Coincident(g2,g3)
    c: Coincident(g3,g0)
    c: Horizontal(g0)
    c: Horizontal(g2)
    c: Vertical(g1)
    c: Vertical(g3)
    c: Coincident(g4,g2)
    c: Coincident(g4,g-4)
    c: Coincident(g5,g1)
    c: Coincident(g5,g-3)
    c: Vertical(g5)
    c: Vertical(g4)
    c: Distance(g5) = 1.5
    c: Distance(g1) = 3.8
FEATURE [PartDesign::Pocket] Pocket013
  BaseFeature = -> Pad131
  Length = 5
  Length2 = 100
  Placement = pos=(0,0,0) rot=(0.57735,0.57735,0.57735;2.0944rad)
  Profile = -> Sketch248
  Reversed = true
  Type = 1
FEATURE [Sketcher::SketchObject] Sketch247
  MapMode = 5
  Placement = pos=(-1.9e-15,3e-15,6.81) rot=(0,0,-1;1.5708rad)
  Support = -> [Pocket013]
  sketch-geometry (1):
    g0: Circle CenterX=0 CenterY=12 CenterZ=0 NormalX=0 NormalY=0 NormalZ=1 AngleXU=0 Radius=0.6
  constraints (3):
    c: PointOnObject(g0,g-2)
    c: Radius(g0) = 0.6
    c: DistanceY(g-1,g0) = 12
FEATURE [PartDesign::Pocket] Pocket111
  BaseFeature = -> Pocket013
  Length = 5
  Length2 = 100
  Placement = pos=(0,0,0) rot=(0.57735,0.57735,0.57735;2.0944rad)
  Profile = -> Sketch247
  Type = 2
FEATURE [PartDesign::Fillet] Fillet014
  Base = -> Pocket111 [Edge39,Edge1,Edge2,Edge41]
  BaseFeature = -> Pocket111
  Placement = pos=(0,0,0) rot=(0.57735,0.57735,0.57735;2.0944rad)
  Radius = 1
  SupportTransform = true
FEATURE [PartDesign::Fillet] Fillet035
  Base = -> Fillet014 [Edge62,Edge61,Edge56]
  BaseFeature = -> Fillet014
  Placement = pos=(0,0,0) rot=(0.57735,0.57735,0.57735;2.0944rad)
  Radius = 1
  SupportTransform = true
FEATURE [Sketcher::SketchObject] Sketch238
  ExternalGeometry = -> [Fillet035]
  MapMode = 5
  Placement = pos=(-1.9e-15,3e-15,6.81) rot=(0,0,-1;1.5708rad)
  Support = -> [Fillet035]
  sketch-geometry (4):
    g0: LineSegment StartX=10.2 StartY=14 StartZ=0 EndX=40.2 EndY=2 EndZ=0
    g1: LineSegment StartX=40.2 StartY=2 StartZ=0 EndX=40.2 EndY=15 EndZ=0
    g2: LineSegment StartX=40.2 StartY=15 StartZ=0 EndX=10.2 EndY=15 EndZ=0
    g3: LineSegment StartX=10.2 StartY=15 StartZ=0 EndX=10.2 EndY=14 EndZ=0
  constraints (11):
    c: Coincident(g0,g-4)
    c: PointOnObject(g0,g-3)
    c: Coincident(g0,g1)
    c: Vertical(g1)
    c: Coincident(g1,g2)
    c: Horizontal(g2)
    c: Coincident(g2,g3)
    c: Coincident(g3,g0)
    c: Vertical(g3)
    c: DistanceY(g-3,g0) = 2
    c: Distance(g3) = 1
FEATURE [PartDesign::Pocket] Pocket103
  BaseFeature = -> Fillet035
  Length = 5
  Length2 = 100
  Placement = pos=(0,0,0) rot=(0.57735,0.57735,0.57735;2.0944rad)
  Profile = -> Sketch238
  Type = 1
FEATURE [Sketcher::SketchObject] Sketch249
  ExternalGeometry = -> [Pocket103]
  MapMode = 5
  Placement = pos=(14,-3.1e-15,3.1e-15) rot=(0.57735,0.57735,0.57735;2.0944rad)
  Support = -> [Pocket103]
  sketch-geometry (16):
    g0: LineSegment StartX=-38.7 StartY=5.31 StartZ=0 EndX=-11.7 EndY=5.31 EndZ=0
    g1: LineSegment StartX=-11.7 StartY=5.31 StartZ=0 EndX=-11.7 EndY=-2.42333 EndZ=0
    g2: LineSegment StartX=-11.7 StartY=-2.42333 StartZ=0 EndX=-38.7 EndY=-2.42333 EndZ=0
    g3: LineSegment StartX=-38.7 StartY=-2.42333 StartZ=0 EndX=-38.7 EndY=5.31 EndZ=0
    g4: LineSegment StartX=-38.7 StartY=-3.92333 StartZ=0 EndX=-11.7 EndY=-3.92333 EndZ=0
    g5: LineSegment StartX=-11.7 StartY=-3.92333 StartZ=0 EndX=-11.7 EndY=-11.6567 EndZ=0
    g6: LineSegment StartX=-11.7 StartY=-11.6567 StartZ=0 EndX=-38.7 EndY=-11.6567 EndZ=0
    g7: LineSegment StartX=-38.7 StartY=-11.6567 StartZ=0 EndX=-38.7 EndY=-3.92333 EndZ=0
    g8: LineSegment StartX=-38.7 StartY=-13.1567 StartZ=0 EndX=-11.7 EndY=-13.1567 EndZ=0
    g9: LineSegment StartX=-11.7 StartY=-13.1567 StartZ=0 EndX=-11.7 EndY=-20.89 EndZ=0
    g10: LineSegment StartX=-11.7 StartY=-20.89 StartZ=0 EndX=-38.7 EndY=-20.89 EndZ=0
    g11: LineSegment StartX=-38.7 StartY=-20.89 StartZ=0 EndX=-38.7 EndY=-13.1567 EndZ=0
    g12: LineSegment [constr] StartX=-38.7 StartY=6.81 StartZ=0 EndX=-38.7 EndY=5.31 EndZ=0
    g13: LineSegment [constr] StartX=-38.7 StartY=-2.42333 StartZ=0 EndX=-38.7 EndY=-3.92333 EndZ=0
    g14: LineSegment [constr] StartX=-38.7 StartY=-11.6567 StartZ=0 EndX=-38.7 EndY=-13.1567 EndZ=0
    g15: LineSegment [constr] StartX=-38.7 StartY=-20.89 StartZ=0 EndX=-38.7 EndY=-22.39 EndZ=0
  constraints (46):
    c: Coincident(g0,g1)
    c: Coincident(g1,g2)
    c: Coincident(g2,g3)
    c: Coincident(g3,g0)
    c: Horizontal(g0)
    c: Horizontal(g2)
    c: Vertical(g1)
    c: Vertical(g3)
    c: Coincident(g4,g5)
    c: Coincident(g5,g6)
    c: Coincident(g6,g7)
    c: Coincident(g7,g4)
    c: Horizontal(g4)
    c: Horizontal(g6)
    c: Vertical(g5)
    c: Vertical(g7)
    c: Coincident(g8,g9)
    c: Coincident(g9,g10)
    c: Coincident(g10,g11)
    c: Coincident(g11,g8)
    c: Horizontal(g8)
    c: Horizontal(g10)
    c: Vertical(g9)
    c: Vertical(g11)
    c: Vertical(g8,g4)
    c: Vertical(g4,g0)
    c: Coincident(g12,g0)
    c: Coincident(g13,g2)
    c: Coincident(g13,g4)
    c: Coincident(g14,g6)
    c: Coincident(g14,g8)
    c: Coincident(g15,g10)
    c: Equal(g12,g13)
    c: Equal(g13,g14)
    c: Equal(g14,g15)
    c: Distance(g12) = 1.5
    c: DistanceX(g0,g-3) = 1.5
    c: Equal(g3,g7)
    c: Equal(g7,g11)
    c: Vertical(g12)
    c: Vertical(g13)
    c: Vertical(g14)
    c: Vertical(g15)
    c: Horizontal(g12,g-4)
    c: Horizontal(g15,g-4)
    c: DistanceX(g-4,g12) = 1.5
FEATURE [PartDesign::Pocket] Pocket108
  BaseFeature = -> Pocket103
  Length = 12.5
  Length2 = 100
  Placement = pos=(0,0,0) rot=(0.57735,0.57735,0.57735;2.0944rad)
  Profile = -> Sketch249
  Type = 0
FEATURE [Sketcher::SketchObject] Sketch246
  MapMode = 5
  Placement = pos=(-4e-16,7e-16,1.51) rot=(0,0,-1;1.5708rad)
  Support = -> [Pocket108]
  sketch-geometry (1):
    g0: Circle CenterX=0 CenterY=0 CenterZ=0 NormalX=0 NormalY=0 NormalZ=1 AngleXU=0 Radius=4
  constraints (2):
    c: Coincident(g0,g-1)
    c: Radius(g0) = 4
FEATURE [PartDesign::Pocket] Pocket107
  BaseFeature = -> Pocket108
  Length = 5
  Length2 = 100
  Placement = pos=(0,0,0) rot=(0.57735,0.57735,0.57735;2.0944rad)
  Profile = -> Sketch246
  Type = 2
FEATURE [PartDesign::Fillet] Fillet015
  Base = -> Pocket107 [Edge10,Edge18]
  BaseFeature = -> Pocket107
  Placement = pos=(0,0,0) rot=(0.57735,0.57735,0.57735;2.0944rad)
  Radius = 2
  SupportTransform = true
FEATURE [PartDesign::Fillet] Fillet036
  Base = -> Fillet015 [Edge76]
  BaseFeature = -> Fillet015
  Placement = pos=(0,0,0) rot=(0.57735,0.57735,0.57735;2.0944rad)
  Radius = 1
  SupportTransform = true
FEATURE [PartDesign::Fillet] Fillet037
  Base = -> Fillet036 [Edge108,Edge110,Edge116,Edge118,Edge124,Edge126]
  BaseFeature = -> Fillet036
  Placement = pos=(0,0,0) rot=(0.57735,0.57735,0.57735;2.0944rad)
  Radius = 1
  SupportTransform = true
FEATURE [Sketcher::SketchObject] Sketch251
  ExternalGeometry = -> [Pocket106]
  MapMode = 5
  Placement = pos=(5e-16,-9e-16,-2) rot=(0.707107,0.707107,0;3.14159rad)
  Support = -> [Pocket106]
  expr: Constraints[8] = 22.2 + 0.4
  sketch-geometry (10):
    g0: LineSegment StartX=-6.1 StartY=16.5 StartZ=0 EndX=6.1 EndY=16.5 EndZ=0
    g1: LineSegment StartX=6.1 StartY=16.5 StartZ=0 EndX=6.1 EndY=-6.1 EndZ=0
    g2: LineSegment StartX=6.1 StartY=-6.1 StartZ=0 EndX=-6.1 EndY=-6.1 EndZ=0
    g3: LineSegment StartX=-6.1 StartY=-6.1 StartZ=0 EndX=-6.1 EndY=16.5 EndZ=0
    g4: LineSegment StartX=-7.1 StartY=-7.1 StartZ=0 EndX=7.1 EndY=-7.1 EndZ=0
    g5: LineSegment StartX=7.1 StartY=-7.1 StartZ=0 EndX=7.1 EndY=17.5 EndZ=0
    g6: LineSegment StartX=7.1 StartY=17.5 StartZ=0 EndX=-7.1 EndY=17.5 EndZ=0
    g7: LineSegment StartX=-7.1 StartY=17.5 StartZ=0 EndX=-7.1 EndY=-7.1 EndZ=0
    g8: LineSegment [constr] StartX=7.1 StartY=17.5 StartZ=0 EndX=6.1 EndY=16.5 EndZ=0
    g9: LineSegment [constr] StartX=6.1 StartY=-6.1 StartZ=0 EndX=7.1 EndY=-7.1 EndZ=0
  constraints (26):
    c: Coincident(g0,g1)
    c: Coincident(g1,g2)
    c: Coincident(g2,g3)
    c: Coincident(g3,g0)
    c: Horizontal(g2)
    c: Vertical(g1)
    c: Vertical(g3)
    c: Symmetric(g0,g0,g-2)
    c: Distance(g3) = 22.6
    c: Coincident(g4,g5)
    c: Coincident(g5,g6)
    c: Coincident(g6,g7)
    c: Coincident(g7,g4)
    c: Horizontal(g4)
    c: Vertical(g5)
    c: Vertical(g7)
    c: Symmetric(g6,g5,g-2)
    c: DistanceX(g4,g2) = 1
    c: DistanceY(g4,g2) = 1
    c: Coincident(g8,g5)
    c: Coincident(g8,g0)
    c: Coincident(g9,g1)
    c: Coincident(g9,g4)
    c: Equal(g9,g8)
    c: Tangent(g-3,g2)
    c: Tangent(g1,g-3)
FEATURE [PartDesign::Pad] Pad132
  BaseFeature = -> Pocket106
  Length = 5
  Length2 = 100
  Placement = pos=(0,0,0) rot=(0.57735,0.57735,0.57735;2.0944rad)
  Profile = -> Sketch251
  Refine = true
  Type = 0
FEATURE [Sketcher::SketchObject] Sketch239
  ExternalGeometry = -> [Pad132]
  MapMode = 5
  Placement = pos=(4.4e-15,10,-2.2e-15) rot=(0.57735,0.57735,0.57735;4.18879rad)
  Support = -> [Pad132]
  sketch-geometry (4):
    g0: LineSegment StartX=-20 StartY=5 StartZ=0 EndX=-5.8 EndY=5 EndZ=0
    g1: LineSegment StartX=-5.8 StartY=5 StartZ=0 EndX=-5.8 EndY=-5 EndZ=0
    g2: LineSegment StartX=-5.8 StartY=-5 StartZ=0 EndX=-20 EndY=-5 EndZ=0
    g3: LineSegment StartX=-20 StartY=-5 StartZ=0 EndX=-20 EndY=5 EndZ=0
  constraints (11):
    c: Coincident(g0,g1)
    c: Coincident(g1,g2)
    c: Coincident(g2,g3)
    c: Coincident(g3,g0)
    c: Horizontal(g0)
    c: Horizontal(g2)
    c: Vertical(g3)
    c: Symmetric(g0,g1,g-1)
    c: Distance(g3) = 10
    c: PointOnObject(g0,g-3)
    c: Distance(g0) = 14.2
FEATURE [PartDesign::Pocket] Pocket110
  BaseFeature = -> Pad132
  Length = 5
  Length2 = 100
  Placement = pos=(0,0,0) rot=(0.57735,0.57735,0.57735;2.0944rad)
  Profile = -> Sketch239
  Refine = true
  Type = 2
FEATURE [Sketcher::SketchObject] Sketch242
  MapMode = 5
  Placement = pos=(1.8e-15,8,-4.4e-15) rot=(0.57735,0.57735,-0.57735;2.0944rad)
  Support = -> [Pocket110]
  sketch-geometry (4):
    g0: LineSegment StartX=4.8 StartY=6.2 StartZ=0 EndX=17.2 EndY=6.2 EndZ=0
    g1: LineSegment StartX=17.2 StartY=6.2 StartZ=0 EndX=17.2 EndY=-6.2 EndZ=0
    g2: LineSegment StartX=17.2 StartY=-6.2 StartZ=0 EndX=4.8 EndY=-6.2 EndZ=0
    g3: LineSegment StartX=4.8 StartY=-6.2 StartZ=0 EndX=4.8 EndY=6.2 EndZ=0
  constraints (11):
    c: Coincident(g0,g1)
    c: Coincident(g1,g2)
    c: Coincident(g2,g3)
    c: Coincident(g3,g0)
    c: Horizontal(g0)
    c: Horizontal(g2)
    c: Vertical(g1)
    c: Symmetric(g0,g2,g-1)
    c: Distance(g3) = 12.4
    c: Equal(g0,g3)
    c: DistanceX(g-1,g0) = 4.8
FEATURE [PartDesign::Pocket] Pocket112
  BaseFeature = -> Pocket110
  Length = 1
  Length2 = 100
  Placement = pos=(0,0,0) rot=(0.57735,0.57735,0.57735;2.0944rad)
  Profile = -> Sketch242
  Refine = true
  Type = 0
FEATURE [Sketcher::SketchObject] Sketch252
  ExternalGeometry = -> [Pocket112]
  MapMode = 5
  Placement = pos=(0,0,0) rot=(0.57735,0.57735,0.57735;2.0944rad)
  Support = -> [YZ_Plane092]
  sketch-geometry (12):
    g0: ArcOfCircle CenterX=-9 CenterY=-19 CenterZ=0 NormalX=0 NormalY=0 NormalZ=1 AngleXU=0 Radius=1 StartAngle=4.71239 EndAngle=6.28319
    g1: ArcOfCircle CenterX=9 CenterY=-19 CenterZ=0 NormalX=0 NormalY=0 NormalZ=1 AngleXU=0 Radius=1 StartAngle=3.14159 EndAngle=4.71239
    g2: LineSegment StartX=-8 StartY=-19 StartZ=0 EndX=-8 EndY=-17.5 EndZ=0
    g3: LineSegment StartX=8 StartY=-19 StartZ=0 EndX=8 EndY=-17.5 EndZ=0
    g4: LineSegment StartX=-8 StartY=-17.5 StartZ=0 EndX=-6.6 EndY=-17.5 EndZ=0
    g5: LineSegment StartX=8 StartY=-17.5 StartZ=0 EndX=6.6 EndY=-17.5 EndZ=0
    g6: LineSegment StartX=9 StartY=-20 StartZ=0 EndX=4.1 EndY=-20 EndZ=0
    g7: LineSegment StartX=-9 StartY=-20 StartZ=0 EndX=-4.1 EndY=-20 EndZ=0
    g8: ArcOfCircle CenterX=-4.1 CenterY=-18.75 CenterZ=0 NormalX=0 NormalY=0 NormalZ=1 AngleXU=0 Radius=1.25 StartAngle=3.14159 EndAngle=4.71239
    g9: ArcOfCircle CenterX=4.1 CenterY=-18.75 CenterZ=0 NormalX=0 NormalY=0 NormalZ=1 AngleXU=0 Radius=1.25 StartAngle=4.71239 EndAngle=6.28319
    g10: ArcOfCircle CenterX=-6.6 CenterY=-18.75 CenterZ=0 NormalX=0 NormalY=0 NormalZ=1 AngleXU=0 Radius=1.25 StartAngle=0 EndAngle=1.5708
    g11: ArcOfCircle CenterX=6.6 CenterY=-18.75 CenterZ=0 NormalX=0 NormalY=0 NormalZ=1 AngleXU=0 Radius=1.25 StartAngle=1.5708 EndAngle=3.14159
  constraints (40):
    c: Vertical(g-3,g0)
    c: Vertical(g1,g-4)
    c: Horizontal(g0,g0)
    c: Horizontal(g1,g1)
    c: Vertical(g0,g0)
    c: Vertical(g1,g1)
    c: Equal(g0,g1)
    c: Radius(g0) = 1
    c: Coincident(g2,g0)
    c: Vertical(g2)
    c: Coincident(g3,g1)
    c: Vertical(g3)
    c: DistanceY(g0,g2) = 2.5
    c: Horizontal(g3,g2)
    c: Coincident(g4,g2)
    c: Horizontal(g4)
    c: Coincident(g5,g3)
    c: Horizontal(g5)
    c: Equal(g4,g5)
    c: Distance(g4) = 1.4
    c: Coincident(g6,g1)
    c: Horizontal(g6)
    c: Coincident(g7,g0)
    c: Horizontal(g7)
    c: PointOnObject(g-3,g7)
    c: PointOnObject(g-4,g6)
    c: Tangent(g9,g6) = 1.5708
    c: Tangent(g8,g7) = -1.5708
    c: Horizontal(g9,g9)
    c: Horizontal(g8,g8)
    c: Coincident(g10,g4)
    c: Coincident(g10,g8)
    c: Coincident(g11,g5)
    c: Coincident(g11,g9)
    c: Vertical(g11,g5)
    c: Horizontal(g11,g9)
    c: Horizontal(g8,g10)
    c: Vertical(g4,g10)
    c: Horizontal(g8,g9)
    c: Equal(g10,g8)
FEATURE [PartDesign::Pocket] Pocket027
  BaseFeature = -> Pocket112
  Length = 5
  Length2 = 100
  Midplane = true
  Placement = pos=(0,0,0) rot=(0.57735,0.57735,0.57735;2.0944rad)
  Profile = -> Sketch252
  Refine = true
  Type = 1
FEATURE [PartDesign::Mirrored] Mirrored023
  BaseFeature = -> Pad128
  MirrorPlane = -> Sketch237 [V_Axis]
  Originals = -> [Pad128]
  Placement = pos=(0,0,0) rot=(1,0,0;1.5708rad)
  Refine = true
FEATURE [PartDesign::Body] Body079
  Group = -> [Sketch237,Pad128,Mirrored023]
  Origin = -> Origin094
  Placement = pos=(0,0.05,3.96) rot=(-1,0,0;1.5708rad)
  Tip = -> Mirrored023
FEATURE [Sketcher::SketchObject] Sketch255
  MapMode = 5
  Placement = pos=(5.4e-15,12.2,-2.7e-15) rot=(0.57735,0.57735,0.57735;4.18879rad)
  Support = -> [Fillet037]
  sketch-geometry (5):
    g0: ArcOfCircle CenterX=-11.2 CenterY=0 CenterZ=0 NormalX=0 NormalY=0 NormalZ=1 AngleXU=0 Radius=8 StartAngle=0.460554 EndAngle=3.14159
    g1: LineSegment StartX=-3.13774 StartY=3 StartZ=0 EndX=0 EndY=3 EndZ=0
    g2: LineSegment StartX=0 StartY=3 StartZ=0 EndX=0 EndY=0 EndZ=0
    g3: LineSegment StartX=0 StartY=0 StartZ=0 EndX=-19.2 EndY=1e-15 EndZ=0
    g4: ArcOfCircle CenterX=-3.13774 CenterY=4 CenterZ=0 NormalX=0 NormalY=0 NormalZ=1 AngleXU=0 Radius=1 StartAngle=3.60215 EndAngle=4.71239
  constraints (14):
    c: PointOnObject(g0,g-1)
    c: PointOnObject(g0,g-1)
    c: DistanceX(g0,g-1) = 11.2
    c: Diameter(g0) = 16
    c: PointOnObject(g1,g-2)
    c: Horizontal(g1)
    c: Coincident(g2,g1)
    c: Coincident(g2,g-1)
    c: Coincident(g3,g2)
    c: Coincident(g3,g0)
    c: Distance(g2) = 3
    c: Tangent(g1,g4) = -1.5708
    c: Tangent(g0,g4) = 1.5708
    c: Radius(g4) = 1
FEATURE [PartDesign::Pocket] Pocket102
  BaseFeature = -> Fillet037
  Length = 4
  Length2 = 100
  Placement = pos=(0,0,0) rot=(0.57735,0.57735,0.57735;2.0944rad)
  Profile = -> Sketch255
  Refine = true
  Type = 0
FEATURE [Sketcher::SketchObject] Sketch254
  ExternalGeometry = -> [Pocket102]
  MapMode = 5
  Placement = pos=(0,0,0) rot=(0.57735,0.57735,0.57735;2.0944rad)
  Support = -> [YZ_Plane091]
  sketch-geometry (8):
    g0: LineSegment StartX=-7.8 StartY=-22.39 StartZ=0 EndX=-6.8 EndY=-22.39 EndZ=0
    g1: LineSegment StartX=-6.8 StartY=-22.39 StartZ=0 EndX=-6.8 EndY=-18.39 EndZ=0
    g2: LineSegment StartX=-6.8 StartY=-18.39 StartZ=0 EndX=-7.8 EndY=-18.39 EndZ=0
    g3: LineSegment StartX=-7.8 StartY=-18.39 StartZ=0 EndX=-7.8 EndY=-22.39 EndZ=0
    g4: LineSegment StartX=7.8 StartY=-22.39 StartZ=0 EndX=6.8 EndY=-22.39 EndZ=0
    g5: LineSegment StartX=6.8 StartY=-22.39 StartZ=0 EndX=6.8 EndY=-18.39 EndZ=0
    g6: LineSegment StartX=6.8 StartY=-18.39 StartZ=0 EndX=7.8 EndY=-18.39 EndZ=0
    g7: LineSegment StartX=7.8 StartY=-18.39 StartZ=0 EndX=7.8 EndY=-22.39 EndZ=0
  constraints (22):
    c: Coincident(g0,g1)
    c: Coincident(g1,g2)
    c: Coincident(g2,g3)
    c: Coincident(g3,g0)
    c: Horizontal(g0)
    c: Horizontal(g2)
    c: Vertical(g1)
    c: Vertical(g3)
    c: Coincident(g0,g-3)
    c: Coincident(g4,g5)
    c: Coincident(g5,g6)
    c: Coincident(g6,g7)
    c: Coincident(g7,g4)
    c: Horizontal(g4)
    c: Horizontal(g6)
    c: Vertical(g5)
    c: Vertical(g7)
    c: Coincident(g4,g-4)
    c: Equal(g2,g6)
    c: Equal(g1,g5)
    c: Distance(g6) = 1
    c: Distance(g3) = 4
FEATURE [PartDesign::Pad] Pad126
  BaseFeature = -> Pocket102
  Length = 10
  Length2 = 100
  Placement = pos=(0,0,0) rot=(0.57735,0.57735,0.57735;2.0944rad)
  Profile = -> Sketch254
  Refine = true
  Type = 3
  UpToFace = -> Pocket102 [Face9]
FEATURE [PartDesign::Fillet] Fillet016
  Base = -> Pad126 [Edge106,Edge158,Edge168,Edge142]
  BaseFeature = -> Pad126
  Placement = pos=(0,0,0) rot=(0.57735,0.57735,0.57735;2.0944rad)
  Radius = 1
  Refine = true
  SupportTransform = false
FEATURE [PartDesign::Body] Body082
  Group = -> [Sketch243,Pad131,Sketch248,Pocket013,Sketch247,Pocket111,Fillet014,Fillet035,Sketch238,Pocket103,Sketch249,Pocket108,Sketch246,Pocket107,Fillet015,Fillet036,Fillet037,Sketch255,Pocket102,Sketch254,Pad126,Fillet016]
  Origin = -> Origin092
  Placement = pos=(16,11,14.15) rot=(-1,0,0;1.5708rad)
  Tip = -> Fillet016
FEATURE [Sketcher::SketchObject] Sketch256
  ExternalGeometry = -> [Pocket027]
  MapMode = 5
  Placement = pos=(4.4e-15,10,-2.2e-15) rot=(0.57735,0.57735,0.57735;4.18879rad)
  Support = -> [Pocket027]
  sketch-geometry (6):
    g0: ArcOfCircle CenterX=-19 CenterY=6 CenterZ=0 NormalX=0 NormalY=0 NormalZ=1 AngleXU=0 Radius=1 StartAngle=3.14159 EndAngle=4.71239
    g1: ArcOfCircle CenterX=-19 CenterY=-6 CenterZ=0 NormalX=0 NormalY=0 NormalZ=1 AngleXU=0 Radius=1 StartAngle=1.5708 EndAngle=3.14159
    g2: LineSegment StartX=-19 StartY=5 StartZ=0 EndX=-19 EndY=-5 EndZ=0
    g3: LineSegment StartX=-20 StartY=6 StartZ=0 EndX=-21 EndY=6 EndZ=0
    g4: LineSegment StartX=-20 StartY=-6 StartZ=0 EndX=-21 EndY=-6 EndZ=0
    g5: LineSegment StartX=-21 StartY=6 StartZ=0 EndX=-21 EndY=-6 EndZ=0
  constraints (18):
    c: PointOnObject(g0,g-3)
    c: Coincident(g0,g-3)
    c: PointOnObject(g1,g-4)
    c: Coincident(g1,g-4)
    c: Distance(g0,g0) = 1
    c: Coincident(g2,g0)
    c: Coincident(g2,g1)
    c: Coincident(g3,g0)
    c: Horizontal(g3)
    c: Coincident(g4,g1)
    c: Horizontal(g4)
    c: Coincident(g5,g3)
    c: Coincident(g5,g4)
    c: Vertical(g5)
    c: Horizontal(g0,g0)
    c: Horizontal(g1,g1)
    c: Vertical(g0,g1)
    c: Distance(g3) = 1
FEATURE [PartDesign::Pocket] Pocket028
  BaseFeature = -> Pocket027
  Length = 3
  Length2 = 100
  Placement = pos=(0,0,0) rot=(0.57735,0.57735,0.57735;2.0944rad)
  Profile = -> Sketch256
  Refine = true
  Type = 0
FEATURE [PartDesign::Body] Body081
  Group = -> [Sketch028,Pad130,Sketch029,Pocket109,Sketch030,Pocket105,Sketch031,Pocket106,Sketch251,Pad132,Sketch239,Pocket110,Sketch242,Pocket112,Sketch252,Pocket027,Sketch256,Pocket028]
  Origin = -> Origin093
  Placement = pos=(0,10.8,14.16) rot=(-1,0,0;1.5708rad)
  Tip = -> Pocket028
FEATURE [PartDesign::FeatureBase] Clone049
  BaseFeature = -> Body082
  Placement = pos=(16,11,14.15) rot=(-1,0,0;1.5708rad)
FEATURE [PartDesign::Body] Body083
  BaseFeature = -> Body082
  Group = -> [Clone049]
  Origin = -> Origin095
  Tip = -> Clone049
FEATURE [Sketcher::SketchObject] Sketch257
  MapMode = 5
  Placement = pos=(0,0,-5.5) rot=(1,0,0;3.14159rad)
  Support = -> [Pocket054]
  sketch-geometry (1):
    g0: Circle CenterX=10 CenterY=0 CenterZ=0 NormalX=0 NormalY=0 NormalZ=1 AngleXU=0 Radius=8.5
  constraints (3):
    c: PointOnObject(g0,g-1)
    c: Diameter(g0) = 17
    c: DistanceX(g0) = 10
FEATURE [PartDesign::Pad] Pad133
  BaseFeature = -> Pocket054
  Length = 17
  Length2 = 100
  Profile = -> Sketch257
  Refine = true
  Type = 0
FEATURE [PartDesign::Body] Body023
  Group = -> [Sketch108,Pad046,Sketch109,Pad048,Sketch110,Pad047,Chamfer006,Sketch107,Pad045,Sketch106,Sketch101,Pad044,Sketch103,Pad042,Pocket053,Sketch100,MultiTransform,Mirrored013,Mirrored001,Pocket052,MultiTransform001,Mirrored002,Mirrored003,Fillet028,Chamfer007,Fillet024,Chamfer002,Chamfer003,Fillet025,Chamfer004,Fillet023,Chamfer005,Sketch102,Pocket050,Sketch105,Pad043,Sketch104,MultiTransform002,+12 more]
  Origin = -> Origin023
  Tip = -> Pad133
FEATURE [PartDesign::FeatureBase] Clone010
  BaseFeature = -> Body023
FEATURE [PartDesign::Body] Body024
  BaseFeature = -> Body023
  Group = -> [Clone010]
  Origin = -> Origin024
  Placement = pos=(37.1,-10,-203.8) rot=(0.57735,-0.57735,-0.57735;2.0944rad)
  Tip = -> Clone010
FEATURE [PartDesign::FeatureBase] Clone011
  BaseFeature = -> Body023
FEATURE [PartDesign::Body] Body025
  BaseFeature = -> Body023
  Group = -> [Clone011]
  Origin = -> Origin025
  Placement = pos=(37.1,-190,-203.8) rot=(0.57735,0.57735,-0.57735;4.18879rad)
  Tip = -> Clone011
FEATURE [PartDesign::FeatureBase] Clone029
  BaseFeature = -> Body023
FEATURE [PartDesign::Body] Body051
  BaseFeature = -> Body023
  Group = -> [Clone029]
  Origin = -> Origin058
  Placement = pos=(-1,-198.75,-213.8) rot=(0.57735,0.57735,-0.57735;2.0944rad)
  Tip = -> Clone029
FEATURE [Part::Mirroring] Part__Mirroring007  label="Body083 (Mirror #8)"
  Base = (0,0,0)
  Normal = (1,0,0)
  Source = -> Body083
FEATURE [App::DocumentObjectGroup] Group001  label="Gripper"
  Group = -> [Body079,Body081,Body082,Part__Mirroring007]
FEATURE [Sketcher::SketchObject] Sketch274
  MapMode = 5
  Support = -> [XY_Plane098]
  sketch-geometry (7):
    g0: LineSegment StartX=-11.5 StartY=0 StartZ=0 EndX=-14.5 EndY=17.5 EndZ=0
    g1: LineSegment StartX=-14.5 StartY=17.5 StartZ=0 EndX=-7.5 EndY=34.5 EndZ=0
    g2: LineSegment StartX=-7.5 StartY=34.5 StartZ=0 EndX=20.5 EndY=34.5 EndZ=0
    g3: LineSegment StartX=20.5 StartY=34.5 StartZ=0 EndX=20.5 EndY=17.5 EndZ=0
    g4: LineSegment StartX=20.5 StartY=17.5 StartZ=0 EndX=11.5 EndY=0 EndZ=0
    g5: LineSegment StartX=11.5 StartY=0 StartZ=0 EndX=-11.5 EndY=0 EndZ=0
    g6: GeomPoint X=0 Y=17.5 Z=0
  constraints (20):
    c: PointOnObject(g0,g-1)
    c: Coincident(g0,g1)
    c: Coincident(g1,g2)
    c: Horizontal(g2)
    c: Coincident(g2,g3)
    c: Vertical(g3)
    c: Coincident(g3,g4)
    c: PointOnObject(g4,g-1)
    c: Coincident(g4,g5)
    c: Coincident(g5,g0)
    c: Distance(g-1,g0) = 11.5
    c: Distance(g-1,g4) = 11.5
    c: PointOnObject(g6,g-2)
    c: Horizontal(g6,g3)
    c: Distance(g6,g3) = 20.5
    c: Horizontal(g6,g0)
    c: Distance(g0,g6) = 14.5
    c: Distance(g-1,g6) = 17.5
    c: Distance(g3) = 17
    c: Distance(g2) = 28
FEATURE [PartDesign::Pad] Pad146
  Length = 1
  Length2 = 100
  Profile = -> Sketch274
  Refine = true
  Type = 0
FEATURE [Sketcher::SketchObject] Sketch275
  ExternalGeometry = -> [Pad146]
  MapMode = 5
  Placement = pos=(0,0,0) rot=(1,0,0;3.14159rad)
  Support = -> [Pad146]
  sketch-geometry (12):
    g0: LineSegment StartX=-7.5 StartY=-34.5 StartZ=0 EndX=-14.5 EndY=-17.5 EndZ=0
    g1: LineSegment StartX=-14.5 StartY=-17.5 StartZ=0 EndX=-11.5 EndY=0 EndZ=0
    g2: LineSegment StartX=-11.5 StartY=0 StartZ=0 EndX=-10.5 EndY=0 EndZ=0
    g3: LineSegment StartX=-10.5 StartY=0 StartZ=0 EndX=-13.5 EndY=-17.5 EndZ=0
    g4: LineSegment StartX=-13.5 StartY=-17.5 StartZ=0 EndX=-6.5 EndY=-34.5 EndZ=0
    g5: LineSegment StartX=-6.5 StartY=-34.5 StartZ=0 EndX=-7.5 EndY=-34.5 EndZ=0
    g6: LineSegment StartX=11.5 StartY=0 StartZ=0 EndX=20.5 EndY=-17.5 EndZ=0
    g7: LineSegment StartX=20.5 StartY=-17.5 StartZ=0 EndX=20.5 EndY=-34.5 EndZ=0
    g8: LineSegment StartX=20.5 StartY=-34.5 StartZ=0 EndX=19.5 EndY=-34.5 EndZ=0
    g9: LineSegment StartX=19.5 StartY=-34.5 StartZ=0 EndX=19.5 EndY=-17.5 EndZ=0
    g10: LineSegment StartX=19.5 StartY=-17.5 StartZ=0 EndX=10.5 EndY=0 EndZ=0
    g11: LineSegment StartX=10.5 StartY=0 StartZ=0 EndX=11.5 EndY=0 EndZ=0
  constraints (30):
    c: Coincident(g-4,g0)
    c: Coincident(g0,g-4)
    c: Coincident(g0,g1)
    c: Coincident(g1,g-3)
    c: Coincident(g1,g2)
    c: PointOnObject(g2,g-1)
    c: Coincident(g2,g3)
    c: Coincident(g3,g4)
    c: Coincident(g4,g5)
    c: Coincident(g5,g0)
    c: Coincident(g-5,g6)
    c: Coincident(g6,g-6)
    c: Coincident(g6,g7)
    c: Coincident(g7,g-6)
    c: Coincident(g7,g8)
    c: Horizontal(g8)
    c: Coincident(g8,g9)
    c: Vertical(g9)
    c: Coincident(g9,g10)
    c: PointOnObject(g10,g-1)
    c: Coincident(g10,g11)
    c: Coincident(g11,g6)
    c: Horizontal(g0,g3)
    c: Horizontal(g3,g9)
    c: Horizontal(g5)
    c: Equal(g5,g8)
    c: Equal(g8,g11)
    c: Equal(g11,g2)
    c: Parallel(g3,g1)
    c: Distance(g8) = 1
FEATURE [PartDesign::Pad] Pad147
  BaseFeature = -> Pad146
  Length = 41
  Length2 = 100
  Profile = -> Sketch275
  Refine = true
  Type = 0
FEATURE [Sketcher::SketchObject] Sketch276
  ExternalGeometry = -> [Pad147]
  MapMode = 5
  Placement = pos=(0,0,-41) rot=(1,0,0;3.14159rad)
  Support = -> [Pad147]
  sketch-geometry (9):
    g0: LineSegment StartX=-11.5 StartY=0 StartZ=0 EndX=-14.5 EndY=-17.5 EndZ=0
    g1: LineSegment StartX=-14.5 StartY=-17.5 StartZ=0 EndX=-7.5 EndY=-34.5 EndZ=0
    g2: LineSegment StartX=-7.5 StartY=-34.5 StartZ=0 EndX=-6.5 EndY=-34.5 EndZ=0
    g3: LineSegment StartX=-6.5 StartY=-34.5 StartZ=0 EndX=-6.5 EndY=0 EndZ=0
    g4: LineSegment StartX=-6.5 StartY=0 StartZ=0 EndX=-11.5 EndY=0 EndZ=0
    g5: LineSegment StartX=20.5 StartY=-17.5 StartZ=0 EndX=6.5 EndY=-17.5 EndZ=0
    g6: LineSegment StartX=6.5 StartY=-17.5 StartZ=0 EndX=6.5 EndY=0 EndZ=0
    g7: LineSegment StartX=6.5 StartY=0 StartZ=0 EndX=11.5 EndY=0 EndZ=0
    g8: LineSegment StartX=11.5 StartY=0 StartZ=0 EndX=20.5 EndY=-17.5 EndZ=0
  constraints (21):
    c: Coincident(g-3,g0)
    c: Coincident(g0,g-4)
    c: Coincident(g0,g1)
    c: Coincident(g1,g-4)
    c: Coincident(g1,g2)
    c: Coincident(g2,g-6)
    c: Coincident(g2,g3)
    c: PointOnObject(g3,g-1)
    c: Vertical(g3)
    c: Coincident(g3,g4)
    c: Coincident(g4,g0)
    c: Coincident(g-5,g5)
    c: Horizontal(g5)
    c: Coincident(g5,g6)
    c: PointOnObject(g6,g-1)
    c: Vertical(g6)
    c: Coincident(g6,g7)
    c: Coincident(g7,g-5)
    c: Coincident(g7,g8)
    c: Distance(g7) = 5
    c: Coincident(g8,g5)
FEATURE [PartDesign::Pad] Pad148
  BaseFeature = -> Pad147
  Length = 1
  Length2 = 100
  Profile = -> Sketch276
  Refine = true
  Reversed = true
  Type = 0
FEATURE [Sketcher::SketchObject] Sketch312
  MapMode = 5
  Placement = pos=(0,0,0) rot=(0.57735,0.57735,0.57735;2.0944rad)
  Support = -> [YZ_Plane101]
  sketch-geometry (12):
    g0: LineSegment StartX=-12.5 StartY=-12 StartZ=0 EndX=-12.5 EndY=5 EndZ=0
    g1: LineSegment StartX=-9.5 StartY=8 StartZ=0 EndX=9.5 EndY=8 EndZ=0
    g2: LineSegment StartX=12.5 StartY=5 StartZ=0 EndX=12.5 EndY=-7 EndZ=0
    g3: LineSegment StartX=12.5 StartY=-7 StartZ=0 EndX=13.5 EndY=-7 EndZ=0
    g4: LineSegment StartX=13.5 StartY=-7 StartZ=0 EndX=13.5 EndY=5 EndZ=0
    g5: LineSegment StartX=9.5 StartY=9 StartZ=0 EndX=-9.5 EndY=9 EndZ=0
    g6: LineSegment StartX=-13.5 StartY=5 StartZ=0 EndX=-13.5 EndY=-12 EndZ=0
    g7: LineSegment StartX=-13.5 StartY=-12 StartZ=0 EndX=-12.5 EndY=-12 EndZ=0
    g8: ArcOfCircle CenterX=-9.5 CenterY=5 CenterZ=0 NormalX=0 NormalY=0 NormalZ=1 AngleXU=0 Radius=4 StartAngle=1.5708 EndAngle=3.14159
    g9: ArcOfCircle CenterX=-9.5 CenterY=5 CenterZ=0 NormalX=0 NormalY=0 NormalZ=1 AngleXU=0 Radius=3 StartAngle=1.5708 EndAngle=3.14159
    g10: ArcOfCircle CenterX=9.5 CenterY=5 CenterZ=0 NormalX=0 NormalY=0 NormalZ=1 AngleXU=0 Radius=3 StartAngle=0 EndAngle=1.5708
    g11: ArcOfCircle CenterX=9.5 CenterY=5 CenterZ=0 NormalX=0 NormalY=0 NormalZ=1 AngleXU=0 Radius=4 StartAngle=1e-16 EndAngle=1.5708
  constraints (29):
    c: Vertical(g0)
    c: Horizontal(g1)
    c: Vertical(g2)
    c: Coincident(g2,g3)
    c: Horizontal(g3)
    c: Coincident(g3,g4)
    c: Vertical(g4)
    c: Coincident(g6,g7)
    c: Coincident(g7,g0)
    c: Horizontal(g7)
    c: Tangent(g5,g8) = -1.5708
    c: Tangent(g6,g8) = -1.5708
    c: Tangent(g1,g9) = 1.5708
    c: Tangent(g0,g9) = 1.5708
    c: Tangent(g1,g10) = 1.5708
    c: Tangent(g2,g10) = 1.5708
    c: Tangent(g5,g11) = -1.5708
    c: Tangent(g4,g11) = -1.5708
    c: Coincident(g11,g10)
    c: Coincident(g8,g9)
    c: Equal(g10,g9)
    c: Distance(g7) = 1
    c: Radius(g8) = 4
    c: Symmetric(g5,g5,g-2)
    c: DistanceY(g-1,g1) = 8
    c: DistanceY(g2,g1) = 15
    c: Vertical(g6)
    c: DistanceX(g0,g2) = 25
    c: DistanceY(g6,g1) = 20
FEATURE [PartDesign::Pad] Pad170
  Length = 14
  Length2 = 12
  Placement = pos=(0,0,0) rot=(0.57735,0.57735,0.57735;2.0944rad)
  Profile = -> Sketch312
  Refine = true
  Type = 4
FEATURE [PartDesign::Plane] DatumPlane007
  AttachmentOffset = pos=(1,0,0) rot=(0,-1,0;0.628319rad)
  Length = 83.5704
  MapMode = 5
  Placement = pos=(1,0,0) rot=(0,-1,0;0.628319rad)
  ResizeMode = 0
  Support = -> [XY_Plane102]
  Width = 61.9669
FEATURE [Sketcher::SketchObject] Sketch313
  ExternalGeometry = -> [Pad170]
  MapMode = 5
  Placement = pos=(1,0,0) rot=(0,-1,0;0.628319rad)
  Support = -> [DatumPlane007]
  sketch-geometry (10):
    g0: LineSegment StartX=-0.597276 StartY=13.5 StartZ=0 EndX=6.40272 EndY=6.5 EndZ=0
    g1: LineSegment StartX=6.40272 StartY=6.5 StartZ=0 EndX=6.40272 EndY=-10.5 EndZ=0
    g2: LineSegment StartX=6.40272 StartY=-10.5 StartZ=0 EndX=3.40272 EndY=-13.5 EndZ=0
    g3: LineSegment [constr] StartX=6.40272 StartY=13.5 StartZ=0 EndX=6.40272 EndY=6.5 EndZ=0
    g4: LineSegment [constr] StartX=-0.597276 StartY=13.5 StartZ=0 EndX=6.40272 EndY=13.5 EndZ=0
    g5: LineSegment [constr] StartX=6.40272 StartY=-10.5 StartZ=0 EndX=6.40272 EndY=-13.5 EndZ=0
    g6: LineSegment [constr] StartX=3.40272 StartY=-13.5 StartZ=0 EndX=6.40272 EndY=-13.5 EndZ=0
    g7: LineSegment StartX=-0.597276 StartY=13.5 StartZ=0 EndX=15.8073 EndY=13.5 EndZ=0
    g8: LineSegment StartX=15.8073 StartY=13.5 StartZ=0 EndX=15.8073 EndY=-13.5 EndZ=0
    g9: LineSegment StartX=3.40272 StartY=-13.5 StartZ=0 EndX=15.8073 EndY=-13.5 EndZ=0
  constraints (27):
    c: PointOnObject(g0,g-3)
    c: Coincident(g1,g0)
    c: Vertical(g1)
    c: Coincident(g2,g1)
    c: PointOnObject(g2,g-4)
    c: Vertical(g0,g-5)
    c: Coincident(g3,g-5)
    c: Coincident(g3,g0)
    c: Coincident(g4,g0)
    c: Coincident(g4,g3)
    c: Equal(g4,g3)
    c: Coincident(g5,g1)
    c: PointOnObject(g5,g-4)
    c: Vertical(g5)
    c: Coincident(g6,g2)
    c: Coincident(g6,g5)
    c: Equal(g6,g5)
    c: Distance(g6) = 3
    c: Distance(g4) = 7
    c: Coincident(g7,g0)
    c: Horizontal(g7)
    c: Coincident(g8,g7)
    c: PointOnObject(g8,g-4)
    c: Coincident(g9,g2)
    c: Coincident(g9,g8)
    c: Vertical(g8)
    c: PointOnObject(g-6,g8)
FEATURE [PartDesign::Pocket] Pocket130
  BaseFeature = -> Pad170
  Length = 5
  Length2 = 100
  Midplane = true
  Placement = pos=(0,0,0) rot=(0.57735,0.57735,0.57735;2.0944rad)
  Profile = -> Sketch313
  Refine = true
  Type = 1
FEATURE [Sketcher::SketchObject] Sketch314
  ExternalGeometry = -> [Sketch313]
  MapMode = 5
  Placement = pos=(1,0,0) rot=(0,-1,0;0.628319rad)
  Support = -> [DatumPlane007]
  sketch-geometry (8):
    g0: LineSegment StartX=-0.597276 StartY=13.5 StartZ=0 EndX=6.40272 EndY=6.5 EndZ=0
    g1: LineSegment StartX=6.40272 StartY=6.5 StartZ=0 EndX=6.40272 EndY=-10.5 EndZ=0
    g2: LineSegment StartX=6.40272 StartY=-10.5 StartZ=0 EndX=3.40272 EndY=-13.5 EndZ=0
    g3: LineSegment StartX=3.40272 StartY=-13.5 StartZ=0 EndX=2.40272 EndY=-13.5 EndZ=0
    g4: LineSegment StartX=2.40272 StartY=-13.5 StartZ=0 EndX=5.40272 EndY=-10.5 EndZ=0
    g5: LineSegment StartX=5.40272 StartY=-10.5 StartZ=0 EndX=5.40272 EndY=6.5 EndZ=0
    g6: LineSegment StartX=5.40272 StartY=6.5 StartZ=0 EndX=-1.59728 EndY=13.5 EndZ=0
    g7: LineSegment StartX=-1.59728 StartY=13.5 StartZ=0 EndX=-0.597276 EndY=13.5 EndZ=0
  constraints (20):
    c: Coincident(g-3,g0)
    c: Coincident(g0,g-4)
    c: Coincident(g0,g1)
    c: Coincident(g1,g-5)
    c: Coincident(g1,g2)
    c: Coincident(g2,g-5)
    c: Coincident(g2,g3)
    c: Horizontal(g3)
    c: Coincident(g3,g4)
    c: Coincident(g4,g5)
    c: Vertical(g5)
    c: Coincident(g5,g6)
    c: Coincident(g6,g7)
    c: Coincident(g7,g0)
    c: Horizontal(g7)
    c: Parallel(g0,g6)
    c: Parallel(g4,g2)
    c: Horizontal(g4,g1)
    c: Horizontal(g5,g0)
    c: Distance(g7) = 1
FEATURE [PartDesign::Pad] Pad171
  BaseFeature = -> Pocket130
  Length = 11
  Length2 = 25
  Placement = pos=(0,0,0) rot=(0.57735,0.57735,0.57735;2.0944rad)
  Profile = -> Sketch314
  Refine = true
  Type = 4
FEATURE [Sketcher::SketchObject] Sketch315
  ExternalGeometry = -> [Sketch312,Pad171]
  MapMode = 5
  Placement = pos=(0,0,0) rot=(0.57735,0.57735,0.57735;2.0944rad)
  Support = -> [YZ_Plane101]
  sketch-geometry (13):
    g0: LineSegment StartX=-13.5 StartY=-12 StartZ=0 EndX=-12.5 EndY=-12 EndZ=0
    g1: LineSegment StartX=-10.5 StartY=-7 StartZ=0 EndX=13.5 EndY=-7 EndZ=0
    g2: LineSegment StartX=-13.5 StartY=-12 StartZ=0 EndX=-13.5 EndY=5 EndZ=0
    g3: LineSegment StartX=13.5 StartY=5 StartZ=0 EndX=13.5 EndY=-7 EndZ=0
    g4: LineSegment StartX=9.5 StartY=9 StartZ=0 EndX=-9.5 EndY=9 EndZ=0
    g5: ArcOfCircle CenterX=-9.5 CenterY=5 CenterZ=0 NormalX=0 NormalY=0 NormalZ=1 AngleXU=0 Radius=4 StartAngle=1.5708 EndAngle=3.14159
    g6: ArcOfCircle CenterX=9.5 CenterY=5 CenterZ=0 NormalX=0 NormalY=0 NormalZ=1 AngleXU=0 Radius=4 StartAngle=3.285e-13 EndAngle=1.5708
    g7: LineSegment StartX=-25 StartY=25 StartZ=0 EndX=25 EndY=25 EndZ=0
    g8: LineSegment StartX=25 StartY=25 StartZ=0 EndX=25 EndY=-25 EndZ=0
    g9: LineSegment StartX=25 StartY=-25 StartZ=0 EndX=-25 EndY=-25 EndZ=0
    g10: LineSegment StartX=-25 StartY=-25 StartZ=0 EndX=-25 EndY=25 EndZ=0
    g11: LineSegment StartX=-10.5 StartY=-7 StartZ=0 EndX=-10.5 EndY=-8 EndZ=0
    g12: LineSegment StartX=-10.5 StartY=-8 StartZ=0 EndX=-12.5 EndY=-12 EndZ=0
  constraints (33):
    c: Coincident(g1,g-6)
    c: Horizontal(g1)
    c: Coincident(g2,g-7)
    c: Coincident(g3,g-6)
    c: Coincident(g3,g1)
    c: Coincident(g4,g-5)
    c: Coincident(g4,g-5)
    c: Coincident(g5,g4)
    c: Coincident(g5,g2)
    c: Coincident(g6,g4)
    c: Coincident(g6,g3)
    c: Equal(g6,g-3)
    c: Equal(g5,g-4)
    c: Coincident(g7,g8)
    c: Coincident(g8,g9)
    c: Coincident(g9,g10)
    c: Coincident(g10,g7)
    c: Horizontal(g7)
    c: Horizontal(g9)
    c: Vertical(g8)
    c: Vertical(g10)
    c: Symmetric(g7,g8,g-1)
    c: Equal(g8,g7)
    c: Distance(g8) = 50
    c: Coincident(g0,g2)
    c: Coincident(g0,g-7)
    c: Coincident(g0,g-8)
    c: PointOnObject(g1,g-9)
    c: Coincident(g1,g11)
    c: PointOnObject(g11,g-9)
    c: Coincident(g11,g12)
    c: Coincident(g12,g0)
    c: Equal(g11,g0)
FEATURE [PartDesign::Pocket] Pocket131
  BaseFeature = -> Pad171
  Length = 5
  Length2 = 100
  Midplane = true
  Placement = pos=(0,0,0) rot=(0.57735,0.57735,0.57735;2.0944rad)
  Profile = -> Sketch315
  Refine = true
  Type = 1
FEATURE [Sketcher::SketchObject] Sketch316
  ExternalGeometry = -> [Pocket131]
  MapMode = 5
  Placement = pos=(2e-15,-3.1e-15,-7) rot=(0.707107,0.707107,0;3.14159rad)
  Support = -> [Pocket131]
  sketch-geometry (7):
    g0: LineSegment StartX=13.5 StartY=-12 StartZ=0 EndX=13.5 EndY=24 EndZ=0
    g1: LineSegment StartX=13.5 StartY=24 StartZ=0 EndX=-10.5 EndY=24 EndZ=0
    g2: LineSegment StartX=-10.5 StartY=24 StartZ=0 EndX=-10.5 EndY=12.7639 EndZ=0
    g3: LineSegment StartX=-10.5 StartY=12.7639 StartZ=0 EndX=6.5 EndY=12.7639 EndZ=0
    g4: LineSegment StartX=6.5 StartY=12.7639 StartZ=0 EndX=12.5 EndY=5.34752 EndZ=0
    g5: LineSegment StartX=12.5 StartY=5.34752 StartZ=0 EndX=12.5 EndY=-12 EndZ=0
    g6: LineSegment StartX=12.5 StartY=-12 StartZ=0 EndX=13.5 EndY=-12 EndZ=0
  constraints (17):
    c: Coincident(g-3,g0)
    c: Vertical(g0)
    c: Coincident(g0,g1)
    c: Horizontal(g1)
    c: Coincident(g1,g2)
    c: Coincident(g2,g3)
    c: Coincident(g3,g4)
    c: Coincident(g4,g-4)
    c: Coincident(g4,g5)
    c: Vertical(g5)
    c: Coincident(g5,g6)
    c: Coincident(g6,g0)
    c: Horizontal(g6)
    c: Vertical(g2)
    c: Coincident(g3,g-5)
    c: Coincident(g2,g-5)
    c: Distance(g0) = 36
FEATURE [PartDesign::Pad] Pad172
  BaseFeature = -> Pocket131
  Length = 1
  Length2 = 100
  Placement = pos=(0,0,0) rot=(0.57735,0.57735,0.57735;2.0944rad)
  Profile = -> Sketch316
  Refine = true
  Type = 0
FEATURE [Sketcher::SketchObject] Sketch317
  ExternalGeometry = -> [Pad172]
  MapMode = 5
  Placement = pos=(4.6e-15,13.5,-2.79e-14) rot=(0.57735,0.57735,0.57735;4.18879rad)
  Support = -> [Pad172]
  sketch-geometry (4):
    g0: LineSegment StartX=-7 StartY=24 StartZ=0 EndX=-27 EndY=24 EndZ=0
    g1: LineSegment StartX=-27 StartY=24 StartZ=0 EndX=-27 EndY=25 EndZ=0
    g2: LineSegment StartX=-27 StartY=25 StartZ=0 EndX=-7 EndY=25 EndZ=0
    g3: LineSegment StartX=-7 StartY=25 StartZ=0 EndX=-7 EndY=24 EndZ=0
  constraints (11):
    c: Coincident(g0,g1)
    c: Coincident(g1,g2)
    c: Coincident(g2,g3)
    c: Coincident(g3,g0)
    c: Horizontal(g0)
    c: Horizontal(g2)
    c: Vertical(g1)
    c: Vertical(g3)
    c: Coincident(g0,g-3)
    c: Distance(g3) = 1
    c: Distance(g2) = 20
FEATURE [PartDesign::Pad] Pad173
  BaseFeature = -> Pad172
  Length = 10
  Length2 = 100
  Placement = pos=(0,0,0) rot=(0.57735,0.57735,0.57735;2.0944rad)
  Profile = -> Sketch317
  Refine = true
  Reversed = true
  Type = 3
  UpToFace = -> Pad172 [Face21]
FEATURE [Sketcher::SketchObject] Sketch318
  ExternalGeometry = -> [Sketch312]
  MapMode = 5
  Placement = pos=(-12,3.28e-14,-5.16e-14) rot=(0.57735,0.57735,-0.57735;4.18879rad)
  Support = -> [Pad173]
  sketch-geometry (6):
    g0: LineSegment StartX=13.5 StartY=7 StartZ=0 EndX=-13.5 EndY=7 EndZ=0
    g1: LineSegment StartX=-13.5 StartY=7 StartZ=0 EndX=-13.5 EndY=-5 EndZ=0
    g2: LineSegment StartX=13.5 StartY=-5 StartZ=0 EndX=13.5 EndY=7 EndZ=0
    g3: ArcOfCircle CenterX=-9.5 CenterY=-5 CenterZ=0 NormalX=0 NormalY=0 NormalZ=1 AngleXU=0 Radius=4 StartAngle=3.14159 EndAngle=4.71239
    g4: ArcOfCircle CenterX=9.5 CenterY=-5 CenterZ=0 NormalX=0 NormalY=0 NormalZ=1 AngleXU=0 Radius=4 StartAngle=4.71239 EndAngle=6.28319
    g5: LineSegment StartX=-9.5 StartY=-9 StartZ=0 EndX=9.5 EndY=-9 EndZ=0
  constraints (15):
    c: Coincident(g0,g1)
    c: Coincident(g2,g0)
    c: Horizontal(g0)
    c: Vertical(g1)
    c: Coincident(g3,g1)
    c: Coincident(g4,g2)
    c: Coincident(g5,g3)
    c: Coincident(g5,g4)
    c: Coincident(g0,g-4)
    c: Coincident(g2,g-4)
    c: Coincident(g4,g-3)
    c: Coincident(g3,g-5)
    c: Coincident(g-5,g1)
    c: Equal(g-5,g3)
    c: Equal(g-3,g4)
FEATURE [PartDesign::Pad] Pad174
  BaseFeature = -> Pad173
  Length = 1
  Length2 = 100
  Placement = pos=(0,0,0) rot=(0.57735,0.57735,0.57735;2.0944rad)
  Profile = -> Sketch318
  Refine = true
  Type = 0
FEATURE [Sketcher::SketchObject] Sketch319
  ExternalGeometry = -> [Sketch318]
  MapMode = 5
  Placement = pos=(-13,3.51e-14,-5.77e-14) rot=(0.57735,0.57735,-0.57735;4.18879rad)
  Support = -> [Pad174]
  sketch-geometry (4):
    g0: LineSegment StartX=13.5 StartY=7 StartZ=0 EndX=-13.5 EndY=7 EndZ=0
    g1: LineSegment StartX=-13.5 StartY=7 StartZ=0 EndX=-13.5 EndY=27 EndZ=0
    g2: LineSegment StartX=-13.5 StartY=27 StartZ=0 EndX=13.5 EndY=27 EndZ=0
    g3: LineSegment StartX=13.5 StartY=27 StartZ=0 EndX=13.5 EndY=7 EndZ=0
  constraints (10):
    c: Coincident(g0,g1)
    c: Coincident(g1,g2)
    c: Coincident(g2,g3)
    c: Coincident(g3,g0)
    c: Horizontal(g2)
    c: Vertical(g1)
    c: Vertical(g3)
    c: Coincident(g0,g-3)
    c: Coincident(g0,g-3)
    c: Distance(g3) = 20
FEATURE [PartDesign::Pad] Pad175
  BaseFeature = -> Pad174
  Length = 1
  Length2 = 100
  Placement = pos=(0,0,0) rot=(0.57735,0.57735,0.57735;2.0944rad)
  Profile = -> Sketch319
  Refine = true
  Reversed = true
  Type = 0
FEATURE [Sketcher::SketchObject] Sketch320
  ExternalGeometry = -> [Sketch317,Sketch319]
  MapMode = 5
  Placement = pos=(8.9e-15,-5.1e-14,-27) rot=(0.707107,0.707107,0;3.14159rad)
  Support = -> [Pad175]
  sketch-geometry (8):
    g0: LineSegment StartX=13.5 StartY=25 StartZ=0 EndX=13.5 EndY=5 EndZ=0
    g1: LineSegment StartX=13.5 StartY=5 StartZ=0 EndX=4.5 EndY=11 EndZ=0
    g2: LineSegment StartX=4.5 StartY=11 StartZ=0 EndX=4.5 EndY=25 EndZ=0
    g3: LineSegment StartX=4.5 StartY=25 StartZ=0 EndX=13.5 EndY=25 EndZ=0
    g4: LineSegment StartX=13.5 StartY=-13 StartZ=0 EndX=4.5 EndY=-13 EndZ=0
    g5: LineSegment StartX=4.5 StartY=-13 StartZ=0 EndX=4.5 EndY=-8 EndZ=0
    g6: LineSegment StartX=4.5 StartY=-8 StartZ=0 EndX=13.5 EndY=-8 EndZ=0
    g7: LineSegment StartX=13.5 StartY=-8 StartZ=0 EndX=13.5 EndY=-13 EndZ=0
  constraints (22):
    c: Coincident(g0,g-3)
    c: Vertical(g0)
    c: Coincident(g0,g1)
    c: Coincident(g1,g2)
    c: Vertical(g2)
    c: Coincident(g2,g3)
    c: Coincident(g3,g0)
    c: Distance(g3) = 9
    c: DistanceY(g0,g1) = 6
    c: Distance(g0) = 20
    c: Horizontal(g3)
    c: Coincident(g4,g5)
    c: Coincident(g5,g6)
    c: Coincident(g6,g7)
    c: Coincident(g7,g4)
    c: Horizontal(g4)
    c: Horizontal(g6)
    c: Vertical(g5)
    c: Vertical(g7)
    c: Coincident(g4,g-4)
    c: Vertical(g5,g1)
    c: Distance(g7) = 5
FEATURE [PartDesign::Pad] Pad176
  BaseFeature = -> Pad175
  Length = 1
  Length2 = 100
  Placement = pos=(0,0,0) rot=(0.57735,0.57735,0.57735;2.0944rad)
  Profile = -> Sketch320
  Refine = true
  Type = 0
FEATURE [Sketcher::SketchObject] Sketch321
  ExternalGeometry = -> [Sketch319,Sketch317]
  MapMode = 5
  Placement = pos=(2.32e-14,13.5,-1.16e-14) rot=(0.57735,0.57735,0.57735;4.18879rad)
  Support = -> [Pad176]
  sketch-geometry (4):
    g0: LineSegment StartX=-27 StartY=24 StartZ=0 EndX=-7 EndY=24 EndZ=0
    g1: LineSegment StartX=-7 StartY=24 StartZ=0 EndX=-7 EndY=-13 EndZ=0
    g2: LineSegment StartX=-7 StartY=-13 StartZ=0 EndX=-27 EndY=-13 EndZ=0
    g3: LineSegment StartX=-27 StartY=-13 StartZ=0 EndX=-27 EndY=24 EndZ=0
  constraints (10):
    c: Coincident(g0,g1)
    c: Coincident(g1,g2)
    c: Coincident(g2,g3)
    c: Coincident(g3,g0)
    c: Horizontal(g0)
    c: Horizontal(g2)
    c: Vertical(g1)
    c: Vertical(g3)
    c: Coincident(g0,g-4)
    c: Coincident(g1,g-3)
FEATURE [PartDesign::Pad] Pad177
  BaseFeature = -> Pad176
  Length = 1
  Length2 = 100
  Placement = pos=(0,0,0) rot=(0.57735,0.57735,0.57735;2.0944rad)
  Profile = -> Sketch321
  Refine = true
  Reversed = true
  Type = 0
FEATURE [Sketcher::SketchObject] Sketch322
  ExternalGeometry = -> [Sketch320]
  MapMode = 5
  Placement = pos=(-13,3.83e-14,-5.81e-14) rot=(0.57735,0.57735,-0.57735;4.18879rad)
  Support = -> [Pad177]
  sketch-geometry (4):
    g0: LineSegment StartX=12.5 StartY=22 StartZ=0 EndX=9.5 EndY=22 EndZ=0
    g1: LineSegment StartX=9.5 StartY=22 StartZ=0 EndX=9.5 EndY=14 EndZ=0
    g2: LineSegment StartX=9.5 StartY=14 StartZ=0 EndX=12.5 EndY=14 EndZ=0
    g3: LineSegment StartX=12.5 StartY=14 StartZ=0 EndX=12.5 EndY=22 EndZ=0
  constraints (12):
    c: Coincident(g0,g1)
    c: Coincident(g1,g2)
    c: Coincident(g2,g3)
    c: Coincident(g3,g0)
    c: Horizontal(g0)
    c: Horizontal(g2)
    c: Vertical(g1)
    c: Vertical(g3)
    c: DistanceY(g0,g-3) = 5
    c: DistanceX(g0,g-3) = 1
    c: Distance(g2) = 3
    c: Distance(g3) = 8
FEATURE [PartDesign::Pocket] Pocket132
  BaseFeature = -> Pad177
  Length = 5
  Length2 = 100
  Placement = pos=(0,0,0) rot=(0.57735,0.57735,0.57735;2.0944rad)
  Profile = -> Sketch322
  Refine = true
  Type = 2
FEATURE [Sketcher::SketchObject] Sketch323
  ExternalGeometry = -> [Sketch317]
  MapMode = 5
  Placement = pos=(6.7e-15,-7.6e-15,-7) rot=(0,0,-1;1.5708rad)
  Support = -> [Pocket132]
  sketch-geometry (3):
    g0: LineSegment StartX=-13.5 StartY=25 StartZ=0 EndX=-13.5 EndY=22.5 EndZ=0
    g1: LineSegment StartX=-13.5 StartY=22.5 StartZ=0 EndX=-11 EndY=25 EndZ=0
    g2: LineSegment StartX=-11 StartY=25 StartZ=0 EndX=-13.5 EndY=25 EndZ=0
  constraints (8):
    c: Coincident(g0,g-3)
    c: Coincident(g0,g1)
    c: Coincident(g1,g2)
    c: Coincident(g2,g0)
    c: Horizontal(g2)
    c: Vertical(g0)
    c: Equal(g2,g0)
    c: Distance(g2) = 2.5
FEATURE [PartDesign::Pocket] Pocket133
  BaseFeature = -> Pocket132
  Length = 5
  Length2 = 100
  Placement = pos=(0,0,0) rot=(0.57735,0.57735,0.57735;2.0944rad)
  Profile = -> Sketch323
  Refine = true
  Type = 1
FEATURE [Sketcher::SketchObject] Sketch324
  ExternalGeometry = -> [Pocket133]
  MapMode = 5
  Placement = pos=(18,18,-1.43e-14) rot=(0.678598,0.281085,0.678598;3.68962rad)
  Support = -> [Pocket133]
  sketch-geometry (4):
    g0: LineSegment StartX=-28 StartY=9.89949 StartZ=0 EndX=-7 EndY=9.89949 EndZ=0
    g1: LineSegment StartX=-7 StartY=9.89949 StartZ=0 EndX=-7 EndY=6.36396 EndZ=0
    g2: LineSegment StartX=-7 StartY=6.36396 StartZ=0 EndX=-28 EndY=6.36396 EndZ=0
    g3: LineSegment StartX=-28 StartY=6.36396 StartZ=0 EndX=-28 EndY=9.89949 EndZ=0
  constraints (10):
    c: Coincident(g0,g1)
    c: Coincident(g1,g2)
    c: Coincident(g2,g3)
    c: Coincident(g3,g0)
    c: Horizontal(g0)
    c: Horizontal(g2)
    c: Vertical(g1)
    c: Vertical(g3)
    c: Coincident(g0,g-3)
    c: Coincident(g1,g-4)
FEATURE [PartDesign::Pad] Pad178
  BaseFeature = -> Pocket133
  Length = 0.4
  Length2 = 100
  Placement = pos=(0,0,0) rot=(0.57735,0.57735,0.57735;2.0944rad)
  Profile = -> Sketch324
  Refine = true
  Reversed = true
  Type = 0
FEATURE [Sketcher::SketchObject] Sketch325
  ExternalGeometry = -> [Sketch320,Sketch319,Pad178]
  MapMode = 5
  Placement = pos=(2.7e-14,13.5,-2.24e-14) rot=(0.57735,0.57735,0.57735;4.18879rad)
  Support = -> [Pad178]
  sketch-geometry (27):
    g0: GeomPoint X=-14 Y=-1 Z=0
    g1: GeomPoint X=-24 Y=20 Z=0
    g2: LineSegment StartX=-14 StartY=-0.752786 StartZ=0 EndX=-27 EndY=8.69227 EndZ=0
    g3: LineSegment StartX=-26.6 StartY=7.90722 StartZ=0 EndX=-14 EndY=-1.24721 EndZ=0
    g4: LineSegment StartX=-27 StartY=25 StartZ=0 EndX=-26.6 EndY=25 EndZ=0
    g5: LineSegment StartX=-26.6 StartY=7.90722 StartZ=0 EndX=-26.6 EndY=4.6 EndZ=0
    g6: LineSegment StartX=-26.6 StartY=4.6 StartZ=0 EndX=-27 EndY=4.6 EndZ=0
    g7: LineSegment StartX=-24 StartY=20.2472 StartZ=0 EndX=-26.6 EndY=22.1362 EndZ=0
    g8: LineSegment StartX=-26.6 StartY=25 StartZ=0 EndX=-26.6 EndY=22.1362 EndZ=0
    g9: LineSegment StartX=-27 StartY=21.9324 StartZ=0 EndX=-24 EndY=19.7528 EndZ=0
    g10: LineSegment StartX=-24 StartY=20.2472 StartZ=0 EndX=-8 EndY=8.62253 EndZ=0
    g11: LineSegment StartX=-8 StartY=8.62253 StartZ=0 EndX=-8 EndY=5.07407 EndZ=0
    g12: LineSegment StartX=-8 StartY=5.07407 StartZ=0 EndX=0.799941 EndY=-1.31946 EndZ=0
    g13: LineSegment StartX=0.799941 StartY=-1.81389 StartZ=0 EndX=-8.4 EndY=4.87026 EndZ=0
    g14: LineSegment StartX=-8.4 StartY=4.87026 StartZ=0 EndX=-8.4 EndY=8.41872 EndZ=0
    g15: LineSegment StartX=-8.4 StartY=8.41872 StartZ=0 EndX=-24 EndY=19.7528 EndZ=0
    g16: LineSegment [constr] StartX=-8.4 StartY=8.41872 StartZ=0 EndX=-8 EndY=8.41872 EndZ=0
    g17: LineSegment [constr] StartX=-8.4 StartY=8.41872 StartZ=0 EndX=-8.16489 EndY=8.74233 EndZ=0
    g18: LineSegment [constr] StartX=-8 StartY=5.07407 StartZ=0 EndX=-8.23511 EndY=4.75046 EndZ=0
    g19: LineSegment StartX=-14 StartY=-0.752786 StartZ=0 EndX=0.799941 EndY=-11.5056 EndZ=0
    g20: LineSegment StartX=0.799941 StartY=-11.5056 StartZ=0 EndX=0.799941 EndY=-12 EndZ=0
    g21: LineSegment StartX=0.799941 StartY=-12 StartZ=0 EndX=-14 EndY=-1.24721 EndZ=0
    g22: LineSegment [constr] StartX=0.799941 StartY=-1.31946 StartZ=0 EndX=0.799941 EndY=-0.319465 EndZ=0
    g23: LineSegment StartX=-27 StartY=21.9324 StartZ=0 EndX=-27 EndY=25 EndZ=0
    g24: LineSegment StartX=-27 StartY=8.69227 StartZ=0 EndX=-27 EndY=4.6 EndZ=0
    g25: LineSegment [constr] StartX=-26.6 StartY=7.90722 StartZ=0 EndX=-26.3649 EndY=8.23083 EndZ=0
    g26: LineSegment StartX=0.799941 StartY=-1.31946 StartZ=0 EndX=0.799941 EndY=-1.81389 EndZ=0
  constraints (76):
    c: DistanceY(g1,g-3) = 5
    c: DistanceX(g-3,g1) = 3
    c: DistanceY(g-4,g0) = 12
    c: DistanceX(g0,g-4) = 7
    c: Coincident(g-3,g4)
    c: Horizontal(g4)
    c: Coincident(g3,g5)
    c: Coincident(g5,g6)
    c: Horizontal(g6)
    c: Distance(g6) = 0.4
    c: Vertical(g5)
    c: Parallel(g3,g2)
    c: Parallel(g2,g-5)
    c: Symmetric(g2,g3,g0)
    c: Vertical(g2,g3)
    c: Coincident(g8,g4)
    c: Coincident(g8,g7)
    c: Vertical(g8)
    c: Symmetric(g7,g9,g1)
    c: Vertical(g7,g9)
    c: Parallel(g2,g9)
    c: Parallel(g9,g7)
    c: Coincident(g10,g7)
    c: Coincident(g10,g11)
    c: Vertical(g11)
    c: Coincident(g11,g12)
    c: Coincident(g13,g14)
    c: Vertical(g14)
    c: Coincident(g14,g15)
    c: Coincident(g15,g9)
    c: Parallel(g10,g15)
    c: Parallel(g15,g9)
    c: Parallel(g9,g13)
    c: Parallel(g13,g12)
    c: Coincident(g16,g14)
    c: PointOnObject(g16,g11)
    c: Horizontal(g16)
    c: Coincident(g17,g14)
    c: PointOnObject(g17,g10)
    c: Perpendicular(g15,g17)
    c: Equal(g16,g17)
    c: Coincident(g18,g11)
    c: PointOnObject(g18,g13)
    c: Perpendicular(g12,g18)
    c: Equal(g18,g16)
    c: Coincident(g2,g19)
    c: Coincident(g19,g20)
    c: Vertical(g20)
    c: Coincident(g20,g21)
    c: Coincident(g21,g3)
    c: Parallel(g19,g21)
    c: Parallel(g21,g2)
    c: DistanceY(g-4,g20) = 1
    c: DistanceX(g10,g-5) = 1
    c: Coincident(g22,g12)
    c: PointOnObject(g22,g-5)
    c: Vertical(g22)
    c: Distance(g22) = 1
    c: PointOnObject(g9,g-3)
    c: Coincident(g23,g9)
    c: Coincident(g23,g4)
    c: PointOnObject(g2,g-3)
    c: Coincident(g24,g2)
    c: Coincident(g24,g6)
    c: Vertical(g24)
    c: Vertical(g7,g3)
    c: Coincident(g25,g3)
    c: PointOnObject(g25,g2)
    c: Perpendicular(g2,g25)
    c: Equal(g25,g6)
    c: Equal(g6,g16)
    c: Vertical(g12,g19)
    c: Distance(g-3,g6) = 0.4
    c: Coincident(g26,g12)
    c: Coincident(g26,g13)
    c: Vertical(g26)
FEATURE [PartDesign::Pocket] Pocket134
  BaseFeature = -> Pad178
  Length = 9.4
  Length2 = 100
  Placement = pos=(0,0,0) rot=(0.57735,0.57735,0.57735;2.0944rad)
  Profile = -> Sketch325
  Refine = true
  Type = 0
FEATURE [Sketcher::SketchObject] Sketch326
  ExternalGeometry = -> [Pocket134]
  MapMode = 5
  Placement = pos=(-2.31e-14,-13.5,-4.2e-15) rot=(0.57735,0.57735,-0.57735;2.0944rad)
  Support = -> [Pocket134]
  sketch-geometry (4):
    g0: LineSegment StartX=12 StartY=-12 StartZ=0 EndX=-0.799941 EndY=-12 EndZ=0
    g1: LineSegment StartX=-0.799941 StartY=-12 StartZ=0 EndX=-0.799941 EndY=-11.5056 EndZ=0
    g2: LineSegment StartX=-0.799941 StartY=-11.5056 StartZ=0 EndX=12 EndY=-11.5056 EndZ=0
    g3: LineSegment StartX=12 StartY=-11.5056 StartZ=0 EndX=12 EndY=-12 EndZ=0
  constraints (10):
    c: Coincident(g0,g1)
    c: Coincident(g1,g2)
    c: Coincident(g2,g3)
    c: Coincident(g3,g0)
    c: Horizontal(g0)
    c: Horizontal(g2)
    c: Vertical(g1)
    c: Vertical(g3)
    c: Coincident(g0,g-3)
    c: Coincident(g1,g-4)
FEATURE [Sketcher::SketchObject] Sketch327
  MapMode = 5
  Placement = pos=(0,0,0) rot=(0.57735,0.57735,0.57735;2.0944rad)
  Support = -> [YZ_Plane102]
  sketch-geometry (12):
    g0: LineSegment StartX=-12 StartY=-11 StartZ=0 EndX=-12 EndY=5 EndZ=0
    g1: LineSegment StartX=-9 StartY=8 StartZ=0 EndX=9 EndY=8 EndZ=0
    g2: LineSegment StartX=12 StartY=5 StartZ=0 EndX=12 EndY=-6 EndZ=0
    g3: LineSegment StartX=12 StartY=-6 StartZ=0 EndX=13 EndY=-6 EndZ=0
    g4: LineSegment StartX=13 StartY=-6 StartZ=0 EndX=13 EndY=5 EndZ=0
    g5: LineSegment StartX=9 StartY=9 StartZ=0 EndX=-9 EndY=9 EndZ=0
    g6: LineSegment StartX=-13 StartY=5 StartZ=0 EndX=-13 EndY=-11 EndZ=0
    g7: LineSegment StartX=-13 StartY=-11 StartZ=0 EndX=-12 EndY=-11 EndZ=0
    g8: ArcOfCircle CenterX=-9 CenterY=5 CenterZ=0 NormalX=0 NormalY=0 NormalZ=1 AngleXU=0 Radius=4 StartAngle=1.5708 EndAngle=3.14159
    g9: ArcOfCircle CenterX=-9 CenterY=5 CenterZ=0 NormalX=0 NormalY=0 NormalZ=1 AngleXU=0 Radius=3 StartAngle=1.5708 EndAngle=3.14159
    g10: ArcOfCircle CenterX=9 CenterY=5 CenterZ=0 NormalX=0 NormalY=0 NormalZ=1 AngleXU=0 Radius=3 StartAngle=0 EndAngle=1.5708
    g11: ArcOfCircle CenterX=9 CenterY=5 CenterZ=0 NormalX=0 NormalY=0 NormalZ=1 AngleXU=0 Radius=4 StartAngle=0 EndAngle=1.5708
  constraints (29):
    c: Vertical(g0)
    c: Horizontal(g1)
    c: Vertical(g2)
    c: Coincident(g2,g3)
    c: Horizontal(g3)
    c: Coincident(g3,g4)
    c: Vertical(g4)
    c: Coincident(g6,g7)
    c: Coincident(g7,g0)
    c: Horizontal(g7)
    c: Tangent(g5,g8) = -1.5708
    c: Tangent(g6,g8) = -1.5708
    c: Tangent(g1,g9) = 1.5708
    c: Tangent(g0,g9) = 1.5708
    c: Tangent(g1,g10) = 1.5708
    c: Tangent(g2,g10) = 1.5708
    c: Tangent(g5,g11) = -1.5708
    c: Tangent(g4,g11) = -1.5708
    c: Coincident(g11,g10)
    c: Coincident(g8,g9)
    c: Equal(g10,g9)
    c: Distance(g7) = 1
    c: Radius(g8) = 4
    c: Symmetric(g5,g5,g-2)
    c: DistanceY(g-1,g1) = 8
    c: DistanceY(g2,g1) = 14
    c: Vertical(g6)
    c: DistanceX(g0,g2) = 24
    c: DistanceY(g6,g1) = 19
FEATURE [PartDesign::Pad] Pad179
  Length = 14
  Length2 = 10
  Placement = pos=(0,0,0) rot=(0.57735,0.57735,0.57735;2.0944rad)
  Profile = -> Sketch327
  Refine = true
  Type = 4
FEATURE [PartDesign::Plane] DatumPlane008
  AttachmentOffset = pos=(1,0,0) rot=(0,-1,0;0.628319rad)
  Length = 84.6864
  MapMode = 5
  Placement = pos=(1,0,0) rot=(0,-1,0;0.628319rad)
  ResizeMode = 0
  Support = -> [XY_Plane103]
  Width = 62.0527
FEATURE [Sketcher::SketchObject] Sketch328
  ExternalGeometry = -> [Pad179]
  MapMode = 5
  Placement = pos=(1,0,0) rot=(0,-1,0;0.628319rad)
  Support = -> [DatumPlane008]
  sketch-geometry (10):
    g0: LineSegment StartX=-0.00949059 StartY=13 StartZ=0 EndX=6.99051 EndY=6 EndZ=0
    g1: LineSegment StartX=6.99051 StartY=6 StartZ=0 EndX=6.99051 EndY=-10 EndZ=0
    g2: LineSegment StartX=6.99051 StartY=-10 StartZ=0 EndX=3.99051 EndY=-13 EndZ=0
    g3: LineSegment [constr] StartX=6.99051 StartY=13 StartZ=0 EndX=6.99051 EndY=6 EndZ=0
    g4: LineSegment [constr] StartX=-0.00949059 StartY=13 StartZ=0 EndX=6.99051 EndY=13 EndZ=0
    g5: LineSegment [constr] StartX=6.99051 StartY=-10 StartZ=0 EndX=6.99051 EndY=-13 EndZ=0
    g6: LineSegment [constr] StartX=3.99051 StartY=-13 StartZ=0 EndX=6.99051 EndY=-13 EndZ=0
    g7: LineSegment StartX=-0.00949059 StartY=13 StartZ=0 EndX=15.8073 EndY=13 EndZ=0
    g8: LineSegment StartX=15.8073 StartY=13 StartZ=0 EndX=15.8073 EndY=-13 EndZ=0
    g9: LineSegment StartX=3.99051 StartY=-13 StartZ=0 EndX=15.8073 EndY=-13 EndZ=0
  constraints (27):
    c: PointOnObject(g0,g-3)
    c: Coincident(g1,g0)
    c: Vertical(g1)
    c: Coincident(g2,g1)
    c: PointOnObject(g2,g-4)
    c: Vertical(g0,g-5)
    c: Coincident(g3,g-5)
    c: Coincident(g3,g0)
    c: Coincident(g4,g0)
    c: Coincident(g4,g3)
    c: Equal(g4,g3)
    c: Coincident(g5,g1)
    c: PointOnObject(g5,g-4)
    c: Vertical(g5)
    c: Coincident(g6,g2)
    c: Coincident(g6,g5)
    c: Equal(g6,g5)
    c: Distance(g6) = 3
    c: Distance(g4) = 7
    c: Coincident(g7,g0)
    c: Horizontal(g7)
    c: Coincident(g8,g7)
    c: PointOnObject(g8,g-4)
    c: Coincident(g9,g2)
    c: Coincident(g9,g8)
    c: Vertical(g8)
    c: PointOnObject(g-6,g8)
FEATURE [PartDesign::Pocket] Pocket136
  BaseFeature = -> Pad179
  Length = 5
  Length2 = 100
  Midplane = true
  Placement = pos=(0,0,0) rot=(0.57735,0.57735,0.57735;2.0944rad)
  Profile = -> Sketch328
  Refine = true
  Type = 1
FEATURE [Sketcher::SketchObject] Sketch329
  ExternalGeometry = -> [Sketch328]
  MapMode = 5
  Placement = pos=(1,0,0) rot=(0,-1,0;0.628319rad)
  Support = -> [DatumPlane008]
  sketch-geometry (8):
    g0: LineSegment StartX=-0.00949059 StartY=13 StartZ=0 EndX=6.99051 EndY=6 EndZ=0
    g1: LineSegment StartX=6.99051 StartY=6 StartZ=0 EndX=6.99051 EndY=-10 EndZ=0
    g2: LineSegment StartX=6.99051 StartY=-10 StartZ=0 EndX=3.99051 EndY=-13 EndZ=0
    g3: LineSegment StartX=3.99051 StartY=-13 StartZ=0 EndX=2.99051 EndY=-13 EndZ=0
    g4: LineSegment StartX=2.99051 StartY=-13 StartZ=0 EndX=5.99051 EndY=-10 EndZ=0
    g5: LineSegment StartX=5.99051 StartY=-10 StartZ=0 EndX=5.99051 EndY=6 EndZ=0
    g6: LineSegment StartX=5.99051 StartY=6 StartZ=0 EndX=-1.00949 EndY=13 EndZ=0
    g7: LineSegment StartX=-1.00949 StartY=13 StartZ=0 EndX=-0.00949059 EndY=13 EndZ=0
  constraints (20):
    c: Coincident(g-3,g0)
    c: Coincident(g0,g-4)
    c: Coincident(g0,g1)
    c: Coincident(g1,g-5)
    c: Coincident(g1,g2)
    c: Coincident(g2,g-5)
    c: Coincident(g2,g3)
    c: Horizontal(g3)
    c: Coincident(g3,g4)
    c: Coincident(g4,g5)
    c: Vertical(g5)
    c: Coincident(g5,g6)
    c: Coincident(g6,g7)
    c: Coincident(g7,g0)
    c: Horizontal(g7)
    c: Parallel(g0,g6)
    c: Parallel(g4,g2)
    c: Horizontal(g4,g1)
    c: Horizontal(g5,g0)
    c: Distance(g7) = 1
FEATURE [PartDesign::Pad] Pad180
  BaseFeature = -> Pocket136
  Length = 11
  Length2 = 25
  Placement = pos=(0,0,0) rot=(0.57735,0.57735,0.57735;2.0944rad)
  Profile = -> Sketch329
  Refine = true
  Type = 4
FEATURE [Sketcher::SketchObject] Sketch330
  ExternalGeometry = -> [Sketch327,Pad180]
  MapMode = 5
  Placement = pos=(0,0,0) rot=(0.57735,0.57735,0.57735;2.0944rad)
  Support = -> [YZ_Plane102]
  sketch-geometry (13):
    g0: LineSegment StartX=-13 StartY=-11 StartZ=0 EndX=-12 EndY=-11 EndZ=0
    g1: LineSegment StartX=-10 StartY=-6 StartZ=0 EndX=13 EndY=-6 EndZ=0
    g2: LineSegment StartX=-13 StartY=-11 StartZ=0 EndX=-13 EndY=5 EndZ=0
    g3: LineSegment StartX=13 StartY=5 StartZ=0 EndX=13 EndY=-6 EndZ=0
    g4: LineSegment StartX=9 StartY=9 StartZ=0 EndX=-9 EndY=9 EndZ=0
    g5: ArcOfCircle CenterX=-9 CenterY=5 CenterZ=0 NormalX=0 NormalY=0 NormalZ=1 AngleXU=0 Radius=4 StartAngle=1.5708 EndAngle=3.14159
    g6: ArcOfCircle CenterX=9 CenterY=5 CenterZ=0 NormalX=0 NormalY=0 NormalZ=1 AngleXU=0 Radius=4 StartAngle=5.9829e-12 EndAngle=1.5708
    g7: LineSegment StartX=-25 StartY=25 StartZ=0 EndX=25 EndY=25 EndZ=0
    g8: LineSegment StartX=25 StartY=25 StartZ=0 EndX=25 EndY=-25 EndZ=0
    g9: LineSegment StartX=25 StartY=-25 StartZ=0 EndX=-25 EndY=-25 EndZ=0
    g10: LineSegment StartX=-25 StartY=-25 StartZ=0 EndX=-25 EndY=25 EndZ=0
    g11: LineSegment StartX=-10 StartY=-6 StartZ=0 EndX=-10 EndY=-7 EndZ=0
    g12: LineSegment StartX=-10 StartY=-7 StartZ=0 EndX=-12 EndY=-11 EndZ=0
  constraints (33):
    c: Coincident(g1,g-6)
    c: Horizontal(g1)
    c: Coincident(g2,g-7)
    c: Coincident(g3,g-6)
    c: Coincident(g3,g1)
    c: Coincident(g4,g-5)
    c: Coincident(g4,g-5)
    c: Coincident(g5,g4)
    c: Coincident(g5,g2)
    c: Coincident(g6,g4)
    c: Coincident(g6,g3)
    c: Equal(g6,g-3)
    c: Equal(g5,g-4)
    c: Coincident(g7,g8)
    c: Coincident(g8,g9)
    c: Coincident(g9,g10)
    c: Coincident(g10,g7)
    c: Horizontal(g7)
    c: Horizontal(g9)
    c: Vertical(g8)
    c: Vertical(g10)
    c: Symmetric(g7,g8,g-1)
    c: Equal(g8,g7)
    c: Distance(g8) = 50
    c: Coincident(g0,g2)
    c: Coincident(g0,g-7)
    c: Coincident(g0,g-8)
    c: PointOnObject(g1,g-9)
    c: Coincident(g1,g11)
    c: PointOnObject(g11,g-9)
    c: Coincident(g11,g12)
    c: Coincident(g12,g0)
    c: Equal(g11,g0)
FEATURE [PartDesign::Pocket] Pocket137
  BaseFeature = -> Pad180
  Length = 5
  Length2 = 100
  Midplane = true
  Placement = pos=(0,0,0) rot=(0.57735,0.57735,0.57735;2.0944rad)
  Profile = -> Sketch330
  Refine = true
  Type = 1
FEATURE [Sketcher::SketchObject] Sketch331
  ExternalGeometry = -> [Pocket137]
  MapMode = 5
  Placement = pos=(1.7e-15,-2.6e-15,-6) rot=(0.707107,0.707107,0;3.14159rad)
  Support = -> [Pocket137]
  sketch-geometry (7):
    g0: LineSegment StartX=13 StartY=-10 StartZ=0 EndX=13 EndY=26 EndZ=0
    g1: LineSegment StartX=13 StartY=26 StartZ=0 EndX=-10 EndY=26 EndZ=0
    g2: LineSegment StartX=-10 StartY=26 StartZ=0 EndX=-10 EndY=12.7639 EndZ=0
    g3: LineSegment StartX=-10 StartY=12.7639 StartZ=0 EndX=6 EndY=12.7639 EndZ=0
    g4: LineSegment StartX=6 StartY=12.7639 StartZ=0 EndX=12 EndY=5.34752 EndZ=0
    g5: LineSegment StartX=12 StartY=5.34752 StartZ=0 EndX=12 EndY=-10 EndZ=0
    g6: LineSegment StartX=12 StartY=-10 StartZ=0 EndX=13 EndY=-10 EndZ=0
  constraints (17):
    c: Coincident(g-3,g0)
    c: Vertical(g0)
    c: Coincident(g0,g1)
    c: Horizontal(g1)
    c: Coincident(g1,g2)
    c: Coincident(g2,g3)
    c: Coincident(g3,g4)
    c: Coincident(g4,g-4)
    c: Coincident(g4,g5)
    c: Vertical(g5)
    c: Coincident(g5,g6)
    c: Coincident(g6,g0)
    c: Horizontal(g6)
    c: Vertical(g2)
    c: Coincident(g3,g-5)
    c: Coincident(g2,g-5)
    c: Distance(g0) = 36
FEATURE [PartDesign::Pad] Pad181
  BaseFeature = -> Pocket137
  Length = 1
  Length2 = 100
  Placement = pos=(0,0,0) rot=(0.57735,0.57735,0.57735;2.0944rad)
  Profile = -> Sketch331
  Refine = true
  Type = 0
FEATURE [Sketcher::SketchObject] Sketch332
  ExternalGeometry = -> [Pad181]
  MapMode = 5
  Placement = pos=(5.2e-15,13,-1e-15) rot=(0.57735,0.57735,0.57735;4.18879rad)
  Support = -> [Pad181]
  sketch-geometry (4):
    g0: LineSegment StartX=-6 StartY=26 StartZ=0 EndX=-26 EndY=26 EndZ=0
    g1: LineSegment StartX=-26 StartY=26 StartZ=0 EndX=-26 EndY=27 EndZ=0
    g2: LineSegment StartX=-26 StartY=27 StartZ=0 EndX=-6 EndY=27 EndZ=0
    g3: LineSegment StartX=-6 StartY=27 StartZ=0 EndX=-6 EndY=26 EndZ=0
  constraints (11):
    c: Coincident(g0,g1)
    c: Coincident(g1,g2)
    c: Coincident(g2,g3)
    c: Coincident(g3,g0)
    c: Horizontal(g0)
    c: Horizontal(g2)
    c: Vertical(g1)
    c: Vertical(g3)
    c: Coincident(g0,g-3)
    c: Distance(g3) = 1
    c: Distance(g2) = 20
FEATURE [PartDesign::Pad] Pad182
  BaseFeature = -> Pad181
  Length = 10
  Length2 = 100
  Placement = pos=(0,0,0) rot=(0.57735,0.57735,0.57735;2.0944rad)
  Profile = -> Sketch332
  Refine = true
  Reversed = true
  Type = 3
  UpToFace = -> Pad181 [Face21]
FEATURE [Sketcher::SketchObject] Sketch333
  ExternalGeometry = -> [Sketch327]
  MapMode = 5
  Placement = pos=(-10,2.2e-15,-1.78e-14) rot=(0.57735,0.57735,-0.57735;4.18879rad)
  Support = -> [Pad182]
  sketch-geometry (6):
    g0: LineSegment StartX=13 StartY=6 StartZ=0 EndX=-13 EndY=6 EndZ=0
    g1: LineSegment StartX=-13 StartY=6 StartZ=0 EndX=-13 EndY=-5 EndZ=0
    g2: LineSegment StartX=13 StartY=-5 StartZ=0 EndX=13 EndY=6 EndZ=0
    g3: ArcOfCircle CenterX=-9 CenterY=-5 CenterZ=0 NormalX=0 NormalY=0 NormalZ=1 AngleXU=0 Radius=4 StartAngle=3.14159 EndAngle=4.71239
    g4: ArcOfCircle CenterX=9 CenterY=-5 CenterZ=0 NormalX=0 NormalY=0 NormalZ=1 AngleXU=0 Radius=4 StartAngle=4.71239 EndAngle=6.28319
    g5: LineSegment StartX=-9 StartY=-9 StartZ=0 EndX=9 EndY=-9 EndZ=0
  constraints (15):
    c: Coincident(g0,g1)
    c: Coincident(g2,g0)
    c: Horizontal(g0)
    c: Vertical(g1)
    c: Coincident(g3,g1)
    c: Coincident(g4,g2)
    c: Coincident(g5,g3)
    c: Coincident(g5,g4)
    c: Coincident(g0,g-4)
    c: Coincident(g2,g-4)
    c: Coincident(g4,g-3)
    c: Coincident(g3,g-5)
    c: Coincident(g-5,g1)
    c: Equal(g-5,g3)
    c: Equal(g-3,g4)
FEATURE [PartDesign::Pad] Pad183
  BaseFeature = -> Pad182
  Length = 1
  Length2 = 100
  Placement = pos=(0,0,0) rot=(0.57735,0.57735,0.57735;2.0944rad)
  Profile = -> Sketch333
  Refine = true
  Type = 0
FEATURE [Sketcher::SketchObject] Sketch334
  ExternalGeometry = -> [Sketch333]
  MapMode = 5
  Placement = pos=(-11,3.7e-15,-2.48e-14) rot=(0.57735,0.57735,-0.57735;4.18879rad)
  Support = -> [Pad183]
  sketch-geometry (4):
    g0: LineSegment StartX=13 StartY=6 StartZ=0 EndX=-13 EndY=6 EndZ=0
    g1: LineSegment StartX=-13 StartY=6 StartZ=0 EndX=-13 EndY=26 EndZ=0
    g2: LineSegment StartX=-13 StartY=26 StartZ=0 EndX=13 EndY=26 EndZ=0
    g3: LineSegment StartX=13 StartY=26 StartZ=0 EndX=13 EndY=6 EndZ=0
  constraints (10):
    c: Coincident(g0,g1)
    c: Coincident(g1,g2)
    c: Coincident(g2,g3)
    c: Coincident(g3,g0)
    c: Horizontal(g2)
    c: Vertical(g1)
    c: Vertical(g3)
    c: Coincident(g0,g-3)
    c: Coincident(g0,g-3)
    c: Distance(g3) = 20
FEATURE [PartDesign::Pad] Pad184
  BaseFeature = -> Pad183
  Length = 1
  Length2 = 100
  Placement = pos=(0,0,0) rot=(0.57735,0.57735,0.57735;2.0944rad)
  Profile = -> Sketch334
  Refine = true
  Reversed = true
  Type = 0
FEATURE [Sketcher::SketchObject] Sketch335
  ExternalGeometry = -> [Sketch332,Sketch334]
  MapMode = 5
  Placement = pos=(5.7e-15,-1.01e-14,-26) rot=(0.707107,0.707107,0;3.14159rad)
  Support = -> [Pad184]
  sketch-geometry (8):
    g0: LineSegment StartX=13 StartY=27 StartZ=0 EndX=13 EndY=7 EndZ=0
    g1: LineSegment StartX=13 StartY=7 StartZ=0 EndX=4 EndY=13 EndZ=0
    g2: LineSegment StartX=4 StartY=13 StartZ=0 EndX=4 EndY=27 EndZ=0
    g3: LineSegment StartX=4 StartY=27 StartZ=0 EndX=13 EndY=27 EndZ=0
    g4: LineSegment StartX=13 StartY=-11 StartZ=0 EndX=4 EndY=-11 EndZ=0
    g5: LineSegment StartX=4 StartY=-11 StartZ=0 EndX=4 EndY=-6 EndZ=0
    g6: LineSegment StartX=4 StartY=-6 StartZ=0 EndX=13 EndY=-6 EndZ=0
    g7: LineSegment StartX=13 StartY=-6 StartZ=0 EndX=13 EndY=-11 EndZ=0
  constraints (22):
    c: Coincident(g0,g-3)
    c: Vertical(g0)
    c: Coincident(g0,g1)
    c: Coincident(g1,g2)
    c: Vertical(g2)
    c: Coincident(g2,g3)
    c: Coincident(g3,g0)
    c: Distance(g3) = 9
    c: DistanceY(g0,g1) = 6
    c: Distance(g0) = 20
    c: Horizontal(g3)
    c: Coincident(g4,g5)
    c: Coincident(g5,g6)
    c: Coincident(g6,g7)
    c: Coincident(g7,g4)
    c: Horizontal(g4)
    c: Horizontal(g6)
    c: Vertical(g5)
    c: Vertical(g7)
    c: Coincident(g4,g-4)
    c: Vertical(g5,g1)
    c: Distance(g7) = 5
FEATURE [PartDesign::Pad] Pad185
  BaseFeature = -> Pad184
  Length = 1
  Length2 = 100
  Placement = pos=(0,0,0) rot=(0.57735,0.57735,0.57735;2.0944rad)
  Profile = -> Sketch335
  Refine = true
  Type = 0
FEATURE [Sketcher::SketchObject] Sketch336
  ExternalGeometry = -> [Sketch334,Sketch332]
  MapMode = 5
  Placement = pos=(1.21e-14,13,-2.3e-15) rot=(0.57735,0.57735,0.57735;4.18879rad)
  Support = -> [Pad185]
  sketch-geometry (4):
    g0: LineSegment StartX=-26 StartY=26 StartZ=0 EndX=-6 EndY=26 EndZ=0
    g1: LineSegment StartX=-6 StartY=26 StartZ=0 EndX=-6 EndY=-11 EndZ=0
    g2: LineSegment StartX=-6 StartY=-11 StartZ=0 EndX=-26 EndY=-11 EndZ=0
    g3: LineSegment StartX=-26 StartY=-11 StartZ=0 EndX=-26 EndY=26 EndZ=0
  constraints (10):
    c: Coincident(g0,g1)
    c: Coincident(g1,g2)
    c: Coincident(g2,g3)
    c: Coincident(g3,g0)
    c: Horizontal(g0)
    c: Horizontal(g2)
    c: Vertical(g1)
    c: Vertical(g3)
    c: Coincident(g0,g-4)
    c: Coincident(g1,g-3)
FEATURE [PartDesign::Pad] Pad186
  BaseFeature = -> Pad185
  Length = 1
  Length2 = 100
  Placement = pos=(0,0,0) rot=(0.57735,0.57735,0.57735;2.0944rad)
  Profile = -> Sketch336
  Refine = true
  Reversed = true
  Type = 0
FEATURE [Sketcher::SketchObject] Sketch337
  ExternalGeometry = -> [Sketch335]
  MapMode = 5
  Placement = pos=(-11,6.4e-15,-3.28e-14) rot=(0.57735,0.57735,-0.57735;4.18879rad)
  Support = -> [Pad186]
  sketch-geometry (4):
    g0: LineSegment StartX=12 StartY=21 StartZ=0 EndX=9 EndY=21 EndZ=0
    g1: LineSegment StartX=9 StartY=21 StartZ=0 EndX=9 EndY=13 EndZ=0
    g2: LineSegment StartX=9 StartY=13 StartZ=0 EndX=12 EndY=13 EndZ=0
    g3: LineSegment StartX=12 StartY=13 StartZ=0 EndX=12 EndY=21 EndZ=0
  constraints (12):
    c: Coincident(g0,g1)
    c: Coincident(g1,g2)
    c: Coincident(g2,g3)
    c: Coincident(g3,g0)
    c: Horizontal(g0)
    c: Horizontal(g2)
    c: Vertical(g1)
    c: Vertical(g3)
    c: DistanceY(g0,g-3) = 5
    c: DistanceX(g0,g-3) = 1
    c: Distance(g2) = 3
    c: Distance(g3) = 8
FEATURE [PartDesign::Pocket] Pocket138
  BaseFeature = -> Pad186
  Length = 5
  Length2 = 100
  Placement = pos=(0,0,0) rot=(0.57735,0.57735,0.57735;2.0944rad)
  Profile = -> Sketch337
  Refine = true
  Type = 2
FEATURE [Sketcher::SketchObject] Sketch338
  ExternalGeometry = -> [Sketch332]
  MapMode = 5
  Placement = pos=(1.8e-15,-5.2e-15,-6) rot=(0,0,-1;1.5708rad)
  Support = -> [Pocket138]
  sketch-geometry (3):
    g0: LineSegment StartX=-13 StartY=27 StartZ=0 EndX=-13 EndY=24.5 EndZ=0
    g1: LineSegment StartX=-13 StartY=24.5 StartZ=0 EndX=-10.5 EndY=27 EndZ=0
    g2: LineSegment StartX=-10.5 StartY=27 StartZ=0 EndX=-13 EndY=27 EndZ=0
  constraints (8):
    c: Coincident(g0,g-3)
    c: Coincident(g0,g1)
    c: Coincident(g1,g2)
    c: Coincident(g2,g0)
    c: Horizontal(g2)
    c: Vertical(g0)
    c: Equal(g2,g0)
    c: Distance(g2) = 2.5
FEATURE [PartDesign::Pocket] Pocket139
  BaseFeature = -> Pocket138
  Length = 5
  Length2 = 100
  Placement = pos=(0,0,0) rot=(0.57735,0.57735,0.57735;2.0944rad)
  Profile = -> Sketch338
  Refine = true
  Type = 1
FEATURE [Sketcher::SketchObject] Sketch339
  ExternalGeometry = -> [Pocket139]
  MapMode = 5
  Placement = pos=(18.75,18.75,1.43e-14) rot=(0.281085,0.678598,0.678598;2.59356rad)
  Support = -> [Pocket139]
  sketch-geometry (4):
    g0: LineSegment StartX=-11.6673 StartY=-27 StartZ=0 EndX=-8.13173 EndY=-27 EndZ=0
    g1: LineSegment StartX=-8.13173 StartY=-27 StartZ=0 EndX=-8.13173 EndY=-6 EndZ=0
    g2: LineSegment StartX=-8.13173 StartY=-6 StartZ=0 EndX=-11.6673 EndY=-6 EndZ=0
    g3: LineSegment StartX=-11.6673 StartY=-6 StartZ=0 EndX=-11.6673 EndY=-27 EndZ=0
  constraints (10):
    c: Coincident(g0,g1)
    c: Coincident(g1,g2)
    c: Coincident(g2,g3)
    c: Coincident(g3,g0)
    c: Horizontal(g0)
    c: Horizontal(g2)
    c: Vertical(g1)
    c: Vertical(g3)
    c: Coincident(g0,g-3)
    c: Coincident(g1,g-4)
FEATURE [PartDesign::Pad] Pad187
  BaseFeature = -> Pocket139
  Length = 0.4
  Length2 = 100
  Placement = pos=(0,0,0) rot=(0.57735,0.57735,0.57735;2.0944rad)
  Profile = -> Sketch339
  Refine = true
  Reversed = true
  Type = 0
FEATURE [Sketcher::SketchObject] Sketch340
  ExternalGeometry = -> [Sketch335,Sketch334,Pad187]
  MapMode = 5
  Placement = pos=(1.56e-14,13,-3.9e-15) rot=(0.57735,0.57735,0.57735;4.18879rad)
  Support = -> [Pad187]
  sketch-geometry (27):
    g0: GeomPoint X=-13 Y=1 Z=0
    g1: GeomPoint X=-23 Y=22 Z=0
    g2: LineSegment StartX=-13 StartY=1.24721 StartZ=0 EndX=-26 EndY=10.6923 EndZ=0
    g3: LineSegment StartX=-25.6 StartY=9.90722 StartZ=0 EndX=-13 EndY=0.752786 EndZ=0
    g4: LineSegment StartX=-26 StartY=27 StartZ=0 EndX=-25.6 EndY=27 EndZ=0
    g5: LineSegment StartX=-25.6 StartY=9.90722 StartZ=0 EndX=-25.6 EndY=6.6 EndZ=0
    g6: LineSegment StartX=-25.6 StartY=6.6 StartZ=0 EndX=-26 EndY=6.6 EndZ=0
    g7: LineSegment StartX=-23 StartY=22.2472 StartZ=0 EndX=-25.6 EndY=24.1362 EndZ=0
    g8: LineSegment StartX=-25.6 StartY=27 StartZ=0 EndX=-25.6 EndY=24.1362 EndZ=0
    g9: LineSegment StartX=-26 StartY=23.9324 StartZ=0 EndX=-23 EndY=21.7528 EndZ=0
    g10: LineSegment StartX=-23 StartY=22.2472 StartZ=0 EndX=-7 EndY=10.6225 EndZ=0
    g11: LineSegment StartX=-7 StartY=10.6225 StartZ=0 EndX=-7 EndY=5.07407 EndZ=0
    g12: LineSegment StartX=-7 StartY=5.07407 StartZ=0 EndX=1.79994 EndY=-1.31946 EndZ=0
    g13: LineSegment StartX=1.79994 StartY=-1.81389 StartZ=0 EndX=-7.4 EndY=4.87026 EndZ=0
    g14: LineSegment StartX=-7.4 StartY=4.87026 StartZ=0 EndX=-7.4 EndY=10.4187 EndZ=0
    g15: LineSegment StartX=-7.4 StartY=10.4187 StartZ=0 EndX=-23 EndY=21.7528 EndZ=0
    g16: LineSegment [constr] StartX=-7.4 StartY=10.4187 StartZ=0 EndX=-7 EndY=10.4187 EndZ=0
    g17: LineSegment [constr] StartX=-7.4 StartY=10.4187 StartZ=0 EndX=-7.16489 EndY=10.7423 EndZ=0
    g18: LineSegment [constr] StartX=-7 StartY=5.07407 StartZ=0 EndX=-7.23511 EndY=4.75046 EndZ=0
    g19: LineSegment StartX=-13 StartY=1.24721 StartZ=0 EndX=1.79994 EndY=-9.50557 EndZ=0
    g20: LineSegment StartX=1.79994 StartY=-9.50557 StartZ=0 EndX=1.79994 EndY=-10 EndZ=0
    g21: LineSegment StartX=1.79994 StartY=-10 StartZ=0 EndX=-13 EndY=0.752786 EndZ=0
    g22: LineSegment [constr] StartX=1.79994 StartY=-1.31946 StartZ=0 EndX=1.79994 EndY=-0.319465 EndZ=0
    g23: LineSegment StartX=-26 StartY=23.9324 StartZ=0 EndX=-26 EndY=27 EndZ=0
    g24: LineSegment StartX=-26 StartY=10.6923 StartZ=0 EndX=-26 EndY=6.6 EndZ=0
    g25: LineSegment [constr] StartX=-25.6 StartY=9.90722 StartZ=0 EndX=-25.3649 EndY=10.2308 EndZ=0
    g26: LineSegment StartX=1.79994 StartY=-1.31946 StartZ=0 EndX=1.79994 EndY=-1.81389 EndZ=0
  constraints (76):
    c: DistanceY(g1,g-3) = 5
    c: DistanceX(g-3,g1) = 3
    c: DistanceY(g-4,g0) = 12
    c: DistanceX(g0,g-4) = 7
    c: Coincident(g-3,g4)
    c: Horizontal(g4)
    c: Coincident(g3,g5)
    c: Coincident(g5,g6)
    c: Horizontal(g6)
    c: Distance(g6) = 0.4
    c: Vertical(g5)
    c: Parallel(g3,g2)
    c: Parallel(g2,g-5)
    c: Symmetric(g2,g3,g0)
    c: Vertical(g2,g3)
    c: Coincident(g8,g4)
    c: Coincident(g8,g7)
    c: Vertical(g8)
    c: Symmetric(g7,g9,g1)
    c: Vertical(g7,g9)
    c: Parallel(g2,g9)
    c: Parallel(g9,g7)
    c: Coincident(g10,g7)
    c: Coincident(g10,g11)
    c: Vertical(g11)
    c: Coincident(g11,g12)
    c: Coincident(g13,g14)
    c: Vertical(g14)
    c: Coincident(g14,g15)
    c: Coincident(g15,g9)
    c: Parallel(g10,g15)
    c: Parallel(g15,g9)
    c: Parallel(g9,g13)
    c: Parallel(g13,g12)
    c: Coincident(g16,g14)
    c: PointOnObject(g16,g11)
    c: Horizontal(g16)
    c: Coincident(g17,g14)
    c: PointOnObject(g17,g10)
    c: Perpendicular(g15,g17)
    c: Equal(g16,g17)
    c: Coincident(g18,g11)
    c: PointOnObject(g18,g13)
    c: Perpendicular(g12,g18)
    c: Equal(g18,g16)
    c: Coincident(g2,g19)
    c: Coincident(g19,g20)
    c: Vertical(g20)
    c: Coincident(g20,g21)
    c: Coincident(g21,g3)
    c: Parallel(g19,g21)
    c: Parallel(g21,g2)
    c: DistanceY(g-4,g20) = 1
    c: DistanceX(g10,g-5) = 1
    c: Coincident(g22,g12)
    c: PointOnObject(g22,g-5)
    c: Vertical(g22)
    c: Distance(g22) = 1
    c: PointOnObject(g9,g-3)
    c: Coincident(g23,g9)
    c: Coincident(g23,g4)
    c: PointOnObject(g2,g-3)
    c: Coincident(g24,g2)
    c: Coincident(g24,g6)
    c: Vertical(g24)
    c: Vertical(g7,g3)
    c: Coincident(g25,g3)
    c: PointOnObject(g25,g2)
    c: Perpendicular(g2,g25)
    c: Equal(g25,g6)
    c: Equal(g6,g16)
    c: Vertical(g12,g19)
    c: Distance(g-3,g6) = 0.4
    c: Coincident(g26,g12)
    c: Coincident(g26,g13)
    c: Vertical(g26)
FEATURE [PartDesign::Pocket] Pocket141
  BaseFeature = -> Pad187
  Length = 9.4
  Length2 = 100
  Placement = pos=(0,0,0) rot=(0.57735,0.57735,0.57735;2.0944rad)
  Profile = -> Sketch340
  Refine = true
  Type = 0
FEATURE [Sketcher::SketchObject] Sketch341
  ExternalGeometry = -> [Pocket141]
  MapMode = 5
  Placement = pos=(-2.44e-14,-13,8.7e-15) rot=(-0.57735,-0.57735,0.57735;4.18879rad)
  Support = -> [Pocket141]
  sketch-geometry (4):
    g0: LineSegment StartX=11 StartY=-10 StartZ=0 EndX=-1.79994 EndY=-10 EndZ=0
    g1: LineSegment StartX=-1.79994 StartY=-10 StartZ=0 EndX=-1.79994 EndY=-9.50557 EndZ=0
    g2: LineSegment StartX=-1.79994 StartY=-9.50557 StartZ=0 EndX=11 EndY=-9.50557 EndZ=0
    g3: LineSegment StartX=11 StartY=-9.50557 StartZ=0 EndX=11 EndY=-10 EndZ=0
  constraints (10):
    c: Coincident(g0,g1)
    c: Coincident(g1,g2)
    c: Coincident(g2,g3)
    c: Coincident(g3,g0)
    c: Horizontal(g0)
    c: Horizontal(g2)
    c: Vertical(g1)
    c: Vertical(g3)
    c: Coincident(g0,g-3)
    c: Coincident(g1,g-4)
FEATURE [PartDesign::Pocket] Pocket142
  BaseFeature = -> Pocket141
  Length = 5
  Length2 = 100
  Placement = pos=(0,0,0) rot=(0.57735,0.57735,0.57735;2.0944rad)
  Profile = -> Sketch341
  Refine = true
  Type = 2
FEATURE [Sketcher::SketchObject] Sketch342
  ExternalGeometry = -> [Pocket142]
  MapMode = 5
  Placement = pos=(-11,6.4e-15,-3.28e-14) rot=(0.57735,0.57735,-0.57735;4.18879rad)
  Support = -> [Pocket142]
  sketch-geometry (4):
    g0: LineSegment StartX=-13 StartY=26 StartZ=0 EndX=4 EndY=26 EndZ=0
    g1: LineSegment StartX=4 StartY=26 StartZ=0 EndX=4 EndY=23 EndZ=0
    g2: LineSegment StartX=4 StartY=23 StartZ=0 EndX=-13 EndY=23 EndZ=0
    g3: LineSegment StartX=-13 StartY=23 StartZ=0 EndX=-13 EndY=26 EndZ=0
  constraints (10):
    c: Coincident(g0,g1)
    c: Coincident(g1,g2)
    c: Coincident(g2,g3)
    c: Coincident(g3,g0)
    c: Horizontal(g2)
    c: Vertical(g1)
    c: Vertical(g3)
    c: Coincident(g0,g-3)
    c: Coincident(g-3,g0)
    c: Distance(g3) = 3
FEATURE [PartDesign::Pocket] Pocket143
  BaseFeature = -> Pocket142
  Length = 5
  Length2 = 100
  Placement = pos=(0,0,0) rot=(0.57735,0.57735,0.57735;2.0944rad)
  Profile = -> Sketch342
  Refine = true
  Type = 2
FEATURE [Sketcher::SketchObject] Sketch343
  ExternalGeometry = -> [Pocket143]
  MapMode = 5
  Placement = pos=(27,-4.6e-15,2.21e-14) rot=(0.57735,0.57735,0.57735;2.0944rad)
  Support = -> [Pocket143]
  sketch-geometry (4):
    g0: LineSegment StartX=-10 StartY=-6 StartZ=0 EndX=4 EndY=-6 EndZ=0
    g1: LineSegment StartX=4 StartY=-6 StartZ=0 EndX=4 EndY=-27 EndZ=0
    g2: LineSegment StartX=4 StartY=-27 StartZ=0 EndX=-10 EndY=-27 EndZ=0
    g3: LineSegment StartX=-10 StartY=-27 StartZ=0 EndX=-10 EndY=-6 EndZ=0
  constraints (10):
    c: Coincident(g0,g1)
    c: Coincident(g1,g2)
    c: Coincident(g2,g3)
    c: Coincident(g3,g0)
    c: Horizontal(g0)
    c: Horizontal(g2)
    c: Vertical(g1)
    c: Vertical(g3)
    c: Coincident(g0,g-4)
    c: Coincident(g1,g-3)
FEATURE [PartDesign::Pocket] Pocket144
  BaseFeature = -> Pocket143
  Length = 1
  Length2 = 100
  Placement = pos=(0,0,0) rot=(0.57735,0.57735,0.57735;2.0944rad)
  Profile = -> Sketch343
  Refine = true
  Type = 0
FEATURE [PartDesign::Body] Body091
  Group = -> [Sketch327,Pad179,DatumPlane008,Sketch328,Pocket136,Sketch329,Pad180,Sketch330,Pocket137,Sketch331,Pad181,Sketch332,Pad182,Sketch333,Pad183,Sketch334,Pad184,Sketch335,Pad185,Sketch336,Pad186,Sketch337,Pocket138,Sketch338,Pocket139,Sketch339,Pad187,Sketch340,Pocket141,Sketch341,Pocket142,Sketch342,Pocket143,Sketch343,Pocket144]
  Origin = -> Origin103
  Placement = pos=(15.3323,2.00761,-32.786) rot=(0.002664,0.999048,-0.043553;3.08928rad)
  Tip = -> Pocket144
FEATURE [PartDesign::Pocket] Pocket145
  BaseFeature = -> Pocket134
  Length = 5
  Length2 = 100
  Placement = pos=(0,0,0) rot=(0.57735,0.57735,0.57735;2.0944rad)
  Profile = -> Sketch326
  Refine = true
  Type = 2
FEATURE [PartDesign::Body] Body090
  Group = -> [Sketch312,Pad170,DatumPlane007,Sketch313,Pocket130,Sketch314,Pad171,Sketch315,Pocket131,Sketch316,Pad172,Sketch317,Pad173,Sketch318,Pad174,Sketch319,Pad175,Sketch320,Pad176,Sketch321,Pad177,Sketch322,Pocket132,Sketch323,Pocket133,Sketch324,Pad178,Sketch325,Pocket134,Sketch326,Pocket145]
  Origin = -> Origin102
  Placement = pos=(-54,4,-32) rot=(0,-1,0;1.5708rad)
  Tip = -> Pocket145
FEATURE [Sketcher::SketchObject] Sketch344
  ExternalGeometry = -> [Sketch274]
  MapMode = 5
  Placement = pos=(0,0,1) rot=(0,0,1;0rad)
  Support = -> [Pad148]
  sketch-geometry (4):
    g0: LineSegment StartX=20.5 StartY=34.5 StartZ=0 EndX=-7.5 EndY=34.5 EndZ=0
    g1: LineSegment StartX=-7.5 StartY=34.5 StartZ=0 EndX=-7.08824 EndY=35.5 EndZ=0
    g2: LineSegment StartX=-7.08824 StartY=35.5 StartZ=0 EndX=20.5 EndY=35.5 EndZ=0
    g3: LineSegment StartX=20.5 StartY=35.5 StartZ=0 EndX=20.5 EndY=34.5 EndZ=0
  constraints (10):
    c: Coincident(g-4,g0)
    c: Coincident(g0,g-3)
    c: Coincident(g0,g1)
    c: Coincident(g1,g2)
    c: Horizontal(g2)
    c: Coincident(g2,g3)
    c: Coincident(g3,g0)
    c: Vertical(g3)
    c: Parallel(g1,g-3)
    c: Distance(g3) = 1
FEATURE [PartDesign::Pad] Pad188
  BaseFeature = -> Pad148
  Length = 10
  Length2 = 100
  Profile = -> Sketch344
  Refine = true
  Reversed = true
  Type = 3
  UpToFace = -> Pad148 [Face19]
FEATURE [Sketcher::SketchObject] Sketch345
  ExternalGeometry = -> [Pad188]
  MapMode = 5
  Placement = pos=(0,35.5,0) rot=(0,0.707107,0.707107;3.14159rad)
  Support = -> [Pad188]
  sketch-geometry (14):
    g0: GeomPoint X=-10.2 Y=-8.3 Z=0
    g1: GeomPoint X=-3.2 Y=-27.3 Z=0
    g2: LineSegment [constr] StartX=-10.2 StartY=-33.3 StartZ=0 EndX=-2.2 EndY=-33.3 EndZ=0
    g3: LineSegment [constr] StartX=-2.2 StartY=-33.3 StartZ=0 EndX=-2.2 EndY=-38.8 EndZ=0
    g4: LineSegment [constr] StartX=-2.2 StartY=-38.8 StartZ=0 EndX=-10.2 EndY=-38.8 EndZ=0
    g5: LineSegment [constr] StartX=-10.2 StartY=-38.8 StartZ=0 EndX=-10.2 EndY=-33.3 EndZ=0
    g6: LineSegment StartX=-13.0579 StartY=0 StartZ=0 EndX=2.04737 EndY=-41 EndZ=0
    g7: LineSegment StartX=2.04737 StartY=-41 StartZ=0 EndX=1.64737 EndY=-41 EndZ=0
    g8: LineSegment StartX=1.64737 StartY=-41 StartZ=0 EndX=-13.4579 EndY=0 EndZ=0
    g9: LineSegment StartX=-13.4579 StartY=0 StartZ=0 EndX=-13.0579 EndY=0 EndZ=0
    g10: GeomPoint X=-3.2 Y=-27.8429 Z=0
    g11: GeomPoint X=-3.2 Y=-26.7571 Z=0
    g12: GeomPoint X=-10.2 Y=-7.75714 Z=0
    g13: GeomPoint X=-10.2 Y=-8.84286 Z=0
  constraints (34):
    c: Coincident(g2,g3)
    c: Coincident(g3,g4)
    c: Coincident(g4,g5)
    c: Coincident(g5,g2)
    c: Horizontal(g2)
    c: Horizontal(g4)
    c: Vertical(g3)
    c: Vertical(g5)
    c: Distance(g2) = 8
    c: Distance(g5) = 5.5
    c: DistanceY(g3) = -38.8
    c: DistanceX(g3) = -2.2
    c: Vertical(g2,g0)
    c: Distance(g0,g2) = 25
    c: DistanceX(g1,g2) = 1
    c: DistanceY(g2,g1) = 6
    c: PointOnObject(g6,g-3)
    c: Coincident(g6,g7)
    c: PointOnObject(g7,g-3)
    c: Coincident(g7,g8)
    c: Coincident(g8,g9)
    c: Coincident(g9,g6)
    c: Parallel(g6,g8)
    c: PointOnObject(g10,g8)
    c: PointOnObject(g11,g6)
    c: PointOnObject(g12,g6)
    c: PointOnObject(g13,g8)
    c: Symmetric(g12,g13,g0)
    c: Symmetric(g11,g10,g1)
    c: Vertical(g11,g10)
    c: Vertical(g12,g13)
    c: Distance(g9) = 0.4
    c: PointOnObject(g8,g-1)
    c: Horizontal(g9)
FEATURE [PartDesign::Pocket] Pocket146
  BaseFeature = -> Pad188
  Length = 5
  Length2 = 100
  Profile = -> Sketch345
  Refine = true
  Type = 2
FEATURE [PartDesign::Body] Body086
  Group = -> [Sketch274,Pad146,Sketch275,Pad147,Sketch276,Pad148,Sketch344,Pad188,Sketch345,Pocket146]
  Origin = -> Origin098
  Placement = pos=(-1,-193,-194.5) rot=(0,0,1;0rad)
  Tip = -> Pocket146
FEATURE [Sketcher::SketchObject] Sketch346
  MapMode = 5
  Support = -> [XY_Plane104]
  sketch-geometry (7):
    g0: LineSegment StartX=-11 StartY=0 StartZ=0 EndX=-14 EndY=17.5 EndZ=0
    g1: LineSegment StartX=-14 StartY=17.5 StartZ=0 EndX=-7 EndY=34.5 EndZ=0
    g2: LineSegment StartX=-7 StartY=34.5 StartZ=0 EndX=20 EndY=34.5 EndZ=0
    g3: LineSegment StartX=20 StartY=34.5 StartZ=0 EndX=20 EndY=17.5 EndZ=0
    g4: LineSegment StartX=20 StartY=17.5 StartZ=0 EndX=11 EndY=0 EndZ=0
    g5: LineSegment StartX=11 StartY=0 StartZ=0 EndX=-11 EndY=0 EndZ=0
    g6: GeomPoint X=0 Y=17.5 Z=0
  constraints (20):
    c: PointOnObject(g0,g-1)
    c: Coincident(g0,g1)
    c: Coincident(g1,g2)
    c: Horizontal(g2)
    c: Coincident(g2,g3)
    c: Vertical(g3)
    c: Coincident(g3,g4)
    c: PointOnObject(g4,g-1)
    c: Coincident(g4,g5)
    c: Coincident(g5,g0)
    c: Distance(g-1,g0) = 11
    c: Distance(g-1,g4) = 11
    c: PointOnObject(g6,g-2)
    c: Horizontal(g6,g3)
    c: Distance(g6,g3) = 20
    c: Horizontal(g6,g0)
    c: Distance(g0,g6) = 14
    c: Distance(g-1,g6) = 17.5
    c: Distance(g3) = 17
    c: Distance(g2) = 27
FEATURE [PartDesign::Pad] Pad189
  Length = 1
  Length2 = 100
  Profile = -> Sketch346
  Refine = true
  Type = 0
FEATURE [Sketcher::SketchObject] Sketch347
  ExternalGeometry = -> [Pad189]
  MapMode = 5
  Placement = pos=(0,0,0) rot=(1,0,0;3.14159rad)
  Support = -> [Pad189]
  sketch-geometry (12):
    g0: LineSegment StartX=-7 StartY=-34.5 StartZ=0 EndX=-14 EndY=-17.5 EndZ=0
    g1: LineSegment StartX=-14 StartY=-17.5 StartZ=0 EndX=-11 EndY=0 EndZ=0
    g2: LineSegment StartX=-11 StartY=0 StartZ=0 EndX=-10 EndY=0 EndZ=0
    g3: LineSegment StartX=-10 StartY=0 StartZ=0 EndX=-13 EndY=-17.5 EndZ=0
    g4: LineSegment StartX=-13 StartY=-17.5 StartZ=0 EndX=-6 EndY=-34.5 EndZ=0
    g5: LineSegment StartX=-6 StartY=-34.5 StartZ=0 EndX=-7 EndY=-34.5 EndZ=0
    g6: LineSegment StartX=11 StartY=0 StartZ=0 EndX=20 EndY=-17.5 EndZ=0
    g7: LineSegment StartX=20 StartY=-17.5 StartZ=0 EndX=20 EndY=-34.5 EndZ=0
    g8: LineSegment StartX=20 StartY=-34.5 StartZ=0 EndX=19 EndY=-34.5 EndZ=0
    g9: LineSegment StartX=19 StartY=-34.5 StartZ=0 EndX=19 EndY=-17.5 EndZ=0
    g10: LineSegment StartX=19 StartY=-17.5 StartZ=0 EndX=10 EndY=0 EndZ=0
    g11: LineSegment StartX=10 StartY=0 StartZ=0 EndX=11 EndY=0 EndZ=0
  constraints (30):
    c: Coincident(g-4,g0)
    c: Coincident(g0,g-4)
    c: Coincident(g0,g1)
    c: Coincident(g1,g-3)
    c: Coincident(g1,g2)
    c: PointOnObject(g2,g-1)
    c: Coincident(g2,g3)
    c: Coincident(g3,g4)
    c: Coincident(g4,g5)
    c: Coincident(g5,g0)
    c: Coincident(g-5,g6)
    c: Coincident(g6,g-6)
    c: Coincident(g6,g7)
    c: Coincident(g7,g-6)
    c: Coincident(g7,g8)
    c: Horizontal(g8)
    c: Coincident(g8,g9)
    c: Vertical(g9)
    c: Coincident(g9,g10)
    c: PointOnObject(g10,g-1)
    c: Coincident(g10,g11)
    c: Coincident(g11,g6)
    c: Horizontal(g0,g3)
    c: Horizontal(g3,g9)
    c: Horizontal(g5)
    c: Equal(g5,g8)
    c: Equal(g8,g11)
    c: Equal(g11,g2)
    c: Parallel(g3,g1)
    c: Distance(g8) = 1
FEATURE [PartDesign::Pad] Pad190
  BaseFeature = -> Pad189
  Length = 40
  Length2 = 100
  Profile = -> Sketch347
  Refine = true
  Type = 0
FEATURE [Sketcher::SketchObject] Sketch348
  ExternalGeometry = -> [Pad190]
  MapMode = 5
  Placement = pos=(0,0,-40) rot=(1,0,0;3.14159rad)
  Support = -> [Pad190]
  sketch-geometry (9):
    g0: LineSegment StartX=-11 StartY=0 StartZ=0 EndX=-14 EndY=-17.5 EndZ=0
    g1: LineSegment StartX=-14 StartY=-17.5 StartZ=0 EndX=-7 EndY=-34.5 EndZ=0
    g2: LineSegment StartX=-7 StartY=-34.5 StartZ=0 EndX=-6 EndY=-34.5 EndZ=0
    g3: LineSegment StartX=-6 StartY=-34.5 StartZ=0 EndX=-6 EndY=0 EndZ=0
    g4: LineSegment StartX=-6 StartY=0 StartZ=0 EndX=-11 EndY=0 EndZ=0
    g5: LineSegment StartX=20 StartY=-17.5 StartZ=0 EndX=6 EndY=-17.5 EndZ=0
    g6: LineSegment StartX=6 StartY=-17.5 StartZ=0 EndX=6 EndY=0 EndZ=0
    g7: LineSegment StartX=6 StartY=0 StartZ=0 EndX=11 EndY=0 EndZ=0
    g8: LineSegment StartX=11 StartY=0 StartZ=0 EndX=20 EndY=-17.5 EndZ=0
  constraints (21):
    c: Coincident(g-3,g0)
    c: Coincident(g0,g-4)
    c: Coincident(g0,g1)
    c: Coincident(g1,g-4)
    c: Coincident(g1,g2)
    c: Coincident(g2,g-6)
    c: Coincident(g2,g3)
    c: PointOnObject(g3,g-1)
    c: Vertical(g3)
    c: Coincident(g3,g4)
    c: Coincident(g4,g0)
    c: Coincident(g-5,g5)
    c: Horizontal(g5)
    c: Coincident(g5,g6)
    c: PointOnObject(g6,g-1)
    c: Vertical(g6)
    c: Coincident(g6,g7)
    c: Coincident(g7,g-5)
    c: Coincident(g7,g8)
    c: Distance(g7) = 5
    c: Coincident(g8,g5)
FEATURE [PartDesign::Pad] Pad191
  BaseFeature = -> Pad190
  Length = 1
  Length2 = 100
  Profile = -> Sketch348
  Refine = true
  Reversed = true
  Type = 0
FEATURE [Sketcher::SketchObject] Sketch349
  ExternalGeometry = -> [Sketch346]
  MapMode = 5
  Placement = pos=(0,0,1) rot=(0,0,1;0rad)
  Support = -> [Pad191]
  sketch-geometry (4):
    g0: LineSegment StartX=20 StartY=34.5 StartZ=0 EndX=-7 EndY=34.5 EndZ=0
    g1: LineSegment StartX=-7 StartY=34.5 StartZ=0 EndX=-6.58824 EndY=35.5 EndZ=0
    g2: LineSegment StartX=-6.58824 StartY=35.5 StartZ=0 EndX=20 EndY=35.5 EndZ=0
    g3: LineSegment StartX=20 StartY=35.5 StartZ=0 EndX=20 EndY=34.5 EndZ=0
  constraints (10):
    c: Coincident(g-4,g0)
    c: Coincident(g0,g-3)
    c: Coincident(g0,g1)
    c: Coincident(g1,g2)
    c: Horizontal(g2)
    c: Coincident(g2,g3)
    c: Coincident(g3,g0)
    c: Vertical(g3)
    c: Parallel(g1,g-3)
    c: Distance(g3) = 1
FEATURE [PartDesign::Pad] Pad192
  BaseFeature = -> Pad191
  Length = 10
  Length2 = 100
  Profile = -> Sketch349
  Refine = true
  Reversed = true
  Type = 3
  UpToFace = -> Pad191 [Face19]
FEATURE [Sketcher::SketchObject] Sketch350
  ExternalGeometry = -> [Pad192]
  MapMode = 5
  Placement = pos=(0,35.5,0) rot=(0,0.707107,0.707107;3.14159rad)
  Support = -> [Pad192]
  sketch-geometry (14):
    g0: GeomPoint X=-10.2 Y=-8.3 Z=0
    g1: GeomPoint X=-3.2 Y=-27.3 Z=0
    g2: LineSegment [constr] StartX=-10.2 StartY=-33.3 StartZ=0 EndX=-2.2 EndY=-33.3 EndZ=0
    g3: LineSegment [constr] StartX=-2.2 StartY=-33.3 StartZ=0 EndX=-2.2 EndY=-38.8 EndZ=0
    g4: LineSegment [constr] StartX=-2.2 StartY=-38.8 StartZ=0 EndX=-10.2 EndY=-38.8 EndZ=0
    g5: LineSegment [constr] StartX=-10.2 StartY=-38.8 StartZ=0 EndX=-10.2 EndY=-33.3 EndZ=0
    g6: LineSegment StartX=-13.0579 StartY=0 StartZ=0 EndX=1.67895 EndY=-40 EndZ=0
    g7: LineSegment StartX=1.67895 StartY=-40 StartZ=0 EndX=1.27895 EndY=-40 EndZ=0
    g8: LineSegment StartX=1.27895 StartY=-40 StartZ=0 EndX=-13.4579 EndY=0 EndZ=0
    g9: LineSegment StartX=-13.4579 StartY=0 StartZ=0 EndX=-13.0579 EndY=0 EndZ=0
    g10: GeomPoint X=-3.2 Y=-27.8429 Z=0
    g11: GeomPoint X=-3.2 Y=-26.7571 Z=0
    g12: GeomPoint X=-10.2 Y=-7.75714 Z=0
    g13: GeomPoint X=-10.2 Y=-8.84286 Z=0
  constraints (34):
    c: Coincident(g2,g3)
    c: Coincident(g3,g4)
    c: Coincident(g4,g5)
    c: Coincident(g5,g2)
    c: Horizontal(g2)
    c: Horizontal(g4)
    c: Vertical(g3)
    c: Vertical(g5)
    c: Distance(g2) = 8
    c: Distance(g5) = 5.5
    c: DistanceY(g3) = -38.8
    c: DistanceX(g3) = -2.2
    c: Vertical(g2,g0)
    c: Distance(g0,g2) = 25
    c: DistanceX(g1,g2) = 1
    c: DistanceY(g2,g1) = 6
    c: PointOnObject(g6,g-3)
    c: Coincident(g6,g7)
    c: PointOnObject(g7,g-3)
    c: Coincident(g7,g8)
    c: Coincident(g8,g9)
    c: Coincident(g9,g6)
    c: Parallel(g6,g8)
    c: PointOnObject(g10,g8)
    c: PointOnObject(g11,g6)
    c: PointOnObject(g12,g6)
    c: PointOnObject(g13,g8)
    c: Symmetric(g12,g13,g0)
    c: Symmetric(g11,g10,g1)
    c: Vertical(g11,g10)
    c: Vertical(g12,g13)
    c: Distance(g9) = 0.4
    c: PointOnObject(g8,g-1)
    c: Horizontal(g9)
FEATURE [PartDesign::Pocket] Pocket147
  BaseFeature = -> Pad192
  Length = 5
  Length2 = 100
  Profile = -> Sketch350
  Refine = true
  Type = 2
FEATURE [PartDesign::Body] Body092
  Group = -> [Sketch346,Pad189,Sketch347,Pad190,Sketch348,Pad191,Sketch349,Pad192,Sketch350,Pocket147]
  Origin = -> Origin104
  Placement = pos=(43,-210,-203.5) rot=(0.57735,0.57735,-0.57735;2.0944rad)
  Tip = -> Pocket147
FEATURE [Sketcher::SketchObject] Sketch351
  MapMode = 5
  Support = -> [XY_Plane105]
  sketch-geometry (7):
    g0: LineSegment StartX=-11.5 StartY=0 StartZ=0 EndX=-20.5 EndY=17.5 EndZ=0
    g1: LineSegment StartX=-20.5 StartY=17.5 StartZ=0 EndX=-20.5 EndY=34.5 EndZ=0
    g2: LineSegment StartX=-20.5 StartY=34.5 StartZ=0 EndX=7.5 EndY=34.5 EndZ=0
    g3: LineSegment StartX=7.5 StartY=34.5 StartZ=0 EndX=14.5 EndY=17.5 EndZ=0
    g4: LineSegment StartX=14.5 StartY=17.5 StartZ=0 EndX=11.5 EndY=0 EndZ=0
    g5: LineSegment StartX=11.5 StartY=0 StartZ=0 EndX=-11.5 EndY=0 EndZ=0
    g6: GeomPoint X=0 Y=17.5 Z=0
  constraints (20):
    c: PointOnObject(g0,g-1)
    c: Coincident(g0,g1)
    c: Coincident(g1,g2)
    c: Horizontal(g2)
    c: Coincident(g2,g3)
    c: Coincident(g3,g4)
    c: PointOnObject(g4,g-1)
    c: Coincident(g4,g5)
    c: Coincident(g5,g0)
    c: Distance(g-1,g0) = 11.5
    c: Distance(g-1,g4) = 11.5
    c: PointOnObject(g6,g-2)
    c: Horizontal(g6,g3)
    c: Distance(g6,g3) = 14.5
    c: Horizontal(g6,g0)
    c: Distance(g0,g6) = 20.5
    c: Distance(g-1,g6) = 17.5
    c: Distance(g2) = 28
    c: Vertical(g1)
    c: Distance(g1) = 17
FEATURE [PartDesign::Pad] Pad193
  Length = 1
  Length2 = 100
  Profile = -> Sketch351
  Refine = true
  Type = 0
FEATURE [Sketcher::SketchObject] Sketch352
  ExternalGeometry = -> [Pad193]
  MapMode = 5
  Placement = pos=(0,0,0) rot=(1,0,0;3.14159rad)
  Support = -> [Pad193]
  sketch-geometry (12):
    g0: LineSegment StartX=-20.5 StartY=-34.5 StartZ=0 EndX=-20.5 EndY=-17.5 EndZ=0
    g1: LineSegment StartX=-20.5 StartY=-17.5 StartZ=0 EndX=-11.5 EndY=0 EndZ=0
    g2: LineSegment StartX=-11.5 StartY=0 StartZ=0 EndX=-10.5 EndY=0 EndZ=0
    g3: LineSegment StartX=-10.5 StartY=0 StartZ=0 EndX=-19.5 EndY=-17.5 EndZ=0
    g4: LineSegment StartX=-19.5 StartY=-17.5 StartZ=0 EndX=-19.5 EndY=-34.5 EndZ=0
    g5: LineSegment StartX=-19.5 StartY=-34.5 StartZ=0 EndX=-20.5 EndY=-34.5 EndZ=0
    g6: LineSegment StartX=11.5 StartY=0 StartZ=0 EndX=14.5 EndY=-17.5 EndZ=0
    g7: LineSegment StartX=14.5 StartY=-17.5 StartZ=0 EndX=7.5 EndY=-34.5 EndZ=0
    g8: LineSegment StartX=7.5 StartY=-34.5 StartZ=0 EndX=6.5 EndY=-34.5 EndZ=0
    g9: LineSegment StartX=6.5 StartY=-34.5 StartZ=0 EndX=13.5 EndY=-17.5 EndZ=0
    g10: LineSegment StartX=13.5 StartY=-17.5 StartZ=0 EndX=10.5 EndY=0 EndZ=0
    g11: LineSegment StartX=10.5 StartY=0 StartZ=0 EndX=11.5 EndY=0 EndZ=0
  constraints (30):
    c: Coincident(g-4,g0)
    c: Coincident(g0,g-4)
    c: Coincident(g0,g1)
    c: Coincident(g1,g-3)
    c: Coincident(g1,g2)
    c: PointOnObject(g2,g-1)
    c: Coincident(g2,g3)
    c: Coincident(g3,g4)
    c: Coincident(g4,g5)
    c: Coincident(g5,g0)
    c: Coincident(g-5,g6)
    c: Coincident(g6,g-6)
    c: Coincident(g6,g7)
    c: Coincident(g7,g-6)
    c: Coincident(g7,g8)
    c: Horizontal(g8)
    c: Coincident(g8,g9)
    c: Coincident(g9,g10)
    c: PointOnObject(g10,g-1)
    c: Coincident(g10,g11)
    c: Coincident(g11,g6)
    c: Horizontal(g0,g3)
    c: Horizontal(g3,g9)
    c: Horizontal(g5)
    c: Equal(g11,g2)
    c: Parallel(g3,g1)
    c: Distance(g8) = 1
    c: Equal(g5,g8)
    c: Equal(g8,g11)
    c: Parallel(g6,g10)
FEATURE [PartDesign::Pad] Pad194
  BaseFeature = -> Pad193
  Length = 41
  Length2 = 100
  Profile = -> Sketch352
  Refine = true
  Type = 0
FEATURE [Sketcher::SketchObject] Sketch353
  ExternalGeometry = -> [Pad194]
  MapMode = 5
  Placement = pos=(0,0,-41) rot=(1,0,0;3.14159rad)
  Support = -> [Pad194]
  sketch-geometry (9):
    g0: LineSegment StartX=11.5 StartY=0 StartZ=0 EndX=14.5 EndY=-17.5 EndZ=0
    g1: LineSegment StartX=14.5 StartY=-17.5 StartZ=0 EndX=7.5 EndY=-34.5 EndZ=0
    g2: LineSegment StartX=7.5 StartY=-34.5 StartZ=0 EndX=6.5 EndY=-34.5 EndZ=0
    g3: LineSegment StartX=6.5 StartY=-34.5 StartZ=0 EndX=6.5 EndY=0 EndZ=0
    g4: LineSegment StartX=6.5 StartY=0 StartZ=0 EndX=11.5 EndY=0 EndZ=0
    g5: LineSegment StartX=-6.5 StartY=-17.5 StartZ=0 EndX=-20.5 EndY=-17.5 EndZ=0
    g6: LineSegment StartX=-20.5 StartY=-17.5 StartZ=0 EndX=-11.5 EndY=0 EndZ=0
    g7: LineSegment StartX=-11.5 StartY=0 StartZ=0 EndX=-6.5 EndY=0 EndZ=0
    g8: LineSegment StartX=-6.5 StartY=0 StartZ=0 EndX=-6.5 EndY=-17.5 EndZ=0
  constraints (22):
    c: Coincident(g0,g1)
    c: Coincident(g1,g2)
    c: Coincident(g2,g3)
    c: Coincident(g3,g4)
    c: Coincident(g4,g0)
    c: Horizontal(g5)
    c: Coincident(g5,g6)
    c: Coincident(g6,g7)
    c: Coincident(g7,g8)
    c: Distance(g7) = 5
    c: Coincident(g8,g5)
    c: Vertical(g8)
    c: Horizontal(g7)
    c: Coincident(g6,g-5)
    c: Coincident(g5,g-5)
    c: Coincident(g-3,g0)
    c: Coincident(g0,g-4)
    c: Coincident(g-4,g1)
    c: Horizontal(g4)
    c: Horizontal(g2)
    c: Distance(g2) = 1
    c: Vertical(g3)
FEATURE [PartDesign::Pad] Pad195
  BaseFeature = -> Pad194
  Length = 1
  Length2 = 100
  Profile = -> Sketch353
  Refine = true
  Reversed = true
  Type = 0
FEATURE [Sketcher::SketchObject] Sketch354
  ExternalGeometry = -> [Sketch351]
  MapMode = 5
  Placement = pos=(0,0,1) rot=(0,0,1;0rad)
  Support = -> [Pad195]
  sketch-geometry (4):
    g0: LineSegment StartX=7.5 StartY=34.5 StartZ=0 EndX=-20.5 EndY=34.5 EndZ=0
    g1: LineSegment StartX=-20.5 StartY=34.5 StartZ=0 EndX=-20.5 EndY=35.5 EndZ=0
    g2: LineSegment StartX=-20.5 StartY=35.5 StartZ=0 EndX=7.08824 EndY=35.5 EndZ=0
    g3: LineSegment StartX=7.08824 StartY=35.5 StartZ=0 EndX=7.5 EndY=34.5 EndZ=0
  constraints (10):
    c: Coincident(g-4,g0)
    c: Coincident(g0,g-3)
    c: Coincident(g0,g1)
    c: Coincident(g1,g2)
    c: Horizontal(g2)
    c: Coincident(g2,g3)
    c: Coincident(g3,g0)
    c: Parallel(g1,g-3)
    c: Parallel(g3,g-4)
    c: DistanceY(g0,g2) = 1
FEATURE [PartDesign::Pad] Pad196
  BaseFeature = -> Pad195
  Length = 10
  Length2 = 100
  Profile = -> Sketch354
  Refine = true
  Reversed = true
  Type = 3
  UpToFace = -> Pad195 [Face19]
FEATURE [Sketcher::SketchObject] Sketch355
  ExternalGeometry = -> [Pad196]
  MapMode = 5
  Placement = pos=(0,35.5,0) rot=(0,0.707107,0.707107;3.14159rad)
  Support = -> [Pad196]
  sketch-geometry (15):
    g0: GeomPoint X=2.2 Y=-8.3 Z=0
    g1: GeomPoint X=9.2 Y=-27.3 Z=0
    g2: LineSegment [constr] StartX=10.2 StartY=-33.3 StartZ=0 EndX=2.2 EndY=-33.3 EndZ=0
    g3: LineSegment [constr] StartX=2.2 StartY=-33.3 StartZ=0 EndX=2.2 EndY=-38.8 EndZ=0
    g4: LineSegment [constr] StartX=2.2 StartY=-38.8 StartZ=0 EndX=10.2 EndY=-38.8 EndZ=0
    g5: LineSegment [constr] StartX=10.2 StartY=-38.8 StartZ=0 EndX=10.2 EndY=-33.3 EndZ=0
    g6: GeomPoint X=9.2 Y=-26.7215 Z=0
    g7: GeomPoint X=9.2 Y=-27.8785 Z=0
    g8: GeomPoint X=2.2 Y=-8.87853 Z=0
    g9: GeomPoint X=2.2 Y=-7.72147 Z=0
    g10: LineSegment StartX=-1.07104 StartY=0 StartZ=0 EndX=-0.644753 EndY=0 EndZ=0
    g11: LineSegment StartX=-0.644753 StartY=0 StartZ=0 EndX=14.4605 EndY=-41 EndZ=0
    g12: LineSegment StartX=14.4605 StartY=-41 StartZ=0 EndX=14.0342 EndY=-41 EndZ=0
    g13: LineSegment StartX=14.0342 StartY=-41 StartZ=0 EndX=-1.07104 EndY=0 EndZ=0
    g14: LineSegment [constr] StartX=-0.644753 StartY=0 StartZ=0 EndX=-1.02009 EndY=-0.138282 EndZ=0
  constraints (37):
    c: Coincident(g2,g3)
    c: Coincident(g3,g4)
    c: Coincident(g4,g5)
    c: Coincident(g5,g2)
    c: Horizontal(g2)
    c: Horizontal(g4)
    c: Vertical(g3)
    c: Vertical(g5)
    c: Distance(g5) = 5.5
    c: DistanceY(g3) = -38.8
    c: DistanceX(g3) = 2.2
    c: DistanceY(g2,g1) = 6
    c: Symmetric(g8,g9,g0)
    c: Symmetric(g7,g6,g1)
    c: Vertical(g7,g6)
    c: Vertical(g8,g9)
    c: Distance(g4) = 8
    c: DistanceX(g1,g2) = 1
    c: DistanceY(g2,g0) = 25
    c: Vertical(g0,g2)
    c: PointOnObject(g10,g-1)
    c: Horizontal(g10)
    c: Coincident(g10,g11)
    c: Coincident(g11,g12)
    c: Coincident(g12,g13)
    c: Coincident(g13,g10)
    c: Horizontal(g12)
    c: Horizontal(g11,g-4)
    c: Parallel(g11,g13)
    c: PointOnObject(g6,g11)
    c: PointOnObject(g7,g13)
    c: PointOnObject(g9,g11)
    c: PointOnObject(g8,g13)
    c: Coincident(g14,g10)
    c: PointOnObject(g14,g13)
    c: Perpendicular(g13,g14)
    c: Distance(g14) = 0.4
FEATURE [PartDesign::Pocket] Pocket148
  BaseFeature = -> Pad196
  Length = 5
  Length2 = 100
  Profile = -> Sketch355
  Refine = true
  Type = 2
FEATURE [PartDesign::Body] Body093
  Group = -> [Sketch351,Pad193,Sketch352,Pad194,Sketch353,Pad195,Sketch354,Pad196,Sketch355,Pocket148]
  Origin = -> Origin105
  Placement = pos=(43,10,-203.5) rot=(0.57735,0.57735,0.57735;4.18879rad)
  Tip = -> Pocket148
FEATURE [Sketcher::SketchObject] Sketch356
  MapMode = 5
  Support = -> [XY_Plane106]
  sketch-geometry (15):
    g0: ArcOfCircle CenterX=1101.52 CenterY=5 CenterZ=0 NormalX=0 NormalY=0 NormalZ=1 AngleXU=0 Radius=1108.6 StartAngle=3.12896 EndAngle=3.15422
    g1: LineSegment StartX=-6.98782 StartY=19 StartZ=0 EndX=20 EndY=19 EndZ=0
    g2: LineSegment StartX=20 StartY=19 StartZ=0 EndX=20 EndY=-9 EndZ=0
    g3: LineSegment StartX=20 StartY=-9 StartZ=0 EndX=-6.98782 EndY=-9 EndZ=0
    g4: ArcOfCircle CenterX=1102.52 CenterY=5 CenterZ=0 NormalX=0 NormalY=0 NormalZ=1 AngleXU=0 Radius=1108.6 StartAngle=3.12987 EndAngle=3.15332
    g5: LineSegment StartX=-6 StartY=18 StartZ=0 EndX=19 EndY=18 EndZ=0
    g6: LineSegment StartX=19 StartY=18 StartZ=0 EndX=19 EndY=-8 EndZ=0
    g7: LineSegment StartX=19 StartY=-8 StartZ=0 EndX=-6 EndY=-8 EndZ=0
    g8: LineSegment [constr] StartX=19 StartY=18 StartZ=0 EndX=20 EndY=18 EndZ=0
    g9: LineSegment [constr] StartX=19 StartY=18 StartZ=0 EndX=19 EndY=19 EndZ=0
    g10: LineSegment [constr] StartX=-6.07622 StartY=5 StartZ=0 EndX=-7.07622 EndY=5 EndZ=0
    g11: LineSegment [constr] StartX=19 StartY=-8 StartZ=0 EndX=19 EndY=-9 EndZ=0
    g12: GeomPoint X=1102.52 Y=18 Z=0
    g13: GeomPoint X=1102.52 Y=-8 Z=0
    g14: LineSegment [constr] StartX=1101.52 StartY=5 StartZ=0 EndX=1102.52 EndY=5 EndZ=0
  constraints (43):
    c: Coincident(g1,g2)
    c: Coincident(g2,g3)
    c: Coincident(g3,g0)
    c: Coincident(g0,g1)
    c: Vertical(g2)
    c: Horizontal(g3)
    c: Horizontal(g1)
    c: Coincident(g5,g6)
    c: Coincident(g6,g7)
    c: Horizontal(g5)
    c: Horizontal(g7)
    c: Vertical(g6)
    c: Coincident(g5,g4)
    c: Coincident(g4,g7)
    c: Horizontal(g0,g4)
    c: Coincident(g8,g5)
    c: PointOnObject(g8,g2)
    c: Horizontal(g8)
    c: Coincident(g9,g5)
    c: PointOnObject(g9,g1)
    c: Vertical(g9)
    c: Equal(g9,g8)
    c: PointOnObject(g10,g4)
    c: PointOnObject(g10,g0)
    c: Horizontal(g10)
    c: Horizontal(g10,g0)
    c: Equal(g10,g8)
    c: Coincident(g11,g6)
    c: PointOnObject(g11,g3)
    c: Vertical(g11)
    c: Equal(g11,g8)
    c: Distance(g8) = 1
    c: PointOnObject(g12,g5)
    c: PointOnObject(g13,g7)
    c: Symmetric(g12,g13,g4)
    c: Vertical(g12,g4)
    c: Coincident(g14,g0)
    c: Coincident(g14,g4)
    c: Equal(g14,g8)
    c: Distance(g7) = 25
    c: Distance(g6) = 26
    c: DistanceY(g6) = -8
    c: DistanceX(g6) = 19
FEATURE [PartDesign::Pad] Pad197
  Length = 9
  Length2 = 110
  Profile = -> Sketch356
  Refine = true
  Type = 4
FEATURE [Sketcher::SketchObject] Sketch358
  ExternalGeometry = -> [Pad197]
  MapMode = 5
  Placement = pos=(0,19,0) rot=(0,0.707107,0.707107;3.14159rad)
  Support = -> [Pad197]
  sketch-geometry (4):
    g0: LineSegment StartX=0 StartY=9 StartZ=0 EndX=-6 EndY=0 EndZ=0
    g1: LineSegment StartX=0 StartY=9 StartZ=0 EndX=-20 EndY=9 EndZ=0
    g2: LineSegment StartX=-20 StartY=9 StartZ=0 EndX=-20 EndY=-21 EndZ=0
    g3: LineSegment StartX=-6 StartY=0 StartZ=0 EndX=-20 EndY=-21 EndZ=0
  constraints (11):
    c: PointOnObject(g0,g-2)
    c: Coincident(g1,g0)
    c: Horizontal(g1)
    c: Coincident(g2,g1)
    c: Vertical(g2)
    c: Coincident(g1,g-3)
    c: Distance(g-1,g0) = 6
    c: PointOnObject(g0,g-1)
    c: Coincident(g3,g0)
    c: Coincident(g3,g2)
    c: Parallel(g0,g3)
FEATURE [PartDesign::Pocket] Pocket149
  BaseFeature = -> Pad197
  Length = 5
  Length2 = 100
  Profile = -> Sketch358
  Refine = true
  Type = 1
FEATURE [Sketcher::SketchObject] Sketch359
  MapMode = 5
  Support = -> [XY_Plane107]
  sketch-geometry (6):
    g0: LineSegment StartX=-10 StartY=14 StartZ=0 EndX=9 EndY=14 EndZ=0
    g1: LineSegment StartX=9 StartY=14 StartZ=0 EndX=20 EndY=-13.9106 EndZ=0
    g2: LineSegment StartX=20 StartY=-13.9106 StartZ=0 EndX=5 EndY=-13.9106 EndZ=0
    g3: LineSegment StartX=5 StartY=-13.9106 StartZ=0 EndX=5 EndY=5 EndZ=0
    g4: LineSegment StartX=5 StartY=5 StartZ=0 EndX=-10 EndY=5 EndZ=0
    g5: LineSegment StartX=-10 StartY=5 StartZ=0 EndX=-10 EndY=14 EndZ=0
  constraints (18):
    c: Horizontal(g0)
    c: Coincident(g0,g1)
    c: Coincident(g1,g2)
    c: Coincident(g2,g3)
    c: Coincident(g3,g4)
    c: Horizontal(g4)
    c: Coincident(g4,g5)
    c: Coincident(g5,g0)
    c: Vertical(g5)
    c: Distance(g0) = 19
    c: Distance(g5) = 9
    c: DistanceY(g4) = 5
    c: DistanceX(g4) = -10
    c: Vertical(g3)
    c: Horizontal(g2)
    c: Distance(g1) = 30
    c: DistanceX(g0,g1) = 30
    c: Distance(g4) = 15
FEATURE [PartDesign::Pad] Pad198
  Length = 36
  Length2 = 100
  Profile = -> Sketch359
  Refine = true
  Reversed = true
  Type = 0
FEATURE [PartDesign::Body] Body095
  Group = -> [Sketch359,Pad198]
  Origin = -> Origin107
  Placement = pos=(9,0,-150) rot=(0,1,0;3.14159rad)
  Tip = -> Pad198
FEATURE [Sketcher::SketchObject] Sketch360
  ExternalGeometry = -> [Pocket149]
  MapMode = 5
  Placement = pos=(0,19,0) rot=(0,0.707107,0.707107;3.14159rad)
  Support = -> [Pocket149]
  sketch-geometry (4):
    g0: LineSegment StartX=-20 StartY=-86 StartZ=0 EndX=37.3333 EndY=0 EndZ=0
    g1: LineSegment StartX=-20 StartY=-86 StartZ=0 EndX=-20 EndY=-115.903 EndZ=0
    g2: LineSegment StartX=-20 StartY=-115.903 StartZ=0 EndX=37.3333 EndY=-115.903 EndZ=0
    g3: LineSegment StartX=37.3333 StartY=0 StartZ=0 EndX=37.3333 EndY=-115.903 EndZ=0
  constraints (11):
    c: Parallel(g-3,g0)
    c: Vertical(g-3,g0)
    c: PointOnObject(g0,g-1)
    c: Coincident(g1,g0)
    c: Vertical(g1)
    c: Coincident(g2,g1)
    c: Horizontal(g2)
    c: Coincident(g3,g0)
    c: Coincident(g3,g2)
    c: Vertical(g3)
    c: DistanceY(g0,g-1) = 86
FEATURE [PartDesign::Pocket] Pocket150
  BaseFeature = -> Pocket149
  Length = 5
  Length2 = 100
  Profile = -> Sketch360
  Refine = true
  Type = 1
FEATURE [PartDesign::Plane] DatumPlane009
  AttachmentOffset = pos=(0,0,-50) rot=(0,0,1;0rad)
  Length = 60
  MapMode = 5
  Placement = pos=(0,0,-50) rot=(0,0,1;0rad)
  ResizeMode = 0
  Support = -> [XY_Plane106]
  Width = 60
FEATURE [Sketcher::SketchObject] Sketch361
  ExternalGeometry = -> [Pocket150]
  MapMode = 5
  Placement = pos=(0,0,-50) rot=(0,0,1;0rad)
  Support = -> [DatumPlane009]
  sketch-geometry (8):
    g0: LineSegment StartX=-1.3e-15 StartY=19 StartZ=0 EndX=-12.9293 EndY=-13.5244 EndZ=0
    g1: LineSegment StartX=-12.9293 StartY=-13.5244 StartZ=0 EndX=-12 EndY=-13.8938 EndZ=0
    g2: LineSegment StartX=-12 StartY=-13.8938 StartZ=0 EndX=0.678591 EndY=18 EndZ=0
    g3: LineSegment StartX=-1.3e-15 StartY=19 StartZ=0 EndX=20 EndY=19 EndZ=0
    g4: LineSegment StartX=20 StartY=19 StartZ=0 EndX=20 EndY=5 EndZ=0
    g5: LineSegment StartX=0.678591 StartY=18 StartZ=0 EndX=19 EndY=18 EndZ=0
    g6: LineSegment StartX=19 StartY=18 StartZ=0 EndX=19 EndY=5 EndZ=0
    g7: LineSegment StartX=19 StartY=5 StartZ=0 EndX=20 EndY=5 EndZ=0
  constraints (22):
    c: PointOnObject(g0,g-3)
    c: Coincident(g1,g0)
    c: Coincident(g2,g1)
    c: PointOnObject(g2,g-4)
    c: Coincident(g3,g0)
    c: Coincident(g3,g-3)
    c: Coincident(g4,g3)
    c: Vertical(g4)
    c: Parallel(g2,g0)
    c: Distance(g0) = 35
    c: Distance(g3) = 20
    c: DistanceX(g1,g-4) = 31
    c: Coincident(g2,g5)
    c: Coincident(g5,g-4)
    c: Coincident(g5,g6)
    c: Vertical(g6)
    c: Coincident(g6,g7)
    c: Horizontal(g7)
    c: Coincident(g4,g7)
    c: Equal(g7,g1)
    c: Distance(g4) = 14
    c: Perpendicular(g1,g0)
FEATURE [PartDesign::Pad] Pad199
  BaseFeature = -> Pocket150
  Length = 10
  Length2 = 36
  Profile = -> Sketch361
  Refine = true
  Reversed = true
  Type = 4
FEATURE [Sketcher::SketchObject] Sketch362
  ExternalGeometry = -> [Pad199]
  MapMode = 5
  Placement = pos=(0,0,-40) rot=(0,0,1;0rad)
  Support = -> [Pad199]
  sketch-geometry (4):
    g0: LineSegment StartX=-6.98782 StartY=19 StartZ=0 EndX=0.678591 EndY=19 EndZ=0
    g1: LineSegment StartX=0.678591 StartY=19 StartZ=0 EndX=0.678591 EndY=18 EndZ=0
    g2: LineSegment StartX=0.678591 StartY=18 StartZ=0 EndX=-7.0574 EndY=-1.46036 EndZ=0
    g3: ArcOfCircle CenterX=1101.52 CenterY=5 CenterZ=0 NormalX=0 NormalY=0 NormalZ=1 AngleXU=0 Radius=1108.6 StartAngle=3.12896 EndAngle=3.14742
  constraints (11):
    c: Horizontal(g0)
    c: Coincident(g1,g0)
    c: Coincident(g1,g-4)
    c: Coincident(g2,g1)
    c: PointOnObject(g2,g-4)
    c: PointOnObject(g2,g-3)
    c: Vertical(g1)
    c: Coincident(g3,g0)
    c: Coincident(g3,g2)
    c: Coincident(g0,g-3)
    c: Equal(g-3,g3)
FEATURE [PartDesign::Pad] Pad200
  BaseFeature = -> Pad199
  Length = 1
  Length2 = 100
  Profile = -> Sketch362
  Refine = true
  Type = 0
FEATURE [Sketcher::SketchObject] Sketch363
  ExternalGeometry = -> [Pad200]
  MapMode = 5
  Placement = pos=(0,-9,0) rot=(1,0,0;1.5708rad)
  Support = -> [Pad200]
  sketch-geometry (6):
    g0: LineSegment StartX=-6.98782 StartY=-86 StartZ=0 EndX=20 EndY=-86 EndZ=0
    g1: LineSegment StartX=20 StartY=-86 StartZ=0 EndX=20 EndY=-21 EndZ=0
    g2: LineSegment StartX=20 StartY=-21 StartZ=0 EndX=-1.421e-13 EndY=9 EndZ=0
    g3: LineSegment StartX=-6.98782 StartY=-45.5183 StartZ=0 EndX=-6.98782 EndY=-86 EndZ=0
    g4: LineSegment StartX=-6.98782 StartY=-45.5183 StartZ=0 EndX=-1.421e-13 EndY=-45.5183 EndZ=0
    g5: LineSegment StartX=-1.421e-13 StartY=-45.5183 StartZ=0 EndX=-1.421e-13 EndY=9 EndZ=0
  constraints (14):
    c: Horizontal(g0)
    c: Coincident(g1,g-3)
    c: Coincident(g1,g2)
    c: Coincident(g-4,g0)
    c: Coincident(g0,g1)
    c: Coincident(g3,g-4)
    c: Vertical(g3)
    c: Coincident(g0,g3)
    c: Coincident(g4,g3)
    c: Horizontal(g4)
    c: Coincident(g5,g4)
    c: Coincident(g5,g2)
    c: Coincident(g-3,g2)
    c: Vertical(g5)
FEATURE [PartDesign::Pocket] Pocket151
  BaseFeature = -> Pad200
  Length = 3
  Length2 = 100
  Profile = -> Sketch363
  Refine = true
  Type = 2
FEATURE [Sketcher::SketchObject] Sketch364
  ExternalGeometry = -> [Pocket151]
  MapMode = 5
  Placement = pos=(1.1e-14,19,8.5e-15) rot=(0,0.707107,0.707107;3.14159rad)
  Support = -> [Pocket151]
  expr: Constraints[3] = 1 + 18 - 6
  expr: Constraints[2] = 6mm
  expr: Constraints[0] = 12mm
  expr: Constraints[1] = 36 - 5
  sketch-geometry (12):
    g0: GeomPoint X=-7 Y=-74 Z=0
    g1: GeomPoint X=-14 Y=-55 Z=0
    g2: LineSegment StartX=-14 StartY=-54.4215 StartZ=0 EndX=-7 EndY=-73.4215 EndZ=0
    g3: LineSegment StartX=-7 StartY=-74.5785 StartZ=0 EndX=-14 EndY=-55.5785 EndZ=0
    g4: LineSegment StartX=-7 StartY=-73.4215 StartZ=0 EndX=-2.36581 EndY=-86 EndZ=0
    g5: LineSegment StartX=-7 StartY=-74.5785 StartZ=0 EndX=-2.79209 EndY=-86 EndZ=0
    g6: LineSegment StartX=-2.79209 StartY=-86 StartZ=0 EndX=-2.36581 EndY=-86 EndZ=0
    g7: LineSegment StartX=-14 StartY=-54.4215 StartZ=0 EndX=-18.6247 EndY=-41.8688 EndZ=0
    g8: LineSegment StartX=-14 StartY=-55.5785 StartZ=0 EndX=-19 EndY=-42.0071 EndZ=0
    g9: LineSegment [constr] StartX=-18.6247 StartY=-41.8688 StartZ=0 EndX=-19 EndY=-42.0071 EndZ=0
    g10: LineSegment StartX=-18.6247 StartY=-41.8688 StartZ=0 EndX=-19 EndY=-40.85 EndZ=0
    g11: LineSegment StartX=-19 StartY=-40.85 StartZ=0 EndX=-19 EndY=-42.0071 EndZ=0
  constraints (31):
    c: DistanceY(g-3,g0) = 12
    c: DistanceY(g-3,g1) = 31
    c: DistanceX(g-3,g1) = 6
    c: DistanceX(g-3,g0) = 13
    c: Symmetric(g2,g3,g1)
    c: Vertical(g2,g3)
    c: Symmetric(g2,g3,g0)
    c: Vertical(g2,g3)
    c: Coincident(g4,g2)
    c: PointOnObject(g4,g-3)
    c: Coincident(g5,g3)
    c: PointOnObject(g5,g-3)
    c: Coincident(g6,g5)
    c: Coincident(g6,g4)
    c: Coincident(g7,g2)
    c: Coincident(g8,g3)
    c: Coincident(g9,g7)
    c: Coincident(g9,g8)
    c: Parallel(g7,g8)
    c: Parallel(g8,g2)
    c: Parallel(g2,g4)
    c: Parallel(g4,g5)
    c: Parallel(g3,g2)
    c: Perpendicular(g7,g9)
    c: Coincident(g10,g7)
    c: Coincident(g11,g10)
    c: Vertical(g11)
    c: Distance(g9) = 0.4
    c: DistanceX(g-3,g11) = 1
    c: Coincident(g8,g11)
    c: Parallel(g10,g7)
FEATURE [PartDesign::Pocket] Pocket152
  BaseFeature = -> Pocket151
  Length = 5
  Length2 = 100
  Profile = -> Sketch364
  Refine = true
  Type = 2
FEATURE [PartDesign::Chamfer] Chamfer009
  Angle = 45
  Base = -> Pocket152 [Edge54]
  BaseFeature = -> Pocket152
  ChamferType = 1
  FlipDirection = false
  Refine = true
  Size = 3
  Size2 = 12
  SupportTransform = false
FEATURE [Sketcher::SketchObject] Sketch365
  ExternalGeometry = -> [Chamfer009]
  MapMode = 5
  Placement = pos=(20,0,0) rot=(0.57735,0.57735,0.57735;2.0944rad)
  Support = -> [Chamfer009]
  sketch-geometry (3):
    g0: LineSegment StartX=5.44674 StartY=-86 StartZ=0 EndX=-8 EndY=-40.85 EndZ=0
    g1: LineSegment StartX=-8 StartY=-40.85 StartZ=0 EndX=-8 EndY=-86 EndZ=0
    g2: LineSegment StartX=-8 StartY=-86 StartZ=0 EndX=5.44674 EndY=-86 EndZ=0
  constraints (8):
    c: PointOnObject(g0,g-3)
    c: PointOnObject(g0,g-4)
    c: Coincident(g1,g0)
    c: Coincident(g1,g-4)
    c: Coincident(g2,g1)
    c: Coincident(g2,g0)
    c: PointOnObject(g-5,g0)
    c: Horizontal(g0,g-6)
FEATURE [PartDesign::Pocket] Pocket153
  BaseFeature = -> Chamfer009
  Length = 5
  Length2 = 100
  Profile = -> Sketch365
  Refine = true
  Type = 2
FEATURE [Sketcher::SketchObject] Sketch366
  ExternalGeometry = -> [Pocket153]
  MapMode = 5
  Placement = pos=(4.15385,6e-16,2.76923) rot=(0.426737,0.426737,0.797365;1.79533rad)
  Support = -> [Pocket153]
  sketch-geometry (4):
    g0: LineSegment StartX=19 StartY=-7.56706 StartZ=0 EndX=13 EndY=-7.56706 EndZ=0
    g1: LineSegment StartX=13 StartY=-7.56706 StartZ=0 EndX=13 EndY=-28.5671 EndZ=0
    g2: LineSegment StartX=13 StartY=-28.5671 StartZ=0 EndX=19 EndY=-28.5671 EndZ=0
    g3: LineSegment StartX=19 StartY=-28.5671 StartZ=0 EndX=19 EndY=-7.56706 EndZ=0
  constraints (11):
    c: Coincident(g0,g1)
    c: Coincident(g1,g2)
    c: Coincident(g2,g3)
    c: Coincident(g3,g0)
    c: Horizontal(g0)
    c: Horizontal(g2)
    c: Vertical(g1)
    c: Vertical(g3)
    c: Coincident(g2,g-3)
    c: Distance(g2) = 6
    c: Distance(g3) = 21
FEATURE [PartDesign::Pad] Pad201
  BaseFeature = -> Pocket153
  Length = 1
  Length2 = 100
  Profile = -> Sketch366
  Refine = true
  Reversed = true
  Type = 0
FEATURE [PartDesign::Body] Body094
  Group = -> [Sketch356,Pad197,Sketch358,Pocket149,Sketch360,Pocket150,DatumPlane009,Sketch361,Pad199,Sketch362,Pad200,Sketch363,Pocket151,Sketch364,Pocket152,Chamfer009,Sketch365,Pocket153,Sketch366,Pad201]
  Origin = -> Origin106
  Placement = pos=(0,0,-64) rot=(0,0,1;0rad)
  Tip = -> Pad201
FEATURE [PartDesign::Pocket] Pocket154
  BaseFeature = -> Pad021
  Length = 1
  Length2 = 100
  Profile = -> Sketch060
  Refine = true
  Type = 0
FEATURE [PartDesign::Body] Body008  label="GripperMount"
  Group = -> [Sketch052,Pad018,Sketch053,Pad019,Sketch054,Pocket024,Sketch055,Pocket025,Sketch056,Pad020,PolarPattern003,Sketch057,Pocket026,Sketch058,Pocket029,Sketch059,Pad021,Sketch060,Pocket154]
  Origin = -> Origin008
  Placement = pos=(-1e-15,0,5.16) rot=(0.707107,0.707107,0;3.14159rad)
  Tip = -> Pocket154
FEATURE [PartDesign::Fillet] Fillet038
  Base = -> Pad049 [Edge73,Edge29,Edge112,Edge163,Edge164,Edge169,Edge86,Edge82]
  BaseFeature = -> Pad049
  Radius = 1
  Refine = true
  SupportTransform = false
FEATURE [PartDesign::Fillet] Fillet039
  Base = -> Fillet038 [Edge117]
  BaseFeature = -> Fillet038
  Radius = 1
  Refine = true
  SupportTransform = false
FEATURE [PartDesign::Body] Body026
  Group = -> [Sketch114,Pad062,Sketch128,Pad057,Sketch129,Pad061,Fillet030,Chamfer008,Sketch124,Pad059,Sketch125,Pad058,Sketch123,Pocket061,Sketch118,Pocket058,Sketch113,Pocket056,Sketch112,Pad054,Sketch116,Pad060,Sketch119,Pocket057,Sketch117,Pad050,Sketch115,Pad051,Mirrored015,Mirrored016,Sketch019,Pad052,Pad049,Fillet038,Fillet039]
  Origin = -> Origin029
  Placement = pos=(0,0,-0.1) rot=(0,0,1;0rad)
  Tip = -> Fillet039
FEATURE [App::Part] Part
  Group = -> [Body027,Body026,Body028]
  Origin = -> Origin026
FEATURE [PartDesign::FeatureBase] Clone013
  BaseFeature = -> Body026
  Placement = pos=(0,0,-0.1) rot=(0,0,1;0rad)
FEATURE [PartDesign::Body] Body030
  BaseFeature = -> Body026
  Group = -> [Clone013]
  Origin = -> Origin031
  Tip = -> Clone013
FEATURE [App::Part] Part001
  Group = -> [Body029,Body030,Body031]
  Origin = -> Origin033
  Placement = pos=(43.7,0,-203.8) rot=(0,1,0;1.5708rad)
FEATURE [PartDesign::FeatureBase] Clone015
  BaseFeature = -> Body026
  Placement = pos=(0,0,-0.1) rot=(0,0,1;0rad)
FEATURE [PartDesign::Body] Body033
  Group = -> [Clone015]
  Origin = -> Origin035
  Tip = -> Clone015
FEATURE [App::Part] Part002
  Group = -> [Body034,Body033,Body032]
  Origin = -> Origin036
  Placement = pos=(43.7,-200,-203.8) rot=(0.707107,0,0.707107;3.14159rad)
FEATURE [PartDesign::FeatureBase] Clone018
  BaseFeature = -> Body026
  Placement = pos=(0,0,-0.1) rot=(0,0,1;0rad)
FEATURE [PartDesign::Body] Body036
  Group = -> [Clone018]
  Origin = -> Origin039
  Tip = -> Clone018
FEATURE [App::Part] Part003
  Group = -> [Body037,Body036,Body035]
  Origin = -> Origin040
  Placement = pos=(-1,-192.1,-203.8) rot=(0,-0.707107,-0.707107;3.14159rad)
FEATURE [App::DocumentObjectGroup] Group  label="referenced"
  Group = -> [Body075,Part008,Body055,Body056,Body057,Body058,Part004,Part,Body023,Body]
FEATURE [Sketcher::SketchObject] Sketch367
  MapMode = 5
  Support = -> [XY_Plane108]
  sketch-geometry (6):
    g0: ArcOfCircle CenterX=240 CenterY=0 CenterZ=0 NormalX=0 NormalY=0 NormalZ=1 AngleXU=0 Radius=250 StartAngle=2.8578 EndAngle=3.42539
    g1: ArcOfCircle CenterX=235 CenterY=0 CenterZ=0 NormalX=0 NormalY=0 NormalZ=1 AngleXU=0 Radius=250.204 StartAngle=2.8522 EndAngle=3.43098
    g2: LineSegment StartX=-4.8 StartY=71.4 StartZ=0 EndX=0 EndY=70 EndZ=0
    g3: LineSegment StartX=-4.8 StartY=-71.4 StartZ=0 EndX=2.84e-14 EndY=-70 EndZ=0
    g4: LineSegment [constr] StartX=235 StartY=0 StartZ=0 EndX=240 EndY=0 EndZ=0
    g5: GeomPoint X=-10 Y=0 Z=0
  constraints (18):
    c: PointOnObject(g0,g-1)
    c: PointOnObject(g1,g-1)
    c: Coincident(g2,g1)
    c: Coincident(g2,g0)
    c: Coincident(g3,g1)
    c: Coincident(g3,g0)
    c: PointOnObject(g0,g-2)
    c: PointOnObject(g0,g-2)
    c: Coincident(g4,g1)
    c: Coincident(g4,g0)
    c: Equal(g4,g2)
    c: Perpendicular(g0,g2)
    c: Perpendicular(g0,g3)
    c: Distance(g0,g0) = 140
    c: Distance(g3) = 5
    c: PointOnObject(g5,g0)
    c: PointOnObject(g5,g-1)
    c: Distance(g-1,g5) = 10
FEATURE [PartDesign::Pad] Pad202
  Length = 5
  Length2 = 100
  Midplane = true
  Profile = -> Sketch367
  Refine = true
  Type = 0
FEATURE [PartDesign::Body] Body096
  Group = -> [Sketch367,Pad202]
  Origin = -> Origin108
  Placement = pos=(74,-101,-211) rot=(0,0,1;0rad)
  Tip = -> Pad202
FEATURE [App::DocumentObjectGroup] Group003  label="Non 3D prited"
  Group = -> [Body001,Body002,Body003,Body011,Body013,Body014,Body020,Body024,Body025,Body050,Body051,Body062,Body063,Part009,Part010,Part011,Body095,Body096]
FEATURE [Sketcher::SketchObject] Sketch368
  MapMode = 5
  Placement = pos=(0,0,0) rot=(1,0,0;1.5708rad)
  Support = -> [XZ_Plane109]
  sketch-geometry (9):
    g0: LineSegment StartX=-44 StartY=-14 StartZ=0 EndX=-4 EndY=-14 EndZ=0
    g1: LineSegment StartX=-4 StartY=-14 StartZ=0 EndX=-4 EndY=7 EndZ=0
    g2: LineSegment StartX=-4 StartY=7 StartZ=0 EndX=-44 EndY=7 EndZ=0
    g3: LineSegment StartX=-44 StartY=7 StartZ=0 EndX=-44 EndY=-14 EndZ=0
    g4: LineSegment StartX=-43 StartY=6 StartZ=0 EndX=-5 EndY=6 EndZ=0
    g5: LineSegment StartX=-5 StartY=6 StartZ=0 EndX=-5 EndY=-13 EndZ=0
    g6: LineSegment StartX=-5 StartY=-13 StartZ=0 EndX=-43 EndY=-13 EndZ=0
    g7: LineSegment StartX=-43 StartY=-13 StartZ=0 EndX=-43 EndY=6 EndZ=0
    g8: GeomPoint X=-24 Y=-3.5 Z=0
  constraints (24):
    c: Coincident(g0,g1)
    c: Coincident(g1,g2)
    c: Coincident(g2,g3)
    c: Coincident(g3,g0)
    c: Horizontal(g0)
    c: Horizontal(g2)
    c: Vertical(g1)
    c: Vertical(g3)
    c: Coincident(g4,g5)
    c: Coincident(g5,g6)
    c: Coincident(g6,g7)
    c: Coincident(g7,g4)
    c: Horizontal(g4)
    c: Horizontal(g6)
    c: Vertical(g5)
    c: Vertical(g7)
    c: Symmetric(g4,g5,g8)
    c: Symmetric(g0,g2,g8)
    c: DistanceX(g4,g1) = 1
    c: DistanceY(g4,g1) = 1
    c: DistanceX(g6) = -43
    c: DistanceY(g6) = -13
    c: Distance(g3) = 21
    c: Distance(g2) = 40
FEATURE [PartDesign::Pad] Pad203
  Length = 110
  Length2 = 100
  Midplane = true
  Placement = pos=(0,0,0) rot=(1,0,0;1.5708rad)
  Profile = -> Sketch368
  Refine = true
  Type = 0
FEATURE [Sketcher::SketchObject] Sketch369
  ExternalGeometry = -> [Pad203]
  MapMode = 5
  Placement = pos=(0,55,1.21e-14) rot=(-1,0,0;1.5708rad)
  Support = -> [Pad203]
  sketch-geometry (3):
    g0: LineSegment StartX=-14 StartY=14 StartZ=0 EndX=-4 EndY=6 EndZ=0
    g1: LineSegment StartX=-4 StartY=6 StartZ=0 EndX=-4 EndY=14 EndZ=0
    g2: LineSegment StartX=-4 StartY=14 StartZ=0 EndX=-14 EndY=14 EndZ=0
  constraints (8):
    c: Coincident(g0,g1)
    c: Vertical(g1)
    c: Coincident(g1,g2)
    c: Coincident(g2,g0)
    c: Horizontal(g2)
    c: Coincident(g1,g-3)
    c: Distance(g2) = 10
    c: Distance(g1) = 8
FEATURE [PartDesign::Pocket] Pocket155
  BaseFeature = -> Pad203
  Length = 26
  Length2 = 100
  Placement = pos=(0,0,0) rot=(1,0,0;1.5708rad)
  Profile = -> Sketch369
  Refine = true
  Type = 1
FEATURE [Sketcher::SketchObject] Sketch370
  ExternalGeometry = -> [Pocket155]
  MapMode = 5
  Placement = pos=(1.36585,0,-1.70732) rot=(0.943628,0,0.331007;3.14159rad)
  Support = -> [Pocket155]
  sketch-geometry (4):
    g0: LineSegment StartX=-19.6779 StartY=55 StartZ=0 EndX=-6.87165 EndY=55 EndZ=0
    g1: LineSegment StartX=-6.87165 StartY=55 StartZ=0 EndX=-6.87165 EndY=-55 EndZ=0
    g2: LineSegment StartX=-6.87165 StartY=-55 StartZ=0 EndX=-19.6779 EndY=-55 EndZ=0
    g3: LineSegment StartX=-19.6779 StartY=-55 StartZ=0 EndX=-19.6779 EndY=55 EndZ=0
  constraints (10):
    c: Coincident(g0,g1)
    c: Coincident(g1,g2)
    c: Coincident(g2,g3)
    c: Coincident(g3,g0)
    c: Horizontal(g0)
    c: Horizontal(g2)
    c: Vertical(g1)
    c: Vertical(g3)
    c: Coincident(g0,g-4)
    c: Coincident(g1,g-3)
FEATURE [PartDesign::Pad] Pad204
  BaseFeature = -> Pocket155
  Length = 1
  Length2 = 100
  Placement = pos=(0,0,0) rot=(1,0,0;1.5708rad)
  Profile = -> Sketch370
  Refine = true
  Reversed = true
  Type = 0
FEATURE [Sketcher::SketchObject] Sketch371
  ExternalGeometry = -> [Pad204]
  MapMode = 5
  Placement = pos=(-3.3e-15,55,5.5e-15) rot=(-1,0,0;1.5708rad)
  Support = -> [Pad204]
  sketch-geometry (3):
    g0: LineSegment StartX=-44 StartY=-7 StartZ=0 EndX=-34 EndY=-7 EndZ=0
    g1: LineSegment StartX=-34 StartY=-7 StartZ=0 EndX=-44 EndY=1 EndZ=0
    g2: LineSegment StartX=-44 StartY=1 StartZ=0 EndX=-44 EndY=-7 EndZ=0
  constraints (8):
    c: Coincident(g-3,g0)
    c: Coincident(g0,g1)
    c: Coincident(g1,g2)
    c: Coincident(g2,g0)
    c: Vertical(g2)
    c: Horizontal(g0)
    c: Distance(g0) = 10
    c: Distance(g2) = 8
FEATURE [PartDesign::Pocket] Pocket156
  BaseFeature = -> Pad204
  Length = 5
  Length2 = 100
  Placement = pos=(0,0,0) rot=(1,0,0;1.5708rad)
  Profile = -> Sketch371
  Refine = true
  Type = 1
FEATURE [Sketcher::SketchObject] Sketch372
  ExternalGeometry = -> [Pocket156]
  MapMode = 5
  Placement = pos=(-16.6829,-1.1e-15,20.8537) rot=(-0.331007,0,0.943628;3.14159rad)
  Support = -> [Pocket156]
  sketch-geometry (4):
    g0: LineSegment StartX=22.1767 StartY=55 StartZ=0 EndX=34.9829 EndY=55 EndZ=0
    g1: LineSegment StartX=34.9829 StartY=55 StartZ=0 EndX=34.9829 EndY=-55 EndZ=0
    g2: LineSegment StartX=34.9829 StartY=-55 StartZ=0 EndX=22.1767 EndY=-55 EndZ=0
    g3: LineSegment StartX=22.1767 StartY=-55 StartZ=0 EndX=22.1767 EndY=55 EndZ=0
  constraints (10):
    c: Coincident(g0,g1)
    c: Coincident(g1,g2)
    c: Coincident(g2,g3)
    c: Coincident(g3,g0)
    c: Horizontal(g0)
    c: Horizontal(g2)
    c: Vertical(g1)
    c: Vertical(g3)
    c: Coincident(g0,g-3)
    c: Coincident(g1,g-4)
FEATURE [PartDesign::Pad] Pad205
  BaseFeature = -> Pocket156
  Length = 1
  Length2 = 100
  Placement = pos=(0,0,0) rot=(1,0,0;1.5708rad)
  Profile = -> Sketch372
  Refine = true
  Reversed = true
  Type = 0
FEATURE [Sketcher::SketchObject] Sketch373
  ExternalGeometry = -> [Pad205]
  MapMode = 5
  Placement = pos=(0,0,7) rot=(0,0,1;3.14159rad)
  Support = -> [Pad205]
  sketch-geometry (6):
    g0: LineSegment StartX=4 StartY=55 StartZ=0 EndX=12 EndY=55 EndZ=0
    g1: LineSegment StartX=12 StartY=55 StartZ=0 EndX=4 EndY=45 EndZ=0
    g2: LineSegment StartX=4 StartY=45 StartZ=0 EndX=4 EndY=55 EndZ=0
    g3: LineSegment StartX=4 StartY=-55 StartZ=0 EndX=12 EndY=-55 EndZ=0
    g4: LineSegment StartX=12 StartY=-55 StartZ=0 EndX=4 EndY=-45 EndZ=0
    g5: LineSegment StartX=4 StartY=-45 StartZ=0 EndX=4 EndY=-55 EndZ=0
  constraints (16):
    c: Coincident(g-3,g0)
    c: Horizontal(g0)
    c: Coincident(g0,g1)
    c: Coincident(g1,g2)
    c: Coincident(g2,g0)
    c: Coincident(g-3,g3)
    c: Horizontal(g3)
    c: Coincident(g3,g4)
    c: Coincident(g4,g5)
    c: Coincident(g5,g3)
    c: Vertical(g5)
    c: Vertical(g2)
    c: Equal(g2,g5)
    c: Equal(g3,g0)
    c: Distance(g2) = 10
    c: Distance(g0) = 8
FEATURE [PartDesign::Pocket] Pocket157
  BaseFeature = -> Pad205
  Length = 5
  Length2 = 100
  Placement = pos=(0,0,0) rot=(1,0,0;1.5708rad)
  Profile = -> Sketch373
  Refine = true
  Type = 1
FEATURE [Sketcher::SketchObject] Sketch374
  ExternalGeometry = -> [Pocket157]
  MapMode = 5
  Placement = pos=(0,0,-14) rot=(1,0,0;3.14159rad)
  Support = -> [Pocket157]
  sketch-geometry (4):
    g0: LineSegment StartX=-43 StartY=55 StartZ=0 EndX=-42.6 EndY=55 EndZ=0
    g1: LineSegment StartX=-42.6 StartY=55 StartZ=0 EndX=-42.6 EndY=-55 EndZ=0
    g2: LineSegment StartX=-42.6 StartY=-55 StartZ=0 EndX=-43 EndY=-55 EndZ=0
    g3: LineSegment StartX=-43 StartY=-55 StartZ=0 EndX=-43 EndY=55 EndZ=0
  constraints (12):
    c: Coincident(g0,g1)
    c: Coincident(g1,g2)
    c: Coincident(g2,g3)
    c: Coincident(g3,g0)
    c: Horizontal(g0)
    c: Horizontal(g2)
    c: Vertical(g1)
    c: Vertical(g3)
    c: PointOnObject(g0,g-3)
    c: PointOnObject(g1,g-4)
    c: Distance(g2,g-4) = 1
    c: Distance(g2) = 0.4
FEATURE [PartDesign::Pocket] Pocket158
  BaseFeature = -> Pocket157
  Length = 5
  Length2 = 100
  Placement = pos=(0,0,0) rot=(1,0,0;1.5708rad)
  Profile = -> Sketch374
  Refine = true
  Type = 2
FEATURE [PartDesign::Body] Body097
  Group = -> [Sketch368,Pad203,Sketch369,Pocket155,Sketch370,Pad204,Sketch371,Pocket156,Sketch372,Pad205,Sketch373,Pocket157,Sketch374,Pocket158]
  Origin = -> Origin109
  Placement = pos=(74,-101,-211) rot=(0,0,1;0rad)
  Tip = -> Pocket158
FEATURE [Sketcher::SketchObject] Sketch023
  MapMode = 5
  Support = -> [XY_Plane005]
  expr: Constraints[2] = 11.8 + 4
  sketch-geometry (2):
    g0: Circle CenterX=0 CenterY=0 CenterZ=0 NormalX=0 NormalY=0 NormalZ=1 AngleXU=0 Radius=7.9
    g1: Circle CenterX=0 CenterY=0 CenterZ=0 NormalX=0 NormalY=0 NormalZ=1 AngleXU=0 Radius=2.55
  constraints (4):
    c: Coincident(g0,g-1)
    c: Coincident(g1,g0)
    c: Diameter(g0) = 15.8
    c: Diameter(g1) = 5.1
FEATURE [PartDesign::Pad] Pad008
  Length = 5
  Length2 = 100
  Profile = -> Sketch023
  Refine = true
  Type = 0
FEATURE [Sketcher::SketchObject] Sketch024
  ExternalGeometry = -> [Pad008]
  MapMode = 5
  Placement = pos=(0,0,5) rot=(0,0,1;0rad)
  Support = -> [Pad008]
  expr: Constraints[16] = 360 / 20
  expr: Constraints[10] = 5.1 / 2 - 0.5 / 2
  sketch-geometry (8):
    g0: ArcOfCircle CenterX=2.3 CenterY=0 CenterZ=0 NormalX=0 NormalY=0 NormalZ=1 AngleXU=0 Radius=0.2 StartAngle=1.57427 EndAngle=4.70891
    g1: LineSegment StartX=2.2993 StartY=0.199999 StartZ=0 EndX=2.3193 EndY=0.200068 EndZ=0
    g2: LineSegment StartX=2.2993 StartY=-0.199999 StartZ=0 EndX=2.3193 EndY=-0.200068 EndZ=0
    g3: ArcOfCircle CenterX=2.31861 CenterY=0.400067 CenterZ=0 NormalX=0 NormalY=0 NormalZ=1 AngleXU=0 Radius=0.2 StartAngle=4.71587 EndAngle=6.27739
    g4: ArcOfCircle CenterX=2.31861 CenterY=-0.400067 CenterZ=0 NormalX=0 NormalY=0 NormalZ=1 AngleXU=0 Radius=0.2 StartAngle=0.00579632 EndAngle=1.56732
    g5: LineSegment [constr] StartX=0 StartY=0 StartZ=0 EndX=2.51861 EndY=0.398908 EndZ=0
    g6: LineSegment [constr] StartX=0 StartY=0 StartZ=0 EndX=2.51861 EndY=-0.398908 EndZ=0
    g7: ArcOfCircle CenterX=0 CenterY=0 CenterZ=0 NormalX=0 NormalY=0 NormalZ=1 AngleXU=0 Radius=2.55 StartAngle=6.12611 EndAngle=6.44026
  constraints (21):
    c: PointOnObject(g0,g-1)
    c: Vertical(g0,g0)
    c: Diameter(g0) = 0.4
    c: Tangent(g2,g0) = -1.5708
    c: Tangent(g1,g0) = 1.5708
    c: PointOnObject(g4,g-3)
    c: Tangent(g4,g2) = 1.5708
    c: Tangent(g3,g1) = -1.5708
    c: Equal(g3,g0)
    c: Equal(g4,g0)
    c: DistanceX(g0) = 2.3
    c: Coincident(g5,g-1)
    c: Coincident(g5,g3)
    c: Coincident(g6,g-1)
    c: Coincident(g6,g4)
    c: Vertical(g4,g3)
    c: Angle(g6,g5) = 0.314159
    c: Coincident(g7,g-1)
    c: Coincident(g7,g3)
    c: Coincident(g7,g4)
    c: Distance(g1) = 0.02
FEATURE [PartDesign::Pad] Pad009
  BaseFeature = -> Pad008
  Length = 10
  Length2 = 100
  Profile = -> Sketch024
  Refine = true
  Reversed = true
  Type = 3
  UpToFace = -> Pad008 [Face3]
FEATURE [PartDesign::PolarPattern] PolarPattern002
  Angle = 360
  Axis = -> Sketch024 [N_Axis]
  BaseFeature = -> Pad009
  Occurrences = 20
  Originals = -> [Pad009]
  Refine = true
FEATURE [Sketcher::SketchObject] Sketch025
  ExternalGeometry = -> [PolarPattern002]
  MapMode = 5
  Placement = pos=(0,0,5) rot=(0,0,1;0rad)
  Support = -> [PolarPattern002]
  sketch-geometry (2):
    g0: Circle CenterX=0 CenterY=0 CenterZ=0 NormalX=0 NormalY=0 NormalZ=1 AngleXU=0 Radius=1.3
    g1: Circle CenterX=0 CenterY=0 CenterZ=0 NormalX=0 NormalY=0 NormalZ=1 AngleXU=0 Radius=7.9
  constraints (4):
    c: Coincident(g0,g-1)
    c: Diameter(g0) = 2.6
    c: Coincident(g1,g0)
    c: Equal(g-3,g1)
FEATURE [PartDesign::Pad] Pad010
  BaseFeature = -> PolarPattern002
  Length = 1
  Length2 = 100
  Profile = -> Sketch025
  Refine = true
  Type = 0
FEATURE [PartDesign::Plane] DatumPlane003
  AttachmentOffset = pos=(0,0,-12.6) rot=(0,0,1;0rad)
  Length = 61.7473
  MapMode = 5
  Placement = pos=(-12.6,2.8e-15,-2.8e-15) rot=(0.57735,0.57735,0.57735;2.0944rad)
  ResizeMode = 0
  Support = -> [YZ_Plane005]
  Width = 80.7473
FEATURE [Sketcher::SketchObject] Sketch026
  ExternalGeometry = -> [Pad010]
  MapMode = 5
  Placement = pos=(-12.6,2.8e-15,-2.8e-15) rot=(0.57735,0.57735,0.57735;2.0944rad)
  Support = -> [DatumPlane003]
  sketch-geometry (4):
    g0: LineSegment StartX=-7.9 StartY=6 StartZ=0 EndX=7.9 EndY=6 EndZ=0
    g1: LineSegment StartX=7.9 StartY=6 StartZ=0 EndX=7.9 EndY=0 EndZ=0
    g2: LineSegment StartX=7.9 StartY=0 StartZ=0 EndX=-7.9 EndY=0 EndZ=0
    g3: LineSegment StartX=-7.9 StartY=0 StartZ=0 EndX=-7.9 EndY=6 EndZ=0
  constraints (10):
    c: Coincident(g0,g1)
    c: Coincident(g1,g2)
    c: Coincident(g2,g3)
    c: Coincident(g3,g0)
    c: Horizontal(g0)
    c: Horizontal(g2)
    c: Vertical(g1)
    c: Vertical(g3)
    c: Symmetric(g2,g1,g-1)
    c: Coincident(g0,g-3)
FEATURE [PartDesign::Pad] Pad011
  BaseFeature = -> Pad010
  Length = 10
  Length2 = 100
  Profile = -> Sketch026
  Refine = true
  Type = 2
FEATURE [Sketcher::SketchObject] Sketch027
  MapMode = 5
  Placement = pos=(-12.6,0,0) rot=(0.57735,-0.57735,-0.57735;2.0944rad)
  Support = -> [Pad011]
  sketch-geometry (4):
    g0: LineSegment StartX=-8 StartY=0 StartZ=0 EndX=8 EndY=0 EndZ=0
    g1: LineSegment StartX=8 StartY=0 StartZ=0 EndX=8 EndY=44 EndZ=0
    g2: LineSegment StartX=8 StartY=44 StartZ=0 EndX=-8 EndY=44 EndZ=0
    g3: LineSegment StartX=-8 StartY=44 StartZ=0 EndX=-8 EndY=0 EndZ=0
  constraints (11):
    c: Coincident(g0,g1)
    c: Coincident(g1,g2)
    c: Coincident(g2,g3)
    c: Coincident(g3,g0)
    c: Horizontal(g0)
    c: Horizontal(g2)
    c: Vertical(g1)
    c: Vertical(g3)
    c: Symmetric(g0,g0,g-1)
    c: Distance(g2) = 16
    c: Distance(g1) = 44
FEATURE [PartDesign::Pad] Pad012
  BaseFeature = -> Pad011
  Length = 7
  Length2 = 100
  Profile = -> Sketch027
  Refine = true
  Type = 0
FEATURE [Sketcher::SketchObject] Sketch033
  MapMode = 5
  Placement = pos=(0,0,-1e-15) rot=(1,0,0;3.14159rad)
  sketch-geometry (1):
    g0: Circle CenterX=0 CenterY=0 CenterZ=0 NormalX=0 NormalY=0 NormalZ=1 AngleXU=0 Radius=2.55
  constraints (1):
    c: Coincident(g0,g-1)
FEATURE [Sketcher::SketchObject] Sketch035
  MapMode = 5
  Placement = pos=(0,0,0) rot=(1,0,0;1.5708rad)
  Support = -> [XZ_Plane005]
  sketch-geometry (4):
    g0: LineSegment StartX=1.90556 StartY=5 StartZ=0 EndX=2.55 EndY=4.275 EndZ=0
    g1: GeomPoint X=2.15 Y=4.725 Z=0
    g2: LineSegment StartX=2.55 StartY=4.275 StartZ=0 EndX=2.55 EndY=5 EndZ=0
    g3: LineSegment StartX=1.90556 StartY=5 StartZ=0 EndX=2.55 EndY=5 EndZ=0
  constraints (9):
    c: PointOnObject(g1,g0)
    c: DistanceY(g0,g1) = 0.45
    c: DistanceY(g1,g0) = 0.275
    c: DistanceX(g1,g0) = 0.4
    c: Coincident(g2,g0)
    c: Vertical(g2)
    c: Coincident(g3,g0)
    c: Coincident(g3,g2)
    c: Horizontal(g3)
FEATURE [PartDesign::Revolution] Revolution001
  Angle = 360
  Axis = (0,-2e-16,1)
  Base = (0,0,0)
  BaseFeature = -> Pad012
  Profile = -> Sketch035
  ReferenceAxis = -> Sketch035 [V_Axis]
  Refine = true
FEATURE [PartDesign::Pocket] Pocket010
  BaseFeature = -> Revolution001
  Length = 2
  Length2 = 100
  Profile = -> Sketch033
  Refine = true
  Type = 0
FEATURE [Sketcher::SketchObject] Sketch036
  MapMode = 5
  Placement = pos=(-19.6,0,0) rot=(0.57735,-0.57735,-0.57735;2.0944rad)
  Support = -> [Pad012]
  sketch-geometry (2):
    g0: ArcOfCircle CenterX=0 CenterY=20 CenterZ=0 NormalX=0 NormalY=0 NormalZ=1 AngleXU=0 Radius=6.3 StartAngle=2.0944 EndAngle=7.33038
    g1: ArcOfCircle CenterX=0 CenterY=25.456 CenterZ=0 NormalX=0 NormalY=0 NormalZ=1 AngleXU=0 Radius=3.15 StartAngle=0 EndAngle=3.14159
  constraints (8):
    c: PointOnObject(g1,g-2)
    c: Coincident(g1,g0)
    c: Coincident(g1,g0)
    c: Diameter(g0) = 12.6
    c: Diameter(g1) = 6.3
    c: PointOnObject(g0,g-2)
    c: Horizontal(g1,g0)
    c: DistanceY(g-1,g0) = 20
FEATURE [Sketcher::SketchObject] Sketch039
  MapMode = 5
  Placement = pos=(0,8,0) rot=(0,0.707107,0.707107;3.14159rad)
  sketch-geometry (3):
    g0: LineSegment StartX=20 StartY=21 StartZ=0 EndX=17.5 EndY=44 EndZ=0
    g1: LineSegment StartX=20 StartY=44 StartZ=0 EndX=17.5 EndY=44 EndZ=0
    g2: LineSegment StartX=20 StartY=44 StartZ=0 EndX=20 EndY=21 EndZ=0
  constraints (7):
    c: Coincident(g1,g0)
    c: Horizontal(g1)
    c: Coincident(g2,g1)
    c: Coincident(g2,g0)
    c: Distance(g2) = 23
    c: Vertical(g2)
    c: Distance(g1) = 2.5
FEATURE [Sketcher::SketchObject] Sketch034
  MapMode = 5
  Placement = pos=(-14.5,0,0) rot=(0.57735,0.57735,0.57735;2.0944rad)
  sketch-geometry (10):
    g0: Circle CenterX=4.5 CenterY=35 CenterZ=0 NormalX=0 NormalY=0 NormalZ=1 AngleXU=0 Radius=1
    g1: Circle CenterX=-4.5 CenterY=35 CenterZ=0 NormalX=0 NormalY=0 NormalZ=1 AngleXU=0 Radius=1
    g2: Circle CenterX=4.5 CenterY=15 CenterZ=0 NormalX=0 NormalY=0 NormalZ=1 AngleXU=0 Radius=1
    g3: Circle CenterX=-4.5 CenterY=15 CenterZ=0 NormalX=0 NormalY=0 NormalZ=1 AngleXU=0 Radius=1
    g4: LineSegment [constr] StartX=-4.5 StartY=35 StartZ=0 EndX=4.5 EndY=35 EndZ=0
    g5: LineSegment [constr] StartX=-4.5 StartY=35 StartZ=0 EndX=-4.5 EndY=15 EndZ=0
    g6: LineSegment [constr] StartX=-4.5 StartY=15 StartZ=0 EndX=4.5 EndY=15 EndZ=0
    g7: LineSegment [constr] StartX=4.5 StartY=35 StartZ=0 EndX=4.5 EndY=15 EndZ=0
    g8: LineSegment [constr] StartX=-4.5 StartY=35 StartZ=0 EndX=0 EndY=25 EndZ=0
    g9: LineSegment [constr] StartX=0 StartY=25 StartZ=0 EndX=4.5 EndY=15 EndZ=0
  constraints (25):
    c: Diameter(g0) = 2
    c: Coincident(g4,g1)
    c: Coincident(g4,g0)
    c: Horizontal(g4)
    c: Coincident(g5,g1)
    c: Coincident(g5,g3)
    c: Vertical(g5)
    c: Coincident(g6,g3)
    c: Coincident(g6,g2)
    c: Horizontal(g6)
    c: Coincident(g7,g0)
    c: Coincident(g7,g2)
    c: Vertical(g7)
    c: Coincident(g9,g8)
    c: Equal(g8,g9)
    c: Parallel(g8,g9)
    c: Symmetric(g0,g3,g8)
    c: Distance(g5) = 20
    c: Distance(g4) = 9
    c: Equal(g1,g3)
    c: Equal(g3,g2)
    c: Equal(g2,g0)
    c: PointOnObject(g8,g-2)
    c: Coincident(g9,g2)
    c: DistanceY(g8) = 25
FEATURE [PartDesign::Pocket] Pocket011
  BaseFeature = -> Pocket010
  Length = 5
  Length2 = 100
  Profile = -> Sketch036
  Refine = true
  Type = 1
FEATURE [Sketcher::SketchObject] Sketch037
  MapMode = 5
  Placement = pos=(-12.6,0,0) rot=(0.57735,0.57735,0.57735;2.0944rad)
  Support = -> [Pocket011]
  sketch-geometry (4):
    g0: LineSegment StartX=-6.405 StartY=37.4 StartZ=0 EndX=6.405 EndY=37.4 EndZ=0
    g1: LineSegment StartX=6.405 StartY=37.4 StartZ=0 EndX=6.405 EndY=13.4 EndZ=0
    g2: LineSegment StartX=6.405 StartY=13.4 StartZ=0 EndX=-6.405 EndY=13.4 EndZ=0
    g3: LineSegment StartX=-6.405 StartY=13.4 StartZ=0 EndX=-6.405 EndY=37.4 EndZ=0
  constraints (11):
    c: Coincident(g0,g1)
    c: Coincident(g1,g2)
    c: Coincident(g2,g3)
    c: Coincident(g3,g0)
    c: Horizontal(g2)
    c: Vertical(g1)
    c: Vertical(g3)
    c: Symmetric(g0,g0,g-2)
    c: Distance(g0) = 12.81
    c: Distance(g1) = 24
    c: DistanceY(g2) = 13.4
FEATURE [PartDesign::Pocket] Pocket012
  BaseFeature = -> Pocket011
  Length = 1.9
  Length2 = 100
  Profile = -> Sketch037
  Refine = true
  Type = 0
FEATURE [Sketcher::SketchObject] Sketch038
  MapMode = 5
  Placement = pos=(-12.6,0,0) rot=(0.57735,0.57735,0.57735;2.0944rad)
  Support = -> [Pocket012]
  sketch-geometry (2):
    g0: Circle CenterX=0 CenterY=39.5 CenterZ=0 NormalX=0 NormalY=0 NormalZ=1 AngleXU=0 Radius=1
    g1: Circle CenterX=0 CenterY=11.1 CenterZ=0 NormalX=0 NormalY=0 NormalZ=1 AngleXU=0 Radius=1
  constraints (6):
    c: PointOnObject(g0,g-2)
    c: PointOnObject(g1,g-2)
    c: Diameter(g0) = 2
    c: Equal(g1,g0)
    c: DistanceY(g1) = 11.1
    c: DistanceY(g1,g0) = 28.4
FEATURE [Sketcher::SketchObject] Sketch040
  MapMode = 5
  Placement = pos=(-14.5,0,0) rot=(0.57735,0.57735,0.57735;2.0944rad)
  sketch-geometry (4):
    g0: ArcOfCircle CenterX=0 CenterY=26.2701 CenterZ=0 NormalX=0 NormalY=0 NormalZ=1 AngleXU=0 Radius=3.16837 StartAngle=6.17546 EndAngle=9.5325
    g1: LineSegment StartX=-3.15 StartY=25.9294 StartZ=0 EndX=-3.15 EndY=25.456 EndZ=0
    g2: LineSegment StartX=-3.15 StartY=25.456 StartZ=0 EndX=3.15 EndY=25.5294 EndZ=0
    g3: LineSegment StartX=3.15 StartY=25.9294 StartZ=0 EndX=3.15 EndY=25.5294 EndZ=0
  constraints (9):
    c: PointOnObject(g0,g-2)
    c: Horizontal(g0,g0)
    c: Coincident(g1,g0)
    c: Vertical(g1)
    c: Coincident(g2,g1)
    c: Coincident(g3,g0)
    c: Coincident(g3,g2)
    c: Vertical(g3)
    c: Distance(g3) = 0.4
FEATURE [PartDesign::Pocket] Pocket014
  BaseFeature = -> Pocket012
  Length = 5
  Length2 = 100
  Profile = -> Sketch039
  Refine = true
  Type = 1
FEATURE [PartDesign::Pocket] Pocket015
  BaseFeature = -> Pocket014
  Length = 5
  Length2 = 100
  Profile = -> Sketch034
  Refine = true
  Type = 1
FEATURE [PartDesign::Pocket] Pocket016
  BaseFeature = -> Pocket015
  Length = 5
  Length2 = 100
  Profile = -> Sketch040
  Refine = true
  Type = 1
FEATURE [Sketcher::SketchObject] Sketch041
  ExternalGeometry = -> [Pocket016]
  MapMode = 5
  Placement = pos=(0,0,-1e-15) rot=(1,0,0;3.14159rad)
  sketch-geometry (3):
    g0: LineSegment StartX=-12.6 StartY=8 StartZ=0 EndX=-12.6 EndY=7.9 EndZ=0
    g1: LineSegment StartX=-12.6 StartY=8 StartZ=0 EndX=0.0625674 EndY=7.89975 EndZ=0
    g2: LineSegment StartX=-12.6 StartY=7.9 StartZ=0 EndX=0.0625674 EndY=7.89975 EndZ=0
  constraints (7):
    c: Coincident(g1,g0)
    c: Coincident(g2,g0)
    c: Coincident(g2,g1)
    c: Coincident(g0,g-4)
    c: Coincident(g0,g-4)
    c: PointOnObject(g1,g-3)
    c: Tangent(g1,g-3)
FEATURE [PartDesign::Pad] Pad013
  BaseFeature = -> Pocket016
  Length = 10
  Length2 = 100
  Profile = -> Sketch041
  Refine = true
  Reversed = true
  Type = 3
  UpToFace = -> Pocket016 [Face104]
FEATURE [PartDesign::Mirrored] Mirrored
  BaseFeature = -> Pad013
  MirrorPlane = -> Sketch041 [H_Axis]
  Originals = -> [Pad013]
  Refine = true
FEATURE [PartDesign::Fillet] Fillet005
  Base = -> Mirrored [Edge2]
  BaseFeature = -> Mirrored
  Radius = 7
  Refine = true
  SupportTransform = false
FEATURE [PartDesign::Pocket] Pocket017
  BaseFeature = -> Fillet005
  Length = 5
  Length2 = 5
  Midplane = true
  Profile = -> Sketch038
  Refine = true
  Type = 4
FEATURE [Sketcher::SketchObject] Sketch042
  ExternalGeometry = -> [Pocket017]
  MapMode = 5
  Placement = pos=(-12.6,0,0) rot=(0.57735,0.57735,0.57735;2.0944rad)
  Support = -> [Pocket017]
  sketch-geometry (4):
    g0: LineSegment StartX=-6.405 StartY=13.4 StartZ=0 EndX=6.405 EndY=13.4 EndZ=0
    g1: LineSegment StartX=6.405 StartY=13.4 StartZ=0 EndX=6.405 EndY=8.4 EndZ=0
    g2: LineSegment StartX=6.405 StartY=8.4 StartZ=0 EndX=-6.405 EndY=8.4 EndZ=0
    g3: LineSegment StartX=-6.405 StartY=8.4 StartZ=0 EndX=-6.405 EndY=13.4 EndZ=0
  constraints (10):
    c: Coincident(g0,g1)
    c: Coincident(g1,g2)
    c: Coincident(g2,g3)
    c: Coincident(g3,g0)
    c: Horizontal(g2)
    c: Vertical(g1)
    c: Vertical(g3)
    c: Coincident(g0,g-3)
    c: Coincident(g0,g-3)
    c: Distance(g1) = 5
FEATURE [PartDesign::Pocket] Pocket018
  BaseFeature = -> Pocket017
  Length = 5
  Length2 = 100
  Profile = -> Sketch042
  Refine = true
  Reversed = true
  Type = 1
FEATURE [PartDesign::Fillet] Fillet006
  Base = -> Pocket018 [Edge76]
  BaseFeature = -> Pocket018
  Radius = 3
  Refine = true
  SupportTransform = false
FEATURE [PartDesign::Fillet] Fillet007
  Base = -> Fillet006 [Edge41,Edge43]
  BaseFeature = -> Fillet006
  Radius = 10
  Refine = true
  SupportTransform = false
FEATURE [PartDesign::Fillet] Fillet008
  Base = -> Fillet007 [Edge62,Edge6]
  BaseFeature = -> Fillet007
  Radius = 7
  Refine = true
  SupportTransform = false
FEATURE [Sketcher::SketchObject] Sketch051
  MapMode = 5
  Placement = pos=(0,0,-3e-16) rot=(1,0,0;3.14159rad)
  Support = -> [Fillet008]
  expr: Constraints[1] = 11.8 + 2
  sketch-geometry (1):
    g0: Circle CenterX=0 CenterY=0 CenterZ=0 NormalX=0 NormalY=0 NormalZ=1 AngleXU=0 Radius=6.9
  constraints (2):
    c: Coincident(g0,g-1)
    c: Diameter(g0) = 13.8
FEATURE [PartDesign::Pocket] Pocket023
  BaseFeature = -> Fillet008
  Length = 1.8
  Length2 = 100
  Profile = -> Sketch051
  Refine = true
  Type = 0
FEATURE [Sketcher::SketchObject] Sketch063
  MapMode = 5
  Placement = pos=(-19.6,0,0) rot=(0.57735,-0.57735,-0.57735;2.0944rad)
  Support = -> [Pocket023]
  expr: Constraints[1] = 11.8 + 3
  sketch-geometry (1):
    g0: Circle CenterX=0 CenterY=20 CenterZ=0 NormalX=0 NormalY=0 NormalZ=1 AngleXU=0 Radius=7.4
  constraints (3):
    c: PointOnObject(g0,g-2)
    c: Diameter(g0) = 14.8
    c: DistanceY(g0) = 20
FEATURE [PartDesign::Pocket] Pocket031
  BaseFeature = -> Pocket023
  Length = 1.5
  Length2 = 100
  Profile = -> Sketch063
  Refine = true
  Type = 0
FEATURE [PartDesign::Body] Body005  label="s6Mount"
  Group = -> [Sketch023,Pad008,Sketch024,Pad009,PolarPattern002,Sketch025,Pad010,DatumPlane003,Sketch026,Pad011,Sketch027,Pad012,Sketch033,Sketch035,Revolution001,Pocket010,Sketch036,Sketch037,Sketch038,Sketch039,Sketch034,Pocket011,Pocket012,Sketch040,Pocket014,Pocket015,Pocket016,Sketch041,Pad013,Mirrored,Fillet005,Pocket017,Sketch042,Pocket018,Fillet006,Fillet007,Fillet008,Sketch051,Pocket023,Sketch063,+1 more]
  Origin = -> Origin005
  Placement = pos=(-20,0,-20) rot=(0,1,0;1.5708rad)
  Tip = -> Pocket031
FEATURE [App::DocumentObjectGroup] Group002  label="3D prited"
  Group = -> [Group001,Body004,Body005,Body006,Body007,Body008,Body009,Body010,Body015,Body019,Part__Mirroring,Part__Mirroring001,Part001,Part002,Part003,Part005,Part006,Part__Mirroring006,Body053,Part007,Body076,Body077,Body078,Body072,Body069,Body068,Body086,Body090,Body091,Body092,Body093,Body094,Body097]
